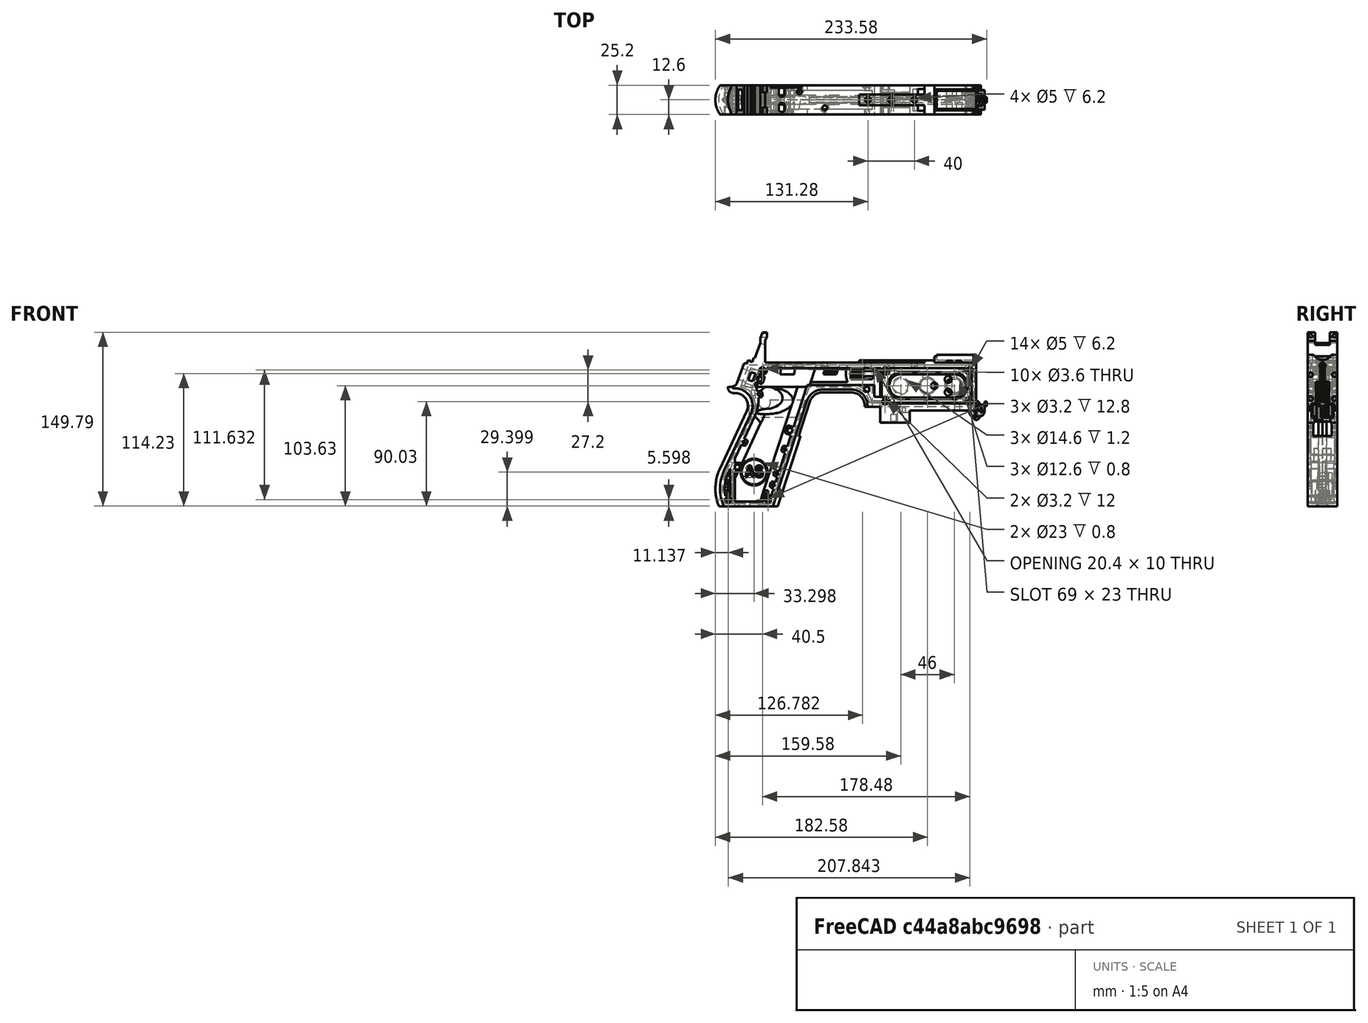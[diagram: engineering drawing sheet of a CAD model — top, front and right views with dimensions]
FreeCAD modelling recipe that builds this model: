
FCSTD DOCUMENT  (FreeCAD 1.0R39319 (Git))
Label: PICON-OF_ver_59
License: All rights reserved
LicenseURL: https://en.wikipedia.org/wiki/All_rights_reserved
objects: Sketcher::SketchObject×126, Part::Extrusion×65, Part::Cut×48, PartDesign::Pad×29, PartDesign::Pocket×21, PartDesign::Chamfer×15, PartDesign::Body×10, PartDesign::Fillet×6, Part::MultiFuse×5, Part::Part2DObjectPython×4, PartDesign::SubtractivePipe×4, PartDesign::SubtractiveLoft×4, PartDesign::Plane×3, PartDesign::SubShapeBinder×2, Part::Sweep×1, PartDesign::ShapeBinder×1, Mesh::Feature×1, PartDesign::Point×1, PartDesign::Groove×1
note: 632 computed .brp shape members not serialized (recipe doc carries the construction recipe); baked Part::Feature solids carry a one-line shape summary decoded from their .brp

FEATURE [Sketcher::SketchObject] Sketch  label="corpo principale"
  ArcFitTolerance = 1e-06
  AttacherType = Attacher::AttachEngine3D
  AttachmentSupport = -> [XZ_Plane]
  FullyConstrained = true
  MakeInternals = false
  MapMode = 5
  Placement = pos=(0,0,0) rot=(1,0,0;1.5708rad)
  sketch-geometry (65):
    g0: LineSegment StartX=0 StartY=0 StartZ=0 EndX=-57.2 EndY=0 EndZ=0
    g1: LineSegment StartX=-57.2 StartY=0 StartZ=0 EndX=-57.2 EndY=-10.4 EndZ=0
    g2: LineSegment StartX=-57.2 StartY=-10.4 StartZ=0 EndX=-82.8 EndY=-10.4 EndZ=0
    g3: LineSegment StartX=-82.8 StartY=-10.4 StartZ=0 EndX=-82.8 EndY=3.2 EndZ=0
    g4: LineSegment StartX=-82.8 StartY=3.2 StartZ=0 EndX=-93.6 EndY=3.2 EndZ=0
    g5: LineSegment StartX=-93.6 StartY=3.2 StartZ=0 EndX=-93.6 EndY=4 EndZ=0
    g6: LineSegment StartX=-107.6 StartY=18 StartZ=0 EndX=-132.428 EndY=18 EndZ=0
    g7: LineSegment StartX=-145.743 StartY=8.32624 StartZ=0 EndX=-175.232 EndY=-82.4316 EndZ=0
    g8: LineSegment StartX=-175.232 StartY=-82.4316 StartZ=0 EndX=-217.232 EndY=-82.4316 EndZ=0
    g9: LineSegment StartX=-217.232 StartY=-52.1862 StartZ=0 EndX=-193.988 EndY=-2.33927 EndZ=0
    g10: LineSegment StartX=-206.196 StartY=23.0857 StartZ=0 EndX=-199.861 EndY=40.4914 EndZ=0
    g11: LineSegment StartX=-199.861 StartY=40.4914 StartZ=0 EndX=-197.061 EndY=40.4914 EndZ=0
    g12: LineSegment StartX=-197.061 StartY=40.4914 StartZ=0 EndX=-197.061 EndY=42.8914 EndZ=0
    g13: LineSegment StartX=-197.061 StartY=42.8914 StartZ=0 EndX=-194.261 EndY=42.8914 EndZ=0
    g14: LineSegment StartX=-194.261 StartY=42.8914 StartZ=0 EndX=-194.535 EndY=42.1397 EndZ=0
    g15: LineSegment StartX=-194.535 StartY=42.1397 StartZ=0 EndX=-193.031 EndY=41.5924 EndZ=0
    g16: LineSegment StartX=-193.031 StartY=41.5924 StartZ=0 EndX=-191.663 EndY=45.3512 EndZ=0
    g17: LineSegment StartX=-191.663 StartY=45.3512 StartZ=0 EndX=-190.536 EndY=44.9408 EndZ=0
    g18: LineSegment StartX=-190.536 StartY=44.9408 StartZ=0 EndX=-185.747 EndY=58.0965 EndZ=0
    g19: LineSegment StartX=-185.747 StartY=58.0965 StartZ=0 EndX=-185.747 EndY=62.0965 EndZ=0
    g20: LineSegment StartX=-185.747 StartY=62.0965 StartZ=0 EndX=-183.832 EndY=67.3588 EndZ=0
    g21: LineSegment StartX=-183.832 StartY=67.3588 StartZ=0 EndX=-180.232 EndY=67.3588 EndZ=0
    g22: LineSegment StartX=-180.232 StartY=67.3588 StartZ=0 EndX=-180.232 EndY=63.7588 EndZ=0
    g23: LineSegment StartX=-180.232 StartY=63.7588 StartZ=0 EndX=-181.6 EndY=60 EndZ=0
    g24: LineSegment StartX=-181.6 StartY=60 StartZ=0 EndX=-181.6 EndY=41.2 EndZ=0
    g25: LineSegment StartX=-181.6 StartY=41.2 StartZ=0 EndX=-100.8 EndY=41.2 EndZ=0
    g26: LineSegment StartX=-36 StartY=43.2 StartZ=0 EndX=-36 EndY=41.2 EndZ=0
    g27: LineSegment StartX=0 StartY=48 StartZ=0 EndX=0 EndY=0 EndZ=0
    g28: LineSegment StartX=-209.901 StartY=19.85 StartZ=0 EndX=-209.901 EndY=20.1 EndZ=0
    g29: LineSegment StartX=-208.001 StartY=22 StartZ=0 EndX=-207.747 EndY=22 EndZ=0
    g30: LineSegment StartX=-207.583 StartY=19 StartZ=0 EndX=-209.051 EndY=19 EndZ=0
    g31: ArcOfCircle CenterX=-208.001 CenterY=20.1 CenterZ=0 NormalX=0 NormalY=0 NormalZ=1 AngleXU=0 Radius=1.9 StartAngle=1.5708 EndAngle=3.14159
    g32: GeomPoint [constr] X=-209.901 Y=22 Z=0
    g33: ArcOfCircle CenterX=-209.051 CenterY=19.85 CenterZ=0 NormalX=0 NormalY=0 NormalZ=1 AngleXU=0 Radius=0.85 StartAngle=3.14159 EndAngle=4.71239
    g34: GeomPoint [constr] X=-209.901 Y=19 Z=0
    g35: ArcOfCircle CenterX=-207.747 CenterY=23.65 CenterZ=0 NormalX=0 NormalY=0 NormalZ=1 AngleXU=0 Radius=1.65 StartAngle=4.71239 EndAngle=5.93412
    g36: GeomPoint [constr] X=-206.591 Y=22 Z=0
    g37: LineSegment StartX=-4 StartY=6 StartZ=0 EndX=-4 EndY=36.4 EndZ=0
    g38: LineSegment StartX=-4 StartY=36.4 StartZ=0 EndX=-185.2 EndY=36.4 EndZ=0
    g39: LineSegment StartX=-185.2 StartY=36.4 StartZ=0 EndX=-190.441 EndY=22 EndZ=0
    g40: LineSegment StartX=-214.575 StartY=-78.4316 StartZ=0 EndX=-178.142 EndY=-78.4316 EndZ=0
    g41: LineSegment StartX=-178.142 StartY=-78.4316 StartZ=0 EndX=-145.51 EndY=22 EndZ=0
    g42: LineSegment StartX=-145.51 StartY=22 StartZ=0 EndX=-87.91 EndY=22 EndZ=0
    g43: LineSegment StartX=-87.91 StartY=22 StartZ=0 EndX=-87.91 EndY=11.6 EndZ=0
    g44: LineSegment StartX=-87.91 StartY=11.6 StartZ=0 EndX=-80.11 EndY=11.6 EndZ=0
    g45: LineSegment StartX=-80.11 StartY=11.6 StartZ=0 EndX=-80.11 EndY=6 EndZ=0
    g46: LineSegment StartX=-80.11 StartY=6 StartZ=0 EndX=-4 EndY=6 EndZ=0
    g47: LineSegment StartX=-190.363 StartY=-4.02975 StartZ=0 EndX=-213.607 EndY=-53.8767 EndZ=0
    g48: ArcOfCircle CenterX=-132.428 CenterY=4 CenterZ=0 NormalX=0 NormalY=0 NormalZ=1 AngleXU=0 Radius=14 StartAngle=1.5708 EndAngle=2.82743
    g49: GeomPoint [constr] X=-142.6 Y=18 Z=0
    g50: ArcOfCircle CenterX=-107.6 CenterY=4 CenterZ=0 NormalX=0 NormalY=0 NormalZ=1 AngleXU=0 Radius=14 StartAngle=0 EndAngle=1.5708
    g51: GeomPoint [constr] X=-93.6 Y=18 Z=0
    g52: ArcOfCircle CenterX=-184.801 CenterY=-67.3089 CenterZ=0 NormalX=0 NormalY=0 NormalZ=1 AngleXU=0 Radius=35.7833 StartAngle=2.70526 EndAngle=3.57792
    g53: ArcOfCircle CenterX=-207.583 CenterY=4 CenterZ=0 NormalX=0 NormalY=0 NormalZ=1 AngleXU=0 Radius=15 StartAngle=5.84685 EndAngle=7.85398
    g54: LineSegment [constr] StartX=-213.607 StartY=-53.8767 StartZ=0 EndX=-217.232 EndY=-52.1862 EndZ=0
    g55: ArcOfCircle CenterX=-184.801 CenterY=-67.3089 CenterZ=0 NormalX=0 NormalY=0 NormalZ=1 AngleXU=0 Radius=31.7833 StartAngle=2.70526 EndAngle=3.49911
    g56: ArcOfCircle CenterX=-218.095 CenterY=8.90192 CenterZ=0 NormalX=0 NormalY=0 NormalZ=1 AngleXU=0 Radius=30.5989 StartAngle=5.84685 EndAngle=6.72553
    g57: LineSegment StartX=-44.6 StartY=43.2 StartZ=0 EndX=-36 EndY=43.2 EndZ=0
    g58: LineSegment StartX=-100.8 StartY=41.2 StartZ=0 EndX=-44.6 EndY=41.2 EndZ=0
    g59: LineSegment StartX=-44.6 StartY=41.2 StartZ=0 EndX=-44.6 EndY=43.2 EndZ=0
    g60: LineSegment StartX=-2.4 StartY=48 StartZ=0 EndX=0 EndY=48 EndZ=0
    g61: LineSegment StartX=-36 StartY=41.2 StartZ=0 EndX=-2.4 EndY=41.2 EndZ=0
    g62: LineSegment StartX=-2.4 StartY=41.2 StartZ=0 EndX=-2.4 EndY=48 EndZ=0
    g63: LineSegment [constr] StartX=-181.6 StartY=36.4 StartZ=0 EndX=-152.209 EndY=36.4 EndZ=0
    g64: LineSegment [constr] StartX=-181.6 StartY=36.4 StartZ=0 EndX=-130.41 EndY=36.4 EndZ=0
  constraints (183):
    c: Coincident(g-1,g0)
    c: PointOnObject(g0,g-1)
    c: Coincident(g0,g1)
    c: Vertical(g1)
    c: Coincident(g1,g2)
    c: Horizontal(g2)
    c: Coincident(g2,g3)
    c: Vertical(g3)
    c: Coincident(g3,g4)
    c: Coincident(g4,g5)
    c: Vertical(g5)
    c: Horizontal(g6)
    c: Coincident(g7,g8)
    c: Horizontal(g8)
    c: Coincident(g10,g11)
    c: Horizontal(g11)
    c: Coincident(g11,g12)
    c: Vertical(g12)
    c: Coincident(g12,g13)
    c: Horizontal(g13)
    c: Coincident(g13,g14)
    c: Coincident(g14,g15)
    c: Coincident(g15,g16)
    c: Coincident(g16,g17)
    c: Coincident(g17,g18)
    c: Coincident(g18,g19)
    c: Vertical(g19)
    c: Coincident(g19,g20)
    c: Coincident(g20,g21)
    c: Horizontal(g21)
    c: Coincident(g21,g22)
    c: Vertical(g22)
    c: Coincident(g22,g23)
    c: Coincident(g23,g24)
    c: Vertical(g24)
    c: Coincident(g24,g25)
    c: Horizontal(g25)
    c: Coincident(g57,g26)
    c: Vertical(g26)
    c: Coincident(g26,g61)
    c: PointOnObject(g60,g-2)
    c: Coincident(g60,g27)
    c: Coincident(g27,g0)
    c: DistanceY(g27,g27) = 48
    c: DistanceY(g1,g1) = 10.4
    c: DistanceX(g0,g0) = 57.2
    c: DistanceX(g2,g2) = 25.6
    c: Horizontal(g4)
    c: DistanceY(g3,g3) = 13.6
    c: DistanceX(g4,g4) = 10.8
    c: DistanceY(g5,g51) = 14.8
    c: DistanceX(g49,g51) = 49
    c: Distance(g7,g49) = 105.6
    c: DistanceX(g61,g60) = 36
    c: DistanceX(g25,g25) = 80.8
    c: DistanceY(g24,g24) = 18.8
    c: DistanceY(g22,g22) = 3.6
    c: Distance(g23) = 4
    c: Angle(g-1,g23) = 1.22173
    c: DistanceX(g21,g21) = 3.6
    c: Distance(g20) = 5.6
    c: Angle(g-1,g20) = 1.22173
    c: DistanceY(g19,g19) = 4
    c: Distance(g18) = 14
    c: Angle(g-1,g18) = 1.22173
    c: Distance(g17) = 1.2
    c: Distance(g16) = 4
    c: Angle(g16) = 1.22173
    c: Perpendicular(g18,g17)
    c: Distance(g15) = 1.6
    c: Perpendicular(g16,g15)
    c: Distance(g14) = 0.8
    c: DistanceX(g13,g13) = 2.8
    c: Perpendicular(g15,g14)
    c: DistanceY(g12,g12) = 2.4
    c: DistanceX(g11,g11) = 2.8
    c: Distance(g9) = 55
    c: Angle(g9,g-1) = 2.00713
    c: Horizontal(g29)
    c: Vertical(g28)
    c: Horizontal(g30)
    c: PointOnObject(g32,g29)
    c: PointOnObject(g32,g28)
    c: Tangent(g29,g31) = 1.5708
    c: Tangent(g28,g31) = 1.5708
    c: PointOnObject(g34,g28)
    c: PointOnObject(g34,g30)
    c: Tangent(g28,g33) = 1.5708
    c: Tangent(g30,g33) = 1.5708
    c: PointOnObject(g36,g29)
    c: PointOnObject(g36,g10)
    c: Tangent(g29,g35) = -1.5708
    c: Tangent(g10,g35) = -1.5708
    c: Angle(g-1,g10) = 1.22173
    c: Radius(g35) = 1.65
    c: Vertical(g37)
    c: Coincident(g37,g38)
    c: Horizontal(g38)
    c: Coincident(g38,g39)
    c: Horizontal(g40)
    c: Coincident(g40,g41)
    c: Coincident(g41,g42)
    c: Horizontal(g42)
    c: Coincident(g42,g43)
    c: Vertical(g43)
    c: Coincident(g43,g44)
    c: Horizontal(g44)
    c: Coincident(g44,g45)
    c: Vertical(g45)
    c: Coincident(g45,g46)
    c: Coincident(g46,g37)
    c: Horizontal(g46)
    c: DistanceY(g0,g37) = 6
    c: DistanceX(g37,g0) = 4
    c: DistanceY(g37,g25) = 4.8
    c: DistanceX(g38,g38) = 181.2
    c: DistanceX(g42,g42) = 57.6
    c: DistanceY(g49,g41) = 4
    c: DistanceX(g41,g49) = 2.91
    c: DistanceY(g43,g43) = 10.4
    c: DistanceX(g44,g44) = 7.8
    c: DistanceY(g7,g40) = 4
    c: Distance(g47) = 55
    c: Angle(g-1,g39) = 1.22173
    c: PointOnObject(g49,g7)
    c: PointOnObject(g49,g6)
    c: Tangent(g7,g48) = -1.5708
    c: Tangent(g6,g48) = -1.5708
    c: PointOnObject(g51,g5)
    c: PointOnObject(g51,g6)
    c: Tangent(g5,g50) = -1.5708
    c: Tangent(g6,g50) = -1.5708
    c: Radius(g50) = 14
    c: Radius(g48) = 14
    c: DistanceX(g8,g8) = 42
    c: Angle(g7,g-1) = 1.88496
    c: Parallel(g41,g7)
    c: Parallel(g47,g9)
    c: Coincident(g52,g8)
    c: Tangent(g52,g9) = 1.5708
    c: DistanceX(g9,g8) = 0
    c: Tangent(g53,g9) = -1.5708
    c: Tangent(g53,g30) = -1.5708
    c: Diameter(g53) = 30
    c: DistanceY(g53,g0) = -4
    c: Coincident(g54,g47)
    c: Distance(g54) = 4
    c: Coincident(g54,g9)
    c: Coincident(g55,g40)
    c: Tangent(g55,g47) = -1.5708
    c: Coincident(g52,g55)
    c: Coincident(g56,g39)
    c: Tangent(g56,g47) = 1.5708
    c: Horizontal(g57)
    c: DistanceX(g57,g57) = 8.6
    c: Coincident(g58,g25)
    c: Horizontal(g58)
    c: Coincident(g59,g58)
    c: Vertical(g59)
    c: DistanceY(g58,g57) = 2
    c: DistanceX(g58,g58) = 56.2
    c: Coincident(g59,g57)
    c: DistanceY(g41,g36) = 0
    c: DistanceY(g36,g39) = 0
    c: DistanceY(g28,g28) = 0.25
    c: DistanceX(g30,g36) = 2.46
    c: DistanceX(g28,g29) = 1.9
    c: Coincident(g62,g60)
    c: Horizontal(g60)
    c: DistanceX(g62,g27) = 2.4
    c: Coincident(g61,g62)
    c: DistanceY(g26,g26) = 2
    c: Vertical(g62)
    c: DistanceY(g61,g60) = 6.8
    c: Horizontal(g61)
    c: Distance(g63) = 29.391
    c: PointOnObject(g63,g38)
    c: PointOnObject(g63,g38)
    c: Distance(g64) = 51.19
    c: PointOnObject(g64,g38)
    c: PointOnObject(g64,g38)
    c: DistanceX(g24,g63) = 0
    c: DistanceX(g24,g64) = 0
FEATURE [Part::Extrusion] Extrude  label="Extrude corpo principale"
  Base = -> Sketch
  Dir = (0,-1,2e-16)
  DirMode = 2
  FaceMakerClass = Part::FaceMakerBullseye
  FaceMakerMode = 3
  LengthFwd = 25.2
  LengthRev = 12.6
  Solid = true
  Symmetric = true
FEATURE [Sketcher::SketchObject] Sketch002  label="scavo grilletto"
  ArcFitTolerance = 1e-06
  AttachmentSupport = -> [XZ_Plane]
  ExternalGeometry = -> [Sketch]
  FullyConstrained = true
  MakeInternals = false
  MapMode = 5
  Placement = pos=(0,0,0) rot=(1,0,0;1.5708rad)
  sketch-geometry (4):
    g0: LineSegment StartX=-89.51 StartY=22 StartZ=0 EndX=-152.71 EndY=22 EndZ=0
    g1: LineSegment StartX=-152.71 StartY=22 StartZ=0 EndX=-167.006 EndY=-22 EndZ=0
    g2: LineSegment StartX=-167.006 StartY=-22 StartZ=0 EndX=-89.51 EndY=-22 EndZ=0
    g3: LineSegment StartX=-89.51 StartY=-22 StartZ=0 EndX=-89.51 EndY=22 EndZ=0
  constraints (12):
    c: Horizontal(g0)
    c: Coincident(g0,g1)
    c: Coincident(g1,g2)
    c: Horizontal(g2)
    c: Coincident(g2,g3)
    c: Coincident(g3,g0)
    c: Vertical(g3)
    c: Angle(g1,g0) = 1.88496
    c: DistanceY(g3,g3) = 44
    c: DistanceX(g0,g0) = 63.2
    c: DistanceX(g0,g-3) = 1.6
    c: DistanceY(g-3,g0) = 0
FEATURE [Sketcher::SketchObject] Sketch004  label="traiettoria arrotondamento impugnatura anteriore"
  ArcFitTolerance = 1e-06
  AttachmentSupport = -> [XZ_Plane]
  ExternalGeometry = -> [Sketch]
  FullyConstrained = true
  MakeInternals = false
  MapMode = 5
  Placement = pos=(0,0,0) rot=(1,0,0;1.5708rad)
  sketch-geometry (13):
    g0: LineSegment StartX=-175.232 StartY=-82.4316 StartZ=0 EndX=-145.743 EndY=8.32624 EndZ=0
    g1: LineSegment StartX=-93.6 StartY=3.2 StartZ=0 EndX=-93.6 EndY=4 EndZ=0
    g2: LineSegment StartX=-132.428 StartY=18 StartZ=0 EndX=-107.6 EndY=18 EndZ=0
    g3: ArcOfCircle CenterX=-132.428 CenterY=4 CenterZ=0 NormalX=0 NormalY=0 NormalZ=1 AngleXU=0 Radius=14 StartAngle=1.5708 EndAngle=2.82743
    g4: ArcOfCircle CenterX=-107.6 CenterY=4 CenterZ=0 NormalX=0 NormalY=0 NormalZ=1 AngleXU=0 Radius=14 StartAngle=0 EndAngle=1.5708
    g5: LineSegment StartX=-175.232 StartY=-82.4316 StartZ=0 EndX=-217.232 EndY=-82.4316 EndZ=0
    g6: LineSegment StartX=-217.232 StartY=-52.1862 StartZ=0 EndX=-193.988 EndY=-2.33927 EndZ=0
    g7: LineSegment StartX=-209.051 StartY=19 StartZ=0 EndX=-207.583 EndY=19 EndZ=0
    g8: LineSegment StartX=-209.901 StartY=20.1 StartZ=0 EndX=-209.901 EndY=19.85 EndZ=0
    g9: ArcOfCircle CenterX=-184.801 CenterY=-67.3089 CenterZ=0 NormalX=0 NormalY=0 NormalZ=1 AngleXU=0 Radius=35.7833 StartAngle=2.70526 EndAngle=3.57792
    g10: ArcOfCircle CenterX=-207.583 CenterY=4 CenterZ=0 NormalX=0 NormalY=0 NormalZ=1 AngleXU=0 Radius=15 StartAngle=5.84685 EndAngle=7.85398
    g11: ArcOfCircle CenterX=-209.051 CenterY=19.85 CenterZ=0 NormalX=0 NormalY=0 NormalZ=1 AngleXU=0 Radius=0.85 StartAngle=3.14159 EndAngle=4.71239
    g12: ArcOfCircle CenterX=-208.001 CenterY=20.1 CenterZ=0 NormalX=0 NormalY=0 NormalZ=1 AngleXU=0 Radius=1.9 StartAngle=1.5708 EndAngle=3.14159
  constraints (26):
    c: Coincident(g0,g-3)
    c: Coincident(g0,g-6)
    c: Coincident(g1,g-8)
    c: Coincident(g1,g-7)
    c: Coincident(g2,g-5)
    c: Coincident(g2,g-4)
    c: Coincident(g3,g2)
    c: Tangent(g3,g0) = 1.5708
    c: Coincident(g4,g1)
    c: Tangent(g4,g2) = 1.5708
    c: Coincident(g5,g0)
    c: Coincident(g5,g-9)
    c: Coincident(g6,g-12)
    c: Coincident(g6,g-11)
    c: Coincident(g7,g-15)
    c: Coincident(g7,g-14)
    c: Coincident(g8,g-16)
    c: Coincident(g8,g-17)
    c: Tangent(g9,g6) = 1.5708
    c: Coincident(g9,g5)
    c: Coincident(g10,g7)
    c: Tangent(g10,g6) = -1.5708
    c: Tangent(g11,g7) = -1.5708
    c: Coincident(g11,g8)
    c: Tangent(g12,g8) = -1.5708
    c: Coincident(g12,g-17)
FEATURE [PartDesign::Plane] DatumPlane  label="Piano per disegno arrotondamento impugnatura"
  AttachmentSupport = -> [Sketch]
  Length = 73.6581
  MapMode = 7
  Placement = pos=(-145.743,1.8e-15,8.32624) rot=(0.154555,0.154555,0.97582;1.59527rad)
  ResizeMode = 0
  Width = 303.511
FEATURE [Sketcher::SketchObject] Sketch005  label="forma arrotondamento impugnatura anteriore"
  ArcFitTolerance = 1e-06
  AttachmentSupport = -> [DatumPlane]
  FullyConstrained = true
  MakeInternals = false
  MapMode = 5
  Placement = pos=(-145.743,1.8e-15,8.32624) rot=(0.154555,0.154555,0.97582;1.59527rad)
  sketch-geometry (5):
    g0: GeomPoint [constr] X=0 Y=-4 Z=0
    g1: GeomPoint [constr] X=-12.6 Y=7.1e-15 Z=0
    g2: GeomPoint [constr] X=12.6 Y=4.97e-14 Z=0
    g3: LineSegment StartX=-12.6 StartY=7.1e-15 StartZ=0 EndX=12.6 EndY=4.97e-14 EndZ=0
    g4: ArcOfCircle CenterX=-3.88e-14 CenterY=17.845 CenterZ=0 NormalX=0 NormalY=0 NormalZ=1 AngleXU=0 Radius=21.845 StartAngle=4.09759 EndAngle=5.32718
  constraints (11):
    c: DistanceY(g0,g-1) = 4
    c: DistanceX(g-1,g0) = 0
    c: DistanceX(g1,g-1) = 12.6
    c: DistanceX(g-1,g2) = 12.6
    c: DistanceY(g-1,g2) = 0
    c: DistanceY(g-1,g1) = 0
    c: Coincident(g3,g1)
    c: Coincident(g3,g2)
    c: Coincident(g4,g1)
    c: Coincident(g4,g2)
    c: PointOnObject(g0,g4)
FEATURE [Part::Sweep] Sweep  label="Sweep impugnatura"
  Frenet = true
  Sections = -> [Sketch005]
  Solid = true
  Spine = -> Sketch [Edge32,Edge33,Edge34,Edge35,Edge36,Edge37,Edge38,Edge39,Edge40,Edge41,Edge42,Edge43,Edge44]
  Transition = 1
FEATURE [Sketcher::SketchObject] Sketch008  label="buchi e pulizie varie"
  ArcFitTolerance = 1e-06
  AttachmentSupport = -> [XZ_Plane]
  ExternalGeometry = -> [Sketch]
  FullyConstrained = true
  MakeInternals = false
  MapMode = 5
  Placement = pos=(0,0,0) rot=(1,0,0;1.5708rad)
  sketch-geometry (26):
    g0: LineSegment StartX=-96.278 StartY=20.155 StartZ=0 EndX=-92.278 EndY=20.155 EndZ=0
    g1: LineSegment StartX=-92.278 StartY=20.155 StartZ=0 EndX=-92.278 EndY=16.155 EndZ=0
    g2: LineSegment StartX=-92.278 StartY=16.155 StartZ=0 EndX=-96.278 EndY=16.155 EndZ=0
    g3: LineSegment StartX=-96.278 StartY=16.155 StartZ=0 EndX=-96.278 EndY=20.155 EndZ=0
    g4: LineSegment StartX=-222.232 StartY=-82.4316 StartZ=0 EndX=-170.232 EndY=-82.4316 EndZ=0
    g5: LineSegment StartX=-170.232 StartY=-82.4316 StartZ=0 EndX=-170.232 EndY=-86.4316 EndZ=0
    g6: LineSegment StartX=-170.232 StartY=-86.4316 StartZ=0 EndX=-222.232 EndY=-86.4316 EndZ=0
    g7: LineSegment StartX=-222.232 StartY=-86.4316 StartZ=0 EndX=-222.232 EndY=-82.4316 EndZ=0
    g8: LineSegment StartX=-213.901 StartY=20.1 StartZ=0 EndX=-213.901 EndY=26 EndZ=0
    g9: LineSegment StartX=-213.901 StartY=26 StartZ=0 EndX=-206.196 EndY=26 EndZ=0
    g10: LineSegment StartX=-17.4 StartY=42.8 StartZ=0 EndX=-12.4 EndY=42.8 EndZ=0
    g11: LineSegment StartX=-12.4 StartY=42.8 StartZ=0 EndX=-12.4 EndY=41.2 EndZ=0
    g12: LineSegment StartX=-12.4 StartY=41.2 StartZ=0 EndX=-17.4 EndY=41.2 EndZ=0
    g13: LineSegment StartX=-17.4 StartY=41.2 StartZ=0 EndX=-17.4 EndY=42.8 EndZ=0
    g14: LineSegment StartX=-25.9 StartY=42.8 StartZ=0 EndX=-20.9 EndY=42.8 EndZ=0
    g15: LineSegment StartX=-20.9 StartY=42.8 StartZ=0 EndX=-20.9 EndY=41.2 EndZ=0
    g16: LineSegment StartX=-20.9 StartY=41.2 StartZ=0 EndX=-25.9 EndY=41.2 EndZ=0
    g17: LineSegment StartX=-25.9 StartY=41.2 StartZ=0 EndX=-25.9 EndY=42.8 EndZ=0
    g18: GeomPoint [constr] X=-206.196 Y=23.0857 Z=0
    g19: GeomPoint [constr] X=-213.901 Y=20.1 Z=0
    g20: BSplineCurve PolesCount=4 KnotsCount=2 Degree=3 IsPeriodic=0
    g21-g24: Circle [constr] x4 (B-spline internal-alignment scaffolding for g20; pole/knot coordinates omitted)
    g25: LineSegment StartX=-206.196 StartY=26 StartZ=0 EndX=-206.196 EndY=23.0857 EndZ=0
  constraints (73):
    c: Horizontal(g0)
    c: Coincident(g1,g0)
    c: Vertical(g1)
    c: Coincident(g2,g1)
    c: Horizontal(g2)
    c: Coincident(g3,g2)
    c: Coincident(g3,g0)
    c: Vertical(g3)
    c: DistanceX(g0,g-4) = 4.368
    c: DistanceY(g0,g-4) = 1.845
    c: DistanceY(g1,g1) = 4
    c: DistanceX(g2,g2) = 4
    c: Horizontal(g4)
    c: Coincident(g5,g4)
    c: Vertical(g5)
    c: Coincident(g6,g5)
    c: Horizontal(g6)
    c: Coincident(g7,g6)
    c: Coincident(g7,g4)
    c: Vertical(g7)
    c: DistanceY(g7,g7) = 4
    c: DistanceX(g4,g-5) = 5
    c: DistanceX(g-5,g4) = 5
    c: DistanceY(g4,g-5) = 0
    c: Coincident(g9,g8)
    c: Parallel(g9,g-6)
    c: DistanceX(g8,g-8) = 4
    c: Horizontal(g10)
    c: Coincident(g11,g10)
    c: Vertical(g11)
    c: Coincident(g12,g11)
    c: Horizontal(g12)
    c: Coincident(g13,g12)
    c: Coincident(g13,g10)
    c: Vertical(g13)
    c: Horizontal(g14)
    c: Coincident(g15,g14)
    c: Vertical(g15)
    c: Coincident(g16,g15)
    c: Horizontal(g16)
    c: Coincident(g17,g16)
    c: Coincident(g17,g14)
    c: Vertical(g17)
    c: DistanceY(g11,g10) = 1.6
    c: DistanceX(g10,g10) = 5
    c: DistanceY(g15,g14) = 1.6
    c: DistanceX(g14,g14) = 5
    c: DistanceX(g15,g12) = 3.5
    c: DistanceX(g11,g-9) = 10
    c: DistanceY(g-9,g11) = 0
    c: DistanceY(g-9,g15) = 0
    c: Perpendicular(g8,g9)
    c: DistanceY(g-7,g9) = 4
    c: DistanceY(g8,g-8) = 0
    c: InternalAlignment(g18,g20)
    c: InternalAlignment(g19,g20)
    c: InternalAlignment(g21,g20)
    c: Weight(g21) = 1
    c: InternalAlignment(g22,g20)
    c: Equal(g22,g21)
    c: InternalAlignment(g23,g20)
    c: Equal(g23,g21)
    c: InternalAlignment(g24,g20)
    c: Equal(g24,g21)
    c: Coincident(g18,g-12)
    c: Coincident(g19,g8)
    c: Coincident(g25,g9)
    c: Coincident(g25,g20)
    c: Vertical(g25)
    c: DistanceY(g20,g23) = 0
    c: DistanceY(g22,g18) = 2.26
    c: DistanceX(g22,g18) = 0.93
    c: DistanceX(g20,g23) = 2.9
FEATURE [Part::Extrusion] Extrude004  label="Extrude Buchi e pulizie varie"
  Base = -> Sketch008
  Dir = (0,-1,2e-16)
  DirMode = 2
  FaceMakerClass = Part::FaceMakerBullseye
  FaceMakerMode = 3
  LengthFwd = 25.2
  LengthRev = 0
  Solid = true
  Symmetric = true
FEATURE [Sketcher::SketchObject] Sketch009  label="rinforzi"
  ArcFitTolerance = 1e-06
  AttachmentSupport = -> [XZ_Plane]
  ExternalGeometry = -> [Sketch]
  FullyConstrained = true
  MakeInternals = false
  MapMode = 5
  Placement = pos=(0,0,0) rot=(1,0,0;1.5708rad)
  sketch-geometry (9):
    g0: LineSegment StartX=-87.91 StartY=22 StartZ=0 EndX=-87.91 EndY=36.4 EndZ=0
    g1: LineSegment StartX=-87.91 StartY=36.4 StartZ=0 EndX=-97.91 EndY=36.4 EndZ=0
    g2: LineSegment StartX=-97.91 StartY=36.4 StartZ=0 EndX=-97.91 EndY=22 EndZ=0
    g3: LineSegment StartX=-97.91 StartY=22 StartZ=0 EndX=-87.91 EndY=22 EndZ=0
    g4: LineSegment StartX=-149.713 StartY=9.06563 StartZ=0 EndX=-154.586 EndY=-5.93437 EndZ=0
    g5: LineSegment StartX=-154.586 StartY=-5.93437 StartZ=0 EndX=-191.863 EndY=-5.93437 EndZ=0
    g6: LineSegment StartX=-191.863 StartY=-5.93437 StartZ=0 EndX=-191.863 EndY=9.06563 EndZ=0
    g7: LineSegment StartX=-191.863 StartY=9.06563 StartZ=0 EndX=-149.713 EndY=9.06563 EndZ=0
    g8: LineSegment [constr] StartX=-145.51 StartY=22 StartZ=0 EndX=-149.713 EndY=9.06563 EndZ=0
  constraints (25):
    c: Vertical(g0)
    c: Coincident(g1,g0)
    c: Horizontal(g1)
    c: Coincident(g2,g1)
    c: Vertical(g2)
    c: Coincident(g3,g2)
    c: Coincident(g3,g0)
    c: Horizontal(g3)
    c: Coincident(g0,g-4)
    c: DistanceX(g3,g3) = 10
    c: DistanceY(g0,g-3) = 0
    c: Coincident(g5,g4)
    c: Horizontal(g5)
    c: Coincident(g6,g5)
    c: Vertical(g6)
    c: Coincident(g7,g6)
    c: Coincident(g7,g4)
    c: Horizontal(g7)
    c: Distance(g8) = 13.6
    c: Parallel(g-6,g8)
    c: Coincident(g-6,g8)
    c: Parallel(g4,g-6)
    c: DistanceY(g4,g4) = 15
    c: Coincident(g4,g8)
    c: DistanceX(g-5,g5) = -1.5
FEATURE [Part::Extrusion] Extrude001  label="Extrude scavo grilletto"
  Base = -> Sketch002
  Dir = (0,-1,2e-16)
  DirMode = 2
  FaceMakerClass = Part::FaceMakerBullseye
  FaceMakerMode = 3
  LengthFwd = 16
  LengthRev = 0
  Solid = true
  Symmetric = true
FEATURE [Part::Extrusion] Extrude005  label="Extrude Rinforzi"
  Base = -> Sketch009
  Dir = (0,-1,2e-16)
  DirMode = 2
  FaceMakerClass = Part::FaceMakerBullseye
  FaceMakerMode = 3
  LengthFwd = 2
  LengthRev = 0
  Placement = pos=(0,12.6,0) rot=(0,0,1;0rad)
  Solid = true
  Symmetric = false
FEATURE [PartDesign::ShapeBinder] CopyCut
  TraceSupport = false
FEATURE [PartDesign::Plane] DatumPlane001
  AttachmentSupport = -> [CopyCut]
  Length = 283.944
  MapMode = 5
  Placement = pos=(0,12.6,0) rot=(0,0.707107,0.707107;3.14159rad)
  ResizeMode = 0
  Width = 188.15
FEATURE [Sketcher::SketchObject] Sketch010  label="buco neopixel"
  ArcFitTolerance = 1e-06
  AttachmentSupport = -> [XZ_Plane]
  ExternalGeometry = -> [Sketch]
  FullyConstrained = true
  MakeInternals = false
  MapMode = 5
  Placement = pos=(0,0,0) rot=(1,0,0;1.5708rad)
  sketch-geometry (5):
    g0: LineSegment [constr] StartX=-199.861 StartY=40.4914 StartZ=0 EndX=-201.368 EndY=36.3521 EndZ=0
    g1: LineSegment StartX=-201.368 StartY=36.3521 StartZ=0 EndX=-204.932 EndY=26.5605 EndZ=0
    g2: LineSegment StartX=-201.368 StartY=36.3521 StartZ=0 EndX=-180.2 EndY=28.6477 EndZ=0
    g3: LineSegment StartX=-180.2 StartY=28.6477 StartZ=0 EndX=-183.764 EndY=18.8561 EndZ=0
    g4: LineSegment StartX=-183.764 StartY=18.8561 StartZ=0 EndX=-204.932 EndY=26.5605 EndZ=0
  constraints (14):
    c: Parallel(g0,g-3)
    c: Distance(g0) = 4.405
    c: Coincident(g0,g-3)
    c: Coincident(g2,g1)
    c: Coincident(g3,g2)
    c: Coincident(g4,g3)
    c: Coincident(g4,g1)
    c: Parallel(g1,g-3)
    c: Distance(g1) = 10.42
    c: Coincident(g1,g0)
    c: Parallel(g2,g4)
    c: Perpendicular(g1,g2)
    c: DistanceX(g-4,g2) = 5
    c: Parallel(g3,g1)
FEATURE [Part::Extrusion] Extrude006  label="Extrude buco neopixel"
  Base = -> Sketch010
  Dir = (0,-1,2e-16)
  DirMode = 2
  FaceMakerClass = Part::FaceMakerBullseye
  FaceMakerMode = 3
  LengthFwd = 17.2
  LengthRev = 0
  Solid = true
  Symmetric = true
FEATURE [Sketcher::SketchObject] Sketch011  label="fermo grilletto"
  ArcFitTolerance = 1e-06
  AttachmentSupport = -> [XZ_Plane]
  ExternalGeometry = -> [Sketch]
  FullyConstrained = true
  MakeInternals = false
  MapMode = 5
  Placement = pos=(0,0,0) rot=(1,0,0;1.5708rad)
  sketch-geometry (18):
    g0: LineSegment [constr] StartX=-145.51 StartY=22 StartZ=0 EndX=-157.347 EndY=-14.4293 EndZ=0
    g1: LineSegment [constr] StartX=-157.347 StartY=-14.4293 StartZ=0 EndX=-157.841 EndY=-15.951 EndZ=0
    g2: LineSegment StartX=-161.151 StartY=-13.1932 StartZ=0 EndX=-155.825 EndY=-14.9237 EndZ=0
    g3: LineSegment StartX=-163.167 StartY=-14.2205 StartZ=0 EndX=-164.403 EndY=-18.0247 EndZ=0
    g4: LineSegment StartX=-163.376 StartY=-20.0408 StartZ=0 EndX=-158.05 EndY=-21.7713 EndZ=0
    g5: LineSegment StartX=-158.05 StartY=-21.7713 StartZ=0 EndX=-155.825 EndY=-14.9237 EndZ=0
    g6: LineSegment StartX=-161.645 StartY=-14.7149 StartZ=0 EndX=-157.841 EndY=-15.951 EndZ=0
    g7: LineSegment StartX=-157.841 StartY=-15.951 StartZ=0 EndX=-159.077 EndY=-19.7552 EndZ=0
    g8: LineSegment StartX=-159.077 StartY=-19.7552 StartZ=0 EndX=-162.881 EndY=-18.5191 EndZ=0
    g9: LineSegment StartX=-162.881 StartY=-18.5191 StartZ=0 EndX=-161.645 EndY=-14.7149 EndZ=0
    g10: LineSegment [constr] StartX=-161.645 StartY=-14.7149 StartZ=0 EndX=-161.151 EndY=-13.1932 EndZ=0
    g11: LineSegment [constr] StartX=-159.077 StartY=-19.7552 StartZ=0 EndX=-157.555 EndY=-20.2496 EndZ=0
    g12: LineSegment [constr] StartX=-159.077 StartY=-19.7552 StartZ=0 EndX=-159.572 EndY=-21.2769 EndZ=0
    g13: LineSegment [constr] StartX=-161.645 StartY=-14.7149 StartZ=0 EndX=-163.167 EndY=-14.2205 EndZ=0
    g14: ArcOfCircle CenterX=-161.645 CenterY=-14.7149 CenterZ=0 NormalX=0 NormalY=0 NormalZ=1 AngleXU=0 Radius=1.6 StartAngle=1.25664 EndAngle=2.82743
    g15: GeomPoint [constr] X=-162.673 Y=-12.6988 Z=0
    g16: ArcOfCircle CenterX=-162.881 CenterY=-18.5191 CenterZ=0 NormalX=0 NormalY=0 NormalZ=1 AngleXU=0 Radius=1.6 StartAngle=2.82743 EndAngle=4.39823
    g17: GeomPoint [constr] X=-164.897 Y=-19.5464 Z=0
  constraints (48):
    c: Parallel(g0,g-3)
    c: Distance(g0) = 38.304
    c: Coincident(g0,g-3)
    c: Parallel(g1,g-3)
    c: Distance(g1) = 1.6
    c: Coincident(g1,g0)
    c: Coincident(g5,g4)
    c: Coincident(g5,g2)
    c: Coincident(g7,g6)
    c: Coincident(g8,g7)
    c: Coincident(g9,g8)
    c: Coincident(g9,g6)
    c: Parallel(g7,g-3)
    c: Parallel(g9,g7)
    c: Perpendicular(g6,g7)
    c: Parallel(g6,g8)
    c: Distance(g6) = 4
    c: Distance(g9) = 4
    c: Parallel(g5,g7)
    c: Parallel(g9,g3)
    c: Parallel(g2,g6)
    c: Parallel(g4,g8)
    c: Parallel(g13,g6)
    c: Parallel(g10,g9)
    c: Parallel(g11,g8)
    c: Parallel(g12,g7)
    c: Distance(g10) = 1.6
    c: Distance(g13) = 1.6
    c: Distance(g12) = 1.6
    c: Distance(g11) = 1.6
    c: Coincident(g10,g6)
    c: Coincident(g13,g6)
    c: Coincident(g12,g7)
    c: Coincident(g11,g7)
    c: Distance(g10,g15) = 1.6
    c: Distance(g15,g13) = 1.6
    c: Distance(g4,g12) = 1.6
    c: Distance(g4,g11) = 1.6
    c: PointOnObject(g15,g2)
    c: Tangent(g3,g14) = -1.5708
    c: Tangent(g2,g14) = 1.5708
    c: PointOnObject(g17,g4)
    c: PointOnObject(g17,g3)
    c: Tangent(g4,g16) = -1.5708
    c: Tangent(g3,g16) = -1.5708
    c: Equal(g16,g14)
    c: Coincident(g16,g8)
    c: Coincident(g6,g1)
FEATURE [Part::Extrusion] Extrude007  label="Extrude fermo grilletto"
  Base = -> Sketch011
  Dir = (0,-1,2e-16)
  DirMode = 2
  FaceMakerClass = Part::FaceMakerBullseye
  FaceMakerMode = 3
  LengthFwd = 25.2
  LengthRev = 0
  Solid = true
  Symmetric = true
FEATURE [Sketcher::SketchObject] Sketch012  label="buco oled"
  ArcFitTolerance = 1e-06
  AttachmentSupport = -> [XZ_Plane]
  ExternalGeometry = -> [Sketch]
  FullyConstrained = true
  MakeInternals = false
  MapMode = 5
  Placement = pos=(0,0,0) rot=(1,0,0;1.5708rad)
  sketch-geometry (4):
    g0: LineSegment StartX=-185.747 StartY=58.0965 StartZ=0 EndX=-180.232 EndY=56.0891 EndZ=0
    g1: LineSegment StartX=-185.747 StartY=58.0965 StartZ=0 EndX=-185.747 EndY=67.3588 EndZ=0
    g2: LineSegment StartX=-185.747 StartY=67.3588 StartZ=0 EndX=-180.232 EndY=67.3588 EndZ=0
    g3: LineSegment StartX=-180.232 StartY=67.3588 StartZ=0 EndX=-180.232 EndY=56.0891 EndZ=0
  constraints (10):
    c: Coincident(g1,g0)
    c: Coincident(g2,g1)
    c: Coincident(g3,g2)
    c: Coincident(g3,g0)
    c: Parallel(g1,g-5)
    c: Perpendicular(g-3,g0)
    c: Parallel(g2,g-6)
    c: Parallel(g3,g-4)
    c: Coincident(g0,g-5)
    c: Coincident(g2,g-6)
FEATURE [Part::Extrusion] Extrude008  label="Extrude buco oled"
  Base = -> Sketch012
  Dir = (0,-1,2e-16)
  DirMode = 2
  FaceMakerClass = Part::FaceMakerBullseye
  FaceMakerMode = 3
  LengthFwd = 12.8
  LengthRev = 0
  Solid = true
  Symmetric = true
FEATURE [Sketcher::SketchObject] Sketch013  label="buco pompa"
  ArcFitTolerance = 1e-06
  AttachmentSupport = -> [XZ_Plane]
  ExternalGeometry = -> [Sketch]
  FullyConstrained = true
  MakeInternals = false
  MapMode = 5
  Placement = pos=(0,0,0) rot=(1,0,0;1.5708rad)
  sketch-geometry (8):
    g0: LineSegment StartX=-82.8 StartY=-10.4 StartZ=0 EndX=-82.8 EndY=-9.6 EndZ=0
    g1: LineSegment StartX=-82.8 StartY=-9.6 StartZ=0 EndX=-67.9 EndY=-9.6 EndZ=0
    g2: LineSegment StartX=-67.9 StartY=-9.6 StartZ=0 EndX=-67.9 EndY=6 EndZ=0
    g3: LineSegment StartX=-67.9 StartY=6 StartZ=0 EndX=-65.9 EndY=6 EndZ=0
    g4: LineSegment StartX=-65.9 StartY=6 StartZ=0 EndX=-65.9 EndY=-1.7 EndZ=0
    g5: LineSegment StartX=-65.9 StartY=-1.7 StartZ=0 EndX=-57.2 EndY=-1.7 EndZ=0
    g6: LineSegment StartX=-57.2 StartY=-1.7 StartZ=0 EndX=-57.2 EndY=-10.4 EndZ=0
    g7: LineSegment StartX=-57.2 StartY=-10.4 StartZ=0 EndX=-82.8 EndY=-10.4 EndZ=0
  constraints (22):
    c: Vertical(g0)
    c: Coincident(g1,g0)
    c: Horizontal(g1)
    c: Coincident(g2,g1)
    c: Vertical(g2)
    c: Coincident(g3,g2)
    c: Horizontal(g3)
    c: Coincident(g4,g3)
    c: Vertical(g4)
    c: Coincident(g5,g4)
    c: Horizontal(g5)
    c: Coincident(g6,g5)
    c: Vertical(g6)
    c: Coincident(g7,g6)
    c: Coincident(g7,g0)
    c: DistanceY(g0,g0) = 0.8
    c: DistanceY(g6,g6) = 8.7
    c: DistanceX(g1,g1) = 14.9
    c: DistanceX(g3,g3) = 2
    c: Coincident(g0,g-4)
    c: DistanceY(g2,g-6) = 0
    c: Coincident(g6,g-5)
FEATURE [Part::Extrusion] Extrude009  label="Extrude buco pompa"
  Base = -> Sketch013
  Dir = (0,-1,2e-16)
  DirMode = 2
  FaceMakerClass = Part::FaceMakerBullseye
  FaceMakerMode = 3
  LengthFwd = 13.2
  LengthRev = 0
  Solid = true
  Symmetric = true
FEATURE [Sketcher::SketchObject] Sketch014  label="buco frontale"
  ArcFitTolerance = 1e-06
  AttachmentSupport = -> [XZ_Plane]
  ExternalGeometry = -> [Sketch]
  FullyConstrained = true
  MakeInternals = false
  MapMode = 5
  Placement = pos=(0,0,0) rot=(1,0,0;1.5708rad)
  sketch-geometry (10):
    g0: LineSegment StartX=0 StartY=0 StartZ=0 EndX=0 EndY=24.671 EndZ=0
    g1: LineSegment StartX=0 StartY=24.671 StartZ=0 EndX=-4 EndY=24.671 EndZ=0
    g2: LineSegment StartX=-4 StartY=24.671 StartZ=0 EndX=-4 EndY=16 EndZ=0
    g3: LineSegment StartX=-4 StartY=16 StartZ=0 EndX=-2.4 EndY=16 EndZ=0
    g4: LineSegment StartX=-2.4 StartY=16 StartZ=0 EndX=-2.4 EndY=10 EndZ=0
    g5: LineSegment StartX=-2.4 StartY=10 StartZ=0 EndX=-12 EndY=10 EndZ=0
    g6: LineSegment StartX=-12 StartY=10 StartZ=0 EndX=-12 EndY=6 EndZ=0
    g7: LineSegment StartX=-12 StartY=6 StartZ=0 EndX=-2.4 EndY=6 EndZ=0
    g8: LineSegment StartX=-2.4 StartY=6 StartZ=0 EndX=-2.4 EndY=0 EndZ=0
    g9: LineSegment StartX=-2.4 StartY=0 StartZ=0 EndX=0 EndY=0 EndZ=0
  constraints (29):
    c: Vertical(g0)
    c: Coincident(g1,g0)
    c: Horizontal(g1)
    c: Coincident(g2,g1)
    c: Vertical(g2)
    c: Coincident(g3,g2)
    c: Horizontal(g3)
    c: Coincident(g4,g3)
    c: Vertical(g4)
    c: Coincident(g5,g4)
    c: Horizontal(g5)
    c: Coincident(g6,g5)
    c: Vertical(g6)
    c: Coincident(g7,g6)
    c: Coincident(g8,g7)
    c: Vertical(g8)
    c: Coincident(g9,g8)
    c: Coincident(g9,g0)
    c: Horizontal(g9)
    c: DistanceY(g0,g0) = 24.671
    c: Horizontal(g7)
    c: DistanceY(g6,g6) = 4
    c: DistanceY(g4,g4) = 6
    c: DistanceX(g9,g9) = 2.4
    c: Coincident(g0,g-1)
    c: DistanceY(g-3,g7) = 0
    c: DistanceX(g8,g4) = 0
    c: DistanceX(g-3,g1) = 0
    c: DistanceX(g6,g-3) = 8
FEATURE [Part::Extrusion] Extrude010  label="Extrude buco frontale"
  Base = -> Sketch014
  Dir = (0,-1,2e-16)
  DirMode = 2
  FaceMakerClass = Part::FaceMakerBullseye
  FaceMakerMode = 3
  LengthFwd = 11.2
  LengthRev = 0
  Solid = true
  Symmetric = true
FEATURE [Sketcher::SketchObject] Sketch015  label="guida rail"
  ArcFitTolerance = 1e-06
  AttachmentSupport = -> [XZ_Plane]
  ExternalGeometry = -> [Sketch]
  FullyConstrained = true
  MakeInternals = false
  MapMode = 5
  Placement = pos=(0,0,0) rot=(1,0,0;1.5708rad)
  sketch-geometry (4):
    g0: LineSegment StartX=-100.8 StartY=43.2 StartZ=0 EndX=-44.6 EndY=43.2 EndZ=0
    g1: LineSegment StartX=-44.6 StartY=43.2 StartZ=0 EndX=-44.6 EndY=41.2 EndZ=0
    g2: LineSegment StartX=-44.6 StartY=41.2 StartZ=0 EndX=-100.8 EndY=41.2 EndZ=0
    g3: LineSegment StartX=-100.8 StartY=41.2 StartZ=0 EndX=-100.8 EndY=43.2 EndZ=0
  constraints (9):
    c: Horizontal(g0)
    c: Coincident(g1,g0)
    c: Coincident(g2,g1)
    c: Coincident(g3,g2)
    c: Coincident(g3,g0)
    c: Vertical(g3)
    c: Coincident(g2,g-3)
    c: Coincident(g1,g-3)
    c: Coincident(g0,g-4)
FEATURE [Part::Extrusion] Extrude011  label="Extrude guida rail"
  Base = -> Sketch015
  Dir = (0,-1,2e-16)
  DirMode = 2
  FaceMakerClass = Part::FaceMakerBullseye
  FaceMakerMode = 3
  LengthFwd = 9
  LengthRev = 0
  Solid = true
  Symmetric = true
FEATURE [Sketcher::SketchObject] Sketch016  label="guide per coperture laterali"
  ArcFitTolerance = 1e-06
  AttachmentSupport = -> [XZ_Plane]
  ExternalGeometry = -> [Sketch]
  FullyConstrained = true
  MakeInternals = false
  MapMode = 5
  Placement = pos=(0,0,0) rot=(1,0,0;1.5708rad)
  sketch-geometry (14):
    g0: Circle CenterX=-5.6 CenterY=7.6 CenterZ=0 NormalX=0 NormalY=0 NormalZ=1 AngleXU=0 Radius=1.6
    g1: Circle CenterX=-5.6 CenterY=7.6 CenterZ=0 NormalX=0 NormalY=0 NormalZ=1 AngleXU=0 Radius=4
    g2: Circle CenterX=-5.6 CenterY=34.8 CenterZ=0 NormalX=0 NormalY=0 NormalZ=1 AngleXU=0 Radius=1.6
    g3: Circle CenterX=-5.6 CenterY=34.8 CenterZ=0 NormalX=0 NormalY=0 NormalZ=1 AngleXU=0 Radius=4
    g4: Circle CenterX=-184.08 CenterY=34.8 CenterZ=0 NormalX=0 NormalY=0 NormalZ=1 AngleXU=0 Radius=1.6
    g5: Circle CenterX=-184.08 CenterY=34.8 CenterZ=0 NormalX=0 NormalY=0 NormalZ=1 AngleXU=0 Radius=4
    g6: Circle CenterX=-179.305 CenterY=-76.8316 CenterZ=0 NormalX=0 NormalY=0 NormalZ=1 AngleXU=0 Radius=1.6
    g7: Circle CenterX=-179.305 CenterY=-76.8316 CenterZ=0 NormalX=0 NormalY=0 NormalZ=1 AngleXU=0 Radius=4
    g8: Circle CenterX=-213.443 CenterY=-76.8316 CenterZ=0 NormalX=0 NormalY=0 NormalZ=1 AngleXU=0 Radius=1.6
    g9: Circle CenterX=-213.443 CenterY=-76.8316 CenterZ=0 NormalX=0 NormalY=0 NormalZ=1 AngleXU=0 Radius=4
    g10: Circle CenterX=-78.51 CenterY=7.6 CenterZ=0 NormalX=0 NormalY=0 NormalZ=1 AngleXU=0 Radius=1.6
    g11: Circle CenterX=-78.51 CenterY=7.6 CenterZ=0 NormalX=0 NormalY=0 NormalZ=1 AngleXU=0 Radius=4
    g12: Circle CenterX=-78.51 CenterY=34.8 CenterZ=0 NormalX=0 NormalY=0 NormalZ=1 AngleXU=0 Radius=1.6
    g13: Circle CenterX=-78.51 CenterY=34.8 CenterZ=0 NormalX=0 NormalY=0 NormalZ=1 AngleXU=0 Radius=4
  constraints (35):
    c: Diameter(g0) = 3.2
    c: Diameter(g1) = 8
    c: Coincident(g0,g1)
    c: Diameter(g2) = 3.2
    c: Diameter(g3) = 8
    c: Coincident(g3,g2)
    c: Tangent(g2,g-7)
    c: Diameter(g4) = 3.2
    c: Diameter(g5) = 8
    c: Coincident(g5,g4)
    c: Tangent(g4,g-7)
    c: Tangent(g4,g-8)
    c: Diameter(g6) = 3.2
    c: Diameter(g7) = 8
    c: Coincident(g7,g6)
    c: Tangent(g6,g-9)
    c: Tangent(g6,g-10)
    c: Diameter(g8) = 3.2
    c: Diameter(g9) = 8
    c: Coincident(g9,g8)
    c: Tangent(g8,g-10)
    c: Tangent(g8,g-11)
    c: Diameter(g10) = 3.2
    c: Diameter(g11) = 8
    c: Diameter(g12) = 3.2
    c: Diameter(g13) = 8
    c: Coincident(g12,g13)
    c: Coincident(g10,g11)
    c: Tangent(g12,g-7)
    c: DistanceX(g12,g10) = 0
    c: Tangent(g2,g-6)
    c: Tangent(g0,g-6)
    c: Tangent(g0,g-3)
    c: Tangent(g10,g-3)
    c: Tangent(g10,g-4)
FEATURE [Part::Extrusion] Extrude012  label="extrude guide per coperture laterali"
  Base = -> Sketch016
  Dir = (0,-1,2e-16)
  DirMode = 2
  FaceMakerClass = Part::FaceMakerBullseye
  FaceMakerMode = 3
  LengthFwd = 25.2
  LengthRev = 0
  Solid = true
  Symmetric = true
FEATURE [Sketcher::SketchObject] Sketch017  label="supporto CAM"
  ArcFitTolerance = 1e-06
  AttachmentSupport = -> [XZ_Plane]
  ExternalGeometry = -> [Sketch]
  FullyConstrained = true
  MakeInternals = false
  MapMode = 5
  Placement = pos=(0,0,0) rot=(1,0,0;1.5708rad)
  sketch-geometry (6):
    g0: LineSegment StartX=-2.4 StartY=48 StartZ=0 EndX=-2.4 EndY=41.2 EndZ=0
    g1: LineSegment StartX=-2.4 StartY=48 StartZ=0 EndX=-34 EndY=48 EndZ=0
    g2: LineSegment StartX=-34 StartY=48 StartZ=0 EndX=-34 EndY=46.72 EndZ=0
    g3: LineSegment StartX=-34 StartY=46.72 StartZ=0 EndX=-36 EndY=46.72 EndZ=0
    g4: LineSegment StartX=-36 StartY=46.72 StartZ=0 EndX=-36 EndY=41.2 EndZ=0
    g5: LineSegment StartX=-36 StartY=41.2 StartZ=0 EndX=-2.4 EndY=41.2 EndZ=0
  constraints (15):
    c: Coincident(g1,g0)
    c: Horizontal(g1)
    c: Coincident(g2,g1)
    c: Vertical(g2)
    c: Coincident(g3,g2)
    c: Horizontal(g3)
    c: Coincident(g4,g3)
    c: Coincident(g5,g4)
    c: DistanceX(g1,g0) = 31.6
    c: Coincident(g5,g0)
    c: Vertical(g4)
    c: DistanceY(g2,g1) = 1.28
    c: Coincident(g0,g-3)
    c: Coincident(g0,g-3)
    c: Coincident(g4,g-4)
FEATURE [Part::Extrusion] Extrude013  label="Extrude supporto CAM"
  Base = -> Sketch017
  Dir = (0,-1,2e-16)
  DirMode = 2
  FaceMakerClass = Part::FaceMakerBullseye
  FaceMakerMode = 3
  LengthFwd = 17.8
  LengthRev = 0
  Solid = true
  Symmetric = true
FEATURE [Sketcher::SketchObject] Sketch018  label="Scavo CAM"
  ArcFitTolerance = 1e-06
  AttachmentSupport = -> [YZ_Plane]
  ExternalGeometry = -> [Sketch]
  FullyConstrained = true
  MakeInternals = false
  MapMode = 5
  Placement = pos=(0,0,0) rot=(0.57735,0.57735,0.57735;2.0944rad)
  sketch-geometry (4):
    g0: LineSegment StartX=-7.73 StartY=48 StartZ=0 EndX=7.73 EndY=48 EndZ=0
    g1: LineSegment [constr] StartX=1.07e-14 StartY=48 StartZ=0 EndX=0 EndY=43.5155 EndZ=0
    g2: ArcOfCircle CenterX=9e-15 CenterY=52.42 CenterZ=0 NormalX=0 NormalY=0 NormalZ=1 AngleXU=0 Radius=8.90445 StartAngle=3.66102 EndAngle=5.76376
    g3: Circle [constr] CenterX=9e-15 CenterY=52.42 CenterZ=0 NormalX=0 NormalY=0 NormalZ=1 AngleXU=0 Radius=8.9
  constraints (13):
    c: Horizontal(g0)
    c: DistanceY(g-3,g0) = 0
    c: DistanceX(g0,g0) = 15.46
    c: DistanceX(g0,g-3) = 7.73
    c: DistanceX(g-3) = 0
    c: Coincident(g1,g-3)
    c: PointOnObject(g1,g-2)
    c: Coincident(g2,g0)
    c: Coincident(g2,g0)
    c: PointOnObject(g1,g2)
    c: Diameter(g3) = 17.8
    c: DistanceY(g1,g3) = 4.42
    c: Coincident(g2,g3)
FEATURE [Part::Extrusion] Extrude014  label="Extrude Scavo CAM"
  Base = -> Sketch018
  Dir = (1,0,0)
  DirMode = 2
  FaceMakerClass = Part::FaceMakerBullseye
  FaceMakerMode = 3
  LengthFwd = -34
  LengthRev = 0
  Solid = true
  Symmetric = false
FEATURE [Sketcher::SketchObject] Sketch019  label="scavo rumble"
  ArcFitTolerance = 1e-06
  AttachmentSupport = -> [XZ_Plane]
  ExternalGeometry = -> [Sketch]
  FullyConstrained = true
  MakeInternals = false
  MapMode = 5
  Placement = pos=(0,0,0) rot=(1,0,0;1.5708rad)
  sketch-geometry (6):
    g0: LineSegment StartX=-168.716 StartY=-37.1227 StartZ=0 EndX=-163.58 EndY=-38.7914 EndZ=0
    g1: LineSegment StartX=-163.58 StartY=-38.7914 StartZ=0 EndX=-170.687 EndY=-60.6657 EndZ=0
    g2: LineSegment StartX=-170.687 StartY=-60.6657 StartZ=0 EndX=-175.823 EndY=-58.997 EndZ=0
    g3: LineSegment StartX=-175.823 StartY=-58.997 StartZ=0 EndX=-168.716 EndY=-37.1227 EndZ=0
    g4: LineSegment [constr] StartX=-145.51 StartY=22 StartZ=0 EndX=-165.102 EndY=-38.297 EndZ=0
    g5: LineSegment [constr] StartX=-163.58 StartY=-38.7914 StartZ=0 EndX=-165.102 EndY=-38.297 EndZ=0
  constraints (17):
    c: Coincident(g1,g0)
    c: Coincident(g2,g1)
    c: Coincident(g3,g2)
    c: Coincident(g3,g0)
    c: Parallel(g3,g-3)
    c: Parallel(g3,g1)
    c: Perpendicular(g3,g0)
    c: Perpendicular(g2,g3)
    c: Distance(g2,g0) = 23
    c: Parallel(g4,g-3)
    c: Distance(g4) = 63.4
    c: Coincident(g4,g-3)
    c: Parallel(g5,g0)
    c: Coincident(g5,g0)
    c: Coincident(g5,g4)
    c: Distance(g4,g0) = 3.8
    c: Distance(g4,g0) = 1.6
FEATURE [Part::Extrusion] Extrude015  label="scavo rumble001"
  Base = -> Sketch019
  Dir = (0,-1,2e-16)
  DirMode = 2
  FaceMakerClass = Part::FaceMakerBullseye
  FaceMakerMode = 3
  LengthFwd = 21
  LengthRev = 0
  Solid = true
  Symmetric = true
FEATURE [Sketcher::SketchObject] Sketch020  label="fermo rumble"
  ArcFitTolerance = 1e-06
  AttachmentSupport = -> [XZ_Plane]
  ExternalGeometry = -> [Sketch019,Sketch]
  FullyConstrained = true
  MakeInternals = false
  MapMode = 5
  Placement = pos=(0,0,0) rot=(1,0,0;1.5708rad)
  sketch-geometry (16):
    g0: LineSegment [constr] StartX=-170.849 StartY=-55.9866 StartZ=0 EndX=-172.209 EndY=-60.1713 EndZ=0
    g1: LineSegment [constr] StartX=-172.209 StartY=-60.1713 StartZ=0 EndX=-170.687 EndY=-60.6657 EndZ=0
    g2: LineSegment StartX=-172.262 StartY=-53.2145 StartZ=0 EndX=-170.17 EndY=-53.8943 EndZ=0
    g3: LineSegment StartX=-170.17 StartY=-53.8943 StartZ=0 EndX=-170.849 EndY=-55.9866 EndZ=0
    g4: LineSegment StartX=-170.849 StartY=-55.9866 StartZ=0 EndX=-172.942 EndY=-55.3068 EndZ=0
    g5: LineSegment StartX=-172.942 StartY=-55.3068 StartZ=0 EndX=-172.262 EndY=-53.2145 EndZ=0
    g6: LineSegment StartX=-171.767 StartY=-51.6928 StartZ=0 EndX=-168.344 EndY=-52.8052 EndZ=0
    g7: LineSegment StartX=-168.344 StartY=-52.8052 StartZ=0 EndX=-169.951 EndY=-57.7507 EndZ=0
    g8: LineSegment StartX=-169.951 StartY=-57.7507 StartZ=0 EndX=-173.374 EndY=-56.6383 EndZ=0
    g9: LineSegment StartX=-174.402 StartY=-54.6222 StartZ=0 EndX=-173.784 EndY=-52.72 EndZ=0
    g10: LineSegment [constr] StartX=-173.784 StartY=-52.72 StartZ=0 EndX=-173.289 EndY=-51.1984 EndZ=0
    g11: LineSegment [constr] StartX=-173.289 StartY=-51.1984 StartZ=0 EndX=-171.767 EndY=-51.6928 EndZ=0
    g12: ArcOfCircle CenterX=-172.88 CenterY=-55.1166 CenterZ=0 NormalX=0 NormalY=0 NormalZ=1 AngleXU=0 Radius=1.6 StartAngle=2.82743 EndAngle=4.39823
    g13: GeomPoint [constr] X=-174.896 Y=-56.1438 Z=0
    g14: ArcOfCircle CenterX=-172.262 CenterY=-53.2145 CenterZ=0 NormalX=0 NormalY=0 NormalZ=1 AngleXU=0 Radius=1.6 StartAngle=1.25664 EndAngle=2.82743
    g15: GeomPoint [constr] X=-173.289 Y=-51.1984 Z=0
  constraints (42):
    c: Parallel(g0,g-4)
    c: Distance(g0) = 4.4
    c: Coincident(g1,g0)
    c: Perpendicular(g0,g1)
    c: Distance(g1) = 1.6
    c: Coincident(g1,g-5)
    c: Coincident(g3,g2)
    c: Coincident(g4,g3)
    c: Coincident(g5,g4)
    c: Coincident(g5,g2)
    c: Parallel(g3,g-4)
    c: Parallel(g3,g5)
    c: Perpendicular(g2,g3)
    c: Parallel(g4,g2)
    c: Distance(g2) = 2.2
    c: Distance(g3) = 2.2
    c: Coincident(g7,g6)
    c: Coincident(g8,g7)
    c: Parallel(g7,g-4)
    c: Parallel(g7,g9)
    c: Perpendicular(g6,g7)
    c: Parallel(g6,g8)
    c: Distance(g6,g15) = 5.2
    c: Distance(g7) = 5.2
    c: Coincident(g11,g10)
    c: Parallel(g10,g9)
    c: Parallel(g11,g6)
    c: Distance(g10) = 1.6
    c: Distance(g11) = 1.6
    c: Coincident(g10,g15)
    c: Distance(g11,g2) = 1.6
    c: Distance(g2,g10) = 1.6
    c: PointOnObject(g13,g8)
    c: PointOnObject(g13,g9)
    c: Tangent(g8,g12) = 1.5708
    c: Tangent(g9,g12) = 1.5708
    c: PointOnObject(g15,g9)
    c: Tangent(g6,g14) = 1.5708
    c: Tangent(g9,g14) = 1.5708
    c: Equal(g12,g14)
    c: Coincident(g6,g11)
    c: Coincident(g3,g0)
FEATURE [Part::Extrusion] Extrude016  label="Extrude fermo rumble"
  Base = -> Sketch020
  Dir = (0,-1,2e-16)
  DirMode = 2
  FaceMakerClass = Part::FaceMakerBullseye
  FaceMakerMode = 3
  LengthFwd = 25.2
  LengthRev = 0
  Solid = true
  Symmetric = true
FEATURE [Sketcher::SketchObject] Sketch021  label="perno fermo rumble001"
  ArcFitTolerance = 1e-06
  AttachmentSupport = -> [XZ_Plane001]
  FullyConstrained = true
  MakeInternals = false
  MapMode = 5
  Placement = pos=(0,0,0) rot=(1,0,0;1.5708rad)
  sketch-geometry (16):
    g0: LineSegment StartX=0 StartY=0.45 StartZ=0 EndX=0 EndY=1.55 EndZ=0
    g1: LineSegment StartX=0.45 StartY=2 StartZ=0 EndX=1.55 EndY=2 EndZ=0
    g2: LineSegment StartX=2 StartY=1.55 StartZ=0 EndX=2 EndY=0.45 EndZ=0
    g3: LineSegment StartX=1.55 StartY=0 StartZ=0 EndX=0.45 EndY=0 EndZ=0
    g4: ArcOfCircle [constr] CenterX=0.45 CenterY=1.55 CenterZ=0 NormalX=0 NormalY=0 NormalZ=1 AngleXU=0 Radius=0.45 StartAngle=1.5708 EndAngle=3.14159
    g5: GeomPoint [constr] X=0 Y=2 Z=0
    g6: LineSegment StartX=0.45 StartY=2 StartZ=0 EndX=0 EndY=1.55 EndZ=0
    g7: ArcOfCircle [constr] CenterX=1.55 CenterY=1.55 CenterZ=0 NormalX=0 NormalY=0 NormalZ=1 AngleXU=0 Radius=0.45 StartAngle=0 EndAngle=1.5708
    g8: GeomPoint [constr] X=2 Y=2 Z=0
    g9: LineSegment StartX=2 StartY=1.55 StartZ=0 EndX=1.55 EndY=2 EndZ=0
    g10: ArcOfCircle [constr] CenterX=1.55 CenterY=0.45 CenterZ=0 NormalX=0 NormalY=0 NormalZ=1 AngleXU=0 Radius=0.45 StartAngle=4.71239 EndAngle=6.28319
    g11: GeomPoint [constr] X=2 Y=0 Z=0
    g12: LineSegment StartX=1.55 StartY=0 StartZ=0 EndX=2 EndY=0.45 EndZ=0
    g13: ArcOfCircle [constr] CenterX=0.45 CenterY=0.45 CenterZ=0 NormalX=0 NormalY=0 NormalZ=1 AngleXU=0 Radius=0.45 StartAngle=3.14159 EndAngle=4.71239
    g14: GeomPoint [constr] X=0 Y=0 Z=0
    g15: LineSegment StartX=0 StartY=0.45 StartZ=0 EndX=0.45 EndY=0 EndZ=0
  constraints (35):
    c: Coincident(g14,g-1)
    c: PointOnObject(g5,g-2)
    c: Horizontal(g1)
    c: Vertical(g2)
    c: Horizontal(g3)
    c: DistanceX(g5,g8) = 2
    c: DistanceY(g11,g8) = 2
    c: PointOnObject(g5,g0)
    c: PointOnObject(g5,g1)
    c: Tangent(g0,g4) = 1.5708
    c: Tangent(g1,g4) = 1.5708
    c: Coincident(g6,g0)
    c: Coincident(g6,g1)
    c: PointOnObject(g8,g2)
    c: PointOnObject(g8,g1)
    c: Tangent(g2,g7) = 1.5708
    c: Tangent(g1,g7) = 1.5708
    c: Coincident(g9,g2)
    c: Coincident(g9,g1)
    c: PointOnObject(g11,g2)
    c: PointOnObject(g11,g3)
    c: Tangent(g2,g10) = 1.5708
    c: Tangent(g3,g10) = 1.5708
    c: Coincident(g12,g2)
    c: Coincident(g12,g3)
    c: PointOnObject(g14,g0)
    c: PointOnObject(g14,g3)
    c: Tangent(g0,g13) = 1.5708
    c: Tangent(g3,g13) = 1.5708
    c: Coincident(g15,g0)
    c: Coincident(g15,g3)
    c: Equal(g6,g9)
    c: Equal(g9,g12)
    c: Equal(g12,g15)
    c: DistanceX(g14,g3) = 0.45
FEATURE [Sketcher::SketchObject] Sketch022  label="fori per M3x5(OD)x6(L)"
  ArcFitTolerance = 1e-06
  AttachmentSupport = -> [XZ_Plane]
  ExternalGeometry = -> [Sketch016]
  FullyConstrained = true
  MakeInternals = false
  MapMode = 5
  Placement = pos=(0,0,0) rot=(1,0,0;1.5708rad)
  sketch-geometry (7):
    g0: Circle CenterX=-5.6 CenterY=34.8 CenterZ=0 NormalX=0 NormalY=0 NormalZ=1 AngleXU=0 Radius=2.5
    g1: Circle CenterX=-5.6 CenterY=7.6 CenterZ=0 NormalX=0 NormalY=0 NormalZ=1 AngleXU=0 Radius=2.5
    g2: Circle CenterX=-78.51 CenterY=34.8 CenterZ=0 NormalX=0 NormalY=0 NormalZ=1 AngleXU=0 Radius=2.5
    g3: Circle CenterX=-78.51 CenterY=7.6 CenterZ=0 NormalX=0 NormalY=0 NormalZ=1 AngleXU=0 Radius=2.5
    g4: Circle CenterX=-184.08 CenterY=34.8 CenterZ=0 NormalX=0 NormalY=0 NormalZ=1 AngleXU=0 Radius=2.5
    g5: Circle CenterX=-179.305 CenterY=-76.8316 CenterZ=0 NormalX=0 NormalY=0 NormalZ=1 AngleXU=0 Radius=2.5
    g6: Circle CenterX=-213.443 CenterY=-76.8316 CenterZ=0 NormalX=0 NormalY=0 NormalZ=1 AngleXU=0 Radius=2.5
  constraints (14):
    c: Diameter(g0) = 5
    c: Diameter(g1) = 5
    c: Diameter(g2) = 5
    c: Diameter(g3) = 5
    c: Diameter(g4) = 5
    c: Diameter(g5) = 5
    c: Diameter(g6) = 5
    c: Coincident(g0,g-8)
    c: Coincident(g1,g-9)
    c: Coincident(g2,g-6)
    c: Coincident(g3,g-7)
    c: Coincident(g4,g-5)
    c: Coincident(g5,g-4)
    c: Coincident(g6,g-3)
FEATURE [Part::Extrusion] Extrude018  label="Extrude fori M3x5x6 - dx"
  Base = -> Sketch022
  Dir = (0,-1,2e-16)
  DirMode = 2
  FaceMakerClass = Part::FaceMakerBullseye
  FaceMakerMode = 3
  LengthFwd = 6.2
  LengthRev = 0
  Placement = pos=(0,-9.5,0) rot=(0,0,1;0rad)
  Solid = true
  Symmetric = true
FEATURE [Part::Extrusion] Extrude019  label="Extrude fori M3x5x6 - sx"
  Base = -> Sketch022
  Dir = (0,-1,2e-16)
  DirMode = 2
  FaceMakerClass = Part::FaceMakerBullseye
  FaceMakerMode = 3
  LengthFwd = 6.2
  LengthRev = 0
  Placement = pos=(0,9.5,0) rot=(0,0,1;0rad)
  Solid = true
  Symmetric = true
FEATURE [Sketcher::SketchObject] Sketch023  label="foro anteriore M3x5x6"
  ArcFitTolerance = 1e-06
  AttachmentSupport = -> [YZ_Plane]
  FullyConstrained = true
  MakeInternals = false
  MapMode = 5
  Placement = pos=(0,0,0) rot=(0.57735,0.57735,0.57735;2.0944rad)
  sketch-geometry (2):
    g0: LineSegment [constr] StartX=0 StartY=0 StartZ=0 EndX=0 EndY=38.6 EndZ=0
    g1: Circle CenterX=0 CenterY=38.6 CenterZ=0 NormalX=0 NormalY=0 NormalZ=1 AngleXU=0 Radius=2.5
  constraints (5):
    c: Coincident(g0,g-1)
    c: PointOnObject(g0,g-2)
    c: DistanceY(g0,g0) = 38.6
    c: Diameter(g1) = 5
    c: Coincident(g1,g0)
FEATURE [Part::Extrusion] Extrude020  label="Extrude foro anteriore M3x5x6"
  Base = -> Sketch023
  Dir = (1,0,0)
  DirMode = 2
  FaceMakerClass = Part::FaceMakerBullseye
  FaceMakerMode = 3
  LengthFwd = -6.2
  LengthRev = 0
  Solid = true
  Symmetric = false
FEATURE [Sketcher::SketchObject] Sketch024  label="fori per viti frontale"
  ArcFitTolerance = 1e-06
  AttachmentSupport = -> [YZ_Plane]
  FullyConstrained = true
  MakeInternals = false
  MapMode = 5
  Placement = pos=(0,0,0) rot=(0.57735,0.57735,0.57735;2.0944rad)
  sketch-geometry (9):
    g0: LineSegment [constr] StartX=-10.3 StartY=30.721 StartZ=0 EndX=10.3 EndY=30.721 EndZ=0
    g1: LineSegment [constr] StartX=10.3 StartY=30.721 StartZ=0 EndX=10.3 EndY=10.121 EndZ=0
    g2: LineSegment [constr] StartX=10.3 StartY=10.121 StartZ=0 EndX=-10.3 EndY=10.121 EndZ=0
    g3: LineSegment [constr] StartX=-10.3 StartY=10.121 StartZ=0 EndX=-10.3 EndY=30.721 EndZ=0
    g4: LineSegment [constr] StartX=0 StartY=0 StartZ=0 EndX=0 EndY=10.121 EndZ=0
    g5: Circle CenterX=-10.3 CenterY=30.721 CenterZ=0 NormalX=0 NormalY=0 NormalZ=1 AngleXU=0 Radius=2
    g6: Circle CenterX=10.3 CenterY=30.721 CenterZ=0 NormalX=0 NormalY=0 NormalZ=1 AngleXU=0 Radius=2
    g7: Circle CenterX=-10.3 CenterY=10.121 CenterZ=0 NormalX=0 NormalY=0 NormalZ=1 AngleXU=0 Radius=2
    g8: Circle CenterX=10.3 CenterY=10.121 CenterZ=0 NormalX=0 NormalY=0 NormalZ=1 AngleXU=0 Radius=2
  constraints (22):
    c: Horizontal(g0)
    c: Coincident(g1,g0)
    c: Vertical(g1)
    c: Coincident(g2,g1)
    c: Horizontal(g2)
    c: Coincident(g3,g2)
    c: Coincident(g3,g0)
    c: Vertical(g3)
    c: DistanceX(g0,g0) = 20.6
    c: DistanceY(g3,g3) = 20.6
    c: Coincident(g4,g-1)
    c: PointOnObject(g4,g-2)
    c: DistanceY(g4,g4) = 10.121
    c: Symmetric(g2,g2,g4)
    c: Diameter(g5) = 4
    c: Diameter(g6) = 4
    c: Diameter(g7) = 4
    c: Diameter(g8) = 4
    c: Coincident(g5,g0)
    c: Coincident(g6,g0)
    c: Coincident(g7,g2)
    c: Coincident(g8,g1)
FEATURE [Part::Extrusion] Extrude021  label="Extrude fori per viti frontale"
  Base = -> Sketch024
  Dir = (1,0,0)
  DirMode = 2
  FaceMakerClass = Part::FaceMakerBullseye
  FaceMakerMode = 3
  LengthFwd = -2.4
  LengthRev = 0
  Solid = true
  Symmetric = false
FEATURE [Sketcher::SketchObject] Sketch025  label="foro per filo CAM"
  ArcFitTolerance = 1e-06
  AttachmentSupport = -> [XZ_Plane]
  ExternalGeometry = -> [Sketch]
  FullyConstrained = true
  MakeInternals = false
  MapMode = 5
  Placement = pos=(0,0,0) rot=(1,0,0;1.5708rad)
  sketch-geometry (4):
    g0: LineSegment StartX=-44.6 StartY=41.2 StartZ=0 EndX=-44.6 EndY=36.4 EndZ=0
    g1: LineSegment StartX=-44.6 StartY=36.4 StartZ=0 EndX=-54.6 EndY=36.4 EndZ=0
    g2: LineSegment StartX=-54.6 StartY=36.4 StartZ=0 EndX=-50.4 EndY=41.2 EndZ=0
    g3: LineSegment StartX=-50.4 StartY=41.2 StartZ=0 EndX=-44.6 EndY=41.2 EndZ=0
  constraints (11):
    c: Vertical(g0)
    c: Coincident(g1,g0)
    c: Horizontal(g1)
    c: Coincident(g2,g1)
    c: Coincident(g3,g2)
    c: Coincident(g3,g0)
    c: Horizontal(g3)
    c: Coincident(g0,g-3)
    c: DistanceY(g0,g-4) = 0
    c: DistanceX(g3,g3) = 5.8
    c: DistanceX(g1,g1) = 10
FEATURE [Part::Extrusion] Extrude022  label="Extrude foro per filo CAM dx"
  Base = -> Sketch025
  Dir = (0,-1,2e-16)
  DirMode = 2
  FaceMakerClass = Part::FaceMakerBullseye
  FaceMakerMode = 3
  LengthFwd = 4.9
  LengthRev = 0
  Placement = pos=(0,6.95,0) rot=(0,0,1;0rad)
  Solid = true
  Symmetric = true
FEATURE [Part::Extrusion] Extrude023  label="Extrude foro per filo CAM sx"
  Base = -> Sketch025
  Dir = (0,-1,2e-16)
  DirMode = 2
  FaceMakerClass = Part::FaceMakerBullseye
  FaceMakerMode = 3
  LengthFwd = 4.9
  LengthRev = 0
  Placement = pos=(0,-6.95,0) rot=(0,0,1;0rad)
  Solid = true
  Symmetric = true
FEATURE [Sketcher::SketchObject] Sketch026  label="foro sotto anteriore M3x5x6"
  ArcFitTolerance = 1e-06
  AttachmentSupport = -> [XY_Plane]
  FullyConstrained = true
  MakeInternals = false
  MapMode = 5
  sketch-geometry (2):
    g0: LineSegment [constr] StartX=0 StartY=0 StartZ=0 EndX=-16.5 EndY=0 EndZ=0
    g1: Circle CenterX=-16.5 CenterY=0 CenterZ=0 NormalX=0 NormalY=0 NormalZ=1 AngleXU=0 Radius=2.5
  constraints (5):
    c: Distance(g0) = 16.5
    c: Coincident(g0,g-1)
    c: PointOnObject(g0,g-1)
    c: Diameter(g1) = 5
    c: Coincident(g0,g1)
FEATURE [Sketcher::SketchObject] Sketch027  label="foro sotto posteriore M3x5x6"
  ArcFitTolerance = 1e-06
  AttachmentSupport = -> [XY_Plane]
  ExternalGeometry = -> [Sketch]
  FullyConstrained = true
  MakeInternals = false
  MapMode = 5
  sketch-geometry (2):
    g0: LineSegment [constr] StartX=-82.8 StartY=2e-16 StartZ=0 EndX=-71.3 EndY=2e-16 EndZ=0
    g1: Circle CenterX=-71.3 CenterY=2e-16 CenterZ=0 NormalX=0 NormalY=0 NormalZ=1 AngleXU=0 Radius=2.5
  constraints (5):
    c: Distance(g0) = 11.5
    c: Coincident(g0,g-3)
    c: PointOnObject(g0,g-3)
    c: Diameter(g1) = 5
    c: Coincident(g1,g0)
FEATURE [Sketcher::SketchObject] Sketch029  label="fori sotto impugnatura"
  ArcFitTolerance = 1e-06
  AttachmentSupport = -> [XY_Plane]
  ExternalGeometry = -> [Sketch]
  FullyConstrained = true
  MakeInternals = false
  MapMode = 5
  sketch-geometry (15):
    g0: LineSegment [constr] StartX=-175.232 StartY=-1.83e-14 StartZ=0 EndX=-191.232 EndY=0 EndZ=0
    g1: Circle CenterX=-191.232 CenterY=0 CenterZ=0 NormalX=0 NormalY=0 NormalZ=1 AngleXU=0 Radius=3.95
    g2: LineSegment [constr] StartX=-175.232 StartY=-1.83e-14 StartZ=0 EndX=-204.275 EndY=0 EndZ=0
    g3: LineSegment StartX=-204.275 StartY=3.525 StartZ=0 EndX=-204.275 EndY=-3.525 EndZ=0
    g4: LineSegment StartX=-205.4 StartY=-4.65 StartZ=0 EndX=-206.65 EndY=-4.65 EndZ=0
    g5: LineSegment StartX=-207.775 StartY=-3.525 StartZ=0 EndX=-207.775 EndY=3.525 EndZ=0
    g6: LineSegment StartX=-206.65 StartY=4.65 StartZ=0 EndX=-205.4 EndY=4.65 EndZ=0
    g7: ArcOfCircle CenterX=-206.65 CenterY=3.525 CenterZ=0 NormalX=0 NormalY=0 NormalZ=1 AngleXU=0 Radius=1.125 StartAngle=1.5708 EndAngle=3.14159
    g8: GeomPoint [constr] X=-207.775 Y=4.65 Z=0
    g9: ArcOfCircle CenterX=-205.4 CenterY=3.525 CenterZ=0 NormalX=0 NormalY=0 NormalZ=1 AngleXU=0 Radius=1.125 StartAngle=0 EndAngle=1.5708
    g10: GeomPoint [constr] X=-204.275 Y=4.65 Z=0
    g11: ArcOfCircle CenterX=-205.4 CenterY=-3.525 CenterZ=0 NormalX=0 NormalY=0 NormalZ=1 AngleXU=0 Radius=1.125 StartAngle=4.71239 EndAngle=6.28319
    g12: GeomPoint [constr] X=-204.275 Y=-4.65 Z=0
    g13: ArcOfCircle CenterX=-206.65 CenterY=-3.525 CenterZ=0 NormalX=0 NormalY=0 NormalZ=1 AngleXU=0 Radius=1.125 StartAngle=3.14159 EndAngle=4.71239
    g14: GeomPoint [constr] X=-207.775 Y=-4.65 Z=0
  constraints (35):
    c: Distance(g0) = 16
    c: Coincident(g0,g-3)
    c: PointOnObject(g0,g-1)
    c: Diameter(g1) = 7.9
    c: Coincident(g1,g0)
    c: Coincident(g2,g0)
    c: PointOnObject(g2,g-1)
    c: Vertical(g3)
    c: Horizontal(g4)
    c: Vertical(g5)
    c: Horizontal(g6)
    c: DistanceY(g12,g10) = 9.3
    c: DistanceX(g8,g10) = 3.5
    c: Symmetric(g10,g12,g2)
    c: PointOnObject(g8,g5)
    c: PointOnObject(g8,g6)
    c: Tangent(g5,g7) = 1.5708
    c: Tangent(g6,g7) = 1.5708
    c: PointOnObject(g10,g3)
    c: PointOnObject(g10,g6)
    c: Tangent(g3,g9) = 1.5708
    c: Tangent(g6,g9) = 1.5708
    c: PointOnObject(g12,g3)
    c: PointOnObject(g12,g4)
    c: Tangent(g3,g11) = 1.5708
    c: Tangent(g4,g11) = 1.5708
    c: PointOnObject(g14,g4)
    c: PointOnObject(g14,g5)
    c: Tangent(g4,g13) = 1.5708
    c: Tangent(g5,g13) = 1.5708
    c: Equal(g7,g9)
    c: Equal(g9,g11)
    c: Equal(g11,g13)
    c: DistanceX(g6,g6) = 1.25
    c: DistanceX(g-5,g5) = 6.8
FEATURE [Sketcher::SketchObject] Sketch030  label="fori superiori per solenoide e oled"
  ArcFitTolerance = 1e-06
  AttachmentSupport = -> [XY_Plane]
  ExternalGeometry = -> [Sketch]
  FullyConstrained = true
  MakeInternals = false
  MapMode = 5
  sketch-geometry (33):
    g0: LineSegment [constr] StartX=-181.6 StartY=1.12e-14 StartZ=0 EndX=-169.91 EndY=0 EndZ=0
    g1: LineSegment [constr] StartX=-169.91 StartY=0 StartZ=0 EndX=-169.91 EndY=-2.6 EndZ=0
    g2: LineSegment [constr] StartX=-169.91 StartY=0 StartZ=0 EndX=-169.91 EndY=2.6 EndZ=0
    g3: LineSegment StartX=-169.91 StartY=4.975 StartZ=0 EndX=-169.91 EndY=8.225 EndZ=0
    g4: LineSegment StartX=-167.535 StartY=10.6 StartZ=0 EndX=-167.285 EndY=10.6 EndZ=0
    g5: LineSegment StartX=-164.91 StartY=8.225 StartZ=0 EndX=-164.91 EndY=4.975 EndZ=0
    g6: LineSegment StartX=-167.285 StartY=2.6 StartZ=0 EndX=-167.535 EndY=2.6 EndZ=0
    g7: LineSegment StartX=-169.91 StartY=-4.975 StartZ=0 EndX=-169.91 EndY=-8.225 EndZ=0
    g8: LineSegment StartX=-167.535 StartY=-10.6 StartZ=0 EndX=-167.285 EndY=-10.6 EndZ=0
    g9: LineSegment StartX=-164.91 StartY=-8.225 StartZ=0 EndX=-164.91 EndY=-4.975 EndZ=0
    g10: LineSegment StartX=-167.285 StartY=-2.6 StartZ=0 EndX=-167.535 EndY=-2.6 EndZ=0
    g11: ArcOfCircle CenterX=-167.535 CenterY=8.225 CenterZ=0 NormalX=0 NormalY=0 NormalZ=1 AngleXU=0 Radius=2.375 StartAngle=1.5708 EndAngle=3.14159
    g12: GeomPoint [constr] X=-169.91 Y=10.6 Z=0
    g13: ArcOfCircle CenterX=-167.285 CenterY=8.225 CenterZ=0 NormalX=0 NormalY=0 NormalZ=1 AngleXU=0 Radius=2.375 StartAngle=0 EndAngle=1.5708
    g14: GeomPoint [constr] X=-164.91 Y=10.6 Z=0
    g15: ArcOfCircle CenterX=-167.285 CenterY=4.975 CenterZ=0 NormalX=0 NormalY=0 NormalZ=1 AngleXU=0 Radius=2.375 StartAngle=4.71239 EndAngle=6.28319
    g16: GeomPoint [constr] X=-164.91 Y=2.6 Z=0
    g17: ArcOfCircle CenterX=-167.535 CenterY=4.975 CenterZ=0 NormalX=0 NormalY=0 NormalZ=1 AngleXU=0 Radius=2.375 StartAngle=3.14159 EndAngle=4.71239
    g18: GeomPoint [constr] X=-169.91 Y=2.6 Z=0
    g19: ArcOfCircle CenterX=-167.535 CenterY=-4.975 CenterZ=0 NormalX=0 NormalY=0 NormalZ=1 AngleXU=0 Radius=2.375 StartAngle=1.5708 EndAngle=3.14159
    g20: GeomPoint [constr] X=-169.91 Y=-2.6 Z=0
    g21: ArcOfCircle CenterX=-167.285 CenterY=-4.975 CenterZ=0 NormalX=0 NormalY=0 NormalZ=1 AngleXU=0 Radius=2.375 StartAngle=0 EndAngle=1.5708
    g22: GeomPoint [constr] X=-164.91 Y=-2.6 Z=0
    g23: ArcOfCircle CenterX=-167.285 CenterY=-8.225 CenterZ=0 NormalX=0 NormalY=0 NormalZ=1 AngleXU=0 Radius=2.375 StartAngle=4.71239 EndAngle=6.28319
    g24: GeomPoint [constr] X=-164.91 Y=-10.6 Z=0
    g25: ArcOfCircle CenterX=-167.535 CenterY=-8.225 CenterZ=0 NormalX=0 NormalY=0 NormalZ=1 AngleXU=0 Radius=2.375 StartAngle=3.14159 EndAngle=4.71239
    g26: GeomPoint [constr] X=-169.91 Y=-10.6 Z=0
    g27: LineSegment [constr] StartX=-181.6 StartY=1.12e-14 StartZ=0 EndX=-152.209 EndY=0 EndZ=0
    g28: LineSegment [constr] StartX=-181.6 StartY=1.12e-14 StartZ=0 EndX=-130.41 EndY=0 EndZ=0
    g29: LineSegment [constr] StartX=-152.209 StartY=0 StartZ=0 EndX=-152.209 EndY=6.95 EndZ=0
    g30: LineSegment [constr] StartX=-130.41 StartY=0 StartZ=0 EndX=-130.41 EndY=-6.95 EndZ=0
    g31: Circle CenterX=-152.209 CenterY=6.95 CenterZ=0 NormalX=0 NormalY=0 NormalZ=1 AngleXU=0 Radius=2.1
    g32: Circle CenterX=-130.41 CenterY=-6.95 CenterZ=0 NormalX=0 NormalY=0 NormalZ=1 AngleXU=0 Radius=2.1
  constraints (79):
    c: Distance(g0) = 11.69
    c: PointOnObject(g0,g-1)
    c: Coincident(g-4,g0)
    c: Distance(g1) = 2.6
    c: Coincident(g1,g0)
    c: Vertical(g1)
    c: Distance(g2) = 2.6
    c: Coincident(g2,g0)
    c: Vertical(g2)
    c: Distance(g18,g12) = 8
    c: Coincident(g18,g2)
    c: Vertical(g3)
    c: Distance(g14,g12) = 5
    c: Horizontal(g4)
    c: Distance(g16,g14) = 8
    c: Vertical(g5)
    c: Distance(g26,g20) = 8
    c: Coincident(g20,g1)
    c: Vertical(g7)
    c: Distance(g26,g24) = 5
    c: Horizontal(g8)
    c: Distance(g24,g22) = 8
    c: Vertical(g9)
    c: PointOnObject(g12,g3)
    c: PointOnObject(g12,g4)
    c: Tangent(g3,g11) = 1.5708
    c: Tangent(g4,g11) = 1.5708
    c: PointOnObject(g14,g5)
    c: PointOnObject(g14,g4)
    c: Tangent(g5,g13) = 1.5708
    c: Tangent(g4,g13) = 1.5708
    c: PointOnObject(g16,g5)
    c: PointOnObject(g16,g6)
    c: Tangent(g5,g15) = 1.5708
    c: Tangent(g6,g15) = 1.5708
    c: PointOnObject(g18,g3)
    c: PointOnObject(g18,g6)
    c: Tangent(g3,g17) = 1.5708
    c: Tangent(g6,g17) = 1.5708
    c: Equal(g11,g13)
    c: Equal(g13,g15)
    c: Equal(g15,g17)
    c: DistanceX(g4,g4) = 0.25
    c: PointOnObject(g20,g7)
    c: PointOnObject(g20,g10)
    c: Tangent(g7,g19) = -1.5708
    c: Tangent(g10,g19) = -1.5708
    c: PointOnObject(g22,g9)
    c: PointOnObject(g22,g10)
    c: Tangent(g9,g21) = -1.5708
    c: Tangent(g10,g21) = -1.5708
    c: PointOnObject(g24,g9)
    c: PointOnObject(g24,g8)
    c: Tangent(g9,g23) = -1.5708
    c: Tangent(g8,g23) = -1.5708
    c: PointOnObject(g26,g8)
    c: PointOnObject(g26,g7)
    c: Tangent(g8,g25) = -1.5708
    c: Tangent(g7,g25) = -1.5708
    c: Equal(g19,g21)
    c: Equal(g21,g23)
    c: Equal(g23,g25)
    c: DistanceX(g10,g10) = 0.25
    c: Distance(g27) = 29.391
    c: Coincident(g27,g0)
    c: PointOnObject(g27,g-1)
    c: Distance(g28) = 51.19
    c: Coincident(g28,g0)
    c: PointOnObject(g28,g-1)
    c: Distance(g29) = 6.95
    c: Coincident(g29,g27)
    c: Vertical(g29)
    c: Distance(g30) = 6.95
    c: Coincident(g30,g28)
    c: Vertical(g30)
    c: Diameter(g31) = 4.2
    c: Diameter(g32) = 4.2
    c: Coincident(g32,g30)
    c: Coincident(g31,g29)
FEATURE [Sketcher::SketchObject] Sketch031  label="fori inferiori switch pompa"
  ArcFitTolerance = 1e-06
  AttachmentSupport = -> [XY_Plane]
  ExternalGeometry = -> [Sketch]
  FullyConstrained = true
  MakeInternals = false
  MapMode = 5
  sketch-geometry (4):
    g0: LineSegment [constr] StartX=-57.2 StartY=1.9e-15 StartZ=0 EndX=-62.45 EndY=1.9e-15 EndZ=0
    g1: LineSegment [constr] StartX=-62.45 StartY=3.25 StartZ=0 EndX=-62.45 EndY=-3.25 EndZ=0
    g2: Circle CenterX=-62.45 CenterY=3.25 CenterZ=0 NormalX=0 NormalY=0 NormalZ=1 AngleXU=0 Radius=1.6
    g3: Circle CenterX=-62.45 CenterY=-3.25 CenterZ=0 NormalX=0 NormalY=0 NormalZ=1 AngleXU=0 Radius=1.6
  constraints (10):
    c: Distance(g0) = 5.25
    c: Coincident(g0,g-3)
    c: PointOnObject(g0,g-3)
    c: Vertical(g1)
    c: DistanceY(g1,g1) = 6.5
    c: Symmetric(g1,g1,g0)
    c: Diameter(g2) = 3.2
    c: Diameter(g3) = 3.2
    c: Coincident(g2,g1)
    c: Coincident(g3,g1)
FEATURE [Sketcher::SketchObject] Sketch032  label="spazio per PILA 18650"
  ArcFitTolerance = 1e-06
  AttachmentSupport = -> [XY_Plane]
  ExternalGeometry = -> [Sketch]
  FullyConstrained = true
  MakeInternals = false
  MapMode = 5
  sketch-geometry (2):
    g0: LineSegment [constr] StartX=-178.142 StartY=-1.74e-14 StartZ=0 EndX=-191.142 EndY=-1.83e-14 EndZ=0
    g1: Circle CenterX=-191.142 CenterY=-1.83e-14 CenterZ=0 NormalX=0 NormalY=0 NormalZ=1 AngleXU=0 Radius=10.5
  constraints (5):
    c: Distance(g0) = 13
    c: Coincident(g0,g-3)
    c: PointOnObject(g0,g-4)
    c: Diameter(g1) = 21
    c: Coincident(g1,g0)
FEATURE [Part::Extrusion] Extrude030  label="Extrude spazio per PILA 18650"
  Base = -> Sketch032
  Dir = (0,0,1)
  DirLink = -> Sketch [Edge45]
  DirMode = 2
  FaceMakerClass = Part::FaceMakerBullseye
  FaceMakerMode = 3
  LengthFwd = 76
  LengthRev = 0
  Placement = pos=(6,0,-72) rot=(0,0,1;0rad)
  Solid = true
  Symmetric = false
FEATURE [Sketcher::SketchObject] Sketch033  label="fermo per scheda micro"
  ArcFitTolerance = 1e-06
  AttachmentSupport = -> [XZ_Plane]
  ExternalGeometry = -> [Sketch]
  FullyConstrained = true
  MakeInternals = false
  MapMode = 5
  Placement = pos=(0,0,0) rot=(1,0,0;1.5708rad)
  sketch-geometry (12):
    g0: LineSegment StartX=-11.6 StartY=6 StartZ=0 EndX=-4 EndY=6 EndZ=0
    g1: LineSegment StartX=-4 StartY=6 StartZ=0 EndX=-4 EndY=36.4 EndZ=0
    g2: LineSegment StartX=-4 StartY=36.4 StartZ=0 EndX=-11.6 EndY=36.4 EndZ=0
    g3: LineSegment StartX=-11.6 StartY=36.4 StartZ=0 EndX=-11.6 EndY=6 EndZ=0
    g4: LineSegment StartX=-80.11 StartY=11.6 StartZ=0 EndX=-70.51 EndY=11.6 EndZ=0
    g5: LineSegment StartX=-70.51 StartY=11.6 StartZ=0 EndX=-70.51 EndY=6 EndZ=0
    g6: LineSegment StartX=-70.51 StartY=6 StartZ=0 EndX=-80.11 EndY=6 EndZ=0
    g7: LineSegment StartX=-80.11 StartY=6 StartZ=0 EndX=-80.11 EndY=11.6 EndZ=0
    g8: LineSegment StartX=-78.51 StartY=36.4 StartZ=0 EndX=-70.51 EndY=36.4 EndZ=0
    g9: LineSegment StartX=-70.51 StartY=36.4 StartZ=0 EndX=-70.51 EndY=30.8 EndZ=0
    g10: LineSegment StartX=-70.51 StartY=30.8 StartZ=0 EndX=-78.51 EndY=30.8 EndZ=0
    g11: LineSegment StartX=-78.51 StartY=30.8 StartZ=0 EndX=-78.51 EndY=36.4 EndZ=0
  constraints (33):
    c: Horizontal(g0)
    c: Coincident(g1,g0)
    c: Coincident(g2,g1)
    c: Horizontal(g2)
    c: Coincident(g3,g2)
    c: Coincident(g3,g0)
    c: Vertical(g3)
    c: DistanceX(g2,g2) = 7.6
    c: Coincident(g1,g-3)
    c: Coincident(g0,g-3)
    c: Horizontal(g4)
    c: Coincident(g5,g4)
    c: Vertical(g5)
    c: Coincident(g6,g5)
    c: Horizontal(g6)
    c: Coincident(g7,g6)
    c: Coincident(g7,g4)
    c: Vertical(g7)
    c: DistanceY(g5,g5) = 5.6
    c: DistanceX(g4,g4) = 9.6
    c: Coincident(g9,g8)
    c: Vertical(g9)
    c: Coincident(g10,g9)
    c: Horizontal(g10)
    c: Coincident(g11,g10)
    c: Coincident(g11,g8)
    c: Vertical(g11)
    c: DistanceY(g9,g9) = 5.6
    c: DistanceX(g10,g10) = 8
    c: Coincident(g4,g-4)
    c: DistanceX(g4,g10) = 1.6
    c: Horizontal(g8)
    c: DistanceY(g8,g1) = 0
FEATURE [Sketcher::SketchObject] Sketch034  label="buchi guida rail"
  ArcFitTolerance = 1e-06
  AttachmentSupport = -> [XY_Plane]
  ExternalGeometry = -> [Sketch]
  FullyConstrained = true
  MakeInternals = false
  MapMode = 5
  sketch-geometry (6):
    g0: LineSegment [constr] StartX=-100.8 StartY=9.1e-15 StartZ=0 EndX=-93.3 EndY=0 EndZ=0
    g1: LineSegment [constr] StartX=-93.3 StartY=0 StartZ=0 EndX=-73.3 EndY=0 EndZ=0
    g2: LineSegment [constr] StartX=-73.3 StartY=0 StartZ=0 EndX=-53.3 EndY=0 EndZ=0
    g3: Circle CenterX=-93.3 CenterY=0 CenterZ=0 NormalX=0 NormalY=0 NormalZ=1 AngleXU=0 Radius=2.5
    g4: Circle CenterX=-73.3 CenterY=0 CenterZ=0 NormalX=0 NormalY=0 NormalZ=1 AngleXU=0 Radius=2.5
    g5: Circle CenterX=-53.3 CenterY=0 CenterZ=0 NormalX=0 NormalY=0 NormalZ=1 AngleXU=0 Radius=2.5
  constraints (15):
    c: Distance(g0) = 7.5
    c: Coincident(g0,g-3)
    c: PointOnObject(g0,g-1)
    c: Distance(g1) = 20
    c: Coincident(g1,g0)
    c: PointOnObject(g1,g-1)
    c: Distance(g2) = 20
    c: Coincident(g2,g1)
    c: PointOnObject(g2,g-1)
    c: Diameter(g3) = 5
    c: Diameter(g4) = 5
    c: Diameter(g5) = 5
    c: Coincident(g3,g0)
    c: Coincident(g4,g1)
    c: Coincident(g5,g2)
FEATURE [Part::Extrusion] Extrude032  label="Extrude buchi guida rail"
  Base = -> Sketch034
  Dir = (0,0,1)
  DirMode = 2
  FaceMakerClass = Part::FaceMakerBullseye
  FaceMakerMode = 3
  LengthFwd = -6.2
  LengthRev = 0
  Placement = pos=(0,0,43.2) rot=(0,0,1;0rad)
  Solid = true
  Symmetric = false
FEATURE [Part::Extrusion] Extrude033  label="Extrude fori superiori per solenoide e oled001"
  Base = -> Sketch030
  Dir = (0,0,1)
  DirMode = 2
  FaceMakerClass = Part::FaceMakerBullseye
  FaceMakerMode = 3
  LengthFwd = -4.8
  LengthRev = 0
  Placement = pos=(0,0,41.2) rot=(0,0,1;0rad)
  Solid = true
  Symmetric = false
FEATURE [Part::Extrusion] Extrude034  label="Extrude fori sotto impugnatura001"
  Base = -> Sketch029
  Dir = (0,0,1)
  DirMode = 2
  FaceMakerClass = Part::FaceMakerBullseye
  FaceMakerMode = 3
  LengthFwd = 5
  LengthRev = 0
  Placement = pos=(0,0,-83) rot=(0,0,1;0rad)
  Solid = true
  Symmetric = false
FEATURE [Part::Extrusion] Extrude035  label="Extrude fori inferiori switch pompa001"
  Base = -> Sketch031
  Dir = (0,0,1)
  DirMode = 2
  FaceMakerClass = Part::FaceMakerBullseye
  FaceMakerMode = 3
  LengthFwd = 4
  LengthRev = 0
  Placement = pos=(0,0,-1.7) rot=(0,0,1;0rad)
  Solid = true
  Symmetric = false
FEATURE [Part::Extrusion] Extrude036  label="Extrude foro sotto posteriore M3x5x007"
  Base = -> Sketch027
  Dir = (0,0,1)
  DirMode = 2
  FaceMakerClass = Part::FaceMakerBullseye
  FaceMakerMode = 3
  LengthFwd = 6.2
  LengthRev = 0
  Placement = pos=(0,0,-9.6) rot=(0,0,1;0rad)
  Solid = true
  Symmetric = false
FEATURE [Part::Extrusion] Extrude037  label="Extrude foro sotto anteriore M3x5x007"
  Base = -> Sketch026
  Dir = (0,0,1)
  DirMode = 2
  FaceMakerClass = Part::FaceMakerBullseye
  FaceMakerMode = 3
  LengthFwd = 6.2
  LengthRev = 0
  Solid = true
  Symmetric = false
FEATURE [Sketcher::SketchObject] Sketch035  label="foro per fissaggio micro"
  ArcFitTolerance = 1e-06
  AttachmentSupport = -> [XZ_Plane]
  ExternalGeometry = -> [Sketch,Sketch033]
  FullyConstrained = true
  MakeInternals = false
  MapMode = 5
  Placement = pos=(0,0,0) rot=(1,0,0;1.5708rad)
  sketch-geometry (3):
    g0: Circle CenterX=-7.8 CenterY=21.2 CenterZ=0 NormalX=0 NormalY=0 NormalZ=1 AngleXU=0 Radius=1.6
    g1: GeomPoint [constr] X=-4 Y=21.2 Z=0
    g2: LineSegment [constr] StartX=-4 StartY=21.2 StartZ=0 EndX=-11.6 EndY=21.2 EndZ=0
  constraints (6):
    c: Diameter(g0) = 3.2
    c: Symmetric(g-3,g-3,g1)
    c: Coincident(g2,g1)
    c: Horizontal(g2)
    c: DistanceX(g-4,g2) = 0
    c: Symmetric(g2,g1,g0)
FEATURE [Part::Extrusion] Extrude038  label="Extrude foro per fissaggio micro"
  Base = -> Sketch035
  Dir = (0,-1,2e-16)
  DirMode = 2
  FaceMakerClass = Part::FaceMakerBullseye
  FaceMakerMode = 3
  LengthFwd = 3
  LengthRev = 0
  Placement = pos=(0,8.6,0) rot=(0,0,1;0rad)
  Solid = true
  Symmetric = false
FEATURE [Sketcher::SketchObject] Sketch036  label="supporto per alimentatore"
  ArcFitTolerance = 1e-06
  AttachmentSupport = -> [XZ_Plane]
  ExternalGeometry = -> [Sketch,Sketch016,Sketch022]
  FullyConstrained = true
  MakeInternals = false
  MapMode = 5
  Placement = pos=(0,0,0) rot=(1,0,0;1.5708rad)
  sketch-geometry (5):
    g0: LineSegment StartX=-211.843 StartY=-50.0944 StartZ=0 EndX=-211.843 EndY=-80.4316 EndZ=0
    g1: LineSegment StartX=-211.843 StartY=-50.0944 StartZ=0 EndX=-207.775 EndY=-41.3701 EndZ=0
    g2: LineSegment [constr] StartX=-209.443 StartY=-50.0944 StartZ=0 EndX=-209.443 EndY=-80.4316 EndZ=0
    g3: LineSegment StartX=-207.775 StartY=-41.3701 StartZ=0 EndX=-207.775 EndY=-80.4316 EndZ=0
    g4: LineSegment StartX=-211.843 StartY=-80.4316 StartZ=0 EndX=-207.775 EndY=-80.4316 EndZ=0
  constraints (15):
    c: Vertical(g0)
    c: Coincident(g1,g0)
    c: Vertical(g2)
    c: Tangent(g2,g-5)
    c: Coincident(g3,g1)
    c: Vertical(g3)
    c: DistanceY(g-3,g3) = -2
    c: Tangent(g1,g-8)
    c: DistanceY(g-3,g0) = -2
    c: Coincident(g4,g0)
    c: Coincident(g4,g3)
    c: Tangent(g0,g-6)
    c: DistanceY(g-3,g2) = -2
    c: DistanceY(g2,g0) = 0
    c: DistanceX(g-3,g3) = 6.8
FEATURE [Part::Extrusion] Extrude039  label="Extrude039 supporto alimentatore"
  Base = -> Sketch036
  Dir = (0,-1,2e-16)
  DirMode = 2
  FaceMakerClass = Part::FaceMakerBullseye
  FaceMakerMode = 3
  LengthFwd = 25.2
  LengthRev = 0
  Solid = true
  Symmetric = true
FEATURE [Sketcher::SketchObject] Sketch037  label="scavo per alimentatore"
  ArcFitTolerance = 1e-06
  AttachmentSupport = -> [XZ_Plane]
  ExternalGeometry = -> [Sketch036]
  FullyConstrained = true
  MakeInternals = false
  MapMode = 5
  Placement = pos=(0,0,0) rot=(1,0,0;1.5708rad)
  sketch-geometry (4):
    g0: LineSegment StartX=-209.575 StartY=-50.4316 StartZ=0 EndX=-209.575 EndY=-80.4316 EndZ=0
    g1: LineSegment StartX=-209.575 StartY=-50.4316 StartZ=0 EndX=-207.775 EndY=-50.4316 EndZ=0
    g2: LineSegment StartX=-207.775 StartY=-50.4316 StartZ=0 EndX=-207.775 EndY=-80.4316 EndZ=0
    g3: LineSegment StartX=-207.775 StartY=-80.4316 StartZ=0 EndX=-209.575 EndY=-80.4316 EndZ=0
  constraints (11):
    c: Vertical(g0)
    c: Coincident(g1,g0)
    c: Horizontal(g1)
    c: Coincident(g2,g1)
    c: Vertical(g2)
    c: Coincident(g3,g2)
    c: Coincident(g3,g0)
    c: Horizontal(g3)
    c: DistanceX(g1,g1) = 1.8
    c: Coincident(g2,g-3)
    c: DistanceY(g2,g2) = 30
FEATURE [Part::Extrusion] Extrude040  label="Extrude040 scavo alimentatore"
  Base = -> Sketch037
  Dir = (0,-1,2e-16)
  DirMode = 2
  FaceMakerClass = Part::FaceMakerBullseye
  FaceMakerMode = 3
  LengthFwd = 19.5
  LengthRev = 0
  Solid = true
  Symmetric = true
FEATURE [Part::Extrusion] Extrude031  label="Extrude fermo per scheda micro"
  Base = -> Sketch033
  Dir = (0,-1,2e-16)
  DirMode = 2
  FaceMakerClass = Part::FaceMakerBullseye
  FaceMakerMode = 3
  LengthFwd = 3
  LengthRev = 0
  Placement = pos=(0,8.6,0) rot=(0,0,1;0rad)
  Solid = true
  Symmetric = false
FEATURE [Sketcher::SketchObject] Sketch038  label="scavo driver solenoide"
  ArcFitTolerance = 1e-06
  AttachmentSupport = -> [XZ_Plane]
  ExternalGeometry = -> [Sketch,Sketch036]
  FullyConstrained = true
  MakeInternals = false
  MapMode = 5
  Placement = pos=(0,0,0) rot=(1,0,0;1.5708rad)
  sketch-geometry (7):
    g0: LineSegment StartX=-192.222 StartY=-8.0175 StartZ=0 EndX=-194.941 EndY=-6.74965 EndZ=0
    g1: LineSegment StartX=-194.941 StartY=-6.74965 StartZ=0 EndX=-212.269 EndY=-43.9083 EndZ=0
    g2: LineSegment StartX=-192.222 StartY=-8.0175 StartZ=0 EndX=-188.779 EndY=-9.62345 EndZ=0
    g3: LineSegment StartX=-188.779 StartY=-9.62345 StartZ=0 EndX=-205.357 EndY=-45.1761 EndZ=0
    g4: LineSegment StartX=-205.357 StartY=-45.1761 StartZ=0 EndX=-209.55 EndY=-45.1761 EndZ=0
    g5: LineSegment [constr] StartX=-212.269 StartY=-43.9083 StartZ=0 EndX=-209.55 EndY=-45.1761 EndZ=0
    g6: LineSegment StartX=-212.269 StartY=-43.9083 StartZ=0 EndX=-209.55 EndY=-45.1761 EndZ=0
  constraints (20):
    c: Coincident(g1,g0)
    c: Coincident(g3,g2)
    c: Coincident(g4,g3)
    c: Distance(g2) = 3.8
    c: Distance(g1) = 41
    c: Coincident(g5,g1)
    c: Distance(g5) = 3
    c: Perpendicular(g5,g-3)
    c: Parallel(g1,g-3)
    c: Perpendicular(g1,g0)
    c: Distance(g0) = 3
    c: Coincident(g6,g1)
    c: Parallel(g3,g-3)
    c: Perpendicular(g2,g3)
    c: Coincident(g2,g0)
    c: Perpendicular(g-4,g4)
    c: PointOnObject(g5,g-3)
    c: Distance(g-3,g5) = 9.6
    c: Coincident(g4,g5)
    c: Coincident(g6,g4)
FEATURE [Part::Extrusion] Extrude041  label="Extrude scavo driver solenoide"
  Base = -> Sketch038
  Dir = (0,-1,2e-16)
  DirMode = 2
  FaceMakerClass = Part::FaceMakerBullseye
  FaceMakerMode = 3
  LengthFwd = 20.6
  LengthRev = 0
  Solid = true
  Symmetric = true
FEATURE [Sketcher::SketchObject] Sketch039  label="scavo per cavo usb per micro"
  ArcFitTolerance = 1e-06
  AttachmentSupport = -> [XZ_Plane]
  ExternalGeometry = -> [Sketch,Sketch016]
  FullyConstrained = true
  MakeInternals = false
  MapMode = 5
  Placement = pos=(0,0,0) rot=(1,0,0;1.5708rad)
  sketch-geometry (4):
    g0: LineSegment StartX=-82.51 StartY=36.4 StartZ=0 EndX=-74.51 EndY=36.4 EndZ=0
    g1: LineSegment StartX=-74.51 StartY=36.4 StartZ=0 EndX=-74.51 EndY=30.8 EndZ=0
    g2: LineSegment StartX=-74.51 StartY=30.8 StartZ=0 EndX=-82.51 EndY=30.8 EndZ=0
    g3: LineSegment StartX=-82.51 StartY=30.8 StartZ=0 EndX=-82.51 EndY=36.4 EndZ=0
  constraints (11):
    c: Coincident(g1,g0)
    c: Vertical(g1)
    c: Coincident(g2,g1)
    c: Horizontal(g2)
    c: Coincident(g3,g2)
    c: Coincident(g3,g0)
    c: Vertical(g3)
    c: Tangent(g0,g-3)
    c: Tangent(g2,g-4)
    c: Tangent(g3,g-4)
    c: Tangent(g1,g-4)
FEATURE [Part::Extrusion] Extrude042  label="Extrude scavo per cavo usb per micro"
  Base = -> Sketch039
  Dir = (0,-1,2e-16)
  DirMode = 2
  FaceMakerClass = Part::FaceMakerBullseye
  FaceMakerMode = 3
  LengthFwd = 11.2
  LengthRev = 0
  Solid = true
  Symmetric = true
FEATURE [Sketcher::SketchObject] Sketch040  label="scavo saldature alimentatore connettore 5v"
  ArcFitTolerance = 1e-06
  AttachmentSupport = -> [XZ_Plane]
  ExternalGeometry = -> [Sketch037]
  FullyConstrained = true
  MakeInternals = false
  MapMode = 5
  Placement = pos=(0,0,0) rot=(1,0,0;1.5708rad)
  sketch-geometry (4):
    g0: LineSegment StartX=-211.175 StartY=-52.4316 StartZ=0 EndX=-211.175 EndY=-56.4316 EndZ=0
    g1: LineSegment StartX=-211.175 StartY=-52.4316 StartZ=0 EndX=-209.575 EndY=-52.4316 EndZ=0
    g2: LineSegment StartX=-209.575 StartY=-52.4316 StartZ=0 EndX=-209.575 EndY=-56.4316 EndZ=0
    g3: LineSegment StartX=-209.575 StartY=-56.4316 StartZ=0 EndX=-211.175 EndY=-56.4316 EndZ=0
  constraints (11):
    c: Vertical(g0)
    c: Coincident(g1,g0)
    c: Horizontal(g1)
    c: Coincident(g2,g1)
    c: Coincident(g3,g2)
    c: Coincident(g3,g0)
    c: Horizontal(g3)
    c: DistanceX(g1,g1) = 1.6
    c: DistanceY(g2,g2) = 4
    c: Tangent(g2,g-3)
    c: DistanceY(g1,g-3) = 2
FEATURE [Part::Extrusion] Extrude043  label="Extrude scavo saldature alimentatore connettore 5v"
  Base = -> Sketch040
  Dir = (0,-1,2e-16)
  DirMode = 2
  FaceMakerClass = Part::FaceMakerBullseye
  FaceMakerMode = 3
  LengthFwd = 8
  LengthRev = 0
  Solid = true
  Symmetric = true
FEATURE [Sketcher::SketchObject] Sketch041  label="scavo saldature alimentatore connettore 5v verticali"
  ArcFitTolerance = 1e-06
  AttachmentSupport = -> [XZ_Plane]
  ExternalGeometry = -> [Sketch037]
  FullyConstrained = true
  MakeInternals = false
  MapMode = 5
  Placement = pos=(0,0,0) rot=(1,0,0;1.5708rad)
  sketch-geometry (4):
    g0: LineSegment StartX=-211.175 StartY=-53.6316 StartZ=0 EndX=-209.575 EndY=-53.6316 EndZ=0
    g1: LineSegment StartX=-209.575 StartY=-53.6316 StartZ=0 EndX=-209.575 EndY=-76.6316 EndZ=0
    g2: LineSegment StartX=-209.575 StartY=-76.6316 StartZ=0 EndX=-211.175 EndY=-76.6316 EndZ=0
    g3: LineSegment StartX=-211.175 StartY=-76.6316 StartZ=0 EndX=-211.175 EndY=-53.6316 EndZ=0
  constraints (11):
    c: Horizontal(g0)
    c: Coincident(g1,g0)
    c: Coincident(g2,g1)
    c: Horizontal(g2)
    c: Coincident(g3,g2)
    c: Coincident(g3,g0)
    c: Vertical(g3)
    c: DistanceY(g3,g3) = 23
    c: DistanceX(g0,g0) = 1.6
    c: Tangent(g1,g-3)
    c: DistanceY(g0,g-3) = 3.2
FEATURE [Part::Extrusion] Extrude044  label="Extrude scavo saldature alimentatore connettore 5v verticali"
  Base = -> Sketch041
  Dir = (0,-1,2e-16)
  DirMode = 2
  FaceMakerClass = Part::FaceMakerBullseye
  FaceMakerMode = 3
  LengthFwd = 3.2
  LengthRev = 0
  Placement = pos=(0,8.3,0) rot=(0,0,1;0rad)
  Solid = true
  Symmetric = false
FEATURE [Sketcher::SketchObject] Sketch042  label="fermi per driver solenoide e alimentatore"
  ArcFitTolerance = 1e-06
  AttachmentSupport = -> [XZ_Plane]
  ExternalGeometry = -> [Sketch036,Sketch037,Sketch,Sketch038]
  FullyConstrained = true
  MakeInternals = false
  MapMode = 5
  Placement = pos=(0,0,0) rot=(1,0,0;1.5708rad)
  sketch-geometry (27):
    g0: LineSegment StartX=-200.506 StartY=-25.7811 StartZ=0 EndX=-201.436 EndY=-27.775 EndZ=0
    g1: LineSegment StartX=-201.436 StartY=-27.775 StartZ=0 EndX=-199.442 EndY=-28.7048 EndZ=0
    g2: LineSegment StartX=-199.442 StartY=-28.7048 StartZ=0 EndX=-198.512 EndY=-26.7109 EndZ=0
    g3: LineSegment StartX=-198.512 StartY=-26.7109 StartZ=0 EndX=-200.506 EndY=-25.7811 EndZ=0
    g4: LineSegment StartX=-201.28 StartY=-23.6549 StartZ=0 EndX=-203.562 EndY=-28.5489 EndZ=0
    g5: LineSegment StartX=-203.562 StartY=-28.5489 StartZ=0 EndX=-200.118 EndY=-30.1549 EndZ=0
    g6: LineSegment StartX=-197.992 StartY=-29.381 StartZ=0 EndX=-197.062 EndY=-27.3871 EndZ=0
    g7: LineSegment StartX=-197.836 StartY=-25.2608 StartZ=0 EndX=-201.28 EndY=-23.6549 EndZ=0
    g8: LineSegment [constr] StartX=-198.668 StartY=-30.8311 StartZ=0 EndX=-197.992 EndY=-29.381 EndZ=0
    g9: LineSegment [constr] StartX=-198.668 StartY=-30.8311 StartZ=0 EndX=-200.118 EndY=-30.1549 EndZ=0
    g10: ArcOfCircle CenterX=-198.512 CenterY=-26.7109 CenterZ=0 NormalX=0 NormalY=0 NormalZ=1 AngleXU=0 Radius=1.6 StartAngle=5.84685 EndAngle=7.41765
    g11: GeomPoint [constr] X=-196.386 Y=-25.937 Z=0
    g12: ArcOfCircle CenterX=-199.442 CenterY=-28.7048 CenterZ=0 NormalX=0 NormalY=0 NormalZ=1 AngleXU=0 Radius=1.6 StartAngle=4.27606 EndAngle=5.84685
    g13: GeomPoint [constr] X=-198.668 Y=-30.8311 Z=0
    g14: LineSegment StartX=-207.775 StartY=-46.8316 StartZ=0 EndX=-207.775 EndY=-50.8316 EndZ=0
    g15: LineSegment StartX=-207.775 StartY=-46.8316 StartZ=0 EndX=-203.775 EndY=-46.8316 EndZ=0
    g16: LineSegment StartX=-203.775 StartY=-46.8316 StartZ=0 EndX=-203.775 EndY=-50.8316 EndZ=0
    g17: LineSegment StartX=-207.775 StartY=-50.8316 StartZ=0 EndX=-203.775 EndY=-50.8316 EndZ=0
    g18: LineSegment StartX=-209.375 StartY=-52.4316 StartZ=0 EndX=-203.775 EndY=-52.4316 EndZ=0
    g19: LineSegment StartX=-202.175 StartY=-50.8316 StartZ=0 EndX=-202.175 EndY=-46.8316 EndZ=0
    g20: LineSegment StartX=-203.775 StartY=-45.2316 StartZ=0 EndX=-209.375 EndY=-45.2316 EndZ=0
    g21: LineSegment StartX=-209.375 StartY=-45.2316 StartZ=0 EndX=-209.375 EndY=-52.4316 EndZ=0
    g22: ArcOfCircle CenterX=-203.775 CenterY=-46.8316 CenterZ=0 NormalX=0 NormalY=0 NormalZ=1 AngleXU=0 Radius=1.6 StartAngle=1.8e-15 EndAngle=1.5708
    g23: GeomPoint [constr] X=-202.175 Y=-45.2316 Z=0
    g24: ArcOfCircle CenterX=-203.775 CenterY=-50.8316 CenterZ=0 NormalX=0 NormalY=0 NormalZ=1 AngleXU=0 Radius=1.6 StartAngle=4.71239 EndAngle=6.28319
    g25: GeomPoint [constr] X=-202.175 Y=-52.4316 Z=0
    g26: LineSegment [constr] StartX=-207.775 StartY=-50.4316 StartZ=0 EndX=-207.775 EndY=-50.8316 EndZ=0
  constraints (69):
    c: Coincident(g1,g0)
    c: Coincident(g2,g1)
    c: Coincident(g3,g2)
    c: Coincident(g3,g0)
    c: Parallel(g0,g2)
    c: Perpendicular(g3,g0)
    c: Perpendicular(g1,g0)
    c: Coincident(g5,g4)
    c: Coincident(g7,g4)
    c: Distance(g3) = 2.2
    c: Distance(g2) = 2.2
    c: Parallel(g6,g2)
    c: Parallel(g6,g4)
    c: Perpendicular(g5,g6)
    c: Perpendicular(g7,g6)
    c: Distance(g13,g11) = 5.4
    c: Distance(g5,g13) = 5.4
    c: Coincident(g9,g8)
    c: Distance(g8) = 1.6
    c: Distance(g9) = 1.6
    c: Perpendicular(g9,g8)
    c: Parallel(g8,g6)
    c: Coincident(g8,g13)
    c: Distance(g8,g1) = 1.6
    c: Distance(g9,g1) = 1.6
    c: Tangent(g0,g-5)
    c: Distance(g0,g-6) = 19.2
    c: PointOnObject(g11,g7)
    c: PointOnObject(g11,g6)
    c: Tangent(g7,g10) = -1.5708
    c: Tangent(g6,g10) = -1.5708
    c: PointOnObject(g13,g5)
    c: Tangent(g5,g12) = -1.5708
    c: Tangent(g6,g12) = -1.5708
    c: Equal(g10,g12)
    c: Coincident(g10,g2)
    c: Vertical(g14)
    c: Coincident(g15,g14)
    c: Horizontal(g15)
    c: Coincident(g16,g15)
    c: Vertical(g16)
    c: Coincident(g17,g14)
    c: Coincident(g17,g16)
    c: Horizontal(g17)
    c: Distance(g16) = 4
    c: Distance(g15) = 4
    c: Horizontal(g18)
    c: Vertical(g19)
    c: Horizontal(g20)
    c: Coincident(g21,g20)
    c: Coincident(g21,g18)
    c: Vertical(g21)
    c: Distance(g20,g23) = 7.2
    c: Distance(g25,g23) = 7.2
    c: DistanceY(g18,g14) = 1.6
    c: DistanceX(g18,g14) = 1.6
    c: PointOnObject(g23,g20)
    c: PointOnObject(g23,g19)
    c: Tangent(g20,g22) = -1.5708
    c: Tangent(g19,g22) = -1.5708
    c: PointOnObject(g25,g19)
    c: Tangent(g18,g24) = -1.5708
    c: Tangent(g19,g24) = -1.5708
    c: Equal(g22,g24)
    c: Coincident(g22,g15)
    c: Vertical(g26)
    c: Distance(g26) = 0.4
    c: Coincident(g26,g-4)
    c: Coincident(g14,g26)
FEATURE [Part::Extrusion] Extrude045  label="Extrude fermi per driver solenoide e alimentatore"
  Base = -> Sketch042
  Dir = (0,-1,2e-16)
  DirMode = 2
  FaceMakerClass = Part::FaceMakerBullseye
  FaceMakerMode = 3
  LengthFwd = 25.2
  LengthRev = 0
  Solid = true
  Symmetric = true
FEATURE [Sketcher::SketchObject] Sketch043  label="scavo pulizia fermo alimentatore"
  ArcFitTolerance = 1e-06
  AttachmentSupport = -> [XZ_Plane]
  ExternalGeometry = -> [Sketch042,Sketch036,Sketch037]
  FullyConstrained = true
  MakeInternals = false
  MapMode = 5
  Placement = pos=(0,0,0) rot=(1,0,0;1.5708rad)
  sketch-geometry (6):
    g0: LineSegment StartX=-209.375 StartY=-52.4316 StartZ=0 EndX=-209.375 EndY=-50.4316 EndZ=0
    g1: LineSegment StartX=-209.375 StartY=-50.4316 StartZ=0 EndX=-207.775 EndY=-50.4316 EndZ=0
    g2: LineSegment StartX=-207.775 StartY=-50.4316 StartZ=0 EndX=-207.775 EndY=-45.2316 EndZ=0
    g3: LineSegment StartX=-207.775 StartY=-45.2316 StartZ=0 EndX=-202.175 EndY=-45.2316 EndZ=0
    g4: LineSegment StartX=-202.175 StartY=-45.2316 StartZ=0 EndX=-202.175 EndY=-52.4316 EndZ=0
    g5: LineSegment StartX=-202.175 StartY=-52.4316 StartZ=0 EndX=-209.375 EndY=-52.4316 EndZ=0
  constraints (13):
    c: Vertical(g0)
    c: Coincident(g1,g0)
    c: Coincident(g2,g1)
    c: Coincident(g3,g2)
    c: Coincident(g4,g3)
    c: Coincident(g5,g4)
    c: Coincident(g5,g0)
    c: Horizontal(g5)
    c: Coincident(g0,g-6)
    c: Tangent(g1,g-8)
    c: Tangent(g2,g-4)
    c: Tangent(g3,g-7)
    c: Tangent(g4,g-3)
FEATURE [Part::Extrusion] Extrude046  label="Extrude scavo pulizia fermo alimentatore"
  Base = -> Sketch043
  Dir = (0,-1,2e-16)
  DirMode = 2
  FaceMakerClass = Part::FaceMakerBullseye
  FaceMakerMode = 3
  LengthFwd = 19.5
  LengthRev = 0
  Solid = true
  Symmetric = true
FEATURE [Sketcher::SketchObject] Sketch044  label="buchini per fissaggio oled"
  ArcFitTolerance = 1e-06
  AttachmentSupport = -> [YZ_Plane]
  ExternalGeometry = -> [Sketch]
  FullyConstrained = true
  MakeInternals = false
  MapMode = 5
  Placement = pos=(0,0,0) rot=(0.57735,0.57735,0.57735;2.0944rad)
  sketch-geometry (5):
    g0: LineSegment [constr] StartX=1.5e-14 StartY=67.3588 StartZ=0 EndX=0 EndY=64.3588 EndZ=0
    g1: LineSegment [constr] StartX=0 StartY=64.3588 StartZ=0 EndX=10.4 EndY=64.3588 EndZ=0
    g2: LineSegment [constr] StartX=0 StartY=64.3588 StartZ=0 EndX=-10.4 EndY=64.3588 EndZ=0
    g3: Circle CenterX=10.4 CenterY=64.3588 CenterZ=0 NormalX=0 NormalY=0 NormalZ=1 AngleXU=0 Radius=1.5
    g4: Circle CenterX=-10.4 CenterY=64.3588 CenterZ=0 NormalX=0 NormalY=0 NormalZ=1 AngleXU=0 Radius=1.5
  constraints (13):
    c: Distance(g0) = 3
    c: PointOnObject(g0,g-2)
    c: Coincident(g1,g0)
    c: Horizontal(g1)
    c: Coincident(g2,g0)
    c: Horizontal(g2)
    c: DistanceX(g1,g1) = 10.4
    c: Coincident(g3,g1)
    c: Diameter(g4) = 3
    c: Coincident(g4,g2)
    c: Coincident(g0,g-7)
    c: Equal(g1,g2)
    c: Equal(g4,g3)
FEATURE [Part::Extrusion] Extrude047  label="Extrude buchini per fissaggio oled"
  Base = -> Sketch044
  Dir = (1,0,0)
  DirMode = 2
  FaceMakerClass = Part::FaceMakerBullseye
  FaceMakerMode = 3
  LengthFwd = 10
  LengthRev = 0
  Placement = pos=(-186,0,0) rot=(0,0,1;0rad)
  Solid = true
  Symmetric = false
FEATURE [Sketcher::SketchObject] Sketch046  label="scavo 5x5 neopixel"
  ArcFitTolerance = 1e-06
  AttachmentSupport = -> [YZ_Plane002]
  FullyConstrained = true
  MakeInternals = false
  MapMode = 5
  Placement = pos=(0,0,0) rot=(0.57735,0.57735,0.57735;2.0944rad)
  sketch-geometry (4):
    g0: LineSegment StartX=-2.7 StartY=2.7 StartZ=0 EndX=2.7 EndY=2.7 EndZ=0
    g1: LineSegment StartX=2.7 StartY=2.7 StartZ=0 EndX=2.7 EndY=-2.7 EndZ=0
    g2: LineSegment StartX=2.7 StartY=-2.7 StartZ=0 EndX=-2.7 EndY=-2.7 EndZ=0
    g3: LineSegment StartX=-2.7 StartY=-2.7 StartZ=0 EndX=-2.7 EndY=2.7 EndZ=0
  constraints (11):
    c: Horizontal(g0)
    c: Coincident(g1,g0)
    c: Vertical(g1)
    c: Coincident(g2,g1)
    c: Horizontal(g2)
    c: Coincident(g3,g2)
    c: Coincident(g3,g0)
    c: Vertical(g3)
    c: DistanceX(g0,g0) = 5.4
    c: DistanceY(g1,g1) = 5.4
    c: Symmetric(g0,g1,g-1)
FEATURE [Sketcher::SketchObject] Sketch047  label="scavo 10x10 neopixel corpo"
  ArcFitTolerance = 1e-06
  AttachmentOffset = pos=(0,0,1) rot=(0,0,1;0rad)
  AttachmentSupport = -> [YZ_Plane002]
  FullyConstrained = true
  MakeInternals = false
  MapMode = 5
  Placement = pos=(1,0,0) rot=(0.57735,0.57735,0.57735;2.0944rad)
  sketch-geometry (4):
    g0: LineSegment StartX=-5 StartY=5.1 StartZ=0 EndX=5 EndY=5.1 EndZ=0
    g1: LineSegment StartX=5 StartY=5.1 StartZ=0 EndX=5 EndY=-5.1 EndZ=0
    g2: LineSegment StartX=5 StartY=-5.1 StartZ=0 EndX=-5 EndY=-5.1 EndZ=0
    g3: LineSegment StartX=-5 StartY=-5.1 StartZ=0 EndX=-5 EndY=5.1 EndZ=0
  constraints (11):
    c: Horizontal(g0)
    c: Coincident(g1,g0)
    c: Vertical(g1)
    c: Coincident(g2,g1)
    c: Horizontal(g2)
    c: Coincident(g3,g2)
    c: Coincident(g3,g0)
    c: Vertical(g3)
    c: DistanceX(g0,g0) = 10
    c: DistanceY(g1,g1) = 10.2
    c: Symmetric(g0,g2,g-1)
FEATURE [Sketcher::SketchObject] Sketch048  label="buco per perno blocco neopixel"
  ArcFitTolerance = 1e-06
  AttachmentSupport = -> [XZ_Plane002]
  FullyConstrained = true
  MakeInternals = false
  MapMode = 5
  Placement = pos=(0,0,0) rot=(1,0,0;1.5708rad)
  sketch-geometry (4):
    g0: LineSegment StartX=3 StartY=1.2 StartZ=0 EndX=3 EndY=-1.2 EndZ=0
    g1: LineSegment StartX=3 StartY=-1.2 StartZ=0 EndX=5.4 EndY=-1.2 EndZ=0
    g2: LineSegment StartX=5.4 StartY=-1.2 StartZ=0 EndX=5.4 EndY=1.2 EndZ=0
    g3: LineSegment StartX=5.4 StartY=1.2 StartZ=0 EndX=3 EndY=1.2 EndZ=0
  constraints (11):
    c: Coincident(g1,g0)
    c: Horizontal(g1)
    c: Coincident(g2,g1)
    c: Vertical(g2)
    c: Coincident(g3,g2)
    c: Coincident(g3,g0)
    c: Horizontal(g3)
    c: DistanceX(g1,g1) = 2.4
    c: DistanceY(g2,g2) = 2.4
    c: Symmetric(g0,g0,g-1)
    c: DistanceX(g-1,g0) = 3
FEATURE [Sketcher::SketchObject] Sketch045  label="blocco principale per neopixel"
  ArcFitTolerance = 1e-06
  AttachmentSupport = -> [XZ_Plane002]
  ExternalGeometry = -> [Sketch048]
  FullyConstrained = true
  MakeInternals = false
  MapMode = 5
  Placement = pos=(0,0,0) rot=(1,0,0;1.5708rad)
  sketch-geometry (6):
    g0: LineSegment StartX=0 StartY=5.1 StartZ=0 EndX=0 EndY=-5.1 EndZ=0
    g1: LineSegment StartX=0 StartY=-5.1 StartZ=0 EndX=3 EndY=-5.1 EndZ=0
    g2: LineSegment StartX=7 StartY=-1.1 StartZ=0 EndX=7 EndY=5.1 EndZ=0
    g3: LineSegment StartX=7 StartY=5.1 StartZ=0 EndX=0 EndY=5.1 EndZ=0
    g4: ArcOfCircle CenterX=3 CenterY=-1.1 CenterZ=0 NormalX=0 NormalY=0 NormalZ=1 AngleXU=0 Radius=4 StartAngle=4.71239 EndAngle=6.28319
    g5: GeomPoint [constr] X=7 Y=-5.1 Z=0
  constraints (15):
    c: Vertical(g0)
    c: Coincident(g1,g0)
    c: Horizontal(g1)
    c: Vertical(g2)
    c: Coincident(g3,g2)
    c: Coincident(g3,g0)
    c: Horizontal(g3)
    c: DistanceY(g0,g0) = 10.2
    c: Symmetric(g0,g0,g-1)
    c: DistanceX(g3,g3) = 7
    c: PointOnObject(g5,g2)
    c: PointOnObject(g5,g1)
    c: Tangent(g2,g4) = -1.5708
    c: Tangent(g1,g4) = -1.5708
    c: DistanceX(g-3,g1) = 0
FEATURE [Sketcher::SketchObject] Sketch049  label="rinforzi esterni per corpo neopoixel"
  ArcFitTolerance = 1e-06
  AttachmentSupport = -> [XZ_Plane002]
  ExternalGeometry = -> [Sketch045]
  FullyConstrained = true
  MakeInternals = false
  MapMode = 5
  Placement = pos=(0,0,0) rot=(1,0,0;1.5708rad)
  sketch-geometry (8):
    g0: LineSegment StartX=1 StartY=-4.1 StartZ=0 EndX=2 EndY=-4.1 EndZ=0
    g1: LineSegment StartX=2 StartY=-4.1 StartZ=0 EndX=2 EndY=-5.1 EndZ=0
    g2: LineSegment StartX=2 StartY=-5.1 StartZ=0 EndX=1 EndY=-5.1 EndZ=0
    g3: LineSegment StartX=1 StartY=-5.1 StartZ=0 EndX=1 EndY=-4.1 EndZ=0
    g4: LineSegment StartX=1 StartY=5.1 StartZ=0 EndX=2 EndY=5.1 EndZ=0
    g5: LineSegment StartX=2 StartY=5.1 StartZ=0 EndX=2 EndY=4.1 EndZ=0
    g6: LineSegment StartX=2 StartY=4.1 StartZ=0 EndX=1 EndY=4.1 EndZ=0
    g7: LineSegment StartX=1 StartY=4.1 StartZ=0 EndX=1 EndY=5.1 EndZ=0
  constraints (24):
    c: Horizontal(g0)
    c: Coincident(g1,g0)
    c: Vertical(g1)
    c: Coincident(g2,g1)
    c: Horizontal(g2)
    c: Coincident(g3,g2)
    c: Coincident(g3,g0)
    c: Vertical(g3)
    c: Horizontal(g4)
    c: Coincident(g5,g4)
    c: Vertical(g5)
    c: Coincident(g6,g5)
    c: Horizontal(g6)
    c: Coincident(g7,g6)
    c: Coincident(g7,g4)
    c: Vertical(g7)
    c: DistanceX(g4,g4) = 1
    c: DistanceY(g5,g5) = 1
    c: DistanceX(g0,g0) = 1
    c: DistanceY(g1,g1) = 1
    c: DistanceX(g-3,g4) = 1
    c: DistanceY(g-3,g4) = 0
    c: DistanceX(g-4,g2) = 1
    c: DistanceY(g2,g-4) = 0
FEATURE [Sketcher::SketchObject] Sketch052  label="scavo saldature driver solenoide"
  ArcFitTolerance = 1e-06
  AttachmentSupport = -> [XZ_Plane]
  ExternalGeometry = -> [Sketch038]
  FullyConstrained = true
  MakeInternals = false
  MapMode = 5
  Placement = pos=(0,0,0) rot=(1,0,0;1.5708rad)
  sketch-geometry (4):
    g0: LineSegment StartX=-195.304 StartY=-6.5806 StartZ=0 EndX=-196.994 EndY=-10.2058 EndZ=0
    g1: LineSegment StartX=-196.994 StartY=-10.2058 StartZ=0 EndX=-196.632 EndY=-10.3749 EndZ=0
    g2: LineSegment StartX=-196.632 StartY=-10.3749 StartZ=0 EndX=-194.941 EndY=-6.74965 EndZ=0
    g3: LineSegment StartX=-194.941 StartY=-6.74965 StartZ=0 EndX=-195.304 EndY=-6.5806 EndZ=0
  constraints (11):
    c: Coincident(g1,g0)
    c: Coincident(g2,g1)
    c: Coincident(g3,g2)
    c: Coincident(g3,g0)
    c: Parallel(g2,g0)
    c: Perpendicular(g2,g3)
    c: Perpendicular(g1,g2,g1) = 1.5708
    c: Parallel(g2,g-3)
    c: Distance(g2) = 4
    c: Distance(g3) = 0.4
    c: Coincident(g2,g-3)
FEATURE [Part::Extrusion] Extrude055  label="Extrude scavo saldature driver solenoide"
  Base = -> Sketch052
  Dir = (0,-1,2e-16)
  DirMode = 2
  FaceMakerClass = Part::FaceMakerBullseye
  FaceMakerMode = 3
  LengthFwd = 6
  LengthRev = 0
  Solid = true
  Symmetric = true
FEATURE [Sketcher::SketchObject] Sketch053  label="scavo saldature rumble"
  ArcFitTolerance = 1e-06
  AttachmentSupport = -> [XZ_Plane]
  ExternalGeometry = -> [Sketch019]
  FullyConstrained = true
  MakeInternals = false
  MapMode = 5
  Placement = pos=(0,0,0) rot=(1,0,0;1.5708rad)
  sketch-geometry (4):
    g0: LineSegment StartX=-169.451 StartY=-56.8615 StartZ=0 EndX=-170.687 EndY=-60.6657 EndZ=0
    g1: LineSegment StartX=-170.687 StartY=-60.6657 StartZ=0 EndX=-169.546 EndY=-61.0365 EndZ=0
    g2: LineSegment StartX=-169.546 StartY=-61.0365 StartZ=0 EndX=-168.31 EndY=-57.2323 EndZ=0
    g3: LineSegment StartX=-168.31 StartY=-57.2323 StartZ=0 EndX=-169.451 EndY=-56.8615 EndZ=0
  constraints (11):
    c: Coincident(g1,g0)
    c: Coincident(g2,g1)
    c: Coincident(g3,g2)
    c: Coincident(g3,g0)
    c: Parallel(g0,g2)
    c: Perpendicular(g3,g0)
    c: Perpendicular(g1,g0)
    c: Parallel(g0,g-3)
    c: Distance(g0) = 4
    c: Coincident(g0,g-3)
    c: Distance(g1) = 1.2
FEATURE [Part::Extrusion] Extrude056  label="Extrude scavo saldature rumble"
  Base = -> Sketch053
  Dir = (0,-1,2e-16)
  DirMode = 2
  FaceMakerClass = Part::FaceMakerBullseye
  FaceMakerMode = 3
  LengthFwd = 8.4
  LengthRev = 0
  Solid = true
  Symmetric = true
FEATURE [Sketcher::SketchObject] Sketch054  label="scavo saldature alimentatore connettore USB"
  ArcFitTolerance = 1e-06
  AttachmentSupport = -> [XZ_Plane]
  ExternalGeometry = -> [Sketch037]
  FullyConstrained = true
  MakeInternals = false
  MapMode = 5
  Placement = pos=(0,0,0) rot=(1,0,0;1.5708rad)
  sketch-geometry (4):
    g0: LineSegment StartX=-209.575 StartY=-80.4316 StartZ=0 EndX=-210.375 EndY=-80.4316 EndZ=0
    g1: LineSegment StartX=-210.375 StartY=-80.4316 StartZ=0 EndX=-210.375 EndY=-72.4316 EndZ=0
    g2: LineSegment StartX=-210.375 StartY=-72.4316 StartZ=0 EndX=-209.575 EndY=-72.4316 EndZ=0
    g3: LineSegment StartX=-209.575 StartY=-72.4316 StartZ=0 EndX=-209.575 EndY=-80.4316 EndZ=0
  constraints (11):
    c: Horizontal(g0)
    c: Coincident(g1,g0)
    c: Vertical(g1)
    c: Coincident(g2,g1)
    c: Horizontal(g2)
    c: Coincident(g3,g2)
    c: Coincident(g3,g0)
    c: Vertical(g3)
    c: DistanceX(g0,g0) = 0.8
    c: DistanceY(g3,g3) = 8
    c: Coincident(g0,g-4)
FEATURE [Part::Extrusion] Extrude057  label="Extrude scavo saldature alimentatore connettore USB"
  Base = -> Sketch054
  Dir = (0,-1,2e-16)
  DirMode = 2
  FaceMakerClass = Part::FaceMakerBullseye
  FaceMakerMode = 3
  LengthFwd = 11
  LengthRev = 0
  Solid = true
  Symmetric = true
FEATURE [Sketcher::SketchObject] Sketch055  label="buco interno per micro switch"
  ArcFitTolerance = 1e-06
  AttachmentSupport = -> [XZ_Plane]
  ExternalGeometry = -> [Sketch]
  FullyConstrained = true
  MakeInternals = false
  MapMode = 5
  Placement = pos=(0,0,0) rot=(1,0,0;1.5708rad)
  sketch-geometry (11):
    g0: LineSegment [constr] StartX=-194.483 StartY=34.2854 StartZ=0 EndX=-196.022 EndY=30.0568 EndZ=0
    g1: LineSegment [constr] StartX=-196.022 StartY=30.0568 StartZ=0 EndX=-197.561 EndY=25.8282 EndZ=0
    g2: LineSegment [constr] StartX=-196.022 StartY=30.0568 StartZ=0 EndX=-194.143 EndY=29.3727 EndZ=0
    g3: LineSegment [constr] StartX=-196.022 StartY=30.0568 StartZ=0 EndX=-197.902 EndY=30.7408 EndZ=0
    g4: LineSegment StartX=-196.362 StartY=34.9694 StartZ=0 EndX=-192.604 EndY=33.6014 EndZ=0
    g5: LineSegment StartX=-199.441 StartY=26.5122 StartZ=0 EndX=-195.682 EndY=25.1441 EndZ=0
    g6: LineSegment StartX=-192.604 StartY=33.6014 StartZ=0 EndX=-195.682 EndY=25.1441 EndZ=0
    g7: LineSegment StartX=-196.362 StartY=34.9694 StartZ=0 EndX=-199.441 EndY=26.5122 EndZ=0
    g8: GeomPoint [constr] X=-187.821 Y=29.2 Z=0
    g9: LineSegment [constr] StartX=-188.505 StartY=27.3206 StartZ=0 EndX=-196.022 EndY=30.0568 EndZ=0
    g10: LineSegment [constr] StartX=-187.821 StartY=29.2 StartZ=0 EndX=-188.505 EndY=27.3206 EndZ=0
  constraints (27):
    c: Coincident(g2,g0)
    c: Parallel(g0,g-3)
    c: Tangent(g1,g0) = -1.5708
    c: Perpendicular(g0,g2)
    c: Tangent(g2,g3)
    c: Distance(g0,g1) = 9
    c: Equal(g0,g1)
    c: Distance(g3,g2) = 4
    c: Equal(g2,g3)
    c: Parallel(g3,g4)
    c: Symmetric(g4,g4,g0)
    c: Parallel(g6,g1)
    c: Parallel(g7,g1)
    c: Symmetric(g6,g6,g2)
    c: Symmetric(g5,g5,g1)
    c: Symmetric(g7,g7,g3)
    c: Coincident(g7,g4)
    c: Coincident(g6,g4)
    c: Coincident(g5,g6)
    c: Symmetric(g-3,g-3,g8)
    c: Perpendicular(g-3,g9)
    c: Distance(g9) = 8
    c: Coincident(g3,g9)
    c: Coincident(g10,g8)
    c: Parallel(g10,g-3)
    c: Distance(g10) = 2
    c: Coincident(g10,g9)
FEATURE [Sketcher::SketchObject] Sketch056  label="buco esterno per micro switch"
  ArcFitTolerance = 1e-06
  AttachmentSupport = -> [XZ_Plane]
  ExternalGeometry = -> [Sketch055]
  FullyConstrained = true
  MakeInternals = false
  MapMode = 5
  Placement = pos=(0,0,0) rot=(1,0,0;1.5708rad)
  sketch-geometry (17):
    g0: GeomPoint [constr] X=-194.143 Y=29.3727 Z=0
    g1: GeomPoint [constr] X=-194.483 Y=34.2854 Z=0
    g2: GeomPoint [constr] X=-197.902 Y=30.7408 Z=0
    g3: GeomPoint [constr] X=-197.561 Y=25.8282 Z=0
    g4: GeomPoint [constr] X=-196.022 Y=30.0568 Z=0
    g5: LineSegment [constr] StartX=-194.483 StartY=34.2854 StartZ=0 EndX=-196.022 EndY=30.0568 EndZ=0
    g6: LineSegment [constr] StartX=-196.022 StartY=30.0568 StartZ=0 EndX=-197.561 EndY=25.8282 EndZ=0
    g7: LineSegment [constr] StartX=-197.902 StartY=30.7408 StartZ=0 EndX=-196.022 EndY=30.0568 EndZ=0
    g8: LineSegment [constr] StartX=-196.022 StartY=30.0568 StartZ=0 EndX=-194.143 EndY=29.3727 EndZ=0
    g9: LineSegment [constr] StartX=-195.338 StartY=31.9362 StartZ=0 EndX=-196.022 EndY=30.0568 EndZ=0
    g10: LineSegment [constr] StartX=-196.022 StartY=30.0568 StartZ=0 EndX=-196.706 EndY=28.1774 EndZ=0
    g11: LineSegment [constr] StartX=-196.022 StartY=30.0568 StartZ=0 EndX=-196.821 EndY=30.3475 EndZ=0
    g12: LineSegment [constr] StartX=-196.022 StartY=30.0568 StartZ=0 EndX=-195.223 EndY=29.7661 EndZ=0
    g13: LineSegment StartX=-194.539 StartY=31.6454 StartZ=0 EndX=-195.907 EndY=27.8867 EndZ=0
    g14: LineSegment StartX=-196.137 StartY=32.2269 StartZ=0 EndX=-197.505 EndY=28.4681 EndZ=0
    g15: LineSegment StartX=-196.137 StartY=32.2269 StartZ=0 EndX=-194.539 EndY=31.6454 EndZ=0
    g16: LineSegment StartX=-197.505 StartY=28.4681 StartZ=0 EndX=-195.907 EndY=27.8867 EndZ=0
  constraints (34):
    c: Symmetric(g-5,g-5,g1)
    c: Symmetric(g-5,g-6,g0)
    c: Symmetric(g-6,g-6,g3)
    c: Symmetric(g-5,g-6,g2)
    c: Coincident(g5,g1)
    c: Coincident(g5,g4)
    c: Coincident(g6,g4)
    c: Coincident(g6,g3)
    c: Equal(g5,g6)
    c: Coincident(g7,g2)
    c: Coincident(g7,g4)
    c: Coincident(g8,g4)
    c: Coincident(g8,g0)
    c: Equal(g7,g8)
    c: Coincident(g11,g9)
    c: Coincident(g12,g9)
    c: Tangent(g10,g9) = -1.5708
    c: Perpendicular(g11,g9)
    c: Parallel(g9,g-4)
    c: Equal(g9,g10)
    c: Parallel(g12,g11)
    c: Equal(g11,g12)
    c: Distance(g11,g12) = 1.7
    c: Distance(g9,g10) = 4
    c: Symmetric(g13,g13,g12)
    c: Parallel(g13,g9)
    c: Symmetric(g14,g14,g11)
    c: Symmetric(g15,g15,g9)
    c: Parallel(g15,g11)
    c: Symmetric(g16,g16,g10)
    c: Coincident(g16,g14)
    c: Coincident(g15,g14)
    c: Coincident(g13,g15)
    c: Coincident(g9,g4)
FEATURE [Sketcher::SketchObject] Sketch057  label="buco interno per SWITCH"
  ArcFitTolerance = 1e-06
  AttachmentSupport = -> [XZ_Plane]
  ExternalGeometry = -> [Sketch]
  FullyConstrained = true
  MakeInternals = false
  MapMode = 5
  Placement = pos=(0,0,0) rot=(1,0,0;1.5708rad)
  sketch-geometry (10):
    g0: GeomPoint [constr] X=-187.821 Y=29.2 Z=0
    g1: LineSegment [constr] StartX=-188.505 StartY=27.3206 StartZ=0 EndX=-193.203 EndY=29.0307 EndZ=0
    g2: LineSegment [constr] StartX=-190.809 StartY=35.6086 StartZ=0 EndX=-195.597 EndY=22.4529 EndZ=0
    g3: GeomPoint [constr] X=-193.203 Y=29.0307 Z=0
    g4: LineSegment [constr] StartX=-196.492 StartY=30.2278 StartZ=0 EndX=-189.914 EndY=27.8336 EndZ=0
    g5: LineSegment StartX=-194.098 StartY=36.8056 StartZ=0 EndX=-187.52 EndY=34.4115 EndZ=0
    g6: LineSegment StartX=-194.098 StartY=36.8056 StartZ=0 EndX=-198.886 EndY=23.6499 EndZ=0
    g7: LineSegment StartX=-187.52 StartY=34.4115 StartZ=0 EndX=-192.308 EndY=21.2558 EndZ=0
    g8: LineSegment StartX=-198.886 StartY=23.6499 StartZ=0 EndX=-192.308 EndY=21.2558 EndZ=0
    g9: LineSegment [constr] StartX=-187.821 StartY=29.2 StartZ=0 EndX=-188.505 EndY=27.3206 EndZ=0
  constraints (23):
    c: Symmetric(g-3,g-3,g0)
    c: Perpendicular(g1,g-3)
    c: Parallel(g2,g-3)
    c: Symmetric(g2,g2,g3)
    c: Perpendicular(g2,g4)
    c: Symmetric(g4,g4,g3)
    c: Distance(g2) = 14
    c: Distance(g4) = 7
    c: Distance(g1) = 5
    c: Parallel(g5,g4)
    c: Parallel(g7,g2)
    c: Symmetric(g5,g5,g2)
    c: Symmetric(g6,g6,g4)
    c: Symmetric(g7,g7,g4)
    c: Symmetric(g8,g8,g2)
    c: Coincident(g6,g5)
    c: Coincident(g7,g5)
    c: Coincident(g8,g7)
    c: Coincident(g3,g1)
    c: Coincident(g9,g0)
    c: Parallel(g9,g-3)
    c: Distance(g9) = 2
    c: Coincident(g1,g9)
FEATURE [Sketcher::SketchObject] Sketch058  label="buco esterno per SWITCH"
  ArcFitTolerance = 1e-06
  AttachmentSupport = -> [XZ_Plane]
  ExternalGeometry = -> [Sketch057]
  FullyConstrained = true
  MakeInternals = false
  MapMode = 5
  Placement = pos=(0,0,0) rot=(1,0,0;1.5708rad)
  sketch-geometry (12):
    g0: GeomPoint [constr] X=-190.809 Y=35.6086 Z=0
    g1: GeomPoint [constr] X=-196.492 Y=30.2278 Z=0
    g2: GeomPoint [constr] X=-189.914 Y=27.8336 Z=0
    g3: GeomPoint [constr] X=-195.597 Y=22.4529 Z=0
    g4: GeomPoint [constr] X=-193.203 Y=29.0307 Z=0
    g5: LineSegment [constr] StartX=-192.006 StartY=32.3196 StartZ=0 EndX=-194.4 EndY=25.7418 EndZ=0
    g6: GeomPoint [constr] X=-193.203 Y=29.0307 Z=0
    g7: LineSegment [constr] StartX=-195.082 StartY=29.7148 StartZ=0 EndX=-191.324 EndY=28.3467 EndZ=0
    g8: LineSegment StartX=-193.885 StartY=33.0037 StartZ=0 EndX=-190.127 EndY=31.6356 EndZ=0
    g9: LineSegment StartX=-190.127 StartY=31.6356 StartZ=0 EndX=-192.521 EndY=25.0578 EndZ=0
    g10: LineSegment StartX=-196.28 StartY=26.4258 StartZ=0 EndX=-192.521 EndY=25.0578 EndZ=0
    g11: LineSegment StartX=-193.885 StartY=33.0037 StartZ=0 EndX=-196.28 EndY=26.4258 EndZ=0
  constraints (21):
    c: Symmetric(g-6,g-6,g3)
    c: Symmetric(g-4,g-6,g2)
    c: Symmetric(g-5,g-4,g0)
    c: Symmetric(g-5,g-6,g1)
    c: Symmetric(g1,g2,g4)
    c: Parallel(g5,g-4)
    c: Symmetric(g5,g5,g6)
    c: Perpendicular(g7,g5)
    c: Symmetric(g7,g7,g6)
    c: Distance(g5) = 7
    c: Distance(g7) = 4
    c: Parallel(g8,g7)
    c: Parallel(g11,g5)
    c: Symmetric(g8,g8,g5)
    c: Symmetric(g9,g9,g7)
    c: Symmetric(g10,g10,g5)
    c: Symmetric(g11,g11,g7)
    c: Coincident(g11,g8)
    c: Coincident(g9,g8)
    c: Coincident(g9,g10)
    c: Coincident(g6,g4)
FEATURE [Part::Extrusion] Extrude060  label="Extrude buco interno per SWITCH destro"
  Base = -> Sketch057
  Dir = (0,-1,2e-16)
  DirMode = 2
  FaceMakerClass = Part::FaceMakerBullseye
  FaceMakerMode = 3
  LengthFwd = 13.2
  LengthRev = 0
  Placement = pos=(0,2.6,0) rot=(0,0,1;0rad)
  Solid = true
  Symmetric = false
FEATURE [Part::Extrusion] Extrude061  label="Extrude buco esterno per SWITCH destro"
  Base = -> Sketch058
  Dir = (0,-1,2e-16)
  DirMode = 2
  FaceMakerClass = Part::FaceMakerBullseye
  FaceMakerMode = 3
  LengthFwd = 2
  LengthRev = 0
  Placement = pos=(0,-10.6,0) rot=(0,0,1;0rad)
  Solid = true
  Symmetric = false
FEATURE [Sketcher::SketchObject] Sketch059  label="buco per spazio introduzione SWITCH"
  ArcFitTolerance = 1e-06
  AttachmentSupport = -> [XZ_Plane]
  ExternalGeometry = -> [Sketch057,Sketch010]
  FullyConstrained = true
  MakeInternals = false
  MapMode = 5
  Placement = pos=(0,0,0) rot=(1,0,0;1.5708rad)
  sketch-geometry (8):
    g0: LineSegment [constr] StartX=-201.368 StartY=36.3521 StartZ=0 EndX=-195.094 EndY=34.0687 EndZ=0
    g1: LineSegment [constr] StartX=-194.098 StartY=36.8056 StartZ=0 EndX=-195.094 EndY=34.0687 EndZ=0
    g2: LineSegment StartX=-198.658 StartY=24.2771 StartZ=0 EndX=-199.654 EndY=21.5401 EndZ=0
    g3: LineSegment StartX=-199.654 StartY=21.5401 StartZ=0 EndX=-181.196 EndY=14.822 EndZ=0
    g4: LineSegment StartX=-181.196 StartY=14.822 StartZ=0 EndX=-180.2 EndY=17.559 EndZ=0
    g5: LineSegment StartX=-180.2 StartY=17.559 StartZ=0 EndX=-198.658 EndY=24.2771 EndZ=0
    g6: LineSegment [constr] StartX=-204.932 StartY=26.5605 StartZ=0 EndX=-198.658 EndY=24.2771 EndZ=0
    g7: LineSegment [constr] StartX=-198.658 StartY=24.2771 StartZ=0 EndX=-199.654 EndY=21.5401 EndZ=0
  constraints (20):
    c: Parallel(g1,g-3)
    c: Parallel(g0,g-4)
    c: Coincident(g0,g-4)
    c: Coincident(g1,g-3)
    c: Coincident(g0,g1)
    c: Coincident(g3,g2)
    c: Coincident(g4,g3)
    c: Coincident(g5,g4)
    c: Coincident(g5,g2)
    c: Parallel(g5,g-5)
    c: Parallel(g3,g-5)
    c: Parallel(g4,g-6)
    c: DistanceX(g-6,g4) = 0
    c: Coincident(g6,g-5)
    c: Equal(g6,g0)
    c: Coincident(g7,g6)
    c: Equal(g7,g1)
    c: Tangent(g7,g-3)
    c: Coincident(g2,g6)
    c: Coincident(g2,g7)
FEATURE [Part::Extrusion] Extrude062  label="Extrude buco per spazio introduzione SWITCH"
  Base = -> Sketch059
  Dir = (0,-1,2e-16)
  DirMode = 2
  FaceMakerClass = Part::FaceMakerBullseye
  FaceMakerMode = 3
  LengthFwd = 13.2
  LengthRev = 0
  Solid = true
  Symmetric = true
FEATURE [Part::Extrusion] Extrude063  label="Extrude buco interno per SWITCH sinistro"
  Base = -> Sketch057
  Dir = (0,-1,2e-16)
  DirMode = 2
  FaceMakerClass = Part::FaceMakerBullseye
  FaceMakerMode = 3
  LengthFwd = 13.2
  LengthRev = 0
  Placement = pos=(0,10.6,0) rot=(0,0,1;0rad)
  Solid = true
  Symmetric = false
FEATURE [Part::Extrusion] Extrude064  label="Extrude buco esterno per SWITCH sinistro"
  Base = -> Sketch058
  Dir = (0,-1,2e-16)
  DirMode = 2
  FaceMakerClass = Part::FaceMakerBullseye
  FaceMakerMode = 3
  LengthFwd = 2
  LengthRev = 0
  Placement = pos=(0,12.6,0) rot=(0,0,1;0rad)
  Solid = true
  Symmetric = false
FEATURE [Sketcher::SketchObject] Sketch061  label="struttura esterna blocco switch"
  ArcFitTolerance = 1e-06
  AttachmentSupport = -> [XZ_Plane003]
  FullyConstrained = true
  MakeInternals = false
  MapMode = 5
  Placement = pos=(0,0,0) rot=(1,0,0;1.5708rad)
  sketch-geometry (5):
    g0: LineSegment StartX=-1 StartY=-5.1 StartZ=0 EndX=1 EndY=-5.1 EndZ=0
    g1: LineSegment StartX=1 StartY=-5.1 StartZ=0 EndX=1 EndY=5.1 EndZ=0
    g2: LineSegment StartX=1 StartY=5.1 StartZ=0 EndX=-1 EndY=5.1 EndZ=0
    g3: LineSegment StartX=-1 StartY=5.1 StartZ=0 EndX=-1 EndY=-5.1 EndZ=0
    g4: GeomPoint [constr] X=0 Y=0 Z=0
  constraints (12):
    c: Coincident(g0,g1)
    c: Coincident(g1,g2)
    c: Coincident(g2,g3)
    c: Coincident(g3,g0)
    c: Horizontal(g0)
    c: Horizontal(g2)
    c: Vertical(g1)
    c: Vertical(g3)
    c: Symmetric(g2,g0,g4)
    c: Distance(g1,g3) = 2
    c: Distance(g0,g2) = 10.2
    c: Coincident(g4,g-1)
FEATURE [Sketcher::SketchObject] Sketch062  label="struttura interna blocco switch"
  ArcFitTolerance = 1e-06
  AttachmentSupport = -> [XZ_Plane003]
  ExternalGeometry = -> [Sketch061]
  FullyConstrained = true
  MakeInternals = false
  MapMode = 5
  Placement = pos=(0,0,0) rot=(1,0,0;1.5708rad)
  sketch-geometry (5):
    g0: LineSegment StartX=-1 StartY=3.1 StartZ=0 EndX=-1 EndY=-3.1 EndZ=0
    g1: LineSegment StartX=-1 StartY=-3.1 StartZ=0 EndX=1 EndY=-3.1 EndZ=0
    g2: LineSegment StartX=1 StartY=-3.1 StartZ=0 EndX=1 EndY=3.1 EndZ=0
    g3: LineSegment StartX=1 StartY=3.1 StartZ=0 EndX=-1 EndY=3.1 EndZ=0
    g4: GeomPoint [constr] X=0 Y=0 Z=0
  constraints (12):
    c: Coincident(g0,g1)
    c: Coincident(g1,g2)
    c: Coincident(g2,g3)
    c: Coincident(g3,g0)
    c: Vertical(g0)
    c: Vertical(g2)
    c: Horizontal(g1)
    c: Horizontal(g3)
    c: Symmetric(g2,g0,g4)
    c: Coincident(g4,g-1)
    c: Distance(g0) = 6.2
    c: Equal(g3,g-3)
FEATURE [Sketcher::SketchObject] Sketch063  label="blocchi tra switch"
  ArcFitTolerance = 1e-06
  AttachmentSupport = -> [XZ_Plane003]
  ExternalGeometry = -> [Sketch061,Sketch062]
  FullyConstrained = true
  MakeInternals = false
  MapMode = 5
  Placement = pos=(0,0,0) rot=(1,0,0;1.5708rad)
  sketch-geometry (8):
    g0: LineSegment StartX=-3 StartY=5.1 StartZ=0 EndX=-1 EndY=5.1 EndZ=0
    g1: LineSegment StartX=-1 StartY=5.1 StartZ=0 EndX=-1 EndY=3.1 EndZ=0
    g2: LineSegment StartX=-1 StartY=3.1 StartZ=0 EndX=-3 EndY=3.1 EndZ=0
    g3: LineSegment StartX=-3 StartY=3.1 StartZ=0 EndX=-3 EndY=5.1 EndZ=0
    g4: LineSegment StartX=-3 StartY=-3.1 StartZ=0 EndX=-1 EndY=-3.1 EndZ=0
    g5: LineSegment StartX=-1 StartY=-3.1 StartZ=0 EndX=-1 EndY=-5.1 EndZ=0
    g6: LineSegment StartX=-1 StartY=-5.1 StartZ=0 EndX=-3 EndY=-5.1 EndZ=0
    g7: LineSegment StartX=-3 StartY=-5.1 StartZ=0 EndX=-3 EndY=-3.1 EndZ=0
  constraints (20):
    c: Horizontal(g0)
    c: Coincident(g1,g0)
    c: Coincident(g2,g1)
    c: Horizontal(g2)
    c: Coincident(g3,g2)
    c: Coincident(g3,g0)
    c: Vertical(g3)
    c: Horizontal(g4)
    c: Coincident(g5,g4)
    c: Coincident(g6,g5)
    c: Horizontal(g6)
    c: Coincident(g7,g6)
    c: Coincident(g7,g4)
    c: Vertical(g7)
    c: Coincident(g0,g-4)
    c: Coincident(g1,g-5)
    c: Coincident(g4,g-6)
    c: Coincident(g5,g-7)
    c: Distance(g0) = 2
    c: Distance(g4) = 2
FEATURE [Sketcher::SketchObject] Sketch066  label="piano per rampino"
  ArcFitTolerance = 1e-06
  AttachmentSupport = -> [XZ_Plane002]
  ExternalGeometry = -> [Sketch045]
  FullyConstrained = true
  MakeInternals = false
  MapMode = 5
  Placement = pos=(0,0,0) rot=(1,0,0;1.5708rad)
  sketch-geometry (4):
    g0: LineSegment StartX=5.4 StartY=5.1 StartZ=0 EndX=5.4 EndY=3.9 EndZ=0
    g1: LineSegment StartX=5.4 StartY=3.9 StartZ=0 EndX=7 EndY=3.9 EndZ=0
    g2: LineSegment StartX=7 StartY=3.9 StartZ=0 EndX=7 EndY=5.1 EndZ=0
    g3: LineSegment StartX=7 StartY=5.1 StartZ=0 EndX=5.4 EndY=5.1 EndZ=0
  constraints (11):
    c: Coincident(g0,g1)
    c: Coincident(g1,g2)
    c: Coincident(g2,g3)
    c: Coincident(g3,g0)
    c: Vertical(g0)
    c: Vertical(g2)
    c: Horizontal(g1)
    c: Horizontal(g3)
    c: Distance(g0,g2) = 1.6
    c: Distance(g1,g3) = 1.2
    c: Coincident(g2,g-3)
FEATURE [Sketcher::SketchObject] Sketch064  label="rampini_per_serraggio_struttura"
  ArcFitTolerance = 1e-06
  AttachmentSupport = -> [XZ_Plane002]
  ExternalGeometry = -> [Sketch066,Sketch045]
  FullyConstrained = true
  MakeInternals = false
  MapMode = 5
  Placement = pos=(0,0,0) rot=(1,0,0;1.5708rad)
  sketch-geometry (7):
    g0: LineSegment StartX=7 StartY=5.1 StartZ=0 EndX=7 EndY=3.9 EndZ=0
    g1: LineSegment StartX=7 StartY=3.9 StartZ=0 EndX=9 EndY=3.9 EndZ=0
    g2: LineSegment StartX=7 StartY=5.1 StartZ=0 EndX=7 EndY=5.1 EndZ=0
    g3: LineSegment StartX=7 StartY=5.1 StartZ=0 EndX=7 EndY=7.5 EndZ=0
    g4: LineSegment StartX=9 StartY=5.1 StartZ=0 EndX=9 EndY=3.9 EndZ=0
    g5: LineSegment StartX=7 StartY=7.5 StartZ=0 EndX=9 EndY=7.5 EndZ=0
    g6: LineSegment StartX=9 StartY=7.5 StartZ=0 EndX=9 EndY=5.1 EndZ=0
  constraints (20):
    c: Vertical(g0)
    c: Coincident(g1,g0)
    c: Horizontal(g1)
    c: Coincident(g2,g0)
    c: Horizontal(g2)
    c: Coincident(g3,g2)
    c: Vertical(g3)
    c: Coincident(g5,g3)
    c: Coincident(g4,g6)
    c: Coincident(g4,g1)
    c: Vertical(g4)
    c: Coincident(g0,g-3)
    c: DistanceY(g-4,g3) = 2.4
    c: DistanceX(g1,g1) = 2
    c: DistanceY(g2,g6) = 0
    c: DistanceX(g2,g2) = 0
    c: DistanceY(g0,g0) = 1.2
    c: Coincident(g5,g6)
    c: Horizontal(g5)
    c: Vertical(g6)
FEATURE [Sketcher::SketchObject] Sketch067  label="perno per blocco switch"
  ArcFitTolerance = 1e-06
  AttachmentSupport = -> [XZ_Plane]
  ExternalGeometry = -> [Sketch,Sketch010]
  FullyConstrained = true
  MakeInternals = false
  MapMode = 5
  Placement = pos=(0,0,0) rot=(1,0,0;1.5708rad)
  sketch-geometry (14):
    g0: LineSegment StartX=-191.073 StartY=24.9429 StartZ=0 EndX=-185.81 EndY=23.0276 EndZ=0
    g1: LineSegment StartX=-183.76 StartY=23.9839 StartZ=0 EndX=-182.392 EndY=27.7427 EndZ=0
    g2: LineSegment StartX=-183.348 StartY=29.7934 StartZ=0 EndX=-188.61 EndY=31.7087 EndZ=0
    g3: LineSegment StartX=-188.61 StartY=31.7087 StartZ=0 EndX=-191.073 EndY=24.9429 EndZ=0
    g4: GeomPoint [constr] X=-186.459 Y=27.0946 Z=0
    g5: LineSegment StartX=-189.022 StartY=25.8992 StartZ=0 EndX=-185.263 EndY=24.5311 EndZ=0
    g6: LineSegment StartX=-185.263 StartY=24.5311 StartZ=0 EndX=-183.895 EndY=28.2899 EndZ=0
    g7: LineSegment StartX=-183.895 StartY=28.2899 StartZ=0 EndX=-187.654 EndY=29.658 EndZ=0
    g8: LineSegment StartX=-187.654 StartY=29.658 StartZ=0 EndX=-189.022 EndY=25.8992 EndZ=0
    g9: GeomPoint [constr] X=-186.459 Y=27.0946 Z=0
    g10: ArcOfCircle CenterX=-185.263 CenterY=24.5311 CenterZ=0 NormalX=0 NormalY=0 NormalZ=1 AngleXU=0 Radius=1.6 StartAngle=4.36332 EndAngle=5.93412
    g11: GeomPoint [constr] X=-184.307 Y=22.4804 Z=0
    g12: ArcOfCircle CenterX=-183.895 CenterY=28.2899 CenterZ=0 NormalX=0 NormalY=0 NormalZ=1 AngleXU=0 Radius=1.6 StartAngle=5.93412 EndAngle=7.50492
    g13: GeomPoint [constr] X=-181.844 Y=29.2462 Z=0
  constraints (30):
    c: Coincident(g2,g3)
    c: Coincident(g3,g0)
    c: Symmetric(g13,g0,g4)
    c: Distance(g11,g3) = 7.2
    c: Distance(g0,g2) = 7.2
    c: Parallel(g3,g1)
    c: Parallel(g2,g0)
    c: Perpendicular(g2,g3)
    c: Coincident(g5,g6)
    c: Coincident(g6,g7)
    c: Coincident(g7,g8)
    c: Coincident(g8,g5)
    c: Symmetric(g7,g5,g9)
    c: Distance(g6,g8) = 4
    c: Distance(g5,g7) = 4
    c: Coincident(g9,g4)
    c: Parallel(g8,g6)
    c: Parallel(g7,g5)
    c: Perpendicular(g7,g8)
    c: Tangent(g8,g-3)
    c: Tangent(g2,g-4)
    c: PointOnObject(g11,g1)
    c: PointOnObject(g11,g0)
    c: Tangent(g1,g10) = -1.5708
    c: Tangent(g0,g10) = -1.5708
    c: PointOnObject(g13,g1)
    c: Tangent(g1,g12) = -1.5708
    c: Tangent(g2,g12) = -1.5708
    c: Equal(g10,g12)
    c: Coincident(g10,g5)
FEATURE [Part::Extrusion] Extrude072  label="Extrude perno per blocco switch"
  Base = -> Sketch067
  Dir = (0,-1,2e-16)
  DirMode = 2
  FaceMakerClass = Part::FaceMakerBullseye
  FaceMakerMode = 3
  LengthFwd = 25.2
  LengthRev = 0
  Solid = true
  Symmetric = true
FEATURE [Part::MultiFuse] Fusion
  Refine = true
  Shapes = -> [Extrude,Sweep,Extrude007,Extrude011,Extrude005,Extrude012,Extrude013,Extrude016,Extrude031,Extrude039,Extrude045,Extrude072]
FEATURE [Part::Cut] Cut
  Base = -> Fusion
  Refine = true
  Tool = -> Extrude001
FEATURE [Part::Cut] Cut001
  Base = -> Cut
  Refine = true
  Tool = -> Extrude004
FEATURE [Part::Cut] Cut002
  Base = -> Cut001
  Refine = true
  Tool = -> Extrude006
FEATURE [Part::Cut] Cut003
  Base = -> Cut002
  Refine = true
  Tool = -> Extrude008
FEATURE [Part::Cut] Cut004
  Base = -> Cut003
  Refine = true
  Tool = -> Extrude009
FEATURE [Part::Cut] Cut005
  Base = -> Cut004
  Refine = true
  Tool = -> Extrude010
FEATURE [Part::Cut] Cut006
  Base = -> Cut005
  Refine = true
  Tool = -> Extrude014
FEATURE [Part::Cut] Cut007
  Base = -> Cut006
  Refine = true
  Tool = -> Extrude015
FEATURE [Part::Cut] Cut008
  Base = -> Cut007
  Refine = true
  Tool = -> Extrude018
FEATURE [Part::Cut] Cut009
  Base = -> Cut008
  Refine = true
  Tool = -> Extrude019
FEATURE [Part::Cut] Cut010
  Base = -> Cut009
  Refine = true
  Tool = -> Extrude020
FEATURE [Part::Cut] Cut011
  Base = -> Cut010
  Refine = true
  Tool = -> Extrude021
FEATURE [Part::Cut] Cut012
  Base = -> Cut011
  Refine = true
  Tool = -> Extrude022
FEATURE [Part::Cut] Cut013
  Base = -> Cut012
  Refine = true
  Tool = -> Extrude023
FEATURE [Part::Cut] Cut014
  Base = -> Cut013
  Refine = true
  Tool = -> Extrude032
FEATURE [Part::Cut] Cut015
  Base = -> Cut014
  Refine = true
  Tool = -> Extrude033
FEATURE [Part::Cut] Cut016
  Base = -> Cut015
  Refine = true
  Tool = -> Extrude034
FEATURE [Part::Cut] Cut017
  Base = -> Cut016
  Refine = true
  Tool = -> Extrude035
FEATURE [Part::Cut] Cut018
  Base = -> Cut017
  Refine = true
  Tool = -> Extrude036
FEATURE [Part::Cut] Cut019
  Base = -> Cut018
  Refine = true
  Tool = -> Extrude037
FEATURE [Part::Cut] Cut020
  Base = -> Cut019
  Refine = true
  Tool = -> Extrude030
FEATURE [Part::Cut] Cut022
  Base = -> Cut020
  Refine = true
  Tool = -> Extrude038
FEATURE [Part::Cut] Cut023
  Base = -> Cut022
  Refine = true
  Tool = -> Extrude041
FEATURE [Part::Cut] Cut024
  Base = -> Cut023
  Refine = true
  Tool = -> Extrude040
FEATURE [Part::Cut] Cut025
  Base = -> Cut024
  Refine = true
  Tool = -> Extrude042
FEATURE [Part::Cut] Cut026
  Base = -> Cut025
  Refine = true
  Tool = -> Extrude043
FEATURE [Part::Cut] Cut027
  Base = -> Cut026
  Refine = true
  Tool = -> Extrude044
FEATURE [Part::Cut] Cut028
  Base = -> Cut027
  Refine = true
  Tool = -> Extrude046
FEATURE [Part::Cut] Cut029
  Base = -> Cut028
  Refine = true
  Tool = -> Extrude047
FEATURE [Part::Cut] Cut033
  Base = -> Cut029
  Refine = true
  Tool = -> Extrude055
FEATURE [Part::Cut] Cut034
  Base = -> Cut033
  Refine = true
  Tool = -> Extrude056
FEATURE [Part::Cut] Cut035
  Base = -> Cut034
  Refine = true
  Tool = -> Extrude057
FEATURE [Part::Cut] Cut037
  Base = -> Cut035
  Refine = true
  Tool = -> Extrude060
FEATURE [Part::Cut] Cut038
  Base = -> Cut037
  Refine = true
  Tool = -> Extrude061
FEATURE [Part::Cut] Cut039
  Base = -> Cut038
  Refine = true
  Tool = -> Extrude063
FEATURE [Part::Cut] Cut040
  Base = -> Cut039
  Refine = true
  Tool = -> Extrude064
FEATURE [Part::Cut] Cut041
  Base = -> Cut040
  Refine = true
  Tool = -> Extrude062
FEATURE [Sketcher::SketchObject] Sketch068  label="base con smusso sopra neopixel"
  ArcFitTolerance = 1e-06
  AttachmentSupport = -> [YZ_Plane002]
  FullyConstrained = true
  MakeInternals = false
  MapMode = 5
  Placement = pos=(0,0,0) rot=(0.57735,0.57735,0.57735;2.0944rad)
  sketch-geometry (5):
    g0: LineSegment StartX=-9.5 StartY=-6.1 StartZ=0 EndX=9.5 EndY=-6.1 EndZ=0
    g1: LineSegment StartX=9.5 StartY=-6.1 StartZ=0 EndX=9.5 EndY=6.1 EndZ=0
    g2: LineSegment StartX=9.5 StartY=6.1 StartZ=0 EndX=-9.5 EndY=6.1 EndZ=0
    g3: LineSegment StartX=-9.5 StartY=6.1 StartZ=0 EndX=-9.5 EndY=-6.1 EndZ=0
    g4: GeomPoint [constr] X=0 Y=0 Z=0
  constraints (12):
    c: Coincident(g0,g1)
    c: Coincident(g1,g2)
    c: Coincident(g2,g3)
    c: Coincident(g3,g0)
    c: Horizontal(g0)
    c: Horizontal(g2)
    c: Vertical(g1)
    c: Vertical(g3)
    c: Symmetric(g2,g0,g4)
    c: Distance(g1,g3) = 19
    c: Distance(g0,g2) = 12.2
    c: Coincident(g4,g-1)
FEATURE [Sketcher::SketchObject] Sketch069  label="cilindro minore"
  ArcFitTolerance = 1e-06
  AttachmentSupport = -> [XZ_Plane004]
  FullyConstrained = true
  MakeInternals = false
  MapMode = 5
  Placement = pos=(0,0,0) rot=(1,0,0;1.5708rad)
  sketch-geometry (1):
    g0: Circle CenterX=0 CenterY=0 CenterZ=0 NormalX=0 NormalY=0 NormalZ=1 AngleXU=0 Radius=5.8
  constraints (2):
    c: Diameter(g0) = 11.6
    c: Coincident(g0,g-1)
FEATURE [Sketcher::SketchObject] Sketch070  label="cilindro maggiore"
  ArcFitTolerance = 1e-06
  AttachmentSupport = -> [XZ_Plane004]
  ExternalGeometry = -> [Sketch069]
  FullyConstrained = true
  MakeInternals = false
  MapMode = 5
  Placement = pos=(0,0,0) rot=(1,0,0;1.5708rad)
  sketch-geometry (1):
    g0: Circle CenterX=0 CenterY=0 CenterZ=0 NormalX=0 NormalY=0 NormalZ=1 AngleXU=0 Radius=6.5
  constraints (2):
    c: Coincident(g0,g-1)
    c: Diameter(g0) = 13
FEATURE [Sketcher::SketchObject] Sketch071  label="buco interno"
  ArcFitTolerance = 1e-06
  AttachmentSupport = -> [XZ_Plane004]
  ExternalGeometry = -> [Sketch069]
  FullyConstrained = true
  MakeInternals = false
  MapMode = 5
  Placement = pos=(0,0,0) rot=(1,0,0;1.5708rad)
  sketch-geometry (1):
    g0: Circle CenterX=0 CenterY=0 CenterZ=0 NormalX=0 NormalY=0 NormalZ=1 AngleXU=0 Radius=5
  constraints (2):
    c: Coincident(g0,g-1)
    c: Diameter(g0) = 10
FEATURE [PartDesign::Pad] Pad
  Direction = (0,-1,2e-16)
  Length = 1.2
  Length2 = 10
  Placement = pos=(0,0,0) rot=(1,0,0;1.5708rad)
  Profile = -> Sketch070
  ReferenceAxis = -> Sketch070 [N_Axis]
  Refine = true
  Suppressed = false
  Type = 0
FEATURE [PartDesign::Pad] Pad001
  BaseFeature = -> Pad
  Direction = (0,-1,2e-16)
  Length = 5.6
  Length2 = 10
  Placement = pos=(0,0,0) rot=(1,0,0;1.5708rad)
  Profile = -> Sketch069
  ReferenceAxis = -> Sketch069 [N_Axis]
  Refine = true
  Suppressed = false
  Type = 0
FEATURE [PartDesign::Pocket] Pocket
  BaseFeature = -> Pad001
  Direction = (0,1,-2e-16)
  Length = 7
  Length2 = 5
  Midplane = true
  Placement = pos=(0,0,0) rot=(1,0,0;1.5708rad)
  Profile = -> Sketch071
  ReferenceAxis = -> Sketch071 [N_Axis]
  Refine = true
  Suppressed = false
  Type = 0
FEATURE [PartDesign::Fillet] Fillet
  Base = -> Pocket [Face7]
  BaseFeature = -> Pocket
  Placement = pos=(0,0,0) rot=(1,0,0;1.5708rad)
  Radius = 1
  Refine = true
  SupportTransform = false
  Suppressed = false
  UseAllEdges = false
FEATURE [PartDesign::Body] Body004  label="pulsanti lato sinistro"
  AllowCompound = false
  Group = -> [Sketch069,Sketch070,Sketch071,Pad,Pad001,Pocket,Fillet]
  Origin = -> Origin004
  Tip = -> Fillet
FEATURE [Sketcher::SketchObject] Sketch072  label="buco per saldature e diodo driver solenoide"
  ArcFitTolerance = 1e-06
  AttachmentSupport = -> [XZ_Plane]
  ExternalGeometry = -> [Sketch038]
  FullyConstrained = true
  MakeInternals = false
  MapMode = 5
  Placement = pos=(0,0,0) rot=(1,0,0;1.5708rad)
  sketch-geometry (4):
    g0: LineSegment StartX=-212.269 StartY=-43.9083 StartZ=0 EndX=-207.197 EndY=-33.0326 EndZ=0
    g1: LineSegment StartX=-207.197 StartY=-33.0326 StartZ=0 EndX=-207.56 EndY=-32.8635 EndZ=0
    g2: LineSegment StartX=-207.56 StartY=-32.8635 StartZ=0 EndX=-212.631 EndY=-43.7392 EndZ=0
    g3: LineSegment StartX=-212.631 StartY=-43.7392 StartZ=0 EndX=-212.269 EndY=-43.9083 EndZ=0
  constraints (11):
    c: Coincident(g1,g0)
    c: Coincident(g2,g1)
    c: Coincident(g3,g2)
    c: Coincident(g3,g0)
    c: Parallel(g-3,g0)
    c: Parallel(g0,g2)
    c: Perpendicular(g0,g3)
    c: Perpendicular(g1,g0)
    c: Distance(g3) = 0.4
    c: Distance(g2) = 12
    c: Coincident(g0,g-3)
FEATURE [Part::Extrusion] Extrude074  label="Extrude buco per saldature e diodo driver solenoide"
  Base = -> Sketch072
  Dir = (0,-1,2e-16)
  DirMode = 2
  FaceMakerClass = Part::FaceMakerBullseye
  FaceMakerMode = 3
  LengthFwd = 14.6
  LengthRev = 0
  Solid = true
  Symmetric = true
FEATURE [Part::Cut] Cut042
  Base = -> Cut041
  Refine = true
  Tool = -> Extrude074
FEATURE [Sketcher::SketchObject] Sketch073  label="fori slargati blocco solenoide"
  ArcFitTolerance = 1e-06
  AttachmentSupport = -> [XY_Plane]
  ExternalGeometry = -> [Sketch030]
  FullyConstrained = true
  MakeInternals = false
  MapMode = 5
  sketch-geometry (2):
    g0: Circle CenterX=-152.209 CenterY=6.95 CenterZ=0 NormalX=0 NormalY=0 NormalZ=1 AngleXU=0 Radius=3.7
    g1: Circle CenterX=-130.41 CenterY=-6.95 CenterZ=0 NormalX=0 NormalY=0 NormalZ=1 AngleXU=0 Radius=3.7
  constraints (4):
    c: Diameter(g0) = 7.4
    c: Coincident(g0,g-3)
    c: Diameter(g1) = 7.4
    c: Coincident(g1,g-4)
FEATURE [Part::Extrusion] Extrude075  label="Extrude fori slargati blocco solenoide"
  Base = -> Sketch073
  Dir = (0,0,1)
  DirMode = 2
  FaceMakerClass = Part::FaceMakerBullseye
  FaceMakerMode = 3
  LengthFwd = 1.5
  LengthRev = 0
  Placement = pos=(0,0,36.4) rot=(0,0,1;0rad)
  Solid = true
  Symmetric = false
FEATURE [Part::Cut] Cut043
  Base = -> Cut042
  Refine = true
  Tool = -> Extrude075
FEATURE [Sketcher::SketchObject] Sketch074  label="lato sx pistola"
  ArcFitTolerance = 1e-06
  AttachmentSupport = -> [XZ_Plane]
  ExternalGeometry = -> [Sketch016,Sketch,Sketch058]
  FullyConstrained = true
  MakeInternals = false
  MapMode = 5
  Placement = pos=(0,0,0) rot=(1,0,0;1.5708rad)
  sketch-geometry (37):
    g0: LineSegment StartX=-82.8 StartY=3.2 StartZ=0 EndX=0 EndY=3.2 EndZ=0
    g1: LineSegment StartX=-82.8 StartY=3.2 StartZ=0 EndX=-82.8 EndY=6.2 EndZ=0
    g2: LineSegment [constr] StartX=-107.6 StartY=18 StartZ=0 EndX=-107.6 EndY=20 EndZ=0
    g3: LineSegment [constr] StartX=-132.428 StartY=18 StartZ=0 EndX=-132.428 EndY=20 EndZ=0
    g4: LineSegment StartX=-132.428 StartY=20 StartZ=0 EndX=-107.6 EndY=20 EndZ=0
    g5: ArcOfCircle CenterX=-107.6 CenterY=4 CenterZ=0 NormalX=0 NormalY=0 NormalZ=1 AngleXU=0 Radius=16 StartAngle=0.137937 EndAngle=1.5708
    g6: LineSegment StartX=-82.8 StartY=6.2 StartZ=0 EndX=-91.752 EndY=6.2 EndZ=0
    g7: LineSegment [constr] StartX=-145.743 StartY=8.32624 StartZ=0 EndX=-147.645 EndY=8.94427 EndZ=0
    g8: ArcOfCircle CenterX=-132.428 CenterY=4 CenterZ=0 NormalX=0 NormalY=0 NormalZ=1 AngleXU=0 Radius=16 StartAngle=1.5708 EndAngle=2.82743
    g9: LineSegment StartX=-215.932 StartY=-80.4316 StartZ=0 EndX=-176.685 EndY=-80.4316 EndZ=0
    g10: LineSegment StartX=-147.645 StartY=8.94427 StartZ=0 EndX=-176.685 EndY=-80.4316 EndZ=0
    g11: LineSegment [constr] StartX=-193.988 StartY=-2.33927 StartZ=0 EndX=-192.176 EndY=-3.18451 EndZ=0
    g12: LineSegment [constr] StartX=-217.232 StartY=-52.1862 StartZ=0 EndX=-215.42 EndY=-53.0314 EndZ=0
    g13: LineSegment StartX=-192.176 StartY=-3.18451 StartZ=0 EndX=-215.42 EndY=-53.0314 EndZ=0
    g14: ArcOfCircle CenterX=-184.801 CenterY=-67.3089 CenterZ=0 NormalX=0 NormalY=0 NormalZ=1 AngleXU=0 Radius=33.7833 StartAngle=2.70526 EndAngle=3.54053
    g15: ArcOfCircle CenterX=-207.583 CenterY=4 CenterZ=0 NormalX=0 NormalY=0 NormalZ=1 AngleXU=0 Radius=17 StartAngle=5.84685 EndAngle=7.56663
    g16: LineSegment StartX=-202.765 StartY=20.303 StartZ=0 EndX=-195.887 EndY=39.2 EndZ=0
    g17: LineSegment [constr] StartX=-193.885 StartY=33.0037 StartZ=0 EndX=-197.644 EndY=34.3718 EndZ=0
    g18: LineSegment StartX=-195.887 StartY=39.2 StartZ=0 EndX=0 EndY=39.2 EndZ=0
    g19: LineSegment StartX=0 StartY=3.2 StartZ=0 EndX=0 EndY=39.2 EndZ=0
    g20: LineSegment StartX=-189.939 StartY=31.5672 StartZ=0 EndX=-192.333 EndY=24.9893 EndZ=0
    g21: LineSegment StartX=-196.467 StartY=26.4942 StartZ=0 EndX=-194.073 EndY=33.0721 EndZ=0
    g22: Circle CenterX=-213.443 CenterY=-76.8316 CenterZ=0 NormalX=0 NormalY=0 NormalZ=1 AngleXU=0 Radius=1.8
    g23: Circle CenterX=-179.305 CenterY=-76.8316 CenterZ=0 NormalX=0 NormalY=0 NormalZ=1 AngleXU=0 Radius=1.8
    g24: Circle CenterX=-184.08 CenterY=34.8 CenterZ=0 NormalX=0 NormalY=0 NormalZ=1 AngleXU=0 Radius=1.8
    g25: Circle CenterX=-78.51 CenterY=34.8 CenterZ=0 NormalX=0 NormalY=0 NormalZ=1 AngleXU=0 Radius=1.8
    g26: Circle CenterX=-78.51 CenterY=7.6 CenterZ=0 NormalX=0 NormalY=0 NormalZ=1 AngleXU=0 Radius=1.8
    g27: Circle CenterX=-5.6 CenterY=34.8 CenterZ=0 NormalX=0 NormalY=0 NormalZ=1 AngleXU=0 Radius=1.8
    g28: Circle CenterX=-5.6 CenterY=7.6 CenterZ=0 NormalX=0 NormalY=0 NormalZ=1 AngleXU=0 Radius=1.8
    g29: LineSegment StartX=-190.127 StartY=31.6356 StartZ=0 EndX=-189.939 EndY=31.5672 EndZ=0
    g30: LineSegment StartX=-194.073 StartY=33.0721 StartZ=0 EndX=-193.885 EndY=33.0037 EndZ=0
    g31: LineSegment StartX=-193.885 StartY=33.0037 StartZ=0 EndX=-190.127 EndY=31.6356 EndZ=0
    g32: LineSegment StartX=-196.467 StartY=26.4942 StartZ=0 EndX=-192.333 EndY=24.9893 EndZ=0
    g33: Circle CenterX=-19 CenterY=21.2 CenterZ=0 NormalX=0 NormalY=0 NormalZ=1 AngleXU=0 Radius=6.3
    g34: Circle CenterX=-42 CenterY=21.2 CenterZ=0 NormalX=0 NormalY=0 NormalZ=1 AngleXU=0 Radius=6.3
    g35: Circle CenterX=-65 CenterY=21.2 CenterZ=0 NormalX=0 NormalY=0 NormalZ=1 AngleXU=0 Radius=6.3
    g36: LineSegment [constr] StartX=-4 StartY=21.2 StartZ=0 EndX=-65 EndY=21.2 EndZ=0
  constraints (96):
    c: Coincident(g0,g-41)
    c: Horizontal(g0)
    c: PointOnObject(g0,g-39)
    c: Coincident(g1,g0)
    c: Vertical(g1)
    c: DistanceY(g1,g1) = 3
    c: Coincident(g2,g-17)
    c: Vertical(g2)
    c: Coincident(g3,g-16)
    c: Vertical(g3)
    c: DistanceY(g2,g2) = 2
    c: DistanceY(g3,g3) = 2
    c: Coincident(g4,g3)
    c: Coincident(g4,g2)
    c: Coincident(g5,g-17)
    c: Coincident(g5,g2)
    c: Coincident(g6,g1)
    c: Horizontal(g6)
    c: Coincident(g6,g5)
    c: Coincident(g7,g-15)
    c: Coincident(g8,g7)
    c: Coincident(g8,g3)
    c: Coincident(g8,g-15)
    c: Horizontal(g9)
    c: DistanceY(g-13,g9) = 2
    c: Coincident(g10,g7)
    c: Parallel(g10,g-14)
    c: Coincident(g9,g10)
    c: Distance(g11) = 2
    c: Coincident(g11,g-11)
    c: Perpendicular(g-11,g11)
    c: Distance(g12) = 2
    c: Coincident(g12,g-12)
    c: Perpendicular(g-11,g12)
    c: Coincident(g13,g11)
    c: Coincident(g13,g12)
    c: Coincident(g14,g-32)
    c: Coincident(g14,g12)
    c: Coincident(g14,g9)
    c: Coincident(g15,g-10)
    c: Coincident(g15,g11)
    c: Parallel(g16,g-22)
    c: Distance(g17) = 4
    c: PointOnObject(g17,g16)
    c: Coincident(g15,g16)
    c: Horizontal(g18)
    c: Coincident(g18,g16)
    c: Coincident(g19,g0)
    c: PointOnObject(g19,g-39)
    c: DistanceY(g19,g-36) = 2
    c: Coincident(g18,g19)
    c: Diameter(g22) = 3.6
    c: Coincident(g22,g-9)
    c: Diameter(g23) = 3.6
    c: Coincident(g23,g-8)
    c: Diameter(g24) = 3.6
    c: Diameter(g25) = 3.6
    c: Diameter(g26) = 3.6
    c: Diameter(g27) = 3.6
    c: Diameter(g28) = 3.6
    c: Coincident(g27,g-4)
    c: Coincident(g28,g-3)
    c: Coincident(g25,g-6)
    c: Coincident(g26,g-5)
    c: Coincident(g24,g-7)
    c: Parallel(g20,g-21)
    c: Equal(g20,g-21)
    c: Parallel(g21,g-19)
    c: Equal(g21,g-19)
    c: Distance(g29) = 0.2
    c: Distance(g30) = 0.2
    c: Parallel(g29,g-20)
    c: Parallel(g31,g-20)
    c: Equal(g31,g-20)
    c: Coincident(g30,g31)
    c: Coincident(g31,g29)
    c: Coincident(g29,g-21)
    c: Parallel(g30,g31)
    c: Coincident(g17,g30)
    c: Coincident(g20,g29)
    c: Coincident(g21,g30)
    c: Perpendicular(g16,g17)
    c: Coincident(g32,g21)
    c: Coincident(g32,g20)
    c: Perpendicular(g10,g7)
    c: Diameter(g33) = 12.6
    c: Diameter(g34) = 12.6
    c: Diameter(g35) = 12.6
    c: Horizontal(g36)
    c: PointOnObject(g33,g36)
    c: PointOnObject(g34,g36)
    c: DistanceX(g34,g33) = 23
    c: DistanceX(g35,g34) = 23
    c: DistanceX(g33,g36) = 15
    c: Symmetric(g-24,g-24,g36)
    c: Coincident(g36,g35)
FEATURE [Sketcher::SketchObject] Sketch075  label="lato dx pistola"
  ArcFitTolerance = 1e-06
  AttachmentSupport = -> [XZ_Plane]
  ExternalGeometry = -> [Sketch016,Sketch,Sketch058,Sketch074]
  FullyConstrained = true
  MakeInternals = false
  MapMode = 5
  Placement = pos=(0,0,0) rot=(1,0,0;1.5708rad)
  sketch-geometry (61):
    g0: LineSegment StartX=-82.8 StartY=3.2 StartZ=0 EndX=0 EndY=3.2 EndZ=0
    g1: LineSegment StartX=-82.8 StartY=3.2 StartZ=0 EndX=-82.8 EndY=6.2 EndZ=0
    g2: LineSegment [constr] StartX=-107.6 StartY=18 StartZ=0 EndX=-107.6 EndY=20 EndZ=0
    g3: LineSegment [constr] StartX=-132.428 StartY=18 StartZ=0 EndX=-132.428 EndY=20 EndZ=0
    g4: LineSegment StartX=-132.428 StartY=20 StartZ=0 EndX=-107.6 EndY=20 EndZ=0
    g5: ArcOfCircle CenterX=-107.6 CenterY=4 CenterZ=0 NormalX=0 NormalY=0 NormalZ=1 AngleXU=0 Radius=16 StartAngle=0.137937 EndAngle=1.5708
    g6: LineSegment StartX=-82.8 StartY=6.2 StartZ=0 EndX=-91.752 EndY=6.2 EndZ=0
    g7: LineSegment [constr] StartX=-145.743 StartY=8.32624 StartZ=0 EndX=-147.645 EndY=8.94427 EndZ=0
    g8: ArcOfCircle CenterX=-132.428 CenterY=4 CenterZ=0 NormalX=0 NormalY=0 NormalZ=1 AngleXU=0 Radius=16 StartAngle=1.5708 EndAngle=2.82743
    g9: LineSegment StartX=-215.932 StartY=-80.4316 StartZ=0 EndX=-176.685 EndY=-80.4316 EndZ=0
    g10: LineSegment StartX=-147.645 StartY=8.94427 StartZ=0 EndX=-176.685 EndY=-80.4316 EndZ=0
    g11: LineSegment [constr] StartX=-193.988 StartY=-2.33927 StartZ=0 EndX=-192.176 EndY=-3.18451 EndZ=0
    g12: LineSegment [constr] StartX=-217.232 StartY=-52.1862 StartZ=0 EndX=-215.42 EndY=-53.0314 EndZ=0
    g13: LineSegment StartX=-192.176 StartY=-3.18451 StartZ=0 EndX=-215.42 EndY=-53.0314 EndZ=0
    g14: ArcOfCircle CenterX=-184.801 CenterY=-67.3089 CenterZ=0 NormalX=0 NormalY=0 NormalZ=1 AngleXU=0 Radius=33.7833 StartAngle=2.70526 EndAngle=3.54053
    g15: ArcOfCircle CenterX=-207.583 CenterY=4 CenterZ=0 NormalX=0 NormalY=0 NormalZ=1 AngleXU=0 Radius=17 StartAngle=5.84685 EndAngle=7.56663
    g16: LineSegment StartX=-202.765 StartY=20.303 StartZ=0 EndX=-195.887 EndY=39.2 EndZ=0
    g17: LineSegment [constr] StartX=-193.885 StartY=33.0037 StartZ=0 EndX=-197.644 EndY=34.3718 EndZ=0
    g18: LineSegment StartX=-195.887 StartY=39.2 StartZ=0 EndX=0 EndY=39.2 EndZ=0
    g19: LineSegment StartX=0 StartY=3.2 StartZ=0 EndX=0 EndY=39.2 EndZ=0
    g20: LineSegment StartX=-189.939 StartY=31.5672 StartZ=0 EndX=-192.333 EndY=24.9893 EndZ=0
    g21: LineSegment StartX=-196.467 StartY=26.4942 StartZ=0 EndX=-194.073 EndY=33.0721 EndZ=0
    g22: Circle CenterX=-213.443 CenterY=-76.8316 CenterZ=0 NormalX=0 NormalY=0 NormalZ=1 AngleXU=0 Radius=1.8
    g23: Circle CenterX=-179.305 CenterY=-76.8316 CenterZ=0 NormalX=0 NormalY=0 NormalZ=1 AngleXU=0 Radius=1.8
    g24: Circle CenterX=-184.08 CenterY=34.8 CenterZ=0 NormalX=0 NormalY=0 NormalZ=1 AngleXU=0 Radius=1.8
    g25: Circle CenterX=-78.51 CenterY=34.8 CenterZ=0 NormalX=0 NormalY=0 NormalZ=1 AngleXU=0 Radius=1.8
    g26: Circle CenterX=-78.51 CenterY=7.6 CenterZ=0 NormalX=0 NormalY=0 NormalZ=1 AngleXU=0 Radius=1.8
    g27: Circle CenterX=-5.6 CenterY=34.8 CenterZ=0 NormalX=0 NormalY=0 NormalZ=1 AngleXU=0 Radius=1.8
    g28: Circle CenterX=-5.6 CenterY=7.6 CenterZ=0 NormalX=0 NormalY=0 NormalZ=1 AngleXU=0 Radius=1.8
    g29: LineSegment StartX=-190.127 StartY=31.6356 StartZ=0 EndX=-189.939 EndY=31.5672 EndZ=0
    g30: LineSegment StartX=-194.073 StartY=33.0721 StartZ=0 EndX=-193.885 EndY=33.0037 EndZ=0
    g31: LineSegment StartX=-193.885 StartY=33.0037 StartZ=0 EndX=-190.127 EndY=31.6356 EndZ=0
    g32: LineSegment StartX=-196.467 StartY=26.4942 StartZ=0 EndX=-192.333 EndY=24.9893 EndZ=0
    g33: LineSegment [constr] StartX=-4 StartY=21.2 StartZ=0 EndX=-87.91 EndY=21.2 EndZ=0
    g34: GeomPoint [constr] X=-4 Y=21.2 Z=0
    g35: LineSegment [constr] StartX=-15.2 StartY=33.7 StartZ=0 EndX=-15.2 EndY=8.7 EndZ=0
    g36: LineSegment [constr] StartX=-15.2 StartY=33.7 StartZ=0 EndX=-56.2 EndY=33.7 EndZ=0
    g37: LineSegment [constr] StartX=-15.2 StartY=8.7 StartZ=0 EndX=-56.2 EndY=8.7 EndZ=0
    g38: LineSegment [constr] StartX=-56.2 StartY=33.7 StartZ=0 EndX=-56.2 EndY=8.7 EndZ=0
    g39: Circle CenterX=-18.6 CenterY=30.3 CenterZ=0 NormalX=0 NormalY=0 NormalZ=1 AngleXU=0 Radius=3.4
    g40: Circle CenterX=-18.6 CenterY=12.1 CenterZ=0 NormalX=0 NormalY=0 NormalZ=1 AngleXU=0 Radius=3.4
    g41: Circle CenterX=-43.2 CenterY=30.3 CenterZ=0 NormalX=0 NormalY=0 NormalZ=1 AngleXU=0 Radius=3.4
    g42: Circle CenterX=-43.2 CenterY=12.1 CenterZ=0 NormalX=0 NormalY=0 NormalZ=1 AngleXU=0 Radius=3.4
    g43: LineSegment [constr] StartX=-4 StartY=21.2 StartZ=0 EndX=-15.2 EndY=21.2 EndZ=0
    g44: LineSegment [constr] StartX=-15.2 StartY=21.2 StartZ=0 EndX=-36.2 EndY=21.2 EndZ=0
    g45: LineSegment [constr] StartX=-41.5 StartY=16.2 StartZ=0 EndX=-30.9 EndY=16.2 EndZ=0
    g46: LineSegment [constr] StartX=-30.9 StartY=16.2 StartZ=0 EndX=-30.9 EndY=26.2 EndZ=0
    g47: LineSegment [constr] StartX=-30.9 StartY=26.2 StartZ=0 EndX=-41.5 EndY=26.2 EndZ=0
    g48: LineSegment [constr] StartX=-41.5 StartY=26.2 StartZ=0 EndX=-41.5 EndY=16.2 EndZ=0
    g49: GeomPoint [constr] X=-36.2 Y=21.2 Z=0
    g50: Circle CenterX=-36.2 CenterY=21.2 CenterZ=0 NormalX=0 NormalY=0 NormalZ=1 AngleXU=0 Radius=2.8
    g51: LineSegment [constr] StartX=-24.2 StartY=26.7 StartZ=0 EndX=-24.2 EndY=15.7 EndZ=0
    g52: Circle CenterX=-24.2 CenterY=26.7 CenterZ=0 NormalX=0 NormalY=0 NormalZ=1 AngleXU=0 Radius=3
    g53: Circle CenterX=-24.2 CenterY=15.7 CenterZ=0 NormalX=0 NormalY=0 NormalZ=1 AngleXU=0 Radius=3
    g54: GeomPoint X=-18.6 Y=30.3 Z=0
    g55: GeomPoint X=-18.6 Y=12.1 Z=0
    g56: GeomPoint X=-43.2 Y=12.1 Z=0
    g57: GeomPoint X=-43.2 Y=30.3 Z=0
    g58: Circle CenterX=-65 CenterY=21.2 CenterZ=0 NormalX=0 NormalY=0 NormalZ=1 AngleXU=0 Radius=1.5
    g59: Circle CenterX=-42 CenterY=21.2 CenterZ=0 NormalX=0 NormalY=0 NormalZ=1 AngleXU=0 Radius=1.5
    g60: Circle CenterX=-19 CenterY=21.2 CenterZ=0 NormalX=0 NormalY=0 NormalZ=1 AngleXU=0 Radius=1.5
  constraints (149):
    c: Coincident(g0,g-41)
    c: Horizontal(g0)
    c: PointOnObject(g0,g-39)
    c: Coincident(g1,g0)
    c: Vertical(g1)
    c: DistanceY(g1,g1) = 3
    c: Coincident(g2,g-17)
    c: Vertical(g2)
    c: Coincident(g3,g-16)
    c: Vertical(g3)
    c: DistanceY(g2,g2) = 2
    c: DistanceY(g3,g3) = 2
    c: Coincident(g4,g3)
    c: Coincident(g4,g2)
    c: Coincident(g5,g-17)
    c: Coincident(g5,g2)
    c: Coincident(g6,g1)
    c: Horizontal(g6)
    c: Coincident(g6,g5)
    c: Coincident(g7,g-15)
    c: Coincident(g8,g7)
    c: Coincident(g8,g3)
    c: Coincident(g8,g-15)
    c: Horizontal(g9)
    c: DistanceY(g-13,g9) = 2
    c: Coincident(g10,g7)
    c: Parallel(g10,g-14)
    c: Coincident(g9,g10)
    c: Distance(g11) = 2
    c: Coincident(g11,g-11)
    c: Perpendicular(g-11,g11)
    c: Distance(g12) = 2
    c: Coincident(g12,g-12)
    c: Perpendicular(g-11,g12)
    c: Coincident(g13,g11)
    c: Coincident(g13,g12)
    c: Coincident(g14,g-32)
    c: Coincident(g14,g12)
    c: Coincident(g14,g9)
    c: Coincident(g15,g-10)
    c: Coincident(g15,g11)
    c: Parallel(g16,g-22)
    c: Distance(g17) = 4
    c: PointOnObject(g17,g16)
    c: Coincident(g15,g16)
    c: Horizontal(g18)
    c: Coincident(g18,g16)
    c: Coincident(g19,g0)
    c: PointOnObject(g19,g-39)
    c: DistanceY(g19,g-36) = 2
    c: Coincident(g18,g19)
    c: Diameter(g22) = 3.6
    c: Coincident(g22,g-9)
    c: Diameter(g23) = 3.6
    c: Coincident(g23,g-8)
    c: Diameter(g24) = 3.6
    c: Diameter(g25) = 3.6
    c: Diameter(g26) = 3.6
    c: Diameter(g27) = 3.6
    c: Diameter(g28) = 3.6
    c: Coincident(g27,g-4)
    c: Coincident(g28,g-3)
    c: Coincident(g25,g-6)
    c: Coincident(g26,g-5)
    c: Coincident(g24,g-7)
    c: Parallel(g20,g-21)
    c: Equal(g20,g-21)
    c: Parallel(g21,g-19)
    c: Equal(g21,g-19)
    c: Distance(g29) = 0.2
    c: Distance(g30) = 0.2
    c: Parallel(g29,g-20)
    c: Parallel(g31,g-20)
    c: Equal(g31,g-20)
    c: Coincident(g30,g31)
    c: Coincident(g31,g29)
    c: Coincident(g29,g-21)
    c: Parallel(g30,g31)
    c: Coincident(g17,g30)
    c: Coincident(g20,g29)
    c: Coincident(g21,g30)
    c: Perpendicular(g16,g17)
    c: Coincident(g32,g21)
    c: Coincident(g32,g20)
    c: Perpendicular(g10,g7)
    c: Horizontal(g33)
    c: Symmetric(g-24,g-24,g33)
    c: PointOnObject(g33,g-28)
    c: Symmetric(g-24,g-24,g34)
    c: DistanceY(g35,g35) = 25
    c: Symmetric(g35,g35,g33)
    c: Distance(g36) = 41
    c: Coincident(g36,g35)
    c: Horizontal(g36)
    c: Coincident(g37,g35)
    c: Horizontal(g37)
    c: Coincident(g38,g36)
    c: Vertical(g38)
    c: Coincident(g37,g38)
    c: Diameter(g39) = 6.8
    c: Diameter(g40) = 6.8
    c: Tangent(g39,g36)
    c: Tangent(g40,g37)
    c: Tangent(g39,g35)
    c: Tangent(g40,g35)
    c: Diameter(g41) = 6.8
    c: Diameter(g42) = 6.8
    c: Tangent(g41,g36)
    c: Tangent(g42,g37)
    c: DistanceX(g41,g39) = 24.6
    c: DistanceX(g42,g40) = 24.6
    c: Distance(g43) = 11.2
    c: Coincident(g43,g33)
    c: PointOnObject(g43,g33)
    c: PointOnObject(g43,g35)
    c: Distance(g44) = 21
    c: Coincident(g44,g43)
    c: PointOnObject(g44,g33)
    c: Coincident(g45,g46)
    c: Coincident(g46,g47)
    c: Coincident(g47,g48)
    c: Coincident(g48,g45)
    c: Horizontal(g45)
    c: Horizontal(g47)
    c: Vertical(g46)
    c: Vertical(g48)
    c: Symmetric(g47,g45,g49)
    c: Distance(g46,g48) = 10.6
    c: Distance(g45,g47) = 10
    c: Coincident(g49,g44)
    c: Diameter(g50) = 5.6
    c: Coincident(g50,g44)
    c: Distance(g51) = 11
    c: Symmetric(g51,g51,g33)
    c: DistanceX(g51,g43) = 9
    c: Diameter(g52) = 6
    c: Coincident(g52,g51)
    c: Diameter(g53) = 6
    c: Coincident(g53,g51)
    c: Coincident(g40,g55)
    c: Coincident(g39,g54)
    c: Coincident(g41,g57)
    c: Coincident(g42,g56)
    c: Diameter(g58) = 3
    c: Diameter(g59) = 3
    c: Diameter(g60) = 3
    c: Coincident(g58,g-44)
    c: Coincident(g59,g-46)
    c: Coincident(g60,g-45)
FEATURE [Sketcher::SketchObject] Sketch078
  ArcFitTolerance = 1e-06
  AttachmentSupport = -> [XZ_Plane005]
  FullyConstrained = true
  MakeInternals = false
  MapMode = 5
  Placement = pos=(0,0,0) rot=(1,0,0;1.5708rad)
  sketch-geometry (5):
    g0: LineSegment [constr] StartX=0 StartY=5.5 StartZ=0 EndX=0 EndY=-5.5 EndZ=0
    g1: ArcOfCircle CenterX=0 CenterY=5.5 CenterZ=0 NormalX=0 NormalY=0 NormalZ=1 AngleXU=0 Radius=2.7 StartAngle=0 EndAngle=3.14159
    g2: ArcOfCircle CenterX=0 CenterY=-5.5 CenterZ=0 NormalX=0 NormalY=0 NormalZ=1 AngleXU=0 Radius=2.7 StartAngle=3.1416 EndAngle=6.28318
    g3: LineSegment StartX=-2.7 StartY=5.5 StartZ=0 EndX=-2.7 EndY=-5.50001 EndZ=0
    g4: LineSegment StartX=2.7 StartY=5.5 StartZ=0 EndX=2.7 EndY=-5.50001 EndZ=0
  constraints (13):
    c: Distance(g0) = 11
    c: Vertical(g0)
    c: Symmetric(g0,g0,g-1)
    c: Radius(g1) = 2.7
    c: Coincident(g1,g0)
    c: Radius(g2) = 2.7
    c: Coincident(g2,g0)
    c: Vertical(g3)
    c: Vertical(g4)
    c: Coincident(g2,g4)
    c: Coincident(g2,g3)
    c: Tangent(g3,g1) = -1.5708
    c: Tangent(g4,g1) = 1.5708
FEATURE [PartDesign::Pad] Pad002
  Direction = (0,-1,2e-16)
  Length = 0.8
  Length2 = 10
  Placement = pos=(0,0,0) rot=(1,0,0;1.5708rad)
  Profile = -> Sketch078
  ReferenceAxis = -> Sketch078 [N_Axis]
  Refine = true
  Suppressed = false
  Type = 0
FEATURE [Sketcher::SketchObject] Sketch079
  ArcFitTolerance = 1e-06
  AttachmentSupport = -> [XZ_Plane005]
  ExternalGeometry = -> [Sketch078]
  FullyConstrained = true
  MakeInternals = false
  MapMode = 5
  Placement = pos=(0,0,0) rot=(1,0,0;1.5708rad)
  sketch-geometry (2):
    g0: Circle CenterX=-1e-16 CenterY=5.5 CenterZ=0 NormalX=0 NormalY=0 NormalZ=1 AngleXU=0 Radius=2.7
    g1: Circle CenterX=0 CenterY=-5.5 CenterZ=0 NormalX=0 NormalY=0 NormalZ=1 AngleXU=0 Radius=2.7
  constraints (4):
    c: Coincident(g0,g-3)
    c: PointOnObject(g-3,g0)
    c: Coincident(g1,g-4)
    c: Equal(g1,g-4)
FEATURE [PartDesign::Pad] Pad003
  BaseFeature = -> Pad002
  Direction = (0,-1,2e-16)
  Length = 5
  Length2 = 10
  Placement = pos=(0,0,0) rot=(1,0,0;1.5708rad)
  Profile = -> Sketch079
  ReferenceAxis = -> Sketch079 [N_Axis]
  Refine = true
  Suppressed = false
  Type = 0
FEATURE [PartDesign::Fillet] Fillet001
  Base = -> Pad003 [Edge16,Edge14]
  BaseFeature = -> Pad003
  Placement = pos=(0,0,0) rot=(1,0,0;1.5708rad)
  Radius = 0.4
  Refine = true
  SupportTransform = false
  Suppressed = false
  UseAllEdges = false
FEATURE [PartDesign::Body] Body005  label="pulsanti lato destro"
  AllowCompound = false
  Group = -> [Sketch078,Pad002,Sketch079,Pad003,Fillet001]
  Origin = -> Origin005
  Tip = -> Fillet001
FEATURE [PartDesign::SubShapeBinder] Binder
  BindCopyOnChange = 0
  BindMode = 0
  ClaimChildren = false
  Context = -> Body006 [Binder.]
  Fuse = false
  MakeFace = true
  OffsetFill = false
  OffsetIntersection = false
  OffsetJoinType = 0
  OffsetOpenResult = false
  PartialLoad = false
  Refine = true
  Relative = true
  Support = -> [Body[Sketch074.]]
  _Version = 2
FEATURE [PartDesign::SubShapeBinder] Binder001
  BindCopyOnChange = 0
  BindMode = 0
  ClaimChildren = false
  Context = -> Body007 [Binder001.]
  Fuse = false
  MakeFace = true
  OffsetFill = false
  OffsetIntersection = false
  OffsetJoinType = 0
  OffsetOpenResult = false
  PartialLoad = false
  Refine = true
  Relative = true
  Support = -> [Body[Sketch075.]]
  _Version = 2
FEATURE [Mesh::Feature] logo_per_PCB_definitivo_positivo
  Placement = pos=(-191,17,-66) rot=(0,1,1;0rad)
FEATURE [Sketcher::SketchObject] Sketch114  label="Sketch114 - base lato DX"
  ArcFitTolerance = 1e-06
  AttachmentSupport = -> [Binder001]
  ExternalGeometry = -> [Binder001]
  FullyConstrained = true
  MakeInternals = false
  MapMode = 5
  Placement = pos=(0,1e-15,0) rot=(0,0.707107,0.707107;3.14159rad)
  sketch-geometry (30):
    g0: Circle CenterX=5.6 CenterY=34.8 CenterZ=0 NormalX=0 NormalY=0 NormalZ=1 AngleXU=0 Radius=1.8
    g1: Circle CenterX=5.6 CenterY=7.6 CenterZ=0 NormalX=0 NormalY=0 NormalZ=1 AngleXU=0 Radius=1.8
    g2: Circle CenterX=24.2 CenterY=26.7 CenterZ=0 NormalX=0 NormalY=0 NormalZ=1 AngleXU=0 Radius=3
    g3: Circle CenterX=24.2 CenterY=15.7 CenterZ=0 NormalX=0 NormalY=0 NormalZ=1 AngleXU=0 Radius=3
    g4: Circle CenterX=36.2 CenterY=21.2 CenterZ=0 NormalX=0 NormalY=0 NormalZ=1 AngleXU=0 Radius=2.8
    g5: Circle CenterX=78.51 CenterY=34.8 CenterZ=0 NormalX=0 NormalY=0 NormalZ=1 AngleXU=0 Radius=1.8
    g6: Circle CenterX=78.51 CenterY=7.6 CenterZ=0 NormalX=0 NormalY=0 NormalZ=1 AngleXU=0 Radius=1.8
    g7: Circle CenterX=184.08 CenterY=34.8 CenterZ=0 NormalX=0 NormalY=0 NormalZ=1 AngleXU=0 Radius=1.8
    g8: Circle CenterX=213.443 CenterY=-76.8316 CenterZ=0 NormalX=0 NormalY=0 NormalZ=1 AngleXU=0 Radius=1.8
    g9: Circle CenterX=179.305 CenterY=-76.8316 CenterZ=0 NormalX=0 NormalY=0 NormalZ=1 AngleXU=0 Radius=1.8
    g10: ArcOfCircle [constr] CenterX=132.428 CenterY=4 CenterZ=0 NormalX=0 NormalY=0 NormalZ=1 AngleXU=0 Radius=16 StartAngle=0.314159 EndAngle=1.5708
    g11: ArcOfCircle CenterX=107.6 CenterY=4 CenterZ=0 NormalX=0 NormalY=0 NormalZ=1 AngleXU=0 Radius=16 StartAngle=1.5708 EndAngle=3.00366
    g12: ArcOfCircle CenterX=207.583 CenterY=4 CenterZ=0 NormalX=0 NormalY=0 NormalZ=1 AngleXU=0 Radius=17 StartAngle=1.85815 EndAngle=3.57792
    g13: ArcOfCircle CenterX=184.801 CenterY=-67.3089 CenterZ=0 NormalX=0 NormalY=0 NormalZ=1 AngleXU=0 Radius=33.7833 StartAngle=5.88425 EndAngle=6.71952
    g14: LineSegment StartX=0 StartY=39.2 StartZ=0 EndX=0 EndY=3.2 EndZ=0
    g15: LineSegment StartX=0 StartY=3.2 StartZ=0 EndX=82.8 EndY=3.2 EndZ=0
    g16: LineSegment StartX=82.8 StartY=3.2 StartZ=0 EndX=82.8 EndY=6.2 EndZ=0
    g17: LineSegment StartX=82.8 StartY=6.2 StartZ=0 EndX=91.752 EndY=6.2 EndZ=0
    g18: LineSegment StartX=107.6 StartY=20 StartZ=0 EndX=132.428 EndY=20 EndZ=0
    g19: LineSegment StartX=147.645 StartY=8.94427 StartZ=0 EndX=176.685 EndY=-80.4316 EndZ=0
    g20: LineSegment StartX=176.685 StartY=-80.4316 StartZ=0 EndX=215.932 EndY=-80.4316 EndZ=0
    g21: LineSegment StartX=215.42 StartY=-53.0314 StartZ=0 EndX=192.176 EndY=-3.18451 EndZ=0
    g22: LineSegment StartX=202.765 StartY=20.303 StartZ=0 EndX=195.887 EndY=39.2 EndZ=0
    g23: LineSegment StartX=195.887 StartY=39.2 StartZ=0 EndX=0 EndY=39.2 EndZ=0
    g24: LineSegment StartX=196.467 StartY=26.4942 StartZ=0 EndX=194.073 EndY=33.0721 EndZ=0
    g25: LineSegment StartX=194.073 StartY=33.0721 StartZ=0 EndX=189.939 EndY=31.5672 EndZ=0
    g26: LineSegment StartX=189.939 StartY=31.5672 StartZ=0 EndX=192.333 EndY=24.9893 EndZ=0
    g27: LineSegment StartX=192.333 StartY=24.9893 StartZ=0 EndX=196.467 EndY=26.4942 EndZ=0
    g28: LineSegment StartX=132.428 StartY=20 StartZ=0 EndX=144.053 EndY=20 EndZ=0
    g29: LineSegment StartX=144.053 StartY=20 StartZ=0 EndX=147.645 EndY=8.94427 EndZ=0
  constraints (65):
    c: Equal(g0,g-25)
    c: Equal(g2,g-29)
    c: Equal(g3,g-30)
    c: Equal(g4,g-28)
    c: Equal(g1,g-26)
    c: Coincident(g0,g-25)
    c: Coincident(g1,g-26)
    c: Coincident(g2,g-29)
    c: Coincident(g3,g-30)
    c: Coincident(g4,g-28)
    c: Equal(g5,g-23)
    c: Equal(g6,g-24)
    c: Coincident(g5,g-23)
    c: Coincident(g6,g-24)
    c: Equal(g7,g-20)
    c: Coincident(g7,g-20)
    c: Equal(g9,g-22)
    c: Coincident(g9,g-22)
    c: Equal(g8,g-21)
    c: Coincident(g8,g-21)
    c: Equal(g13,g-12)
    c: Equal(g12,g-14)
    c: Equal(g10,g-9)
    c: Equal(g11,g-7)
    c: Coincident(g14,g-27)
    c: Coincident(g14,g-27)
    c: Coincident(g15,g14)
    c: Coincident(g15,g-5)
    c: Coincident(g16,g15)
    c: Coincident(g16,g-6)
    c: Coincident(g17,g16)
    c: Coincident(g17,g-7)
    c: Coincident(g11,g17)
    c: Coincident(g11,g-8)
    c: Coincident(g18,g11)
    c: Coincident(g18,g-9)
    c: Coincident(g10,g18)
    c: Coincident(g10,g-10)
    c: Coincident(g19,g10)
    c: Coincident(g19,g-11)
    c: Coincident(g20,g19)
    c: Coincident(g20,g-12)
    c: Coincident(g13,g20)
    c: Coincident(g13,g-13)
    c: Coincident(g21,g13)
    c: Coincident(g21,g-14)
    c: Coincident(g12,g21)
    c: Coincident(g12,g-15)
    c: Coincident(g22,g12)
    c: Coincident(g22,g-15)
    c: Coincident(g23,g22)
    c: Coincident(g23,g14)
    c: Coincident(g24,g-18)
    c: Coincident(g24,g-16)
    c: Coincident(g25,g24)
    c: Coincident(g25,g-19)
    c: Coincident(g26,g25)
    c: Coincident(g26,g-19)
    c: Coincident(g27,g26)
    c: Coincident(g27,g24)
    c: Coincident(g29,g10)
    c: Coincident(g28,g10)
    c: Coincident(g29,g28)
    c: Parallel(g28,g18)
    c: Parallel(g29,g19)
FEATURE [PartDesign::Pad] Pad011
  Direction = (0,1,-2e-16)
  Length = 2
  Length2 = 10
  Profile = -> Sketch114
  ReferenceAxis = -> Sketch114 [N_Axis]
  Refine = true
  Reversed = true
  Suppressed = false
  Type = 0
FEATURE [Sketcher::SketchObject] Sketch115
  ArcFitTolerance = 1e-06
  AttachmentSupport = -> [Pad011]
  ExternalGeometry = -> [Binder001]
  FullyConstrained = true
  MakeInternals = false
  MapMode = 5
  Placement = pos=(0,1.7e-15,0) rot=(0,0.707107,0.707107;3.14159rad)
  sketch-geometry (4):
    g0: ArcOfCircle CenterX=24.2 CenterY=26.7 CenterZ=0 NormalX=0 NormalY=0 NormalZ=1 AngleXU=0 Radius=3 StartAngle=4.48384e-08 EndAngle=3.14159
    g1: ArcOfCircle CenterX=24.2 CenterY=15.7 CenterZ=0 NormalX=0 NormalY=0 NormalZ=1 AngleXU=0 Radius=3 StartAngle=3.14159 EndAngle=6.28318
    g2: LineSegment StartX=21.2 StartY=26.7 StartZ=0 EndX=21.2 EndY=15.7 EndZ=0
    g3: LineSegment StartX=27.2 StartY=26.7 StartZ=0 EndX=27.2 EndY=15.7 EndZ=0
  constraints (12):
    c: Equal(g1,g-4)
    c: Equal(g0,g-3)
    c: Coincident(g0,g-3)
    c: Coincident(g1,g-4)
    c: Vertical(g2)
    c: Vertical(g3)
    c: Tangent(g3,g-3)
    c: Tangent(g2,g-3)
    c: Coincident(g0,g2)
    c: Coincident(g0,g3)
    c: Coincident(g1,g2)
    c: Coincident(g3,g1)
FEATURE [Sketcher::SketchObject] Sketch117  label="Sketch117 - fori per inserto M3 x 3 x 4.5"
  ArcFitTolerance = 1e-06
  AttachmentSupport = -> [Pad011]
  ExternalGeometry = -> [Binder001]
  FullyConstrained = true
  MakeInternals = false
  MapMode = 5
  Placement = pos=(0,1.7e-15,0) rot=(0,0.707107,0.707107;3.14159rad)
  sketch-geometry (4):
    g0: Circle CenterX=43.2 CenterY=30.3 CenterZ=0 NormalX=0 NormalY=0 NormalZ=1 AngleXU=0 Radius=2.25
    g1: Circle CenterX=43.2 CenterY=12.1 CenterZ=0 NormalX=0 NormalY=0 NormalZ=1 AngleXU=0 Radius=2.25
    g2: Circle CenterX=18.6 CenterY=30.3 CenterZ=0 NormalX=0 NormalY=0 NormalZ=1 AngleXU=0 Radius=2.25
    g3: Circle CenterX=18.6 CenterY=12.1 CenterZ=0 NormalX=0 NormalY=0 NormalZ=1 AngleXU=0 Radius=2.25
  constraints (8):
    c: Diameter(g0) = 4.5
    c: Diameter(g1) = 4.5
    c: Diameter(g2) = 4.5
    c: Diameter(g3) = 4.5
    c: Coincident(g2,g-3)
    c: Coincident(g3,g-6)
    c: Coincident(g0,g-4)
    c: Coincident(g1,g-5)
FEATURE [Sketcher::SketchObject] Sketch118
  ArcFitTolerance = 1e-06
  AttachmentSupport = -> [Pad011]
  ExternalGeometry = -> [Binder001]
  FullyConstrained = true
  MakeInternals = false
  MapMode = 5
  Placement = pos=(0,-2,0) rot=(1,0,0;1.5708rad)
  sketch-geometry (12):
    g0: Circle CenterX=-78.51 CenterY=34.8 CenterZ=0 NormalX=0 NormalY=0 NormalZ=1 AngleXU=0 Radius=1.8
    g1: Circle CenterX=-78.51 CenterY=7.6 CenterZ=0 NormalX=0 NormalY=0 NormalZ=1 AngleXU=0 Radius=1.8
    g2: Circle CenterX=-5.6 CenterY=34.8 CenterZ=0 NormalX=0 NormalY=0 NormalZ=1 AngleXU=0 Radius=1.8
    g3: Circle CenterX=-5.6 CenterY=7.6 CenterZ=0 NormalX=0 NormalY=0 NormalZ=1 AngleXU=0 Radius=1.8
    g4: LineSegment StartX=0 StartY=39.2 StartZ=0 EndX=0 EndY=3.2 EndZ=0
    g5: LineSegment StartX=0 StartY=3.2 StartZ=0 EndX=-82.8 EndY=3.2 EndZ=0
    g6: LineSegment StartX=-82.8 StartY=3.2 StartZ=0 EndX=-82.8 EndY=39.2 EndZ=0
    g7: LineSegment StartX=-82.8 StartY=39.2 StartZ=0 EndX=0 EndY=39.2 EndZ=0
    g8: ArcOfCircle CenterX=-65 CenterY=21.2 CenterZ=0 NormalX=0 NormalY=0 NormalZ=1 AngleXU=0 Radius=10 StartAngle=1.5708 EndAngle=4.71239
    g9: ArcOfCircle CenterX=-19 CenterY=21.2 CenterZ=0 NormalX=0 NormalY=0 NormalZ=1 AngleXU=0 Radius=10 StartAngle=4.71239 EndAngle=7.85398
    g10: LineSegment StartX=-65 StartY=31.2 StartZ=0 EndX=-19 EndY=31.2 EndZ=0
    g11: LineSegment StartX=-65 StartY=11.2 StartZ=0 EndX=-19 EndY=11.2 EndZ=0
  constraints (25):
    c: Equal(g2,g-5)
    c: Equal(g3,g-7)
    c: Equal(g1,g-6)
    c: Equal(g0,g-4)
    c: Coincident(g0,g-4)
    c: Coincident(g1,g-6)
    c: Coincident(g3,g-7)
    c: Coincident(g2,g-5)
    c: Coincident(g4,g-8)
    c: Coincident(g4,g-9)
    c: Coincident(g5,g4)
    c: Coincident(g5,g-10)
    c: Coincident(g6,g5)
    c: PointOnObject(g6,g-3)
    c: Vertical(g6)
    c: Coincident(g7,g6)
    c: Coincident(g7,g4)
    c: Tangent(g8,g10) = 1.5708
    c: Tangent(g8,g11) = -1.5708
    c: Tangent(g9,g10) = 1.5708
    c: Tangent(g9,g11) = -1.5708
    c: Equal(g8,g9)
    c: Radius(g8) = 10
    c: Coincident(g8,g-11)
    c: Coincident(g9,g-12)
FEATURE [Sketcher::SketchObject] Sketch120
  ArcFitTolerance = 1e-06
  AttachmentSupport = -> [Pad011]
  ExternalGeometry = -> [Binder001]
  FullyConstrained = true
  MakeInternals = false
  MapMode = 5
  Placement = pos=(0,-2,0) rot=(1,0,0;1.5708rad)
  sketch-geometry (4):
    g0: LineSegment StartX=-137.815 StartY=39.2 StartZ=0 EndX=-142.655 EndY=24.303 EndZ=0
    g1: LineSegment StartX=-137.815 StartY=39.2 StartZ=0 EndX=-110.815 EndY=39.2 EndZ=0
    g2: LineSegment StartX=-142.655 StartY=24.303 StartZ=0 EndX=-110.815 EndY=24.303 EndZ=0
    g3: ArcOfCircle CenterX=-92.2534 CenterY=31.7515 CenterZ=0 NormalX=0 NormalY=0 NormalZ=1 AngleXU=0 Radius=20 StartAngle=2.75997 EndAngle=3.52321
  constraints (12):
    c: PointOnObject(g0,g-3)
    c: Coincident(g1,g0)
    c: PointOnObject(g1,g-3)
    c: Coincident(g2,g0)
    c: Horizontal(g2)
    c: Tangent(g0,g-4)
    c: Vertical(g2,g1)
    c: DistanceX(g1,g1) = 27
    c: DistanceY(g-6,g0) = 4
    c: Radius(g3) = 20
    c: Coincident(g3,g1)
    c: Coincident(g3,g2)
FEATURE [Sketcher::SketchObject] Sketch121
  ArcFitTolerance = 1e-06
  AttachmentSupport = -> [Pad011]
  ExternalGeometry = -> [Binder001]
  FullyConstrained = true
  MakeInternals = false
  MapMode = 5
  Placement = pos=(0,-2,0) rot=(1,0,0;1.5708rad)
  sketch-geometry (15):
    g0: LineSegment StartX=-137.815 StartY=39.2 StartZ=0 EndX=-143.955 EndY=20.303 EndZ=0
    g1: LineSegment StartX=-143.955 StartY=20.303 StartZ=0 EndX=-190.141 EndY=20.303 EndZ=0
    g2: LineSegment StartX=-190.141 StartY=20.303 StartZ=0 EndX=-186.139 EndY=31.3 EndZ=0
    g3: LineSegment StartX=-178.754 StartY=39.2 StartZ=0 EndX=-180.791 EndY=33.6029 EndZ=0
    g4: ArcOfCircle CenterX=-184.08 CenterY=34.8 CenterZ=0 NormalX=0 NormalY=0 NormalZ=1 AngleXU=0 Radius=3.5 StartAngle=4.71239 EndAngle=5.93412
    g5: LineSegment StartX=-184.08 StartY=31.3 StartZ=0 EndX=-186.139 EndY=31.3 EndZ=0
    g6: LineSegment StartX=-137.815 StartY=39.2 StartZ=0 EndX=-156.815 EndY=39.2 EndZ=0
    g7: LineSegment StartX=-168.815 StartY=39.2 StartZ=0 EndX=-178.754 EndY=39.2 EndZ=0
    g8: LineSegment StartX=-157.815 StartY=39.2 StartZ=0 EndX=-167.815 EndY=39.2 EndZ=0
    g9: LineSegment StartX=-168.815 StartY=31.2 StartZ=0 EndX=-156.815 EndY=31.2 EndZ=0
    g10: LineSegment StartX=-167.436 StartY=36.2 StartZ=0 EndX=-157.436 EndY=36.2 EndZ=0
    g11: ArcOfCircle CenterX=-176.411 CenterY=35.2 CenterZ=0 NormalX=0 NormalY=0 NormalZ=1 AngleXU=0 Radius=20 StartAngle=6.08183 EndAngle=6.48454
    g12: ArcOfCircle CenterX=-188.411 CenterY=35.2 CenterZ=0 NormalX=0 NormalY=0 NormalZ=1 AngleXU=0 Radius=20 StartAngle=6.08183 EndAngle=6.48454
    g13: ArcOfCircle CenterX=-177.411 CenterY=35.2 CenterZ=0 NormalX=0 NormalY=0 NormalZ=1 AngleXU=0 Radius=20 StartAngle=0.0500209 EndAngle=0.201358
    g14: ArcOfCircle CenterX=-187.411 CenterY=35.2 CenterZ=0 NormalX=0 NormalY=0 NormalZ=1 AngleXU=0 Radius=20 StartAngle=0.0500209 EndAngle=0.201358
  constraints (46):
    c: PointOnObject(g0,g-3)
    c: Tangent(g0,g-5)
    c: Coincident(g1,g0)
    c: Horizontal(g1)
    c: Coincident(g2,g1)
    c: PointOnObject(g3,g-3)
    c: Parallel(g3,g-6)
    c: Parallel(g2,g-6)
    c: Radius(g4) = 3.5
    c: Coincident(g4,g-7)
    c: Tangent(g3,g4) = 1.5708
    c: Horizontal(g5)
    c: Tangent(g5,g4) = 1.5708
    c: DistanceX(g-8,g5) = 3.8
    c: Coincident(g2,g5)
    c: Coincident(g6,g0)
    c: PointOnObject(g6,g-3)
    c: DistanceX(g6,g6) = 19
    c: PointOnObject(g7,g-3)
    c: DistanceX(g7,g6) = 12
    c: Coincident(g7,g3)
    c: PointOnObject(g8,g-3)
    c: PointOnObject(g8,g-3)
    c: DistanceX(g8,g8) = 10
    c: DistanceX(g8,g6) = 1
    c: Horizontal(g9)
    c: Vertical(g7,g9)
    c: Vertical(g6,g9)
    c: DistanceY(g9,g7) = 8
    c: Horizontal(g10)
    c: Equal(g8,g10)
    c: DistanceY(g10,g8) = 3
    c: Radius(g11) = 20
    c: Coincident(g11,g6)
    c: Coincident(g11,g9)
    c: Radius(g12) = 20
    c: Coincident(g12,g7)
    c: Coincident(g12,g9)
    c: Equal(g13,g11)
    c: Coincident(g13,g8)
    c: Coincident(g13,g10)
    c: Horizontal(g13,g11)
    c: Equal(g14,g12)
    c: Coincident(g14,g8)
    c: Coincident(g14,g10)
    c: Horizontal(g1,g-6)
FEATURE [Sketcher::SketchObject] Sketch122
  ArcFitTolerance = 1e-06
  AttachmentSupport = -> [Pad011]
  ExternalGeometry = -> [Binder001]
  FullyConstrained = true
  MakeInternals = false
  MapMode = 5
  Placement = pos=(0,-2,0) rot=(1,0,0;1.5708rad)
  sketch-geometry (8):
    g0: ArcOfCircle CenterX=-184.801 CenterY=-67.3089 CenterZ=0 NormalX=0 NormalY=0 NormalZ=1 AngleXU=0 Radius=33.7833 StartAngle=2.70526 EndAngle=3.54053
    g1: LineSegment StartX=-176.685 StartY=-80.4316 StartZ=0 EndX=-215.932 EndY=-80.4316 EndZ=0
    g2: LineSegment StartX=-215.42 StartY=-53.0314 StartZ=0 EndX=-192.176 EndY=-3.18454 EndZ=0
    g3: ArcOfCircle CenterX=-207.583 CenterY=4 CenterZ=0 NormalX=0 NormalY=0 NormalZ=1 AngleXU=0 Radius=17 StartAngle=5.84685 EndAngle=7.56663
    g4: Circle CenterX=-213.443 CenterY=-76.8316 CenterZ=0 NormalX=0 NormalY=0 NormalZ=1 AngleXU=0 Radius=3
    g5: Circle CenterX=-179.305 CenterY=-76.8316 CenterZ=0 NormalX=0 NormalY=0 NormalZ=1 AngleXU=0 Radius=3
    g6: LineSegment StartX=-143.955 StartY=20.303 StartZ=0 EndX=-176.685 EndY=-80.4316 EndZ=0
    g7: LineSegment StartX=-202.765 StartY=20.303 StartZ=0 EndX=-143.955 EndY=20.303 EndZ=0
  constraints (18):
    c: Coincident(g0,g-7)
    c: Coincident(g0,g-8)
    c: Coincident(g1,g0)
    c: Tangent(g2,g-5)
    c: Coincident(g3,g-6)
    c: Coincident(g2,g3)
    c: Coincident(g0,g2)
    c: Diameter(g4) = 6
    c: Diameter(g5) = 6
    c: Coincident(g4,g-9)
    c: Coincident(g5,g-10)
    c: Horizontal(g1)
    c: Coincident(g6,g1)
    c: Tangent(g6,g-4)
    c: Coincident(g3,g-6)
    c: Coincident(g7,g3)
    c: Horizontal(g7)
    c: Coincident(g7,g6)
FEATURE [Sketcher::SketchObject] Sketch123
  ArcFitTolerance = 1e-06
  AttachmentSupport = -> [Pad011]
  ExternalGeometry = -> [Binder001]
  FullyConstrained = true
  MakeInternals = false
  MapMode = 5
  Placement = pos=(0,-2,0) rot=(1,0,0;1.5708rad)
  sketch-geometry (4):
    g0: LineSegment StartX=-108 StartY=36.8 StartZ=0 EndX=-90 EndY=36.8 EndZ=0
    g1: LineSegment StartX=-108 StartY=36.8 StartZ=0 EndX=-108 EndY=26.8 EndZ=0
    g2: LineSegment StartX=-108 StartY=26.8 StartZ=0 EndX=-90 EndY=26.8 EndZ=0
    g3: ArcOfCircle CenterX=-94 CenterY=31.8 CenterZ=0 NormalX=0 NormalY=0 NormalZ=1 AngleXU=0 Radius=6.40312 StartAngle=5.38713 EndAngle=7.17924
  constraints (13):
    c: Horizontal(g0)
    c: Coincident(g1,g0)
    c: Vertical(g1)
    c: Coincident(g2,g1)
    c: Horizontal(g2)
    c: DistanceX(g0,g0) = 18
    c: DistanceY(g1,g1) = 10
    c: Equal(g0,g2)
    c: DistanceX(g0,g-3) = 90
    c: DistanceY(g0,g-3) = 2.4
    c: Coincident(g3,g0)
    c: Coincident(g3,g2)
    c: DistanceX(g3,g0) = 4
FEATURE [PartDesign::Chamfer] Chamfer014
  Angle = 45
  Base = -> Pad011 [Edge80,Edge4,Edge7]
  BaseFeature = -> Pad011
  ChamferType = 0
  FlipDirection = false
  Refine = true
  Size = 1.9
  Size2 = 1
  SupportTransform = false
  Suppressed = false
  UseAllEdges = false
FEATURE [PartDesign::Pocket] Pocket006
  BaseFeature = -> Chamfer014
  Direction = (0,-1,2e-16)
  Length = 1.2
  Length2 = 5
  Profile = -> Sketch115
  ReferenceAxis = -> Sketch115 [N_Axis]
  Refine = true
  Suppressed = false
  Type = 0
FEATURE [Sketcher::SketchObject] Sketch116  label="Sketch116 - pieno per inserto M3 x 3 x 4,5"
  ArcFitTolerance = 1e-06
  AttachmentSupport = -> [Pocket006]
  ExternalGeometry = -> [Binder001]
  FullyConstrained = true
  MakeInternals = false
  MapMode = 5
  Placement = pos=(0,1.7e-15,0) rot=(0,0.707107,0.707107;3.14159rad)
  sketch-geometry (4):
    g0: Circle CenterX=43.2 CenterY=30.3 CenterZ=0 NormalX=0 NormalY=0 NormalZ=1 AngleXU=0 Radius=3.4
    g1: Circle CenterX=43.2 CenterY=12.1 CenterZ=0 NormalX=0 NormalY=0 NormalZ=1 AngleXU=0 Radius=3.4
    g2: Circle CenterX=18.6 CenterY=30.3 CenterZ=0 NormalX=0 NormalY=0 NormalZ=1 AngleXU=0 Radius=3.4
    g3: Circle CenterX=18.6 CenterY=12.1 CenterZ=0 NormalX=0 NormalY=0 NormalZ=1 AngleXU=0 Radius=3.4
  constraints (8):
    c: Diameter(g0) = 6.8
    c: Diameter(g1) = 6.8
    c: Diameter(g2) = 6.8
    c: Diameter(g3) = 6.8
    c: Coincident(g2,g-3)
    c: Coincident(g0,g-4)
    c: Coincident(g3,g-6)
    c: Coincident(g1,g-5)
FEATURE [PartDesign::Pad] Pad012
  BaseFeature = -> Pocket006
  Direction = (0,1,-2e-16)
  Length = 2.4
  Length2 = 10
  Profile = -> Sketch116
  ReferenceAxis = -> Sketch116 [N_Axis]
  Refine = true
  Suppressed = false
  Type = 0
FEATURE [PartDesign::Pocket] Pocket007
  BaseFeature = -> Pad012
  Direction = (0,-1,2e-16)
  Length = 0.6
  Length2 = 2.4
  Profile = -> Sketch117
  ReferenceAxis = -> Sketch117 [N_Axis]
  Refine = true
  Suppressed = false
  Type = 4
FEATURE [PartDesign::Pad] Pad013
  BaseFeature = -> Pocket007
  Direction = (0,-1,2e-16)
  Length = 1.6
  Length2 = 10
  Profile = -> Sketch118
  ReferenceAxis = -> Sketch118 [N_Axis]
  Refine = true
  Suppressed = false
  Type = 0
FEATURE [Sketcher::SketchObject] Sketch119
  ArcFitTolerance = 1e-06
  AttachmentSupport = -> [Pad013]
  ExternalGeometry = -> [Binder001]
  FullyConstrained = true
  MakeInternals = false
  MapMode = 5
  Placement = pos=(0,-3.6,0) rot=(1,0,0;1.5708rad)
  sketch-geometry (21):
    g0: LineSegment [constr] StartX=-82.8 StartY=3.2 StartZ=0 EndX=-82.8 EndY=39.2 EndZ=0
    g1: ArcOfCircle CenterX=-78.51 CenterY=34.8 CenterZ=0 NormalX=0 NormalY=0 NormalZ=1 AngleXU=0 Radius=3.5 StartAngle=4.71239 EndAngle=6.28319
    g2: ArcOfCircle CenterX=-78.51 CenterY=7.6 CenterZ=0 NormalX=0 NormalY=0 NormalZ=1 AngleXU=0 Radius=3.5 StartAngle=0 EndAngle=1.5708
    g3: ArcOfCircle CenterX=-5.6 CenterY=34.8 CenterZ=0 NormalX=0 NormalY=0 NormalZ=1 AngleXU=0 Radius=3.5 StartAngle=3.14159 EndAngle=4.71239
    g4: ArcOfCircle CenterX=-5.6 CenterY=7.6 CenterZ=0 NormalX=0 NormalY=0 NormalZ=1 AngleXU=0 Radius=3.5 StartAngle=1.5708 EndAngle=3.14159
    g5: LineSegment StartX=0 StartY=39.2 StartZ=0 EndX=0 EndY=31.3 EndZ=0
    g6: LineSegment StartX=0 StartY=39.2 StartZ=0 EndX=-9.1 EndY=39.2 EndZ=0
    g7: LineSegment StartX=0 StartY=3.2 StartZ=0 EndX=0 EndY=11.1 EndZ=0
    g8: LineSegment StartX=0 StartY=3.2 StartZ=0 EndX=-9.1 EndY=3.2 EndZ=0
    g9: LineSegment StartX=-82.8 StartY=3.2 StartZ=0 EndX=-75.01 EndY=3.2 EndZ=0
    g10: LineSegment StartX=-82.8 StartY=3.2 StartZ=0 EndX=-82.8 EndY=11.1 EndZ=0
    g11: LineSegment StartX=-82.8 StartY=39.2 StartZ=0 EndX=-82.8 EndY=31.3 EndZ=0
    g12: LineSegment StartX=-82.8 StartY=39.2 StartZ=0 EndX=-75.01 EndY=39.2 EndZ=0
    g13: LineSegment StartX=-82.8 StartY=31.3 StartZ=0 EndX=-78.51 EndY=31.3 EndZ=0
    g14: LineSegment StartX=-75.01 StartY=39.2 StartZ=0 EndX=-75.01 EndY=34.8 EndZ=0
    g15: LineSegment StartX=-82.8 StartY=11.1 StartZ=0 EndX=-78.51 EndY=11.1 EndZ=0
    g16: LineSegment StartX=-75.01 StartY=3.2 StartZ=0 EndX=-75.01 EndY=7.6 EndZ=0
    g17: LineSegment StartX=-9.1 StartY=39.2 StartZ=0 EndX=-9.1 EndY=34.8 EndZ=0
    g18: LineSegment StartX=0 StartY=31.3 StartZ=0 EndX=-5.6 EndY=31.3 EndZ=0
    g19: LineSegment StartX=0 StartY=11.1 StartZ=0 EndX=-5.6 EndY=11.1 EndZ=0
    g20: LineSegment StartX=-9.1 StartY=3.2 StartZ=0 EndX=-9.1 EndY=7.6 EndZ=0
  constraints (51):
    c: Coincident(g0,g-10)
    c: PointOnObject(g0,g-8)
    c: Vertical(g0)
    c: Coincident(g1,g-3)
    c: Coincident(g2,g-4)
    c: Coincident(g3,g-5)
    c: Coincident(g4,g-6)
    c: Radius(g4) = 3.5
    c: Radius(g3) = 3.5
    c: Radius(g1) = 3.5
    c: Radius(g2) = 3.5
    c: Coincident(g5,g-9)
    c: PointOnObject(g5,g-9)
    c: Coincident(g6,g5)
    c: PointOnObject(g6,g-8)
    c: Coincident(g7,g-9)
    c: PointOnObject(g7,g-9)
    c: Coincident(g8,g7)
    c: PointOnObject(g8,g-7)
    c: Coincident(g9,g0)
    c: PointOnObject(g9,g-7)
    c: Coincident(g10,g0)
    c: PointOnObject(g10,g0)
    c: Coincident(g11,g0)
    c: PointOnObject(g11,g0)
    c: Coincident(g12,g0)
    c: PointOnObject(g12,g-8)
    c: Coincident(g13,g11)
    c: Horizontal(g13)
    c: Coincident(g14,g12)
    c: Vertical(g14)
    c: Coincident(g15,g10)
    c: Horizontal(g15)
    c: Coincident(g16,g9)
    c: Vertical(g16)
    c: Coincident(g17,g6)
    c: Vertical(g17)
    c: Coincident(g18,g5)
    c: Horizontal(g18)
    c: Coincident(g19,g7)
    c: Horizontal(g19)
    c: Coincident(g20,g8)
    c: Vertical(g20)
    c: Tangent(g20,g4) = 1.5708
    c: Tangent(g4,g19) = -1.5708
    c: Tangent(g18,g3) = 1.5708
    c: Tangent(g3,g17) = -1.5708
    c: Tangent(g13,g1) = -1.5708
    c: Tangent(g1,g14) = 1.5708
    c: Tangent(g16,g2) = -1.5708
    c: Tangent(g2,g15) = 1.5708
FEATURE [PartDesign::Pocket] Pocket008
  BaseFeature = -> Pad013
  Direction = (0,1,-2e-16)
  Length = 1.6
  Length2 = 5
  Profile = -> Sketch119
  ReferenceAxis = -> Sketch119 [N_Axis]
  Refine = true
  Suppressed = false
  Type = 0
FEATURE [PartDesign::Pad] Pad017
  BaseFeature = -> Pocket008
  Direction = (0,-1,2e-16)
  Length = 1.6
  Length2 = 10
  Profile = -> Sketch123
  ReferenceAxis = -> Sketch123 [N_Axis]
  Refine = true
  Suppressed = false
  Type = 0
FEATURE [Sketcher::SketchObject] Sketch125
  ArcFitTolerance = 1e-06
  AttachmentSupport = -> [Pad017]
  ExternalGeometry = -> [Pad017]
  FullyConstrained = true
  MakeInternals = false
  MapMode = 5
  Placement = pos=(0,-3.6,8e-16) rot=(1,0,0;1.5708rad)
  sketch-geometry (20):
    g0: LineSegment StartX=-108 StartY=35.8 StartZ=0 EndX=-108 EndY=35 EndZ=0
    g1: LineSegment StartX=-108 StartY=35 StartZ=0 EndX=-97 EndY=35 EndZ=0
    g2: LineSegment StartX=-97 StartY=35 StartZ=0 EndX=-97 EndY=35.8 EndZ=0
    g3: LineSegment StartX=-97 StartY=35.8 StartZ=0 EndX=-108 EndY=35.8 EndZ=0
    g4: LineSegment StartX=-108 StartY=28.6 StartZ=0 EndX=-108 EndY=27.8 EndZ=0
    g5: LineSegment StartX=-108 StartY=27.8 StartZ=0 EndX=-97 EndY=27.8 EndZ=0
    g6: LineSegment StartX=-97 StartY=27.8 StartZ=0 EndX=-97 EndY=28.6 EndZ=0
    g7: LineSegment StartX=-97 StartY=28.6 StartZ=0 EndX=-108 EndY=28.6 EndZ=0
    g8: LineSegment StartX=-108 StartY=30.4 StartZ=0 EndX=-108 EndY=29.6 EndZ=0
    g9: LineSegment StartX=-108 StartY=29.6 StartZ=0 EndX=-97 EndY=29.6 EndZ=0
    g10: LineSegment StartX=-97 StartY=29.6 StartZ=0 EndX=-97 EndY=30.4 EndZ=0
    g11: LineSegment StartX=-97 StartY=30.4 StartZ=0 EndX=-108 EndY=30.4 EndZ=0
    g12: LineSegment StartX=-108 StartY=32.2 StartZ=0 EndX=-108 EndY=31.4 EndZ=0
    g13: LineSegment StartX=-108 StartY=31.4 StartZ=0 EndX=-97 EndY=31.4 EndZ=0
    g14: LineSegment StartX=-97 StartY=31.4 StartZ=0 EndX=-97 EndY=32.2 EndZ=0
    g15: LineSegment StartX=-97 StartY=32.2 StartZ=0 EndX=-108 EndY=32.2 EndZ=0
    g16: LineSegment StartX=-108 StartY=34 StartZ=0 EndX=-108 EndY=33.2 EndZ=0
    g17: LineSegment StartX=-108 StartY=33.2 StartZ=0 EndX=-97 EndY=33.2 EndZ=0
    g18: LineSegment StartX=-97 StartY=33.2 StartZ=0 EndX=-97 EndY=34 EndZ=0
    g19: LineSegment StartX=-97 StartY=34 StartZ=0 EndX=-108 EndY=34 EndZ=0
  constraints (55):
    c: Coincident(g1,g0)
    c: Horizontal(g1)
    c: Coincident(g2,g1)
    c: Vertical(g2)
    c: Coincident(g3,g2)
    c: Horizontal(g3)
    c: Coincident(g3,g0)
    c: DistanceX(g1,g1) = 11
    c: DistanceY(g2,g2) = 0.8
    c: Coincident(g5,g4)
    c: Horizontal(g5)
    c: Coincident(g6,g5)
    c: Vertical(g6)
    c: Coincident(g7,g6)
    c: Horizontal(g7)
    c: Coincident(g7,g4)
    c: Coincident(g9,g8)
    c: Horizontal(g9)
    c: Coincident(g10,g9)
    c: Vertical(g10)
    c: Coincident(g11,g10)
    c: Horizontal(g11)
    c: Coincident(g11,g8)
    c: Coincident(g13,g12)
    c: Horizontal(g13)
    c: Coincident(g14,g13)
    c: Vertical(g14)
    c: Coincident(g15,g14)
    c: Horizontal(g15)
    c: Coincident(g15,g12)
    c: Coincident(g17,g16)
    c: Horizontal(g17)
    c: Coincident(g18,g17)
    c: Vertical(g18)
    c: Coincident(g19,g18)
    c: Horizontal(g19)
    c: Coincident(g19,g16)
    c: Equal(g3,g19)
    c: Equal(g3,g15)
    c: Equal(g3,g11)
    c: Equal(g3,g7)
    c: Equal(g2,g18)
    c: Equal(g2,g14)
    c: Equal(g2,g10)
    c: Equal(g2,g6)
    c: DistanceY(g-4,g4) = 1
    c: DistanceY(g4,g8) = 1
    c: DistanceY(g8,g12) = 1
    c: DistanceY(g12,g16) = 1
    c: DistanceY(g16,g0) = 1
    c: Tangent(g0,g-5)
    c: Tangent(g16,g-5)
    c: Tangent(g12,g-5)
    c: Tangent(g8,g-5)
    c: Tangent(g4,g-5)
FEATURE [PartDesign::Chamfer] Chamfer009
  Angle = 45
  Base = -> Pad017 [Edge151,Edge154]
  BaseFeature = -> Pad017
  ChamferType = 1
  FlipDirection = false
  Refine = true
  Size = 1.5
  Size2 = 2.8
  SupportTransform = false
  Suppressed = false
  UseAllEdges = false
FEATURE [PartDesign::Pocket] Pocket009
  BaseFeature = -> Chamfer009
  Direction = (0,1,-2e-16)
  Length = 1
  Length2 = 5
  Profile = -> Sketch125
  ReferenceAxis = -> Sketch125 [N_Axis]
  Refine = true
  Suppressed = false
  Type = 0
FEATURE [PartDesign::Pad] Pad014
  BaseFeature = -> Pocket009
  Direction = (0,-1,2e-16)
  Length = 0.8
  Length2 = 10
  Profile = -> Sketch120
  ReferenceAxis = -> Sketch120 [N_Axis]
  Refine = true
  Suppressed = false
  Type = 0
FEATURE [Sketcher::SketchObject] Sketch124
  ArcFitTolerance = 1e-06
  AttachmentSupport = -> [Pad014]
  ExternalGeometry = -> [Binder001]
  FullyConstrained = true
  MakeInternals = false
  MapMode = 5
  Placement = pos=(0,-2.8,6e-16) rot=(1,0,0;1.5708rad)
  sketch-geometry (4):
    g0: LineSegment StartX=-129 StartY=39.2 StartZ=0 EndX=-131.599 EndY=31.2 EndZ=0
    g1: LineSegment StartX=-118 StartY=39.2 StartZ=0 EndX=-120.599 EndY=31.2 EndZ=0
    g2: LineSegment StartX=-129 StartY=39.2 StartZ=0 EndX=-118 EndY=39.2 EndZ=0
    g3: LineSegment StartX=-120.599 StartY=31.2 StartZ=0 EndX=-131.599 EndY=31.2 EndZ=0
  constraints (12):
    c: PointOnObject(g0,g-3)
    c: PointOnObject(g1,g-3)
    c: Parallel(g-4,g0)
    c: Parallel(g-4,g1)
    c: Coincident(g2,g0)
    c: Coincident(g2,g1)
    c: DistanceX(g2,g2) = 11
    c: DistanceY(g1,g1) = 8
    c: Coincident(g3,g1)
    c: Horizontal(g3)
    c: Coincident(g3,g0)
    c: DistanceX(g1,g-3) = 118
FEATURE [PartDesign::Pad] Pad018
  BaseFeature = -> Pad014
  Direction = (0,-1,2e-16)
  Length = 1.2
  Length2 = 10
  Profile = -> Sketch124
  ReferenceAxis = -> Sketch124 [N_Axis]
  Refine = true
  Suppressed = false
  Type = 0
FEATURE [Sketcher::SketchObject] Sketch126
  ArcFitTolerance = 1e-06
  AttachmentSupport = -> [Pad018]
  ExternalGeometry = -> [Pad018]
  FullyConstrained = true
  MakeInternals = false
  MapMode = 5
  Placement = pos=(0,-4,0) rot=(1,0,0;1.5708rad)
  sketch-geometry (8):
    g0: LineSegment StartX=-129.877 StartY=36.5 StartZ=0 EndX=-130.137 EndY=35.7 EndZ=0
    g1: LineSegment StartX=-130.69 StartY=34 StartZ=0 EndX=-130.95 EndY=33.2 EndZ=0
    g2: LineSegment StartX=-129.877 StartY=36.5 StartZ=0 EndX=-118.877 EndY=36.5 EndZ=0
    g3: LineSegment StartX=-130.137 StartY=35.7 StartZ=0 EndX=-119.137 EndY=35.7 EndZ=0
    g4: LineSegment StartX=-130.69 StartY=34 StartZ=0 EndX=-119.69 EndY=34 EndZ=0
    g5: LineSegment StartX=-130.95 StartY=33.2 StartZ=0 EndX=-119.95 EndY=33.2 EndZ=0
    g6: LineSegment StartX=-118.877 StartY=36.5 StartZ=0 EndX=-119.137 EndY=35.7 EndZ=0
    g7: LineSegment StartX=-119.69 StartY=34 StartZ=0 EndX=-119.95 EndY=33.2 EndZ=0
  constraints (20):
    c: Coincident(g2,g0)
    c: Horizontal(g2)
    c: Coincident(g3,g0)
    c: Horizontal(g3)
    c: Coincident(g4,g1)
    c: Horizontal(g4)
    c: Coincident(g5,g1)
    c: Horizontal(g5)
    c: Coincident(g6,g2)
    c: Coincident(g6,g3)
    c: Coincident(g7,g4)
    c: Coincident(g7,g5)
    c: Tangent(g0,g-4)
    c: Tangent(g6,g-5)
    c: Tangent(g1,g-4)
    c: Tangent(g7,g-5)
    c: DistanceY(g3,g2) = 0.8
    c: DistanceY(g5,g4) = 0.8
    c: DistanceY(g-6,g1) = 2
    c: DistanceY(g-6,g0) = 4.5
FEATURE [PartDesign::Chamfer] Chamfer008
  Angle = 45
  Base = -> Pad018 [Edge257]
  BaseFeature = -> Pad018
  ChamferType = 1
  FlipDirection = false
  Refine = true
  Size = 1
  Size2 = 6
  SupportTransform = false
  Suppressed = false
  UseAllEdges = false
FEATURE [PartDesign::Pocket] Pocket010
  BaseFeature = -> Chamfer008
  Direction = (0,1,-2e-16)
  Length = 1
  Length2 = 5
  Profile = -> Sketch126
  ReferenceAxis = -> Sketch126 [N_Axis]
  Refine = true
  Suppressed = false
  Type = 0
FEATURE [PartDesign::Pad] Pad015
  BaseFeature = -> Pocket010
  Direction = (0,-1,2e-16)
  Length = 2
  Length2 = 10
  Profile = -> Sketch121
  ReferenceAxis = -> Sketch121 [N_Axis]
  Refine = true
  Suppressed = false
  Type = 0
FEATURE [PartDesign::Pad] Pad016
  BaseFeature = -> Pad015
  Direction = (0,-1,2e-16)
  Length = 1.6
  Length2 = 10
  Profile = -> Sketch122
  ReferenceAxis = -> Sketch122 [N_Axis]
  Refine = true
  Suppressed = false
  Type = 0
FEATURE [Sketcher::SketchObject] Sketch129
  ArcFitTolerance = 1e-06
  AttachmentSupport = -> [Pad016]
  ExternalGeometry = -> [Binder001]
  FullyConstrained = true
  MakeInternals = false
  MapMode = 5
  Placement = pos=(0,-3.6,0) rot=(1,0,0;1.5708rad)
  sketch-geometry (12):
    g0: LineSegment [constr] StartX=-192.176 StartY=-3.18451 StartZ=0 EndX=-181.223 EndY=20.303 EndZ=0
    g1: LineSegment [constr] StartX=-202.765 StartY=20.303 StartZ=0 EndX=-181.223 EndY=20.303 EndZ=0
    g2: LineSegment StartX=-202.765 StartY=20.303 StartZ=0 EndX=-181.223 EndY=20.303 EndZ=0
    g3: LineSegment StartX=-192.176 StartY=-3.18451 StartZ=0 EndX=-196.804 EndY=-13.1107 EndZ=0
    g4: ArcOfCircle CenterX=-207.583 CenterY=4 CenterZ=0 NormalX=0 NormalY=0 NormalZ=1 AngleXU=0 Radius=17 StartAngle=5.84685 EndAngle=7.56663
    g5: ArcOfEllipse CenterX=-181.223 CenterY=8.55923 CenterZ=0 NormalX=0 NormalY=0 NormalZ=1 MajorRadius=23.4779 MinorRadius=11.7437 AngleXU=2e-16 StartAngle=4.71239 EndAngle=7.85398
    g6: LineSegment [constr] StartX=-157.745 StartY=8.55923 StartZ=0 EndX=-204.701 EndY=8.55923 EndZ=0
    g7: LineSegment [constr] StartX=-181.223 StartY=20.303 StartZ=0 EndX=-181.223 EndY=-3.18451 EndZ=0
    g8: GeomPoint [constr] X=-160.894 Y=8.55923 Z=0
    g9: GeomPoint [constr] X=-201.553 Y=8.55923 Z=0
    g10: ArcOfCircle CenterX=-181.223 CenterY=-20.3763 CenterZ=0 NormalX=0 NormalY=0 NormalZ=1 AngleXU=0 Radius=17.1918 StartAngle=1.57079 EndAngle=2.70526
    g11: GeomPoint [constr] X=-181.223 Y=-3.18451 Z=0
  constraints (23):
    c: Coincident(g0,g-5)
    c: Coincident(g1,g-6)
    c: Horizontal(g1)
    c: Coincident(g1,g0)
    c: Parallel(g0,g-4)
    c: Coincident(g2,g1)
    c: Coincident(g2,g0)
    c: Coincident(g3,g0)
    c: Equal(g4,g-5)
    c: Coincident(g4,g1)
    c: Coincident(g4,g0)
    c: InternalAlignment(g6-g9 -> g5) x4
    c: Vertical(g5,g0)
    c: Horizontal(g6)
    c: Coincident(g5,g0)
    c: DistanceX(g6,g-3) = 10.1
    c: Tangent(g10,g3) = -1.5708
    c: PointOnObject(g11,g10)
    c: Tangent(g5,g10,g11) = 1.5708
    c: Coincident(g10,g5)
    c: Coincident(g11,g7)
    c: Parallel(g3,g-4)
    c: Horizontal(g5,g0)
FEATURE [Sketcher::SketchObject] Sketch130
  ArcFitTolerance = 1e-06
  AttachmentOffset = pos=(0,0,-1.6) rot=(0,0,1;0rad)
  AttachmentSupport = -> [Pad016]
  ExternalGeometry = -> [Binder001]
  FullyConstrained = true
  MakeInternals = false
  MapMode = 5
  Placement = pos=(0,-2,-4e-16) rot=(1,0,0;1.5708rad)
  sketch-geometry (12):
    g0: LineSegment [constr] StartX=-192.176 StartY=-3.18451 StartZ=0 EndX=-181.223 EndY=20.303 EndZ=0
    g1: LineSegment [constr] StartX=-202.765 StartY=20.303 StartZ=0 EndX=-181.223 EndY=20.303 EndZ=0
    g2: LineSegment StartX=-202.765 StartY=20.303 StartZ=0 EndX=-181.223 EndY=20.303 EndZ=0
    g3: LineSegment StartX=-192.176 StartY=-3.18451 StartZ=0 EndX=-193.827 EndY=-6.72678 EndZ=0
    g4: ArcOfCircle CenterX=-207.583 CenterY=4 CenterZ=0 NormalX=0 NormalY=0 NormalZ=1 AngleXU=0 Radius=17 StartAngle=5.84685 EndAngle=7.56663
    g5: ArcOfEllipse CenterX=-181.223 CenterY=10.803 CenterZ=0 NormalX=0 NormalY=0 NormalZ=1 MajorRadius=14.4779 MinorRadius=9.5 AngleXU=0 StartAngle=4.71239 EndAngle=7.85398
    g6: LineSegment [constr] StartX=-166.745 StartY=10.803 StartZ=0 EndX=-195.701 EndY=10.803 EndZ=0
    g7: LineSegment [constr] StartX=-181.223 StartY=20.303 StartZ=0 EndX=-181.223 EndY=1.30297 EndZ=0
    g8: GeomPoint [constr] X=-170.298 Y=10.803 Z=0
    g9: GeomPoint [constr] X=-192.148 Y=10.803 Z=0
    g10: ArcOfCircle CenterX=-181.223 CenterY=-12.6042 CenterZ=0 NormalX=0 NormalY=0 NormalZ=1 AngleXU=0 Radius=13.9072 StartAngle=1.5708 EndAngle=2.70526
    g11: GeomPoint [constr] X=-181.223 Y=1.30297 Z=0
  constraints (23):
    c: Coincident(g0,g-5)
    c: Coincident(g1,g-6)
    c: Horizontal(g1)
    c: Coincident(g1,g0)
    c: Parallel(g0,g-4)
    c: Coincident(g2,g1)
    c: Coincident(g2,g0)
    c: Coincident(g3,g0)
    c: Equal(g4,g-5)
    c: Coincident(g4,g1)
    c: Coincident(g4,g0)
    c: InternalAlignment(g6-g9 -> g5) x4
    c: Vertical(g5,g0)
    c: Horizontal(g6)
    c: Coincident(g5,g0)
    c: DistanceX(g6,g-3) = 19.1
    c: Tangent(g10,g3) = -1.5708
    c: PointOnObject(g11,g10)
    c: Tangent(g5,g10,g11) = 1.5708
    c: Coincident(g10,g5)
    c: Coincident(g11,g7)
    c: Parallel(g3,g-4)
    c: DistanceY(g5,g0) = 19
FEATURE [Part::Part2DObjectPython] Clone2D001  label="Sketch130 (2D)"  # Draft 2D object (typed FeaturePython)
  Fuse = false
  Objects = -> [Sketch130]
  Placement = pos=(0,-2,-4e-16) rot=(1,0,0;1.5708rad)
  Scale = (1,1,1)
FEATURE [Sketcher::SketchObject] Sketch131
  ArcFitTolerance = 1e-06
  AttachmentOffset = pos=(0,0,-3.5) rot=(0,0,1;0rad)
  AttachmentSupport = -> [Pad016]
  ExternalGeometry = -> [Binder001]
  FullyConstrained = true
  MakeInternals = false
  MapMode = 5
  Placement = pos=(0,-0.1,-8e-16) rot=(1,0,0;1.5708rad)
  sketch-geometry (1):
    g0: GeomPoint X=-197.47 Y=8.55923 Z=0
  constraints (1):
    c: Symmetric(g-6,g-4,g0)
FEATURE [Sketcher::SketchObject] Sketch132
  ArcFitTolerance = 1e-06
  AttachmentSupport = -> [Pad016]
  ExternalGeometry = -> [Binder001]
  FullyConstrained = true
  MakeInternals = false
  MapMode = 5
  Placement = pos=(0,-3.6,0) rot=(1,0,0;1.5708rad)
  sketch-geometry (3):
    g0: LineSegment [constr] StartX=-215.42 StartY=-53.0314 StartZ=0 EndX=-167.782 EndY=-53.0314 EndZ=0
    g1: Circle CenterX=-191.282 CenterY=-53.0314 CenterZ=0 NormalX=0 NormalY=0 NormalZ=1 AngleXU=0 Radius=11.5
    g2: Circle CenterX=-191.282 CenterY=-53.0314 CenterZ=0 NormalX=0 NormalY=0 NormalZ=1 AngleXU=0 Radius=10.7
  constraints (8):
    c: Coincident(g0,g-3)
    c: PointOnObject(g0,g-4)
    c: Horizontal(g0)
    c: Diameter(g1) = 23
    c: PointOnObject(g1,g0)
    c: DistanceX(g1,g0) = 23.5
    c: Diameter(g2) = 21.4
    c: Coincident(g2,g1)
FEATURE [Part::Part2DObjectPython] ShapeString  # Draft 2D object (typed FeaturePython)
  FontFile = <path>
  Fuse = false
  Justification = 6
  JustificationReference = 0
  KeepLeftMargin = false
  MakeFace = true
  ObliqueAngle = 0
  Placement = pos=(-199,-3.6,-57.5) rot=(1,0,0;1.5708rad)
  ScaleToSize = true
  Size = 10
  String = AS
  Tracking = 0
FEATURE [Sketcher::SketchObject] Sketch133
  ArcFitTolerance = 1e-06
  AttachmentSupport = -> [Binder]
  ExternalGeometry = -> [Binder]
  FullyConstrained = true
  MakeInternals = false
  MapMode = 5
  Placement = pos=(0,9e-16,0) rot=(0,0.707107,0.707107;3.14159rad)
  sketch-geometry (30):
    g0: LineSegment StartX=0 StartY=39.2 StartZ=0 EndX=0 EndY=3.2 EndZ=0
    g1: LineSegment StartX=0 StartY=3.2 StartZ=0 EndX=82.8 EndY=3.2 EndZ=0
    g2: LineSegment StartX=82.8 StartY=3.2 StartZ=0 EndX=82.8 EndY=6.2 EndZ=0
    g3: LineSegment StartX=82.8 StartY=6.2 StartZ=0 EndX=91.752 EndY=6.2 EndZ=0
    g4: LineSegment StartX=0 StartY=39.2 StartZ=0 EndX=195.887 EndY=39.2 EndZ=0
    g5: LineSegment StartX=195.887 StartY=39.2 StartZ=0 EndX=202.765 EndY=20.303 EndZ=0
    g6: LineSegment StartX=192.333 StartY=24.9893 StartZ=0 EndX=196.467 EndY=26.4942 EndZ=0
    g7: LineSegment StartX=196.467 StartY=26.4942 StartZ=0 EndX=194.073 EndY=33.0721 EndZ=0
    g8: LineSegment StartX=194.073 StartY=33.0721 StartZ=0 EndX=189.939 EndY=31.5672 EndZ=0
    g9: LineSegment StartX=189.939 StartY=31.5672 StartZ=0 EndX=192.333 EndY=24.9893 EndZ=0
    g10: ArcOfCircle CenterX=107.6 CenterY=4 CenterZ=0 NormalX=0 NormalY=0 NormalZ=1 AngleXU=0 Radius=16 StartAngle=1.5708 EndAngle=3.00366
    g11: LineSegment StartX=107.6 StartY=20 StartZ=0 EndX=132.428 EndY=20 EndZ=0
    g12: ArcOfCircle [constr] CenterX=132.428 CenterY=4 CenterZ=0 NormalX=0 NormalY=0 NormalZ=1 AngleXU=0 Radius=16 StartAngle=0.314159 EndAngle=1.5708
    g13: LineSegment StartX=147.645 StartY=8.94427 StartZ=0 EndX=176.685 EndY=-80.4316 EndZ=0
    g14: LineSegment StartX=176.685 StartY=-80.4316 StartZ=0 EndX=215.932 EndY=-80.4316 EndZ=0
    g15: ArcOfCircle CenterX=207.583 CenterY=4 CenterZ=0 NormalX=0 NormalY=0 NormalZ=1 AngleXU=0 Radius=17 StartAngle=1.85815 EndAngle=3.57792
    g16: ArcOfCircle CenterX=184.801 CenterY=-67.3089 CenterZ=0 NormalX=0 NormalY=0 NormalZ=1 AngleXU=0 Radius=33.7833 StartAngle=5.88425 EndAngle=6.71952
    g17: LineSegment StartX=192.176 StartY=-3.18451 StartZ=0 EndX=215.42 EndY=-53.0314 EndZ=0
    g18: Circle CenterX=5.6 CenterY=34.8 CenterZ=0 NormalX=0 NormalY=0 NormalZ=1 AngleXU=0 Radius=1.8
    g19: Circle CenterX=5.6 CenterY=7.6 CenterZ=0 NormalX=0 NormalY=0 NormalZ=1 AngleXU=0 Radius=1.8
    g20: Circle CenterX=78.51 CenterY=34.8 CenterZ=0 NormalX=0 NormalY=0 NormalZ=1 AngleXU=0 Radius=1.8
    g21: Circle CenterX=78.51 CenterY=7.6 CenterZ=0 NormalX=0 NormalY=0 NormalZ=1 AngleXU=0 Radius=1.8
    g22: Circle CenterX=184.08 CenterY=34.8 CenterZ=0 NormalX=0 NormalY=0 NormalZ=1 AngleXU=0 Radius=1.8
    g23: Circle CenterX=179.305 CenterY=-76.8316 CenterZ=0 NormalX=0 NormalY=0 NormalZ=1 AngleXU=0 Radius=1.8
    g24: Circle CenterX=213.443 CenterY=-76.8316 CenterZ=0 NormalX=0 NormalY=0 NormalZ=1 AngleXU=0 Radius=1.8
    g25: Circle CenterX=19 CenterY=21.2 CenterZ=0 NormalX=0 NormalY=0 NormalZ=1 AngleXU=0 Radius=6.3
    g26: Circle CenterX=42 CenterY=21.2 CenterZ=0 NormalX=0 NormalY=0 NormalZ=1 AngleXU=0 Radius=6.3
    g27: Circle CenterX=65 CenterY=21.2 CenterZ=0 NormalX=0 NormalY=0 NormalZ=1 AngleXU=0 Radius=6.3
    g28: LineSegment StartX=132.428 StartY=20 StartZ=0 EndX=144.053 EndY=20 EndZ=0
    g29: LineSegment StartX=147.645 StartY=8.94427 StartZ=0 EndX=144.053 EndY=20 EndZ=0
  constraints (65):
    c: Coincident(g0,g-4)
    c: Coincident(g0,g-5)
    c: Coincident(g1,g0)
    c: Coincident(g1,g-6)
    c: Coincident(g2,g1)
    c: Coincident(g2,g-7)
    c: Coincident(g3,g2)
    c: Coincident(g3,g-8)
    c: Coincident(g4,g0)
    c: Coincident(g4,g-16)
    c: Coincident(g5,g4)
    c: Coincident(g5,g-16)
    c: Coincident(g6,g-20)
    c: Coincident(g6,g-21)
    c: Coincident(g7,g6)
    c: Coincident(g7,g-23)
    c: Coincident(g8,g7)
    c: Coincident(g8,g-22)
    c: Coincident(g9,g8)
    c: Coincident(g9,g6)
    c: Equal(g10,g-8)
    c: Coincident(g10,g3)
    c: Coincident(g10,g-9)
    c: Coincident(g11,g10)
    c: Coincident(g11,g-10)
    c: Equal(g12,g-10)
    c: Coincident(g12,g11)
    c: Coincident(g12,g-11)
    c: Coincident(g13,g12)
    c: Coincident(g13,g-12)
    c: Coincident(g14,g13)
    c: Coincident(g14,g-13)
    c: Equal(g15,g-15)
    c: Coincident(g15,g5)
    c: Coincident(g15,g-15)
    c: Equal(g16,g-13)
    c: Coincident(g16,g14)
    c: Coincident(g16,g-14)
    c: Coincident(g17,g15)
    c: Coincident(g17,g16)
    c: Equal(g18,g-28)
    c: Equal(g19,g-29)
    c: Equal(g20,g-26)
    c: Equal(g21,g-27)
    c: Equal(g22,g-17)
    c: Equal(g24,g-25)
    c: Equal(g23,g-24)
    c: Coincident(g23,g-24)
    c: Coincident(g24,g-25)
    c: Coincident(g22,g-17)
    c: Coincident(g20,g-26)
    c: Coincident(g21,g-27)
    c: Coincident(g18,g-28)
    c: Coincident(g19,g-29)
    c: Equal(g25,g-30)
    c: Equal(g26,g-31)
    c: Equal(g27,g-32)
    c: Coincident(g25,g-30)
    c: Coincident(g26,g-31)
    c: Coincident(g27,g-32)
    c: Parallel(g28,g11)
    c: Parallel(g29,g13)
    c: Coincident(g28,g11)
    c: Coincident(g29,g12)
    c: Coincident(g29,g28)
FEATURE [PartDesign::Pad] Pad019
  Direction = (0,1,-2e-16)
  Length = 2
  Length2 = 10
  Profile = -> Sketch133
  ReferenceAxis = -> Sketch133 [N_Axis]
  Refine = true
  Suppressed = false
  Type = 0
FEATURE [Sketcher::SketchObject] Sketch091  label="Sketch091 - forma anteriore"
  ArcFitTolerance = 1e-06
  AttachmentSupport = -> [Pad019]
  ExternalGeometry = -> [Binder]
  FullyConstrained = true
  MakeInternals = false
  MapMode = 5
  Placement = pos=(0,2,0) rot=(0,0.707107,0.707107;3.14159rad)
  sketch-geometry (12):
    g0: Circle CenterX=5.6 CenterY=34.8 CenterZ=0 NormalX=0 NormalY=0 NormalZ=1 AngleXU=0 Radius=1.8
    g1: Circle CenterX=5.6 CenterY=7.6 CenterZ=0 NormalX=0 NormalY=0 NormalZ=1 AngleXU=0 Radius=1.8
    g2: Circle CenterX=78.51 CenterY=34.8 CenterZ=0 NormalX=0 NormalY=0 NormalZ=1 AngleXU=0 Radius=1.8
    g3: Circle CenterX=78.51 CenterY=7.6 CenterZ=0 NormalX=0 NormalY=0 NormalZ=1 AngleXU=0 Radius=1.8
    g4: LineSegment StartX=0 StartY=39.2 StartZ=0 EndX=0 EndY=3.2 EndZ=0
    g5: LineSegment StartX=0 StartY=3.2 StartZ=0 EndX=82.8 EndY=3.2 EndZ=0
    g6: LineSegment StartX=82.8 StartY=3.2 StartZ=0 EndX=82.8 EndY=39.2 EndZ=0
    g7: LineSegment StartX=82.8 StartY=39.2 StartZ=0 EndX=0 EndY=39.2 EndZ=0
    g8: ArcOfCircle CenterX=19 CenterY=21.2 CenterZ=0 NormalX=0 NormalY=0 NormalZ=1 AngleXU=0 Radius=10 StartAngle=1.5708 EndAngle=4.71239
    g9: ArcOfCircle CenterX=65 CenterY=21.2 CenterZ=0 NormalX=0 NormalY=0 NormalZ=1 AngleXU=0 Radius=10 StartAngle=4.71239 EndAngle=7.85398
    g10: LineSegment StartX=19 StartY=31.2 StartZ=0 EndX=65 EndY=31.2 EndZ=0
    g11: LineSegment StartX=19 StartY=11.2 StartZ=0 EndX=65 EndY=11.2 EndZ=0
  constraints (25):
    c: Equal(g2,g-7)
    c: Equal(g3,g-8)
    c: Equal(g1,g-13)
    c: Equal(g0,g-12)
    c: Coincident(g0,g-12)
    c: Coincident(g1,g-13)
    c: Coincident(g3,g-8)
    c: Coincident(g2,g-7)
    c: Coincident(g4,g-4)
    c: Coincident(g4,g-5)
    c: Coincident(g5,g4)
    c: Coincident(g5,g-6)
    c: Coincident(g6,g5)
    c: PointOnObject(g6,g-3)
    c: Vertical(g6)
    c: Coincident(g7,g6)
    c: Coincident(g7,g4)
    c: Tangent(g8,g10) = 1.5708
    c: Tangent(g8,g11) = -1.5708
    c: Tangent(g9,g10) = 1.5708
    c: Tangent(g9,g11) = -1.5708
    c: Equal(g8,g9)
    c: Radius(g8) = 10
    c: Coincident(g8,g-11)
    c: Coincident(g9,g-9)
FEATURE [Sketcher::SketchObject] Sketch093  label="Sketch093 - scavi interni pulsanti"
  ArcFitTolerance = 1e-06
  AttachmentSupport = -> [Pad019]
  ExternalGeometry = -> [Binder]
  FullyConstrained = true
  MakeInternals = false
  MapMode = 5
  Placement = pos=(0,1.8e-15,0) rot=(1,0,0;1.5708rad)
  sketch-geometry (3):
    g0: Circle CenterX=-65 CenterY=21.2 CenterZ=0 NormalX=0 NormalY=0 NormalZ=1 AngleXU=0 Radius=7.3
    g1: Circle CenterX=-42 CenterY=21.2 CenterZ=0 NormalX=0 NormalY=0 NormalZ=1 AngleXU=0 Radius=7.3
    g2: Circle CenterX=-19 CenterY=21.2 CenterZ=0 NormalX=0 NormalY=0 NormalZ=1 AngleXU=0 Radius=7.3
  constraints (6):
    c: Coincident(g0,g-3)
    c: Coincident(g1,g-4)
    c: Coincident(g2,g-5)
    c: Diameter(g0) = 14.6
    c: Diameter(g1) = 14.6
    c: Diameter(g2) = 14.6
FEATURE [Sketcher::SketchObject] Sketch094  label="Sketch094 - forma centrale"
  ArcFitTolerance = 1e-06
  AttachmentSupport = -> [Pad019]
  ExternalGeometry = -> [Binder]
  FullyConstrained = true
  MakeInternals = false
  MapMode = 5
  Placement = pos=(0,2,0) rot=(0,0.707107,0.707107;3.14159rad)
  sketch-geometry (4):
    g0: LineSegment StartX=137.815 StartY=39.2 StartZ=0 EndX=142.655 EndY=24.303 EndZ=0
    g1: LineSegment StartX=110.815 StartY=24.303 StartZ=0 EndX=142.655 EndY=24.303 EndZ=0
    g2: LineSegment StartX=137.815 StartY=39.2 StartZ=0 EndX=110.815 EndY=39.2 EndZ=0
    g3: ArcOfCircle CenterX=92.2534 CenterY=31.7515 CenterZ=0 NormalX=0 NormalY=0 NormalZ=1 AngleXU=0 Radius=20 StartAngle=5.90156 EndAngle=6.66481
  constraints (12):
    c: PointOnObject(g0,g-3)
    c: Tangent(g0,g-5)
    c: Horizontal(g1)
    c: Coincident(g1,g0)
    c: Coincident(g2,g0)
    c: PointOnObject(g2,g-3)
    c: DistanceX(g2,g2) = 27
    c: Vertical(g1,g2)
    c: Coincident(g3,g2)
    c: Radius(g3) = 20
    c: Coincident(g3,g1)
    c: DistanceY(g-6,g0) = 4
FEATURE [Sketcher::SketchObject] Sketch095  label="Sketch095 - forma posteriore"
  ArcFitTolerance = 1e-06
  AttachmentSupport = -> [Pad019]
  ExternalGeometry = -> [Binder]
  FullyConstrained = true
  MakeInternals = false
  MapMode = 5
  Placement = pos=(0,2,0) rot=(0,0.707107,0.707107;3.14159rad)
  sketch-geometry (15):
    g0: LineSegment StartX=137.815 StartY=39.2 StartZ=0 EndX=143.955 EndY=20.303 EndZ=0
    g1: LineSegment StartX=143.955 StartY=20.303 StartZ=0 EndX=190.141 EndY=20.303 EndZ=0
    g2: ArcOfCircle CenterX=184.08 CenterY=34.8 CenterZ=0 NormalX=0 NormalY=0 NormalZ=1 AngleXU=0 Radius=3.5 StartAngle=3.49066 EndAngle=4.71239
    g3: LineSegment StartX=180.791 StartY=33.6029 StartZ=0 EndX=178.754 EndY=39.2 EndZ=0
    g4: LineSegment StartX=184.08 StartY=31.3 StartZ=0 EndX=186.139 EndY=31.3 EndZ=0
    g5: LineSegment StartX=190.141 StartY=20.303 StartZ=0 EndX=186.139 EndY=31.3 EndZ=0
    g6: LineSegment StartX=137.815 StartY=39.2 StartZ=0 EndX=156.815 EndY=39.2 EndZ=0
    g7: LineSegment StartX=178.754 StartY=39.2 StartZ=0 EndX=168.815 EndY=39.2 EndZ=0
    g8: LineSegment StartX=156.815 StartY=31.2 StartZ=0 EndX=168.815 EndY=31.2 EndZ=0
    g9: ArcOfCircle CenterX=176.411 CenterY=35.2 CenterZ=0 NormalX=0 NormalY=0 NormalZ=1 AngleXU=0 Radius=20 StartAngle=2.94023 EndAngle=3.34295
    g10: ArcOfCircle CenterX=188.411 CenterY=35.2 CenterZ=0 NormalX=0 NormalY=0 NormalZ=1 AngleXU=0 Radius=20 StartAngle=2.94023 EndAngle=3.34295
    g11: LineSegment StartX=157.815 StartY=39.2 StartZ=0 EndX=167.815 EndY=39.2 EndZ=0
    g12: LineSegment StartX=157.436 StartY=36.2 StartZ=0 EndX=167.436 EndY=36.2 EndZ=0
    g13: ArcOfCircle CenterX=177.411 CenterY=35.2 CenterZ=0 NormalX=0 NormalY=0 NormalZ=1 AngleXU=0 Radius=20 StartAngle=2.94023 EndAngle=3.09157
    g14: ArcOfCircle CenterX=187.411 CenterY=35.2 CenterZ=0 NormalX=0 NormalY=0 NormalZ=1 AngleXU=0 Radius=20 StartAngle=2.94023 EndAngle=3.09157
  constraints (46):
    c: PointOnObject(g0,g-3)
    c: Tangent(g0,g-6)
    c: Coincident(g1,g0)
    c: Horizontal(g1)
    c: Radius(g2) = 3.5
    c: Coincident(g2,g-5)
    c: PointOnObject(g3,g-3)
    c: Parallel(g3,g-4)
    c: Tangent(g3,g2) = 1.5708
    c: Horizontal(g4)
    c: Tangent(g4,g2) = -1.5708
    c: Coincident(g5,g1)
    c: Parallel(g5,g-4)
    c: Coincident(g5,g4)
    c: DistanceX(g4,g-8) = 3.8
    c: Coincident(g6,g0)
    c: PointOnObject(g6,g-3)
    c: Coincident(g7,g3)
    c: PointOnObject(g7,g-3)
    c: Horizontal(g8)
    c: DistanceX(g6,g7) = 12
    c: Vertical(g8,g6)
    c: Vertical(g7,g8)
    c: DistanceY(g8,g6) = 8
    c: Coincident(g9,g8)
    c: Coincident(g9,g6)
    c: Coincident(g10,g7)
    c: Coincident(g10,g8)
    c: Radius(g9) = 20
    c: Radius(g10) = 20
    c: PointOnObject(g11,g-3)
    c: PointOnObject(g11,g-3)
    c: DistanceX(g11,g11) = 10
    c: DistanceX(g6,g11) = 1
    c: Horizontal(g12)
    c: Equal(g12,g11)
    c: DistanceY(g12,g11) = 3
    c: Coincident(g13,g11)
    c: Coincident(g13,g12)
    c: Radius(g13) = 20
    c: Coincident(g14,g11)
    c: Coincident(g14,g12)
    c: Radius(g14) = 20
    c: DistanceX(g0,g6) = 19
    c: Horizontal(g9,g13)
    c: Horizontal(g0,g-4)
FEATURE [Sketcher::SketchObject] Sketch096  label="Sketch096 - forma impugnatura"
  ArcFitTolerance = 1e-06
  AttachmentSupport = -> [Pad019]
  ExternalGeometry = -> [Binder]
  FullyConstrained = true
  MakeInternals = false
  MapMode = 5
  Placement = pos=(0,2,0) rot=(0,0.707107,0.707107;3.14159rad)
  sketch-geometry (8):
    g0: LineSegment StartX=176.685 StartY=-80.4316 StartZ=0 EndX=143.955 EndY=20.303 EndZ=0
    g1: LineSegment StartX=176.685 StartY=-80.4316 StartZ=0 EndX=215.932 EndY=-80.4316 EndZ=0
    g2: Circle CenterX=179.305 CenterY=-76.8316 CenterZ=0 NormalX=0 NormalY=0 NormalZ=1 AngleXU=0 Radius=3
    g3: Circle CenterX=213.443 CenterY=-76.8316 CenterZ=0 NormalX=0 NormalY=0 NormalZ=1 AngleXU=0 Radius=3
    g4: LineSegment StartX=143.955 StartY=20.303 StartZ=0 EndX=202.765 EndY=20.303 EndZ=0
    g5: LineSegment StartX=215.42 StartY=-53.0314 StartZ=0 EndX=192.176 EndY=-3.18451 EndZ=0
    g6: ArcOfCircle CenterX=184.801 CenterY=-67.3089 CenterZ=0 NormalX=0 NormalY=0 NormalZ=1 AngleXU=0 Radius=33.7833 StartAngle=5.88425 EndAngle=6.71952
    g7: ArcOfCircle CenterX=207.583 CenterY=4 CenterZ=0 NormalX=0 NormalY=0 NormalZ=1 AngleXU=0 Radius=17 StartAngle=1.85815 EndAngle=3.57792
  constraints (19):
    c: Coincident(g0,g-4)
    c: PointOnObject(g0,g-3)
    c: Horizontal(g0,g-7)
    c: Coincident(g1,g0)
    c: Coincident(g1,g-5)
    c: Diameter(g2) = 6
    c: Diameter(g3) = 6
    c: Coincident(g2,g-9)
    c: Coincident(g3,g-10)
    c: Coincident(g4,g0)
    c: Coincident(g5,g-6)
    c: Coincident(g6,g1)
    c: Coincident(g6,g5)
    c: Equal(g-5,g6)
    c: Coincident(g5,g-7)
    c: Coincident(g4,g-7)
    c: Tangent(g7,g-7)
    c: Coincident(g7,g4)
    c: Coincident(g7,g5)
FEATURE [Sketcher::SketchObject] Sketch097
  ArcFitTolerance = 1e-06
  AttachmentSupport = -> [Pad019]
  ExternalGeometry = -> [Binder]
  FullyConstrained = true
  MakeInternals = false
  MapMode = 5
  Placement = pos=(0,2,0) rot=(0,0.707107,0.707107;3.14159rad)
  sketch-geometry (4):
    g0: LineSegment StartX=90 StartY=36.8 StartZ=0 EndX=108 EndY=36.8 EndZ=0
    g1: LineSegment StartX=108 StartY=36.8 StartZ=0 EndX=108 EndY=26.8 EndZ=0
    g2: LineSegment StartX=108 StartY=26.8 StartZ=0 EndX=90 EndY=26.8 EndZ=0
    g3: ArcOfCircle CenterX=94 CenterY=31.8 CenterZ=0 NormalX=0 NormalY=0 NormalZ=1 AngleXU=0 Radius=6.40312 StartAngle=2.24554 EndAngle=4.03765
  constraints (13):
    c: Horizontal(g0)
    c: Coincident(g1,g0)
    c: Vertical(g1)
    c: DistanceX(g0,g0) = 18
    c: DistanceY(g1,g1) = 10
    c: Coincident(g2,g1)
    c: Horizontal(g2)
    c: Equal(g2,g0)
    c: DistanceY(g0,g-3) = 2.4
    c: Coincident(g3,g0)
    c: Coincident(g3,g2)
    c: DistanceX(g2,g3) = 4
    c: DistanceX(g-3,g0) = 90
FEATURE [PartDesign::Chamfer] Chamfer015
  Angle = 45
  Base = -> Pad019 [Edge19,Edge22,Edge79]
  BaseFeature = -> Pad019
  ChamferType = 0
  FlipDirection = false
  Refine = true
  Size = 1.9
  Size2 = 1
  SupportTransform = false
  Suppressed = false
  UseAllEdges = false
FEATURE [PartDesign::Pocket] Pocket002
  BaseFeature = -> Chamfer015
  Direction = (0,1,-2e-16)
  Length = 1.2
  Length2 = 5
  Profile = -> Sketch093
  ReferenceAxis = -> Sketch093 [N_Axis]
  Refine = true
  Suppressed = false
  Type = 0
FEATURE [PartDesign::Pad] Pad005
  BaseFeature = -> Pocket002
  Direction = (0,1,-2e-16)
  Length = 1.6
  Length2 = 10
  Profile = -> Sketch091
  ReferenceAxis = -> Sketch091 [N_Axis]
  Refine = true
  Suppressed = false
  Type = 0
FEATURE [Sketcher::SketchObject] Sketch092  label="Sketch092 - scavi per viti anteriori"
  ArcFitTolerance = 1e-06
  AttachmentSupport = -> [Pad005]
  ExternalGeometry = -> [Binder]
  FullyConstrained = true
  MakeInternals = false
  MapMode = 5
  Placement = pos=(0,3.6,0) rot=(0,0.707107,0.707107;3.14159rad)
  sketch-geometry (20):
    g0: ArcOfCircle CenterX=5.6 CenterY=7.6 CenterZ=0 NormalX=0 NormalY=0 NormalZ=1 AngleXU=0 Radius=3.5 StartAngle=0 EndAngle=1.5708
    g1: ArcOfCircle CenterX=5.6 CenterY=34.8 CenterZ=0 NormalX=0 NormalY=0 NormalZ=1 AngleXU=0 Radius=3.5 StartAngle=4.71239 EndAngle=6.28319
    g2: ArcOfCircle CenterX=78.51 CenterY=34.8 CenterZ=0 NormalX=0 NormalY=0 NormalZ=1 AngleXU=0 Radius=3.5 StartAngle=3.14159 EndAngle=4.71239
    g3: ArcOfCircle CenterX=78.51 CenterY=7.6 CenterZ=0 NormalX=0 NormalY=0 NormalZ=1 AngleXU=0 Radius=3.5 StartAngle=1.5708 EndAngle=3.14159
    g4: LineSegment StartX=0 StartY=3.2 StartZ=0 EndX=0 EndY=11.1 EndZ=0
    g5: LineSegment StartX=0 StartY=11.1 StartZ=0 EndX=5.6 EndY=11.1 EndZ=0
    g6: LineSegment StartX=0 StartY=3.2 StartZ=0 EndX=9.1 EndY=3.2 EndZ=0
    g7: LineSegment StartX=9.1 StartY=3.2 StartZ=0 EndX=9.1 EndY=7.6 EndZ=0
    g8: LineSegment StartX=0 StartY=39.2 StartZ=0 EndX=0 EndY=31.3 EndZ=0
    g9: LineSegment StartX=0 StartY=31.3 StartZ=0 EndX=5.6 EndY=31.3 EndZ=0
    g10: LineSegment StartX=0 StartY=39.2 StartZ=0 EndX=9.1 EndY=39.2 EndZ=0
    g11: LineSegment StartX=9.1 StartY=39.2 StartZ=0 EndX=9.1 EndY=34.8 EndZ=0
    g12: LineSegment StartX=82.8 StartY=39.2 StartZ=0 EndX=75.01 EndY=39.2 EndZ=0
    g13: LineSegment StartX=82.8 StartY=39.2 StartZ=0 EndX=82.8 EndY=31.3 EndZ=0
    g14: LineSegment StartX=82.8 StartY=31.3 StartZ=0 EndX=78.51 EndY=31.3 EndZ=0
    g15: LineSegment StartX=82.8 StartY=3.2 StartZ=0 EndX=75.01 EndY=3.2 EndZ=0
    g16: LineSegment StartX=75.01 StartY=3.2 StartZ=0 EndX=75.01 EndY=7.6 EndZ=0
    g17: LineSegment StartX=82.8 StartY=3.2 StartZ=0 EndX=82.8 EndY=11.1 EndZ=0
    g18: LineSegment StartX=82.8 StartY=11.1 StartZ=0 EndX=78.51 EndY=11.1 EndZ=0
    g19: LineSegment StartX=75.01 StartY=39.2 StartZ=0 EndX=75.01 EndY=34.8 EndZ=0
  constraints (48):
    c: Radius(g0) = 3.5
    c: Coincident(g0,g-10)
    c: Radius(g1) = 3.5
    c: Coincident(g1,g-9)
    c: Radius(g2) = 3.5
    c: Coincident(g2,g-8)
    c: Radius(g3) = 3.5
    c: Coincident(g3,g-7)
    c: Coincident(g4,g-5)
    c: PointOnObject(g4,g-4)
    c: Coincident(g5,g4)
    c: Horizontal(g5)
    c: Coincident(g6,g4)
    c: PointOnObject(g6,g-5)
    c: Coincident(g7,g6)
    c: Vertical(g7)
    c: Coincident(g8,g-4)
    c: PointOnObject(g8,g-4)
    c: Coincident(g9,g8)
    c: Horizontal(g9)
    c: Coincident(g10,g8)
    c: PointOnObject(g10,g-3)
    c: Coincident(g11,g10)
    c: Vertical(g11)
    c: PointOnObject(g12,g-3)
    c: PointOnObject(g12,g-3)
    c: Coincident(g13,g12)
    c: Vertical(g13)
    c: Coincident(g14,g13)
    c: Horizontal(g14)
    c: Coincident(g15,g-6)
    c: PointOnObject(g15,g-5)
    c: Coincident(g16,g15)
    c: Vertical(g16)
    c: Coincident(g17,g15)
    c: Coincident(g18,g17)
    c: Horizontal(g18)
    c: Tangent(g3,g18) = -1.5708
    c: Tangent(g16,g3) = 1.5708
    c: Coincident(g19,g12)
    c: Vertical(g19)
    c: Tangent(g2,g19) = -1.5708
    c: Tangent(g2,g14) = 1.5708
    c: Tangent(g0,g7) = -1.5708
    c: Tangent(g0,g5) = 1.5708
    c: Tangent(g9,g1) = -1.5708
    c: Tangent(g1,g11) = 1.5708
    c: Tangent(g17,g13)
FEATURE [PartDesign::Pocket] Pocket001
  BaseFeature = -> Pad005
  Direction = (0,-1,2e-16)
  Length = 1.6
  Length2 = 5
  Profile = -> Sketch092
  ReferenceAxis = -> Sketch092 [N_Axis]
  Refine = true
  Suppressed = false
  Type = 0
FEATURE [PartDesign::Pad] Pad006
  BaseFeature = -> Pocket001
  Direction = (0,1,-2e-16)
  Length = 0.8
  Length2 = 10
  Profile = -> Sketch094
  ReferenceAxis = -> Sketch094 [N_Axis]
  Refine = true
  Suppressed = false
  Type = 0
FEATURE [PartDesign::Pad] Pad007
  BaseFeature = -> Pad006
  Direction = (0,1,-2e-16)
  Length = 2
  Length2 = 10
  Profile = -> Sketch095
  ReferenceAxis = -> Sketch095 [N_Axis]
  Refine = true
  Suppressed = false
  Type = 0
FEATURE [PartDesign::Pad] Pad008  label="Pad008 - forma impugnatura"
  BaseFeature = -> Pad007
  Direction = (0,1,-2e-16)
  Length = 1.6
  Length2 = 10
  Profile = -> Sketch096
  ReferenceAxis = -> Sketch096 [N_Axis]
  Refine = true
  Suppressed = false
  Type = 0
FEATURE [PartDesign::Pad] Pad009
  BaseFeature = -> Pad008
  Direction = (0,1,-2e-16)
  Length = 1.6
  Length2 = 10
  Profile = -> Sketch097
  ReferenceAxis = -> Sketch097 [N_Axis]
  Refine = true
  Suppressed = false
  Type = 0
FEATURE [Sketcher::SketchObject] Sketch098
  ArcFitTolerance = 1e-06
  AttachmentSupport = -> [Pad006]
  ExternalGeometry = -> [Binder]
  FullyConstrained = true
  MakeInternals = false
  MapMode = 5
  Placement = pos=(0,2.8,-7e-16) rot=(0,0.707107,0.707107;3.14159rad)
  sketch-geometry (4):
    g0: LineSegment StartX=118 StartY=39.2 StartZ=0 EndX=129 EndY=39.2 EndZ=0
    g1: LineSegment StartX=120.599 StartY=31.2 StartZ=0 EndX=131.599 EndY=31.2 EndZ=0
    g2: LineSegment StartX=129 StartY=39.2 StartZ=0 EndX=131.599 EndY=31.2 EndZ=0
    g3: LineSegment StartX=118 StartY=39.2 StartZ=0 EndX=120.599 EndY=31.2 EndZ=0
  constraints (12):
    c: PointOnObject(g0,g-3)
    c: PointOnObject(g0,g-3)
    c: DistanceX(g0,g0) = 11
    c: Horizontal(g1)
    c: Equal(g1,g0)
    c: Coincident(g2,g0)
    c: Coincident(g3,g0)
    c: Parallel(g-4,g2)
    c: Coincident(g1,g2)
    c: Coincident(g1,g3)
    c: DistanceY(g1,g0) = 8
    c: DistanceX(g-3,g0) = 118
FEATURE [Sketcher::SketchObject] Sketch099
  ArcFitTolerance = 1e-06
  AttachmentSupport = -> [Pad008]
  ExternalGeometry = -> [Binder]
  FullyConstrained = true
  MakeInternals = false
  MapMode = 5
  Placement = pos=(0,3.6,0) rot=(0,0.707107,0.707107;3.14159rad)
  sketch-geometry (13):
    g0: LineSegment StartX=192.176 StartY=-3.18451 StartZ=0 EndX=196.804 EndY=-13.1108 EndZ=0
    g1: LineSegment [constr] StartX=202.765 StartY=20.303 StartZ=0 EndX=181.223 EndY=20.303 EndZ=0
    g2: LineSegment [constr] StartX=181.223 StartY=20.303 StartZ=0 EndX=181.223 EndY=-3.18451 EndZ=0
    g3: ArcOfCircle CenterX=181.223 CenterY=-20.3764 CenterZ=0 NormalX=0 NormalY=0 NormalZ=1 AngleXU=0 Radius=17.1918 StartAngle=0.436332 EndAngle=1.57079
    g4: ArcOfEllipse CenterX=181.223 CenterY=8.55923 CenterZ=0 NormalX=0 NormalY=0 NormalZ=1 MajorRadius=23.4779 MinorRadius=11.7437 AngleXU=0 StartAngle=1.5708 EndAngle=4.71239
    g5: LineSegment [constr] StartX=204.701 StartY=8.55923 StartZ=0 EndX=157.745 EndY=8.55923 EndZ=0
    g6: LineSegment [constr] StartX=181.223 StartY=20.303 StartZ=0 EndX=181.223 EndY=-3.18451 EndZ=0
    g7: GeomPoint [constr] X=201.553 Y=8.55923 Z=0
    g8: GeomPoint [constr] X=160.894 Y=8.55923 Z=0
    g9: GeomPoint [constr] X=181.223 Y=-3.18451 Z=0
    g10: LineSegment StartX=181.223 StartY=20.303 StartZ=0 EndX=202.765 EndY=20.303 EndZ=0
    g11: ArcOfCircle CenterX=207.583 CenterY=4 CenterZ=0 NormalX=0 NormalY=0 NormalZ=1 AngleXU=0 Radius=17 StartAngle=1.85815 EndAngle=3.57792
    g12: LineSegment [constr] StartX=172.411 StartY=39.2 StartZ=0 EndX=192.176 EndY=-3.18451 EndZ=0
  constraints (27):
    c: Coincident(g1,g-7)
    c: Horizontal(g1)
    c: Coincident(g2,g1)
    c: Vertical(g2)
    c: Horizontal(g2,g0)
    c: Coincident(g3,g0)
    c: Coincident(g3,g2)
    c: InternalAlignment(g5-g8 -> g4) x4
    c: Horizontal(g5)
    c: PointOnObject(g4,g2)
    c: Coincident(g4,g1)
    c: DistanceX(g-3,g5) = 10.1
    c: Coincident(g4,g2)
    c: Tangent(g3,g-5)
    c: PointOnObject(g9,g4)
    c: PointOnObject(g9,g3)
    c: Tangent(g4,g3,g9) = 1.5708
    c: Coincident(g10,g1)
    c: Coincident(g10,g1)
    c: Equal(g11,g-4)
    c: Coincident(g11,g1)
    c: Coincident(g11,g0)
    c: PointOnObject(g12,g-6)
    c: PointOnObject(g1,g12)
    c: Tangent(g12,g-5) = -1.5708
    c: Tangent(g0,g-5) = -1.5708
    c: Horizontal(g9,g12)
FEATURE [Sketcher::SketchObject] Sketch106  label="Sketch106 - smusso impuniatura interno"
  ArcFitTolerance = 1e-06
  AttachmentSupport = -> [Pad008]
  ExternalGeometry = -> [Pad008]
  FullyConstrained = true
  MakeInternals = false
  MapMode = 5
  Placement = pos=(0,-1.586e-13,-80.4316) rot=(1,0,0;3.14159rad)
  sketch-geometry (9):
    g0: LineSegment StartX=-176.685 StartY=-3.6 StartZ=0 EndX=-176.685 EndY=4.7291e-12 EndZ=0
    g1: LineSegment [constr] StartX=-176.685 StartY=-1.416e-13 StartZ=0 EndX=-176.685 EndY=4.7292e-12 EndZ=0
    g2: LineSegment [constr] StartX=-186.685 StartY=-3.6 StartZ=0 EndX=-186.685 EndY=4.7291e-12 EndZ=0
    g3: ArcOfEllipse CenterX=-186.685 CenterY=4.7292e-12 CenterZ=0 NormalX=0 NormalY=0 NormalZ=1 MajorRadius=10 MinorRadius=3.6 AngleXU=-3.14159 StartAngle=1.5708 EndAngle=3.14159
    g4: LineSegment [constr] StartX=-196.685 StartY=-1.416e-13 StartZ=0 EndX=-176.685 EndY=-1.416e-13 EndZ=0
    g5: LineSegment [constr] StartX=-186.685 StartY=-3.6 StartZ=0 EndX=-186.685 EndY=3.6 EndZ=0
    g6: GeomPoint [constr] X=-196.015 Y=-1.45e-13 Z=0
    g7: GeomPoint [constr] X=-177.356 Y=-1.415e-13 Z=0
    g8: LineSegment StartX=-176.685 StartY=-3.6 StartZ=0 EndX=-186.685 EndY=-3.6 EndZ=0
  constraints (15):
    c: PointOnObject(g2,g-3)
    c: Coincident(g1,g-5)
    c: DistanceY(g1,g1) = 0
    c: Coincident(g0,g1)
    c: DistanceX(g2,g-5) = 10
    c: Vertical(g2)
    c: Horizontal(g2,g0)
    c: InternalAlignment(g4-g7 -> g3) x4
    c: Coincident(g3,g2)
    c: Horizontal(g4)
    c: Coincident(g3,g0)
    c: Tangent(g0,g-5) = 1.5708
    c: Coincident(g3,g2)
    c: Coincident(g8,g0)
    c: Coincident(g8,g2)
FEATURE [Sketcher::SketchObject] Sketch107  label="Sketch107 - smusso impugnatura esterno"
  ArcFitTolerance = 1e-06
  AttachmentSupport = -> [Pad008]
  ExternalGeometry = -> [Pad008]
  FullyConstrained = true
  MakeInternals = false
  MapMode = 5
  Placement = pos=(0,-1.586e-13,-80.4316) rot=(1,0,0;3.14159rad)
  sketch-geometry (9):
    g0: LineSegment [constr] StartX=-215.932 StartY=-1.416e-13 StartZ=0 EndX=-215.932 EndY=-5.3e-14 EndZ=0
    g1: LineSegment StartX=-215.932 StartY=-3.6 StartZ=0 EndX=-215.932 EndY=-5.28e-14 EndZ=0
    g2: LineSegment StartX=-215.932 StartY=-3.6 StartZ=0 EndX=-205.932 EndY=-3.6 EndZ=0
    g3: LineSegment [constr] StartX=-205.932 StartY=-3.6 StartZ=0 EndX=-205.932 EndY=-5.28e-14 EndZ=0
    g4: ArcOfEllipse CenterX=-205.932 CenterY=-5.3e-14 CenterZ=0 NormalX=0 NormalY=0 NormalZ=1 MajorRadius=10 MinorRadius=3.6 AngleXU=-3.14159 StartAngle=-2.66e-14 EndAngle=1.5708
    g5: LineSegment [constr] StartX=-215.932 StartY=-1.416e-13 StartZ=0 EndX=-195.932 EndY=-1.416e-13 EndZ=0
    g6: LineSegment [constr] StartX=-205.932 StartY=-3.6 StartZ=0 EndX=-205.932 EndY=3.6 EndZ=0
    g7: GeomPoint [constr] X=-215.262 Y=-1.425e-13 Z=0
    g8: GeomPoint [constr] X=-196.602 Y=-1.551e-13 Z=0
  constraints (16):
    c: Coincident(g0,g-6)
    c: PointOnObject(g0,g-6)
    c: DistanceY(g0,g0) = 0
    c: Coincident(g1,g-6)
    c: Coincident(g1,g0)
    c: Tangent(g2,g-3)
    c: DistanceX(g2,g2) = 10
    c: Coincident(g3,g2)
    c: Vertical(g3)
    c: Horizontal(g3,g0)
    c: InternalAlignment(g5-g8 -> g4) x4
    c: Coincident(g4,g3)
    c: Horizontal(g5)
    c: Coincident(g4,g0)
    c: Coincident(g4,g2)
    c: PointOnObject(g2,g1)
FEATURE [Sketcher::SketchObject] Sketch108
  ArcFitTolerance = 1e-06
  AttachmentOffset = pos=(0,0,-1.6) rot=(0,0,1;0rad)
  AttachmentSupport = -> [Pad008]
  ExternalGeometry = -> [Binder]
  FullyConstrained = true
  MakeInternals = false
  MapMode = 5
  Placement = pos=(0,2,4e-16) rot=(0,0.707107,0.707107;3.14159rad)
  sketch-geometry (14):
    g0: LineSegment StartX=192.176 StartY=-3.18451 StartZ=0 EndX=193.827 EndY=-6.72678 EndZ=0
    g1: LineSegment [constr] StartX=202.765 StartY=20.303 StartZ=0 EndX=181.223 EndY=20.303 EndZ=0
    g2: LineSegment [constr] StartX=181.223 StartY=20.303 StartZ=0 EndX=181.223 EndY=1.30297 EndZ=0
    g3: ArcOfCircle CenterX=181.223 CenterY=-12.6042 CenterZ=0 NormalX=0 NormalY=0 NormalZ=1 AngleXU=0 Radius=13.9072 StartAngle=0.436332 EndAngle=1.5708
    g4: ArcOfEllipse CenterX=181.223 CenterY=10.803 CenterZ=0 NormalX=0 NormalY=0 NormalZ=1 MajorRadius=14.4779 MinorRadius=9.5 AngleXU=0 StartAngle=1.5708 EndAngle=4.71239
    g5: LineSegment [constr] StartX=195.701 StartY=10.803 StartZ=0 EndX=166.745 EndY=10.803 EndZ=0
    g6: LineSegment [constr] StartX=181.223 StartY=20.303 StartZ=0 EndX=181.223 EndY=1.30297 EndZ=0
    g7: GeomPoint [constr] X=192.148 Y=10.803 Z=0
    g8: GeomPoint [constr] X=170.298 Y=10.803 Z=0
    g9: LineSegment StartX=181.223 StartY=20.303 StartZ=0 EndX=202.765 EndY=20.303 EndZ=0
    g10: ArcOfCircle CenterX=207.583 CenterY=4 CenterZ=0 NormalX=0 NormalY=0 NormalZ=1 AngleXU=0 Radius=17 StartAngle=1.85815 EndAngle=3.57792
    g11: LineSegment [constr] StartX=172.411 StartY=39.2 StartZ=0 EndX=192.176 EndY=-3.18451 EndZ=0
    g12: GeomPoint [constr] X=181.223 Y=1.30297 Z=0
    g13: GeomPoint [constr] X=181.223 Y=1.30297 Z=0
  constraints (28):
    c: Coincident(g1,g-7)
    c: Horizontal(g1)
    c: Coincident(g2,g1)
    c: Vertical(g2)
    c: Coincident(g3,g2)
    c: InternalAlignment(g5-g8 -> g4) x4
    c: Horizontal(g5)
    c: PointOnObject(g4,g2)
    c: Coincident(g4,g1)
    c: DistanceX(g-3,g5) = 19.1
    c: Coincident(g4,g2)
    c: Coincident(g9,g1)
    c: Coincident(g9,g1)
    c: Coincident(g10,g1)
    c: Coincident(g10,g0)
    c: PointOnObject(g11,g-6)
    c: PointOnObject(g1,g11)
    c: DistanceY(g2,g1) = 19
    c: Coincident(g10,g-4)
    c: PointOnObject(g12,g4)
    c: PointOnObject(g12,g3)
    c: Tangent(g11,g-5) = -1.5708
    c: Tangent(g0,g-5) = -1.5708
    c: Tangent(g3,g0) = 1.5708
    c: PointOnObject(g13,g4)
    c: PointOnObject(g13,g3)
    c: Tangent(g4,g3,g13) = 1.5708
    c: Horizontal(g11,g0)
FEATURE [Part::Part2DObjectPython] Clone2D  label="Sketch108 (2D)"  # Draft 2D object (typed FeaturePython)
  Fuse = false
  Objects = -> [Sketch108]
  Placement = pos=(0,2,4e-16) rot=(0,0.707107,0.707107;3.14159rad)
  Scale = (1,1,1)
FEATURE [Sketcher::SketchObject] Sketch109
  ArcFitTolerance = 1e-06
  AttachmentOffset = pos=(0,0,-3.5) rot=(0,0,1;0rad)
  AttachmentSupport = -> [Pad008]
  ExternalGeometry = -> [Binder]
  FullyConstrained = true
  MakeInternals = false
  MapMode = 5
  Placement = pos=(0,0.1,8e-16) rot=(0,0.707107,0.707107;3.14159rad)
  sketch-geometry (1):
    g0: GeomPoint X=197.47 Y=8.55923 Z=0
  constraints (1):
    c: Symmetric(g-7,g-5,g0)
FEATURE [PartDesign::Chamfer] Chamfer005
  Angle = 45
  Base = -> Pad009 [Edge215,Edge212]
  BaseFeature = -> Pad009
  ChamferType = 1
  FlipDirection = false
  Refine = true
  Size = 1.5
  Size2 = 2.8
  SupportTransform = false
  Suppressed = false
  UseAllEdges = false
FEATURE [Sketcher::SketchObject] Sketch111
  ArcFitTolerance = 1e-06
  AttachmentSupport = -> [Pad009]
  ExternalGeometry = -> [Pad009]
  FullyConstrained = true
  MakeInternals = false
  MapMode = 5
  Placement = pos=(0,3.6,-8e-16) rot=(0,0.707107,0.707107;3.14159rad)
  sketch-geometry (21):
    g0: LineSegment [constr] StartX=97 StartY=36.8 StartZ=0 EndX=97 EndY=26.8 EndZ=0
    g1: LineSegment StartX=97 StartY=28.6 StartZ=0 EndX=97 EndY=27.8 EndZ=0
    g2: LineSegment StartX=97 StartY=27.8 StartZ=0 EndX=108 EndY=27.8 EndZ=0
    g3: LineSegment StartX=108 StartY=27.8 StartZ=0 EndX=108 EndY=28.6 EndZ=0
    g4: LineSegment StartX=108 StartY=28.6 StartZ=0 EndX=97 EndY=28.6 EndZ=0
    g5: LineSegment StartX=97 StartY=35.8 StartZ=0 EndX=97 EndY=35 EndZ=0
    g6: LineSegment StartX=97 StartY=35 StartZ=0 EndX=108 EndY=35 EndZ=0
    g7: LineSegment StartX=108 StartY=35 StartZ=0 EndX=108 EndY=35.8 EndZ=0
    g8: LineSegment StartX=108 StartY=35.8 StartZ=0 EndX=97 EndY=35.8 EndZ=0
    g9: LineSegment StartX=97 StartY=30.4 StartZ=0 EndX=97 EndY=29.6 EndZ=0
    g10: LineSegment StartX=97 StartY=29.6 StartZ=0 EndX=108 EndY=29.6 EndZ=0
    g11: LineSegment StartX=108 StartY=29.6 StartZ=0 EndX=108 EndY=30.4 EndZ=0
    g12: LineSegment StartX=108 StartY=30.4 StartZ=0 EndX=97 EndY=30.4 EndZ=0
    g13: LineSegment StartX=97 StartY=34 StartZ=0 EndX=97 EndY=33.2 EndZ=0
    g14: LineSegment StartX=97 StartY=33.2 StartZ=0 EndX=108 EndY=33.2 EndZ=0
    g15: LineSegment StartX=108 StartY=33.2 StartZ=0 EndX=108 EndY=34 EndZ=0
    g16: LineSegment StartX=108 StartY=34 StartZ=0 EndX=97 EndY=34 EndZ=0
    g17: LineSegment StartX=97 StartY=32.2 StartZ=0 EndX=97 EndY=31.4 EndZ=0
    g18: LineSegment StartX=97 StartY=31.4 StartZ=0 EndX=108 EndY=31.4 EndZ=0
    g19: LineSegment StartX=108 StartY=31.4 StartZ=0 EndX=108 EndY=32.2 EndZ=0
    g20: LineSegment StartX=108 StartY=32.2 StartZ=0 EndX=97 EndY=32.2 EndZ=0
  constraints (54):
    c: Vertical(g0)
    c: PointOnObject(g0,g-3)
    c: PointOnObject(g0,g-4)
    c: DistanceX(g0,g-5) = 11
    c: Coincident(g1,g2)
    c: Coincident(g2,g3)
    c: Coincident(g3,g4)
    c: Coincident(g4,g1)
    c: Horizontal(g2)
    c: Horizontal(g4)
    c: Tangent(g1,g0)
    c: Tangent(g3,g-5)
    c: DistanceY(g2,g3) = 0.8
    c: Coincident(g5,g6)
    c: Coincident(g6,g7)
    c: Coincident(g7,g8)
    c: Coincident(g8,g5)
    c: Horizontal(g6)
    c: Horizontal(g8)
    c: DistanceY(g6,g7) = 0.8
    c: Coincident(g9,g10)
    c: Coincident(g10,g11)
    c: Coincident(g11,g12)
    c: Coincident(g12,g9)
    c: Horizontal(g10)
    c: Horizontal(g12)
    c: DistanceY(g10,g11) = 0.8
    c: Tangent(g5,g0)
    c: Tangent(g7,g-5)
    c: Tangent(g9,g0)
    c: Tangent(g11,g-5)
    c: Coincident(g13,g14)
    c: Coincident(g14,g15)
    c: Coincident(g15,g16)
    c: Coincident(g16,g13)
    c: Horizontal(g14)
    c: Horizontal(g16)
    c: DistanceY(g14,g15) = 0.8
    c: Tangent(g13,g0)
    c: Tangent(g15,g-5)
    c: Coincident(g17,g18)
    c: Coincident(g18,g19)
    c: Coincident(g19,g20)
    c: Coincident(g20,g17)
    c: Horizontal(g18)
    c: Horizontal(g20)
    c: DistanceY(g18,g19) = 0.8
    c: Tangent(g17,g0)
    c: Tangent(g19,g-5)
    c: DistanceY(g1,g9) = 1
    c: DistanceY(g9,g17) = 1
    c: DistanceY(g17,g13) = 1
    c: DistanceY(g13,g5) = 1
    c: DistanceY(g0,g1) = 1
FEATURE [PartDesign::Pocket] Pocket004
  BaseFeature = -> Chamfer005
  Direction = (0,-1,2e-16)
  Length = 1
  Length2 = 5
  Profile = -> Sketch111
  ReferenceAxis = -> Sketch111 [N_Axis]
  Refine = true
  Suppressed = false
  Type = 0
FEATURE [PartDesign::Pad] Pad010
  BaseFeature = -> Pocket004
  Direction = (0,1,-2e-16)
  Length = 1.2
  Length2 = 10
  Profile = -> Sketch098
  ReferenceAxis = -> Sketch098 [N_Axis]
  Refine = true
  Suppressed = false
  Type = 0
FEATURE [PartDesign::Chamfer] Chamfer006
  Angle = 45
  Base = -> Pad010 [Edge291]
  BaseFeature = -> Pad010
  ChamferType = 1
  FlipDirection = false
  Refine = true
  Size = 1
  Size2 = 6
  SupportTransform = false
  Suppressed = false
  UseAllEdges = false
FEATURE [Sketcher::SketchObject] Sketch110
  ArcFitTolerance = 1e-06
  AttachmentSupport = -> [Pad010]
  ExternalGeometry = -> [Sketch098]
  FullyConstrained = true
  MakeInternals = false
  MapMode = 5
  Placement = pos=(0,4,-9e-16) rot=(0,0.707107,0.707107;3.14159rad)
  sketch-geometry (8):
    g0: LineSegment StartX=119.69 StartY=34 StartZ=0 EndX=130.69 EndY=34 EndZ=0
    g1: LineSegment StartX=119.95 StartY=33.2 StartZ=0 EndX=130.95 EndY=33.2 EndZ=0
    g2: LineSegment StartX=119.137 StartY=35.7 StartZ=0 EndX=130.137 EndY=35.7 EndZ=0
    g3: LineSegment StartX=118.877 StartY=36.5 StartZ=0 EndX=129.877 EndY=36.5 EndZ=0
    g4: LineSegment StartX=118.877 StartY=36.5 StartZ=0 EndX=119.137 EndY=35.7 EndZ=0
    g5: LineSegment StartX=129.877 StartY=36.5 StartZ=0 EndX=130.137 EndY=35.7 EndZ=0
    g6: LineSegment StartX=119.69 StartY=34 StartZ=0 EndX=119.95 EndY=33.2 EndZ=0
    g7: LineSegment StartX=130.69 StartY=34 StartZ=0 EndX=130.95 EndY=33.2 EndZ=0
  constraints (24):
    c: Horizontal(g0)
    c: Horizontal(g1)
    c: Horizontal(g2)
    c: Horizontal(g3)
    c: Equal(g1,g-5)
    c: Equal(g0,g-5)
    c: Equal(g2,g-5)
    c: Equal(g3,g-5)
    c: PointOnObject(g0,g-3)
    c: PointOnObject(g1,g-3)
    c: PointOnObject(g2,g-3)
    c: PointOnObject(g3,g-3)
    c: Coincident(g4,g3)
    c: Coincident(g4,g2)
    c: Coincident(g5,g3)
    c: Coincident(g5,g2)
    c: Coincident(g6,g0)
    c: Coincident(g6,g1)
    c: Coincident(g7,g0)
    c: Coincident(g7,g1)
    c: DistanceY(g1,g0) = 0.8
    c: DistanceY(g2,g3) = 0.8
    c: DistanceY(g-5,g1) = 2
    c: DistanceY(g-5,g2) = 4.5
FEATURE [PartDesign::Pocket] Pocket003
  BaseFeature = -> Chamfer006
  Direction = (0,-1,2e-16)
  Length = 1
  Length2 = 5
  Profile = -> Sketch110
  ReferenceAxis = -> Sketch110 [N_Axis]
  Refine = true
  Suppressed = false
  Type = 0
FEATURE [PartDesign::SubtractivePipe] SubtractivePipe
  AuxilleryCurvelinear = true
  AuxillerySpineTangent = false
  BaseFeature = -> Pocket003
  Binormal = (0,0,0)
  Mode = 0
  Profile = -> Sketch106
  Refine = true
  Spine = -> Pad008 [Edge215]
  SpineTangent = false
  Suppressed = false
  Transformation = 0
  Transition = 0
FEATURE [PartDesign::SubtractivePipe] SubtractivePipe001
  AuxilleryCurvelinear = true
  AuxillerySpineTangent = false
  BaseFeature = -> SubtractivePipe
  Binormal = (0,0,0)
  Mode = 0
  Profile = -> Sketch107
  Refine = true
  Spine = -> Pad008 [Edge213,Edge216,Edge210]
  SpineTangent = false
  Suppressed = false
  Transformation = 0
  Transition = 0
FEATURE [PartDesign::SubtractiveLoft] SubtractiveLoft
  BaseFeature = -> SubtractivePipe001
  Closed = false
  Profile = -> Sketch099
  Refine = true
  Ruled = false
  Sections = -> [Sketch108]
  Suppressed = false
FEATURE [PartDesign::SubtractiveLoft] SubtractiveLoft001
  BaseFeature = -> SubtractiveLoft
  Closed = false
  Profile = -> Clone2D
  Refine = true
  Ruled = false
  Sections = -> [Sketch109]
  Suppressed = false
FEATURE [Sketcher::SketchObject] Sketch112
  ArcFitTolerance = 1e-06
  AttachmentSupport = -> [Pad008]
  ExternalGeometry = -> [Binder]
  FullyConstrained = true
  MakeInternals = false
  MapMode = 5
  Placement = pos=(0,3.6,0) rot=(0,0.707107,0.707107;3.14159rad)
  sketch-geometry (4):
    g0: LineSegment [constr] StartX=167.782 StartY=-53.0314 StartZ=0 EndX=215.42 EndY=-53.0314 EndZ=0
    g1: GeomPoint [constr] X=191.282 Y=-53.0314 Z=0
    g2: Circle CenterX=191.282 CenterY=-53.0314 CenterZ=0 NormalX=0 NormalY=0 NormalZ=1 AngleXU=0 Radius=11.5
    g3: Circle CenterX=191.282 CenterY=-53.0314 CenterZ=0 NormalX=0 NormalY=0 NormalZ=1 AngleXU=0 Radius=10.7
  constraints (9):
    c: Horizontal(g0)
    c: PointOnObject(g0,g-3)
    c: Diameter(g2) = 23
    c: Coincident(g2,g1)
    c: Diameter(g3) = 21.4
    c: Coincident(g3,g1)
    c: DistanceX(g0,g1) = 23.5
    c: PointOnObject(g1,g0)
    c: Coincident(g0,g-4)
FEATURE [PartDesign::Chamfer] Chamfer016
  Angle = 45
  Base = -> SubtractiveLoft001 [Edge118,Edge117,Edge119,Edge120,Edge109]
  BaseFeature = -> SubtractiveLoft001
  ChamferType = 0
  FlipDirection = false
  Refine = true
  Size = 1.5
  Size2 = 1
  SupportTransform = false
  Suppressed = false
  UseAllEdges = false
FEATURE [PartDesign::Chamfer] Chamfer017
  Angle = 45
  Base = -> Chamfer016 [Edge15]
  BaseFeature = -> Chamfer016
  ChamferType = 0
  FlipDirection = false
  Refine = true
  Size = 1.6
  Size2 = 1
  SupportTransform = false
  Suppressed = false
  UseAllEdges = false
FEATURE [PartDesign::Chamfer] Chamfer018
  Angle = 45
  Base = -> Chamfer017 [Edge10]
  BaseFeature = -> Chamfer017
  ChamferType = 0
  FlipDirection = false
  Refine = true
  Size = 3.5
  Size2 = 1
  SupportTransform = false
  Suppressed = false
  UseAllEdges = false
FEATURE [PartDesign::Chamfer] Chamfer019
  Angle = 45
  Base = -> Chamfer018 [Edge94]
  BaseFeature = -> Chamfer018
  ChamferType = 0
  FlipDirection = false
  Refine = true
  Size = 1.9
  Size2 = 1
  SupportTransform = false
  Suppressed = false
  UseAllEdges = false
FEATURE [PartDesign::Fillet] Fillet009
  Base = -> Chamfer019 [Edge83]
  BaseFeature = -> Chamfer019
  Radius = 1.1
  Refine = true
  SupportTransform = false
  Suppressed = false
  UseAllEdges = false
FEATURE [PartDesign::Fillet] Fillet010
  Base = -> Fillet009 [Edge77]
  BaseFeature = -> Fillet009
  Radius = 1.9
  Refine = true
  SupportTransform = false
  Suppressed = false
  UseAllEdges = false
FEATURE [PartDesign::Pocket] Pocket005
  BaseFeature = -> Fillet010
  Direction = (0,-1,2e-16)
  Length = 0.8
  Length2 = 5
  Profile = -> Sketch112
  ReferenceAxis = -> Sketch112 [N_Axis]
  Refine = true
  Suppressed = false
  Type = 0
FEATURE [Part::Part2DObjectPython] ShapeString001  # Draft 2D object (typed FeaturePython)
  FontFile = <path>
  Fuse = false
  Justification = 6
  JustificationReference = 0
  KeepLeftMargin = false
  MakeFace = true
  ObliqueAngle = 0
  Placement = pos=(-183.5,3.6,-57.5) rot=(0,0.707107,0.707107;3.14159rad)
  ScaleToSize = true
  Size = 10
  String = AS
  Tracking = 0
FEATURE [PartDesign::Pocket] Pocket013
  BaseFeature = -> Pocket005
  Direction = (-1e-16,-1,2e-16)
  Length = 1
  Length2 = 5
  Profile = -> ShapeString001
  ReferenceAxis = -> ShapeString001 [N_Axis]
  Refine = true
  Suppressed = false
  Type = 0
FEATURE [PartDesign::Pad] Pad020
  Direction = (0,-1,2e-16)
  Length = 25.2
  Length2 = 10
  Midplane = true
  Placement = pos=(0,0,0) rot=(1,0,0;1.5708rad)
  Profile = -> Sketch021
  ReferenceAxis = -> Sketch021 [N_Axis]
  Refine = true
  Suppressed = false
  Type = 0
FEATURE [PartDesign::Body] Body001  label="perno fermo rumble e driver solenoide"
  AllowCompound = false
  Group = -> [Sketch021,Pad020]
  Origin = -> Origin001
  Tip = -> Pad020
FEATURE [PartDesign::Pad] Pad021
  Direction = (0,-1,2e-16)
  Length = 16.8
  Length2 = 10
  Midplane = true
  Placement = pos=(0,0,0) rot=(1,0,0;1.5708rad)
  Profile = -> Sketch061
  ReferenceAxis = -> Sketch061 [N_Axis]
  Refine = true
  Suppressed = false
  Type = 0
FEATURE [PartDesign::Pocket] Pocket014
  BaseFeature = -> Pad021
  Direction = (0,1,-2e-16)
  Length = 12.8
  Length2 = 5
  Midplane = true
  Placement = pos=(0,0,0) rot=(1,0,0;1.5708rad)
  Profile = -> Sketch062
  ReferenceAxis = -> Sketch062 [N_Axis]
  Refine = true
  Suppressed = false
  Type = 0
FEATURE [PartDesign::Pad] Pad022
  BaseFeature = -> Pocket014
  Direction = (0,-1,2e-16)
  Length = 7.6
  Length2 = 10
  Midplane = true
  Placement = pos=(0,0,0) rot=(1,0,0;1.5708rad)
  Profile = -> Sketch063
  ReferenceAxis = -> Sketch063 [N_Axis]
  Refine = true
  Suppressed = false
  Type = 0
FEATURE [PartDesign::Body] Body003  label="blocco switch"
  AllowCompound = false
  Group = -> [Sketch061,Sketch062,Sketch063,Pad021,Pocket014,Pad022]
  Origin = -> Origin003
  Tip = -> Pad022
FEATURE [PartDesign::Pad] Pad024
  Direction = (0,-1,2e-16)
  Length = 17
  Length2 = 10
  Midplane = true
  Placement = pos=(0,0,0) rot=(1,0,0;1.5708rad)
  Profile = -> Sketch045
  ReferenceAxis = -> Sketch045 [N_Axis]
  Refine = true
  Suppressed = false
  Type = 0
FEATURE [PartDesign::Pocket] Pocket015
  BaseFeature = -> Pad024
  Direction = (-1,0,0)
  Length = 8
  Length2 = 5
  Placement = pos=(0,0,0) rot=(1,0,0;1.5708rad)
  Profile = -> Sketch047
  ReferenceAxis = -> Sketch047 [N_Axis]
  Refine = true
  Reversed = true
  Suppressed = false
  Type = 0
FEATURE [PartDesign::Pocket] Pocket016
  BaseFeature = -> Pocket015
  Direction = (-1,0,0)
  Length = 1
  Length2 = 5
  Placement = pos=(0,0,0) rot=(1,0,0;1.5708rad)
  Profile = -> Sketch046
  ReferenceAxis = -> Sketch046 [N_Axis]
  Refine = true
  Reversed = true
  Suppressed = false
  Type = 0
FEATURE [PartDesign::Pocket] Pocket017
  BaseFeature = -> Pocket016
  Direction = (0,1,-2e-16)
  Length = 17
  Length2 = 5
  Midplane = true
  Placement = pos=(0,0,0) rot=(1,0,0;1.5708rad)
  Profile = -> Sketch048
  ReferenceAxis = -> Sketch048 [N_Axis]
  Refine = true
  Suppressed = false
  Type = 0
FEATURE [PartDesign::Pad] Pad025
  BaseFeature = -> Pocket017
  Direction = (0,-1,2e-16)
  Length = 17
  Length2 = 10
  Midplane = true
  Placement = pos=(0,0,0) rot=(1,0,0;1.5708rad)
  Profile = -> Sketch049
  ReferenceAxis = -> Sketch049 [N_Axis]
  Refine = true
  Suppressed = false
  Type = 0
FEATURE [PartDesign::Pad] Pad026
  BaseFeature = -> Pad025
  Direction = (0,-1,2e-16)
  Length = 17
  Length2 = 10
  Midplane = true
  Placement = pos=(0,0,0) rot=(1,0,0;1.5708rad)
  Profile = -> Sketch066
  ReferenceAxis = -> Sketch066 [N_Axis]
  Refine = true
  Suppressed = false
  Type = 0
FEATURE [PartDesign::Pad] Pad027
  BaseFeature = -> Pad026
  Direction = (0,-1,2e-16)
  Length = 5
  Length2 = 10
  Midplane = true
  Placement = pos=(0,0,0) rot=(1,0,0;1.5708rad)
  Profile = -> Sketch064
  ReferenceAxis = -> Sketch064 [N_Axis]
  Refine = true
  Suppressed = false
  Type = 0
FEATURE [PartDesign::Pad] Pad028
  BaseFeature = -> Pad027
  Direction = (1,0,0)
  Length = 1
  Length2 = 10
  Placement = pos=(0,0,0) rot=(1,0,0;1.5708rad)
  Profile = -> Sketch068
  ReferenceAxis = -> Sketch068 [N_Axis]
  Refine = true
  Reversed = true
  Suppressed = false
  Type = 0
FEATURE [PartDesign::Chamfer] Chamfer020
  Angle = 45
  Base = -> Pad028 [Edge73,Edge75,Edge78,Edge77]
  BaseFeature = -> Pad028
  ChamferType = 0
  FlipDirection = false
  Placement = pos=(0,0,0) rot=(1,0,0;1.5708rad)
  Refine = true
  Size = 0.5
  Size2 = 1
  SupportTransform = false
  Suppressed = false
  UseAllEdges = false
FEATURE [PartDesign::Body] Body002  label="supporto per neopixel"
  AllowCompound = false
  Group = -> [Sketch045,Sketch047,Sketch046,Sketch048,Sketch049,Sketch066,Sketch064,Sketch068,Pad024,Pocket015,Pocket016,Pocket017,Pad025,Pad026,Pad027,Pad028,Chamfer020]
  Origin = -> Origin002
  Tip = -> Chamfer020
FEATURE [Sketcher::SketchObject] Sketch134  label="perno fermo rumble002"
  ArcFitTolerance = 1e-06
  AttachmentSupport = -> [XZ_Plane008]
  FullyConstrained = true
  MakeInternals = false
  MapMode = 5
  Placement = pos=(0,0,0) rot=(1,0,0;1.5708rad)
  sketch-geometry (16):
    g0: LineSegment StartX=0 StartY=0.45 StartZ=0 EndX=0 EndY=1.55 EndZ=0
    g1: LineSegment StartX=0.45 StartY=2 StartZ=0 EndX=1.55 EndY=2 EndZ=0
    g2: LineSegment StartX=2 StartY=1.55 StartZ=0 EndX=2 EndY=0.45 EndZ=0
    g3: LineSegment StartX=1.55 StartY=0 StartZ=0 EndX=0.45 EndY=0 EndZ=0
    g4: ArcOfCircle [constr] CenterX=0.45 CenterY=1.55 CenterZ=0 NormalX=0 NormalY=0 NormalZ=1 AngleXU=0 Radius=0.45 StartAngle=1.5708 EndAngle=3.14159
    g5: GeomPoint [constr] X=0 Y=2 Z=0
    g6: LineSegment StartX=0.45 StartY=2 StartZ=0 EndX=0 EndY=1.55 EndZ=0
    g7: ArcOfCircle [constr] CenterX=1.55 CenterY=1.55 CenterZ=0 NormalX=0 NormalY=0 NormalZ=1 AngleXU=0 Radius=0.45 StartAngle=0 EndAngle=1.5708
    g8: GeomPoint [constr] X=2 Y=2 Z=0
    g9: LineSegment StartX=2 StartY=1.55 StartZ=0 EndX=1.55 EndY=2 EndZ=0
    g10: ArcOfCircle [constr] CenterX=1.55 CenterY=0.45 CenterZ=0 NormalX=0 NormalY=0 NormalZ=1 AngleXU=0 Radius=0.45 StartAngle=4.71239 EndAngle=6.28319
    g11: GeomPoint [constr] X=2 Y=0 Z=0
    g12: LineSegment StartX=1.55 StartY=0 StartZ=0 EndX=2 EndY=0.45 EndZ=0
    g13: ArcOfCircle [constr] CenterX=0.45 CenterY=0.45 CenterZ=0 NormalX=0 NormalY=0 NormalZ=1 AngleXU=0 Radius=0.45 StartAngle=3.14159 EndAngle=4.71239
    g14: GeomPoint [constr] X=0 Y=0 Z=0
    g15: LineSegment StartX=0 StartY=0.45 StartZ=0 EndX=0.45 EndY=0 EndZ=0
  constraints (35):
    c: Coincident(g14,g-1)
    c: PointOnObject(g5,g-2)
    c: Horizontal(g1)
    c: Vertical(g2)
    c: Horizontal(g3)
    c: DistanceX(g5,g8) = 2
    c: DistanceY(g11,g8) = 2
    c: PointOnObject(g5,g0)
    c: PointOnObject(g5,g1)
    c: Tangent(g0,g4) = 1.5708
    c: Tangent(g1,g4) = 1.5708
    c: Coincident(g6,g0)
    c: Coincident(g6,g1)
    c: PointOnObject(g8,g2)
    c: PointOnObject(g8,g1)
    c: Tangent(g2,g7) = 1.5708
    c: Tangent(g1,g7) = 1.5708
    c: Coincident(g9,g2)
    c: Coincident(g9,g1)
    c: PointOnObject(g11,g2)
    c: PointOnObject(g11,g3)
    c: Tangent(g2,g10) = 1.5708
    c: Tangent(g3,g10) = 1.5708
    c: Coincident(g12,g2)
    c: Coincident(g12,g3)
    c: PointOnObject(g14,g0)
    c: PointOnObject(g14,g3)
    c: Tangent(g0,g13) = 1.5708
    c: Tangent(g3,g13) = 1.5708
    c: Coincident(g15,g0)
    c: Coincident(g15,g3)
    c: Equal(g6,g9)
    c: Equal(g9,g12)
    c: Equal(g12,g15)
    c: DistanceX(g14,g3) = 0.45
FEATURE [PartDesign::Pad] Pad029
  Direction = (0,-1,2e-16)
  Length = 17
  Length2 = 10
  Midplane = true
  Placement = pos=(0,0,0) rot=(1,0,0;1.5708rad)
  Profile = -> Sketch134
  ReferenceAxis = -> Sketch134 [N_Axis]
  Refine = true
  Suppressed = false
  Type = 0
FEATURE [PartDesign::Body] Body008  label="perno fermo neopixel"
  AllowCompound = false
  Group = -> [Sketch134,Pad029]
  Origin = -> Origin008
  Tip = -> Pad029
FEATURE [Sketcher::SketchObject] Sketch135  label="perno fermo rumble003"
  ArcFitTolerance = 1e-06
  AttachmentSupport = -> [XZ_Plane009]
  FullyConstrained = true
  MakeInternals = false
  MapMode = 5
  Placement = pos=(0,0,0) rot=(1,0,0;1.5708rad)
  sketch-geometry (16):
    g0: LineSegment StartX=4.69e-14 StartY=0.8 StartZ=0 EndX=-3.04e-14 EndY=3.1 EndZ=0
    g1: LineSegment StartX=0.8 StartY=3.9 StartZ=0 EndX=3.1 EndY=3.9 EndZ=0
    g2: LineSegment StartX=3.9 StartY=3.1 StartZ=0 EndX=3.9 EndY=0.8 EndZ=0
    g3: LineSegment StartX=3.1 StartY=0 StartZ=0 EndX=0.8 EndY=0 EndZ=0
    g4: ArcOfCircle [constr] CenterX=0.8 CenterY=3.1 CenterZ=0 NormalX=0 NormalY=0 NormalZ=1 AngleXU=0 Radius=0.8 StartAngle=1.5708 EndAngle=3.14159
    g5: GeomPoint [constr] X=0 Y=3.9 Z=0
    g6: LineSegment StartX=0.8 StartY=3.9 StartZ=0 EndX=-3.04e-14 EndY=3.1 EndZ=0
    g7: ArcOfCircle [constr] CenterX=3.1 CenterY=3.1 CenterZ=0 NormalX=0 NormalY=0 NormalZ=1 AngleXU=0 Radius=0.8 StartAngle=-2.4e-14 EndAngle=1.5708
    g8: GeomPoint [constr] X=3.9 Y=3.9 Z=0
    g9: LineSegment StartX=3.9 StartY=3.1 StartZ=0 EndX=3.1 EndY=3.9 EndZ=0
    g10: ArcOfCircle [constr] CenterX=3.1 CenterY=0.8 CenterZ=0 NormalX=0 NormalY=0 NormalZ=1 AngleXU=0 Radius=0.8 StartAngle=4.71239 EndAngle=6.28319
    g11: GeomPoint [constr] X=3.9 Y=0 Z=0
    g12: LineSegment StartX=3.1 StartY=0 StartZ=0 EndX=3.9 EndY=0.8 EndZ=0
    g13: ArcOfCircle [constr] CenterX=0.8 CenterY=0.8 CenterZ=0 NormalX=0 NormalY=0 NormalZ=1 AngleXU=0 Radius=0.8 StartAngle=3.14159 EndAngle=4.71239
    g14: GeomPoint [constr] X=0 Y=0 Z=0
    g15: LineSegment StartX=4.69e-14 StartY=0.8 StartZ=0 EndX=0.8 EndY=0 EndZ=0
  constraints (35):
    c: Coincident(g14,g-1)
    c: PointOnObject(g5,g-2)
    c: Horizontal(g1)
    c: Vertical(g2)
    c: Horizontal(g3)
    c: DistanceX(g5,g8) = 3.9
    c: DistanceY(g11,g8) = 3.9
    c: PointOnObject(g5,g0)
    c: PointOnObject(g5,g1)
    c: Tangent(g0,g4) = 1.5708
    c: Tangent(g1,g4) = 1.5708
    c: Coincident(g6,g0)
    c: Coincident(g6,g1)
    c: PointOnObject(g8,g2)
    c: PointOnObject(g8,g1)
    c: Tangent(g2,g7) = 1.5708
    c: Tangent(g1,g7) = 1.5708
    c: Coincident(g9,g2)
    c: Coincident(g9,g1)
    c: PointOnObject(g11,g2)
    c: PointOnObject(g11,g3)
    c: Tangent(g2,g10) = 1.5708
    c: Tangent(g3,g10) = 1.5708
    c: Coincident(g12,g2)
    c: Coincident(g12,g3)
    c: PointOnObject(g14,g0)
    c: PointOnObject(g14,g3)
    c: Tangent(g0,g13) = 1.5708
    c: Tangent(g3,g13) = 1.5708
    c: Coincident(g15,g0)
    c: Coincident(g15,g3)
    c: Equal(g6,g9)
    c: Equal(g9,g12)
    c: Equal(g12,g15)
    c: DistanceX(g14,g3) = 0.8
FEATURE [PartDesign::Pad] Pad030
  Direction = (0,-1,2e-16)
  Length = 25.2
  Length2 = 10
  Midplane = true
  Placement = pos=(0,0,0) rot=(1,0,0;1.5708rad)
  Profile = -> Sketch135
  ReferenceAxis = -> Sketch135 [N_Axis]
  Refine = true
  Suppressed = false
  Type = 0
FEATURE [PartDesign::Body] Body009  label="perno fermo switch - caricabatterie - grilletto"
  AllowCompound = false
  Group = -> [Sketch135,Pad030]
  Origin = -> Origin009
  Tip = -> Pad030
FEATURE [Sketcher::SketchObject] Sketch136  label="scavo_rele"
  ArcFitTolerance = 1e-06
  AttachmentSupport = -> [XZ_Plane]
  ExternalGeometry = -> [Sketch]
  FullyConstrained = true
  MakeInternals = false
  MapMode = 5
  Placement = pos=(0,0,0) rot=(1,0,0;1.5708rad)
  sketch-geometry (7):
    g0: LineSegment [constr] StartX=-172.456 StartY=-60.9321 StartZ=0 EndX=-176.597 EndY=-73.6763 EndZ=0
    g1: LineSegment [constr] StartX=-172.456 StartY=-60.9321 StartZ=0 EndX=-170.364 EndY=-61.612 EndZ=0
    g2: LineSegment [constr] StartX=-172.456 StartY=-60.9321 StartZ=0 EndX=-176.07 EndY=-59.7579 EndZ=0
    g3: LineSegment StartX=-176.07 StartY=-59.7579 StartZ=0 EndX=-170.364 EndY=-61.612 EndZ=0
    g4: LineSegment StartX=-176.07 StartY=-59.7579 StartZ=0 EndX=-180.211 EndY=-72.502 EndZ=0
    g5: LineSegment StartX=-170.364 StartY=-61.612 StartZ=0 EndX=-174.505 EndY=-74.3561 EndZ=0
    g6: LineSegment StartX=-180.211 StartY=-72.502 StartZ=0 EndX=-174.505 EndY=-74.3561 EndZ=0
  constraints (19):
    c: Tangent(g0,g-3)
    c: Distance(g0,g-3) = 87.2
    c: Distance(g0,g0) = 13.4
    c: Coincident(g1,g0)
    c: Coincident(g2,g0)
    c: Distance(g2) = 3.8
    c: Distance(g1) = 2.2
    c: Perpendicular(g0,g1)
    c: Perpendicular(g0,g2)
    c: Coincident(g3,g2)
    c: Coincident(g3,g1)
    c: Equal(g4,g0)
    c: Equal(g5,g0)
    c: Parallel(g4,g0)
    c: Parallel(g5,g0)
    c: Coincident(g4,g2)
    c: Coincident(g5,g1)
    c: Coincident(g6,g4)
    c: Coincident(g6,g5)
FEATURE [Part::Extrusion] Extrude076  label="Extrude076 - scavo_rele"
  Base = -> Sketch136
  Dir = (0,-1,2e-16)
  DirMode = 2
  FaceMakerClass = Part::FaceMakerBullseye
  FaceMakerMode = 3
  LengthFwd = 18.2
  LengthRev = 0
  Solid = true
  Symmetric = true
FEATURE [Sketcher::SketchObject] Sketch137  label="scavo_nuovo_driver"
  ArcFitTolerance = 1e-06
  AttachmentSupport = -> [XZ_Plane]
  ExternalGeometry = -> [Sketch]
  FullyConstrained = true
  MakeInternals = false
  MapMode = 5
  Placement = pos=(0,0,0) rot=(1,0,0;1.5708rad)
  sketch-geometry (7):
    g0: LineSegment [constr] StartX=-160.034 StartY=-22.6997 StartZ=0 EndX=-164.854 EndY=-37.5361 EndZ=0
    g1: LineSegment [constr] StartX=-160.034 StartY=-22.6997 StartZ=0 EndX=-156.99 EndY=-23.6885 EndZ=0
    g2: LineSegment [constr] StartX=-160.034 StartY=-22.6997 StartZ=0 EndX=-163.648 EndY=-21.5254 EndZ=0
    g3: LineSegment StartX=-163.648 StartY=-21.5254 StartZ=0 EndX=-156.99 EndY=-23.6885 EndZ=0
    g4: LineSegment StartX=-163.648 StartY=-21.5254 StartZ=0 EndX=-168.468 EndY=-36.3619 EndZ=0
    g5: LineSegment StartX=-156.99 StartY=-23.6885 StartZ=0 EndX=-161.811 EndY=-38.525 EndZ=0
    g6: LineSegment StartX=-168.468 StartY=-36.3619 StartZ=0 EndX=-161.811 EndY=-38.525 EndZ=0
  constraints (19):
    c: Distance(g0,g-3) = 47
    c: Distance(g0) = 15.6
    c: Tangent(g0,g-3)
    c: Coincident(g1,g0)
    c: Coincident(g2,g0)
    c: Distance(g1) = 3.2
    c: Distance(g2) = 3.8
    c: Perpendicular(g0,g1)
    c: Perpendicular(g0,g2)
    c: Coincident(g3,g2)
    c: Coincident(g3,g1)
    c: Equal(g4,g0)
    c: Equal(g5,g0)
    c: Parallel(g4,g0)
    c: Parallel(g5,g0)
    c: Coincident(g4,g2)
    c: Coincident(g5,g1)
    c: Coincident(g6,g4)
    c: Coincident(g6,g5)
FEATURE [Part::Extrusion] Extrude077  label="Extrude077 - scavo_nuovo_driver"
  Base = -> Sketch137
  Dir = (0,-1,2e-16)
  DirMode = 2
  FaceMakerClass = Part::FaceMakerBullseye
  FaceMakerMode = 3
  LengthFwd = 20.8
  LengthRev = 0
  Solid = true
  Symmetric = true
FEATURE [Sketcher::SketchObject] Sketch138  label="scavo_nuovo_driver_alto"
  ArcFitTolerance = 1e-06
  AttachmentSupport = -> [XZ_Plane]
  ExternalGeometry = -> [Sketch]
  FullyConstrained = true
  MakeInternals = false
  MapMode = 5
  Placement = pos=(0,0,0) rot=(1,0,0;1.5708rad)
  sketch-geometry (7):
    g0: LineSegment [constr] StartX=-188.796 StartY=17.7274 StartZ=0 EndX=-187.75 EndY=4.97025 EndZ=0
    g1: LineSegment StartX=-187.75 StartY=4.97025 StartZ=0 EndX=-189.743 EndY=4.8067 EndZ=0
    g2: LineSegment StartX=-187.75 StartY=4.97025 StartZ=0 EndX=-182.766 EndY=5.37913 EndZ=0
    g3: LineSegment StartX=-190.79 StartY=17.5638 StartZ=0 EndX=-189.743 EndY=4.8067 EndZ=0
    g4: LineSegment StartX=-183.813 StartY=18.1363 StartZ=0 EndX=-182.766 EndY=5.37913 EndZ=0
    g5: LineSegment StartX=-190.79 StartY=17.5638 StartZ=0 EndX=-188.796 EndY=17.7274 EndZ=0
    g6: LineSegment StartX=-188.796 StartY=17.7274 StartZ=0 EndX=-183.813 EndY=18.1363 EndZ=0
  constraints (20):
    c: Distance(g0) = 12.8
    c: DistanceY(g-3,g0) = 9
    c: PointOnObject(g0,g-4)
    c: PointOnObject(g0,g-4)
    c: Coincident(g1,g0)
    c: Coincident(g2,g0)
    c: Distance(g1) = 2
    c: Distance(g2) = 5
    c: Perpendicular(g0,g1)
    c: Perpendicular(g0,g2)
    c: Equal(g3,g0)
    c: Parallel(g3,g0)
    c: Coincident(g3,g1)
    c: Equal(g4,g0)
    c: Parallel(g4,g0)
    c: Coincident(g4,g2)
    c: Coincident(g5,g3)
    c: Coincident(g5,g0)
    c: Coincident(g6,g0)
    c: Coincident(g6,g4)
FEATURE [Part::Extrusion] Extrude078  label="Extrude078 - scavo_nuovo_driver_alto"
  Base = -> Sketch138
  Dir = (0,-1,2e-16)
  DirMode = 2
  FaceMakerClass = Part::FaceMakerBullseye
  FaceMakerMode = 3
  LengthFwd = 16.6
  LengthRev = 0
  Solid = true
  Symmetric = true
FEATURE [Sketcher::SketchObject] Sketch139  label="fermi_nuovo_driver_alto"
  ArcFitTolerance = 1e-06
  AttachmentSupport = -> [XZ_Plane]
  ExternalGeometry = -> [Sketch138,Sketch]
  FullyConstrained = true
  MakeInternals = false
  MapMode = 5
  Placement = pos=(0,0,0) rot=(1,0,0;1.5708rad)
  sketch-geometry (17):
    g0: LineSegment [constr] StartX=-188.314 StartY=16.4295 StartZ=0 EndX=-187.885 EndY=13.7638 EndZ=0
    g1: LineSegment [constr] StartX=-187.885 StartY=13.7638 StartZ=0 EndX=-187.456 EndY=11.0981 EndZ=0
    g2: LineSegment StartX=-187.885 StartY=13.7638 StartZ=0 EndX=-187.71 EndY=12.6778 EndZ=0
    g3: LineSegment StartX=-187.885 StartY=13.7638 StartZ=0 EndX=-188.06 EndY=14.8499 EndZ=0
    g4: LineSegment StartX=-187.71 StartY=12.6778 StartZ=0 EndX=-185.538 EndY=13.0274 EndZ=0
    g5: LineSegment StartX=-188.06 StartY=14.8499 StartZ=0 EndX=-185.888 EndY=15.1994 EndZ=0
    g6: LineSegment StartX=-185.888 StartY=15.1994 StartZ=0 EndX=-185.538 EndY=13.0274 EndZ=0
    g7: LineSegment StartX=-187.456 StartY=11.0981 StartZ=0 EndX=-189.035 EndY=10.8439 EndZ=0
    g8: LineSegment StartX=-188.314 StartY=16.4295 StartZ=0 EndX=-189.893 EndY=16.1753 EndZ=0
    g9: LineSegment StartX=-189.893 StartY=16.1753 StartZ=0 EndX=-189.035 EndY=10.8439 EndZ=0
    g10: LineSegment StartX=-187.456 StartY=11.0981 StartZ=0 EndX=-185.284 EndY=11.4477 EndZ=0
    g11: LineSegment StartX=-188.314 StartY=16.4295 StartZ=0 EndX=-186.142 EndY=16.7791 EndZ=0
    g12: LineSegment StartX=-184.308 StartY=15.4537 StartZ=0 EndX=-183.958 EndY=13.2816 EndZ=0
    g13: ArcOfCircle CenterX=-185.888 CenterY=15.1994 CenterZ=0 NormalX=0 NormalY=0 NormalZ=1 AngleXU=0 Radius=1.6 StartAngle=0.15957 EndAngle=1.73037
    g14: GeomPoint [constr] X=-184.562 Y=17.0333 Z=0
    g15: ArcOfCircle CenterX=-185.538 CenterY=13.0274 CenterZ=0 NormalX=0 NormalY=0 NormalZ=1 AngleXU=0 Radius=1.6 StartAngle=4.87196 EndAngle=6.44276
    g16: GeomPoint [constr] X=-183.704 Y=11.7019 Z=0
  constraints (43):
    c: Tangent(g1,g0) = -1.5708
    c: Distance(g0) = 2.7
    c: Equal(g1,g0)
    c: Tangent(g1,g-5)
    c: Coincident(g2,g0)
    c: Coincident(g3,g0)
    c: Distance(g2) = 1.1
    c: Equal(g3,g2)
    c: PointOnObject(g3,g2)
    c: Coincident(g4,g2)
    c: Coincident(g5,g3)
    c: Distance(g4) = 2.2
    c: Equal(g4,g5)
    c: Perpendicular(g1,g4)
    c: Perpendicular(g0,g5)
    c: Coincident(g6,g5)
    c: Coincident(g6,g4)
    c: Coincident(g7,g1)
    c: Coincident(g8,g0)
    c: Distance(g7) = 1.6
    c: Equal(g7,g8)
    c: Perpendicular(g1,g7)
    c: Perpendicular(g8,g0)
    c: Coincident(g9,g8)
    c: Coincident(g9,g7)
    c: Coincident(g10,g1)
    c: Coincident(g11,g0)
    c: Distance(g10,g16) = 3.8
    c: Perpendicular(g1,g10)
    c: Perpendicular(g1,g11)
    c: DistanceY(g0,g-4) = 3.8
    c: PointOnObject(g14,g12)
    c: PointOnObject(g14,g11)
    c: Tangent(g12,g13) = 1.5708
    c: Tangent(g11,g13) = 1.5708
    c: PointOnObject(g16,g12)
    c: PointOnObject(g16,g10)
    c: Tangent(g12,g15) = 1.5708
    c: Tangent(g10,g15) = -1.5708
    c: Equal(g13,g15)
    c: Coincident(g13,g5)
    c: Parallel(g2,g0)
    c: PointOnObject(g0,g-5)
FEATURE [Part::Extrusion] Extrude079  label="Extrude079 - fermi_nuovo_driver_alto"
  Base = -> Sketch139
  Dir = (0,-1,2e-16)
  DirMode = 2
  FaceMakerClass = Part::FaceMakerBullseye
  FaceMakerMode = 3
  LengthFwd = 25.2
  LengthRev = 0
  Solid = true
  Symmetric = true
FEATURE [Sketcher::SketchObject] Sketch140  label="scavo_diodo_nuovo_driver_alto"
  ArcFitTolerance = 1e-06
  AttachmentSupport = -> [XZ_Plane]
  ExternalGeometry = -> [Sketch138]
  FullyConstrained = true
  MakeInternals = false
  MapMode = 5
  Placement = pos=(0,0,0) rot=(1,0,0;1.5708rad)
  sketch-geometry (4):
    g0: LineSegment StartX=-190.79 StartY=17.5638 StartZ=0 EndX=-189.743 EndY=4.8067 EndZ=0
    g1: LineSegment StartX=-193.78 StartY=17.3185 StartZ=0 EndX=-192.733 EndY=4.56137 EndZ=0
    g2: LineSegment StartX=-190.79 StartY=17.5638 StartZ=0 EndX=-193.78 EndY=17.3185 EndZ=0
    g3: LineSegment StartX=-192.733 StartY=4.56137 StartZ=0 EndX=-189.743 EndY=4.8067 EndZ=0
  constraints (11):
    c: Equal(g0,g-3)
    c: Parallel(g0,g-3)
    c: Equal(g1,g-3)
    c: Parallel(g1,g-3)
    c: Coincident(g2,g0)
    c: Distance(g2) = 3
    c: Perpendicular(g0,g2)
    c: Coincident(g1,g2)
    c: Coincident(g3,g1)
    c: Coincident(g3,g0)
    c: Coincident(g0,g-3)
FEATURE [Part::Extrusion] Extrude080  label="Extrude080 - scavo_diodo_nuovo_driver_alto"
  Base = -> Sketch140
  Dir = (0,-1,2e-16)
  DirMode = 2
  FaceMakerClass = Part::FaceMakerBullseye
  FaceMakerMode = 3
  LengthFwd = 4
  LengthRev = 0
  Placement = pos=(0,7.8,0) rot=(0,0,1;0rad)
  Solid = true
  Symmetric = false
FEATURE [Part::MultiFuse] Fusion001
  Refine = true
  Shapes = -> [Cut043,Extrude079]
FEATURE [Part::Cut] Cut044
  Base = -> Fusion001
  Refine = true
  Tool = -> Extrude078
FEATURE [Part::Cut] Cut045
  Base = -> Cut044
  Refine = true
  Tool = -> Extrude080
FEATURE [Sketcher::SketchObject] Sketch141  label="fermi_nuovo_driver"
  ArcFitTolerance = 1e-06
  AttachmentSupport = -> [XZ_Plane]
  ExternalGeometry = -> [Sketch,Sketch137]
  FullyConstrained = true
  MakeInternals = false
  MapMode = 5
  Placement = pos=(0,0,0) rot=(1,0,0;1.5708rad)
  sketch-geometry (17):
    g0: LineSegment [constr] StartX=-156.99 StartY=-23.6885 StartZ=0 EndX=-160.034 EndY=-22.6997 EndZ=0
    g1: LineSegment [constr] StartX=-160.034 StartY=-22.6997 StartZ=0 EndX=-162.815 EndY=-31.2592 EndZ=0
    g2: LineSegment [constr] StartX=-162.815 StartY=-31.2592 StartZ=0 EndX=-164.484 EndY=-36.3949 EndZ=0
    g3: LineSegment StartX=-164.484 StartY=-36.3949 StartZ=0 EndX=-166.576 EndY=-35.715 EndZ=0
    g4: LineSegment StartX=-167.603 StartY=-33.6989 StartZ=0 EndX=-166.923 EndY=-31.6066 EndZ=0
    g5: LineSegment StartX=-164.907 StartY=-30.5793 StartZ=0 EndX=-161.293 EndY=-31.7536 EndZ=0
    g6: LineSegment StartX=-161.293 StartY=-31.7536 StartZ=0 EndX=-162.962 EndY=-36.8893 EndZ=0
    g7: LineSegment StartX=-164.484 StartY=-36.3949 StartZ=0 EndX=-162.962 EndY=-36.8893 EndZ=0
    g8: LineSegment StartX=-165.402 StartY=-32.101 StartZ=0 EndX=-166.082 EndY=-34.1933 EndZ=0
    g9: LineSegment StartX=-166.082 StartY=-34.1933 StartZ=0 EndX=-163.989 EndY=-34.8732 EndZ=0
    g10: LineSegment StartX=-163.989 StartY=-34.8732 StartZ=0 EndX=-163.309 EndY=-32.7809 EndZ=0
    g11: LineSegment StartX=-163.309 StartY=-32.7809 StartZ=0 EndX=-165.402 EndY=-32.101 EndZ=0
    g12: ArcOfCircle CenterX=-165.402 CenterY=-32.101 CenterZ=0 NormalX=0 NormalY=0 NormalZ=1 AngleXU=0 Radius=1.6 StartAngle=1.25664 EndAngle=2.82743
    g13: GeomPoint [constr] X=-166.429 Y=-30.0849 Z=0
    g14: ArcOfCircle CenterX=-166.082 CenterY=-34.1933 CenterZ=0 NormalX=0 NormalY=0 NormalZ=1 AngleXU=0 Radius=1.6 StartAngle=2.82743 EndAngle=4.39823
    g15: GeomPoint [constr] X=-168.098 Y=-35.2206 Z=0
    g16: LineSegment [constr] StartX=-160.034 StartY=-22.6997 StartZ=0 EndX=-164.854 EndY=-37.5361 EndZ=0
  constraints (44):
    c: Coincident(g0,g-4)
    c: PointOnObject(g0,g-3)
    c: Parallel(g0,g-4)
    c: Coincident(g1,g0)
    c: Parallel(g1,g-3)
    c: Coincident(g2,g1)
    c: Distance(g2) = 5.4
    c: Coincident(g3,g2)
    c: Parallel(g2,g-3)
    c: Distance(g15,g13) = 5.4
    c: Perpendicular(g3,g2)
    c: Parallel(g4,g2)
    c: Distance(g5,g13) = 5.4
    c: Distance(g3,g15) = 3.8
    c: Perpendicular(g4,g5)
    c: Coincident(g6,g5)
    c: Distance(g6) = 5.4
    c: Parallel(g6,g4)
    c: Coincident(g7,g2)
    c: Coincident(g7,g6)
    c: Coincident(g8,g9)
    c: Coincident(g9,g10)
    c: Coincident(g10,g11)
    c: Coincident(g11,g8)
    c: Distance(g8,g10) = 2.2
    c: Distance(g9,g11) = 2.2
    c: Perpendicular(g11,g8)
    c: Equal(g8,g10)
    c: Equal(g11,g9)
    c: Tangent(g10,g2)
    c: Distance(g10,g1) = 1.6
    c: PointOnObject(g13,g4)
    c: PointOnObject(g13,g5)
    c: Tangent(g4,g12) = 1.5708
    c: Tangent(g5,g12) = 1.5708
    c: PointOnObject(g15,g4)
    c: Tangent(g4,g14) = 1.5708
    c: Tangent(g3,g14) = 1.5708
    c: Equal(g14,g12)
    c: Coincident(g12,g8)
    c: Coincident(g16,g0)
    c: PointOnObject(g16,g-5)
    c: Parallel(g16,g-3)
    c: Distance(g16,g2) = 1.2
FEATURE [Part::Extrusion] Extrude081  label="Extrude081 - fermi_nuovo_driver"
  Base = -> Sketch141
  Dir = (0,-1,2e-16)
  DirMode = 2
  FaceMakerClass = Part::FaceMakerBullseye
  FaceMakerMode = 3
  LengthFwd = 25.2
  LengthRev = 0
  Solid = true
  Symmetric = true
FEATURE [Part::MultiFuse] Fusion002
  Refine = true
  Shapes = -> [Cut045,Extrude081]
FEATURE [Part::Cut] Cut046
  Base = -> Fusion002
  Refine = true
  Tool = -> Extrude077
FEATURE [Sketcher::SketchObject] Sketch142  label="fermi_rele"
  ArcFitTolerance = 1e-06
  AttachmentSupport = -> [XZ_Plane]
  ExternalGeometry = -> [Sketch,Sketch136]
  FullyConstrained = true
  MakeInternals = false
  MapMode = 5
  Placement = pos=(0,0,0) rot=(1,0,0;1.5708rad)
  sketch-geometry (15):
    g0: LineSegment StartX=-176.936 StartY=-62.4208 StartZ=0 EndX=-177.615 EndY=-64.5131 EndZ=0
    g1: LineSegment StartX=-174.919 StartY=-61.3936 StartZ=0 EndX=-171.305 EndY=-62.5678 EndZ=0
    g2: LineSegment StartX=-171.305 StartY=-62.5678 StartZ=0 EndX=-172.974 EndY=-67.7035 EndZ=0
    g3: LineSegment StartX=-176.588 StartY=-66.5293 StartZ=0 EndX=-172.974 EndY=-67.7035 EndZ=0
    g4: LineSegment StartX=-175.414 StartY=-62.9152 StartZ=0 EndX=-173.322 EndY=-63.5951 EndZ=0
    g5: LineSegment StartX=-175.414 StartY=-62.9152 StartZ=0 EndX=-176.094 EndY=-65.0076 EndZ=0
    g6: LineSegment StartX=-173.322 StartY=-63.5951 StartZ=0 EndX=-174.001 EndY=-65.6874 EndZ=0
    g7: LineSegment StartX=-176.094 StartY=-65.0076 StartZ=0 EndX=-174.001 EndY=-65.6874 EndZ=0
    g8: LineSegment [constr] StartX=-173.322 StartY=-63.5951 StartZ=0 EndX=-172.827 EndY=-62.0734 EndZ=0
    g9: LineSegment [constr] StartX=-173.322 StartY=-63.5951 StartZ=0 EndX=-171.8 EndY=-64.0895 EndZ=0
    g10: LineSegment [constr] StartX=-170.364 StartY=-61.612 StartZ=0 EndX=-172.456 EndY=-60.9321 EndZ=0
    g11: ArcOfCircle CenterX=-175.414 CenterY=-62.9152 CenterZ=0 NormalX=0 NormalY=0 NormalZ=1 AngleXU=0 Radius=1.6 StartAngle=1.25664 EndAngle=2.82743
    g12: GeomPoint [constr] X=-176.441 Y=-60.8991 Z=0
    g13: ArcOfCircle CenterX=-176.094 CenterY=-65.0076 CenterZ=0 NormalX=0 NormalY=0 NormalZ=1 AngleXU=0 Radius=1.6 StartAngle=2.82743 EndAngle=4.39823
    g14: GeomPoint [constr] X=-178.11 Y=-66.0348 Z=0
  constraints (39):
    c: Distance(g14,g12) = 5.4
    c: Distance(g1,g12) = 5.4
    c: Perpendicular(g1,g0)
    c: Coincident(g2,g1)
    c: Parallel(g2,g0)
    c: Coincident(g3,g2)
    c: Parallel(g2,g-3)
    c: Coincident(g5,g4)
    c: Distance(g5) = 2.2
    c: Distance(g4) = 2.2
    c: Perpendicular(g4,g5)
    c: Coincident(g6,g4)
    c: Equal(g6,g5)
    c: Parallel(g6,g5)
    c: Coincident(g7,g5)
    c: Coincident(g7,g6)
    c: Coincident(g8,g4)
    c: Coincident(g9,g4)
    c: Distance(g8) = 1.6
    c: Distance(g9) = 1.6
    c: Parallel(g8,g6)
    c: Parallel(g9,g4)
    c: PointOnObject(g8,g1)
    c: PointOnObject(g9,g2)
    c: Coincident(g10,g-4)
    c: Parallel(g10,g-4)
    c: PointOnObject(g10,g-3)
    c: Tangent(g6,g-3) = 1.5708
    c: Distance(g4,g10) = 2.8
    c: PointOnObject(g12,g1)
    c: Tangent(g1,g11) = 1.5708
    c: Tangent(g0,g11) = -1.5708
    c: PointOnObject(g14,g3)
    c: PointOnObject(g14,g0)
    c: Tangent(g3,g13) = -1.5708
    c: Tangent(g0,g13) = -1.5708
    c: Equal(g11,g13)
    c: Coincident(g11,g4)
    c: Parallel(g3,g1)
FEATURE [Part::Extrusion] Extrude082  label="Extrude082 - fermi_rele"
  Base = -> Sketch142
  Dir = (0,-1,2e-16)
  DirMode = 2
  FaceMakerClass = Part::FaceMakerBullseye
  FaceMakerMode = 3
  LengthFwd = 25.2
  LengthRev = 0
  Solid = true
  Symmetric = true
FEATURE [Part::MultiFuse] Fusion003
  Refine = true
  Shapes = -> [Cut046,Extrude082]
FEATURE [Part::Cut] Cut047
  Base = -> Fusion003
  Refine = true
  Tool = -> Extrude076
FEATURE [Sketcher::SketchObject] Sketch143  label="foro_passaggio_cavi_led_batteria"
  ArcFitTolerance = 1e-06
  AttachmentSupport = -> [XZ_Plane]
  ExternalGeometry = -> [Sketch,Sketch042,Sketch036]
  FullyConstrained = true
  MakeInternals = false
  MapMode = 5
  Placement = pos=(0,0,0) rot=(1,0,0;1.5708rad)
  sketch-geometry (4):
    g0: LineSegment StartX=-207.775 StartY=-41.3701 StartZ=0 EndX=-213.607 EndY=-53.8767 EndZ=0
    g1: LineSegment StartX=-213.607 StartY=-53.8767 StartZ=0 EndX=-211.843 EndY=-59.5559 EndZ=0
    g2: LineSegment StartX=-207.775 StartY=-41.3701 StartZ=0 EndX=-207.775 EndY=-50.8316 EndZ=0
    g3: LineSegment StartX=-207.775 StartY=-50.8316 StartZ=0 EndX=-211.843 EndY=-59.5559 EndZ=0
  constraints (9):
    c: Coincident(g0,g-3)
    c: PointOnObject(g1,g-6)
    c: Coincident(g1,g0)
    c: Coincident(g2,g0)
    c: Coincident(g2,g-7)
    c: Coincident(g3,g2)
    c: Parallel(g3,g0)
    c: Coincident(g3,g1)
    c: Coincident(g0,g-5)
FEATURE [Part::Extrusion] Extrude083  label="Extrude083 - foro_passaggio_cavi_led_batteria"
  Base = -> Sketch143
  Dir = (0,-1,2e-16)
  DirMode = 2
  FaceMakerClass = Part::FaceMakerBullseye
  FaceMakerMode = 3
  LengthFwd = 6
  LengthRev = 0
  Solid = true
  Symmetric = true
FEATURE [Part::Cut] Cut048
  Base = -> Cut047
  Refine = true
  Tool = -> Extrude083
FEATURE [Sketcher::SketchObject] Sketch144  label="foro_areazione_alimentatore"
  ArcFitTolerance = 1e-06
  AttachmentSupport = -> [XZ_Plane]
  ExternalGeometry = -> [Sketch036]
  FullyConstrained = true
  MakeInternals = false
  MapMode = 5
  Placement = pos=(0,0,0) rot=(1,0,0;1.5708rad)
  sketch-geometry (4):
    g0: LineSegment StartX=-211.843 StartY=-60.3701 StartZ=0 EndX=-207.775 EndY=-60.3701 EndZ=0
    g1: LineSegment StartX=-207.775 StartY=-60.3701 StartZ=0 EndX=-207.775 EndY=-70.3701 EndZ=0
    g2: LineSegment StartX=-211.843 StartY=-60.3701 StartZ=0 EndX=-211.843 EndY=-70.3701 EndZ=0
    g3: LineSegment StartX=-207.775 StartY=-70.3701 StartZ=0 EndX=-211.843 EndY=-70.3701 EndZ=0
  constraints (11):
    c: Horizontal(g0)
    c: Distance(g1) = 10
    c: Coincident(g1,g0)
    c: Tangent(g1,g-3)
    c: PointOnObject(g0,g-4)
    c: Coincident(g2,g0)
    c: PointOnObject(g2,g-4)
    c: Coincident(g3,g1)
    c: Horizontal(g3)
    c: Coincident(g3,g2)
    c: DistanceY(g0,g-3) = 19
FEATURE [Part::Extrusion] Extrude084  label="Extrude084 - foro_areazione_alimentatore"
  Base = -> Sketch144
  Dir = (0,-1,2e-16)
  DirMode = 2
  FaceMakerClass = Part::FaceMakerBullseye
  FaceMakerMode = 3
  LengthFwd = 10
  LengthRev = 0
  Solid = true
  Symmetric = true
FEATURE [Part::Cut] Cut049
  Base = -> Cut048
  Refine = true
  Tool = -> Extrude084
FEATURE [Sketcher::SketchObject] Sketch145  label="foro_per_condesatore"
  ArcFitTolerance = 1e-06
  AttachmentSupport = -> [XZ_Plane]
  ExternalGeometry = -> [Sketch,Sketch139]
  FullyConstrained = true
  MakeInternals = false
  MapMode = 5
  Placement = pos=(0,0,0) rot=(1,0,0;1.5708rad)
  sketch-geometry (1):
    g0: Circle CenterX=-182.345 CenterY=7.02342 CenterZ=0 NormalX=0 NormalY=0 NormalZ=1 AngleXU=0 Radius=5.2
  constraints (3):
    c: Diameter(g0) = 10.4
    c: Tangent(g0,g-3)
    c: Tangent(g0,g-4)
FEATURE [Part::Extrusion] Extrude085  label="Extrude085 - foro_per_condesatore"
  Base = -> Sketch145
  Dir = (0,-1,2e-16)
  DirMode = 2
  FaceMakerClass = Part::FaceMakerBullseye
  FaceMakerMode = 3
  LengthFwd = 25.2
  LengthRev = 0
  Solid = true
  Symmetric = true
FEATURE [Part::Cut] Cut050
  Base = -> Cut049
  Refine = true
  Tool = -> Extrude085
FEATURE [Sketcher::SketchObject] Sketch146  label="scavo_pulsante_6x6_per_led_batteria"
  ArcFitTolerance = 1e-06
  AttachmentSupport = -> [XZ_Plane]
  ExternalGeometry = -> [Sketch016]
  FullyConstrained = true
  MakeInternals = false
  MapMode = 5
  Placement = pos=(0,0,0) rot=(1,0,0;1.5708rad)
  sketch-geometry (5):
    g0: LineSegment StartX=-216.643 StartY=-65.8316 StartZ=0 EndX=-216.643 EndY=-72.8316 EndZ=0
    g1: LineSegment StartX=-216.643 StartY=-72.8316 StartZ=0 EndX=-210.243 EndY=-72.8316 EndZ=0
    g2: LineSegment StartX=-210.243 StartY=-72.8316 StartZ=0 EndX=-210.243 EndY=-65.8316 EndZ=0
    g3: LineSegment StartX=-210.243 StartY=-65.8316 StartZ=0 EndX=-216.643 EndY=-65.8316 EndZ=0
    g4: GeomPoint [constr] X=-213.443 Y=-69.3316 Z=0
  constraints (13):
    c: Coincident(g0,g1)
    c: Coincident(g1,g2)
    c: Coincident(g2,g3)
    c: Coincident(g3,g0)
    c: Vertical(g0)
    c: Vertical(g2)
    c: Horizontal(g1)
    c: Horizontal(g3)
    c: Distance(g0,g2) = 6.4
    c: Distance(g1,g3) = 7
    c: Tangent(g1,g-3)
    c: Symmetric(g0,g2,g4)
    c: Vertical(g-3,g4)
FEATURE [Part::Extrusion] Extrude086  label="Extrude086 - scavo_pulsante_6x6_per_led_batteria"
  Base = -> Sketch146
  Dir = (0,-1,2e-16)
  DirMode = 2
  FaceMakerClass = Part::FaceMakerBullseye
  FaceMakerMode = 3
  LengthFwd = 4
  LengthRev = 0
  Placement = pos=(0,12.6,0) rot=(0,0,1;0rad)
  Solid = true
  Symmetric = false
FEATURE [Sketcher::SketchObject] Sketch147  label="scavo_led_stato_batteria"
  ArcFitTolerance = 1e-06
  AttachmentSupport = -> [XZ_Plane]
  ExternalGeometry = -> [Sketch016]
  FullyConstrained = true
  MakeInternals = false
  MapMode = 5
  Placement = pos=(0,0,0) rot=(1,0,0;1.5708rad)
  sketch-geometry (5):
    g0: LineSegment StartX=-215.843 StartY=-56.2316 StartZ=0 EndX=-215.843 EndY=-65.4316 EndZ=0
    g1: LineSegment StartX=-215.843 StartY=-65.4316 StartZ=0 EndX=-211.043 EndY=-65.4316 EndZ=0
    g2: LineSegment StartX=-211.043 StartY=-65.4316 StartZ=0 EndX=-211.043 EndY=-56.2316 EndZ=0
    g3: LineSegment StartX=-211.043 StartY=-56.2316 StartZ=0 EndX=-215.843 EndY=-56.2316 EndZ=0
    g4: GeomPoint [constr] X=-213.443 Y=-60.8316 Z=0
  constraints (13):
    c: Coincident(g0,g1)
    c: Coincident(g1,g2)
    c: Coincident(g2,g3)
    c: Coincident(g3,g0)
    c: Distance(g0,g2) = 4.8
    c: Distance(g1,g3) = 9.2
    c: Equal(g0,g2)
    c: Equal(g1,g3)
    c: Perpendicular(g3,g0)
    c: DistanceY(g-3,g0) = 11.4
    c: Vertical(g2)
    c: Symmetric(g0,g2,g4)
    c: Vertical(g4,g-3)
FEATURE [Part::Extrusion] Extrude087  label="Extrude087 - scavo_led_stato_batteria"
  Base = -> Sketch147
  Dir = (0,-1,2e-16)
  DirMode = 2
  FaceMakerClass = Part::FaceMakerBullseye
  FaceMakerMode = 3
  LengthFwd = 2.2
  LengthRev = 0
  Placement = pos=(0,12.6,0) rot=(0,0,1;0rad)
  Solid = true
  Symmetric = false
FEATURE [Sketcher::SketchObject] Sketch148
  ArcFitTolerance = 1e-06
  AttachmentSupport = -> [Pad016]
  ExternalGeometry = -> [Pad016]
  FullyConstrained = true
  MakeInternals = false
  MapMode = 5
  Placement = pos=(0,0,-80.4316) rot=(1,0,0;3.14159rad)
  sketch-geometry (8):
    g0: LineSegment StartX=-176.685 StartY=3.6 StartZ=0 EndX=-186.685 EndY=3.6 EndZ=0
    g1: LineSegment StartX=-176.685 StartY=3.6 StartZ=0 EndX=-176.685 EndY=-9e-16 EndZ=0
    g2: LineSegment [constr] StartX=-186.685 StartY=3.6 StartZ=0 EndX=-186.685 EndY=-9e-16 EndZ=0
    g3: ArcOfEllipse CenterX=-186.685 CenterY=-9e-16 CenterZ=0 NormalX=0 NormalY=0 NormalZ=1 MajorRadius=10 MinorRadius=3.6 AngleXU=0 StartAngle=0 EndAngle=1.5708
    g4: LineSegment [constr] StartX=-176.685 StartY=-1e-15 StartZ=0 EndX=-196.685 EndY=-1e-15 EndZ=0
    g5: LineSegment [constr] StartX=-186.685 StartY=3.6 StartZ=0 EndX=-186.685 EndY=-3.6 EndZ=0
    g6: GeomPoint [constr] X=-177.356 Y=-1e-15 Z=0
    g7: GeomPoint [constr] X=-196.015 Y=-1e-15 Z=0
  constraints (13):
    c: Distance(g0) = 10
    c: Coincident(g0,g-5)
    c: PointOnObject(g0,g-3)
    c: Coincident(g1,g0)
    c: Coincident(g1,g-5)
    c: Coincident(g2,g0)
    c: Vertical(g2)
    c: PointOnObject(g2,g-4)
    c: InternalAlignment(g4-g7 -> g3) x4
    c: Coincident(g3,g2)
    c: Coincident(g3,g0)
    c: Coincident(g3,g1)
    c: Horizontal(g4)
FEATURE [PartDesign::SubtractivePipe] SubtractivePipe004
  AuxilleryCurvelinear = true
  AuxillerySpineTangent = false
  BaseFeature = -> Pad016
  Binormal = (0,0,0)
  Mode = 0
  Profile = -> Sketch148
  Refine = true
  Spine = -> Pad016 [Edge253]
  SpineTangent = false
  Suppressed = false
  Transformation = 0
  Transition = 0
FEATURE [Sketcher::SketchObject] Sketch149
  ArcFitTolerance = 1e-06
  AttachmentSupport = -> [Pad016]
  ExternalGeometry = -> [Pad016]
  FullyConstrained = true
  MakeInternals = false
  MapMode = 5
  Placement = pos=(0,0,-80.4316) rot=(1,0,0;3.14159rad)
  sketch-geometry (8):
    g0: LineSegment StartX=-215.932 StartY=3.6 StartZ=0 EndX=-205.932 EndY=3.6 EndZ=0
    g1: LineSegment StartX=-215.932 StartY=3.6 StartZ=0 EndX=-215.932 EndY=-4e-16 EndZ=0
    g2: LineSegment [constr] StartX=-205.932 StartY=3.6 StartZ=0 EndX=-205.932 EndY=-9e-16 EndZ=0
    g3: ArcOfEllipse CenterX=-205.932 CenterY=-1e-15 CenterZ=0 NormalX=0 NormalY=0 NormalZ=1 MajorRadius=10 MinorRadius=3.6 AngleXU=-3.14159 StartAngle=4.71239 EndAngle=6.28319
    g4: LineSegment [constr] StartX=-215.932 StartY=-1e-15 StartZ=0 EndX=-195.932 EndY=-1e-15 EndZ=0
    g5: LineSegment [constr] StartX=-205.932 StartY=-3.6 StartZ=0 EndX=-205.932 EndY=3.6 EndZ=0
    g6: GeomPoint [constr] X=-215.262 Y=-2.1e-15 Z=0
    g7: GeomPoint [constr] X=-196.602 Y=-9e-16 Z=0
  constraints (13):
    c: Distance(g0) = 10
    c: Coincident(g0,g-5)
    c: PointOnObject(g0,g-5)
    c: Coincident(g1,g0)
    c: Coincident(g1,g-4)
    c: Coincident(g2,g0)
    c: Vertical(g2)
    c: PointOnObject(g2,g-3)
    c: InternalAlignment(g4-g7 -> g3) x4
    c: Coincident(g3,g2)
    c: Coincident(g3,g0)
    c: Coincident(g3,g1)
    c: Horizontal(g4)
FEATURE [PartDesign::SubtractivePipe] SubtractivePipe005
  AuxilleryCurvelinear = true
  AuxillerySpineTangent = false
  BaseFeature = -> SubtractivePipe004
  Binormal = (0,0,0)
  Mode = 0
  Profile = -> Sketch149
  Refine = true
  Spine = -> Pad016 [Edge251,Edge256,Edge255]
  SpineTangent = false
  Suppressed = false
  Transformation = 0
  Transition = 0
FEATURE [PartDesign::SubtractiveLoft] SubtractiveLoft002
  BaseFeature = -> SubtractivePipe005
  Closed = false
  Profile = -> Sketch129
  Refine = true
  Ruled = false
  Sections = -> [Sketch130]
  Suppressed = false
FEATURE [PartDesign::SubtractiveLoft] SubtractiveLoft003
  BaseFeature = -> SubtractiveLoft002
  Closed = false
  Profile = -> Clone2D001
  Refine = true
  Ruled = false
  Sections = -> [Sketch131]
  Suppressed = false
FEATURE [PartDesign::Chamfer] Chamfer010
  Angle = 45
  Base = -> SubtractiveLoft003 [Edge203,Edge204,Edge202,Edge201,Edge195]
  BaseFeature = -> SubtractiveLoft003
  ChamferType = 0
  FlipDirection = false
  Refine = true
  Size = 1.5
  Size2 = 1
  SupportTransform = false
  Suppressed = false
  UseAllEdges = false
FEATURE [PartDesign::Chamfer] Chamfer011
  Angle = 45
  Base = -> Chamfer010 [Edge15]
  BaseFeature = -> Chamfer010
  ChamferType = 0
  FlipDirection = false
  Refine = true
  Size = 1.6
  Size2 = 1
  SupportTransform = false
  Suppressed = false
  UseAllEdges = false
FEATURE [PartDesign::Chamfer] Chamfer012
  Angle = 45
  Base = -> Chamfer011 [Edge10]
  BaseFeature = -> Chamfer011
  ChamferType = 0
  FlipDirection = false
  Refine = true
  Size = 3.5
  Size2 = 1
  SupportTransform = false
  Suppressed = false
  UseAllEdges = false
FEATURE [PartDesign::Chamfer] Chamfer013
  Angle = 45
  Base = -> Chamfer012 [Edge94]
  BaseFeature = -> Chamfer012
  ChamferType = 0
  FlipDirection = false
  Refine = true
  Size = 1.9
  Size2 = 1
  SupportTransform = false
  Suppressed = false
  UseAllEdges = false
FEATURE [PartDesign::Fillet] Fillet007
  Base = -> Chamfer013 [Edge83]
  BaseFeature = -> Chamfer013
  Radius = 1.1
  Refine = true
  SupportTransform = false
  Suppressed = false
  UseAllEdges = false
FEATURE [PartDesign::Fillet] Fillet008
  Base = -> Fillet007 [Edge75]
  BaseFeature = -> Fillet007
  Radius = 1.9
  Refine = true
  SupportTransform = false
  Suppressed = false
  UseAllEdges = false
FEATURE [PartDesign::Pocket] Pocket011
  BaseFeature = -> Fillet008
  Direction = (0,1,-2e-16)
  Length = 0.8
  Length2 = 5
  Profile = -> Sketch132
  ReferenceAxis = -> Sketch132 [N_Axis]
  Refine = true
  Suppressed = false
  Type = 0
FEATURE [PartDesign::Pocket] Pocket012
  BaseFeature = -> Pocket011
  Direction = (0,1,0)
  Length = 1
  Length2 = 5
  Profile = -> ShapeString
  ReferenceAxis = -> ShapeString [N_Axis]
  Refine = true
  Suppressed = false
  Type = 0
FEATURE [Sketcher::SketchObject] Sketch150
  ArcFitTolerance = 1e-06
  AttachmentSupport = -> [Pad008]
  ExternalGeometry = -> [Pad008]
  FullyConstrained = true
  MakeInternals = false
  MapMode = 5
  Placement = pos=(0,3.6,0) rot=(0,0.707107,0.707107;3.14159rad)
  sketch-geometry (7):
    g0: LineSegment [constr] StartX=210.343 StartY=-66.0316 StartZ=0 EndX=210.343 EndY=-72.8316 EndZ=0
    g1: LineSegment [constr] StartX=210.343 StartY=-72.8316 StartZ=0 EndX=216.543 EndY=-72.8316 EndZ=0
    g2: LineSegment [constr] StartX=216.543 StartY=-72.8316 StartZ=0 EndX=216.543 EndY=-66.0316 EndZ=0
    g3: LineSegment [constr] StartX=216.543 StartY=-66.0316 StartZ=0 EndX=210.343 EndY=-66.0316 EndZ=0
    g4: LineSegment [constr] StartX=210.343 StartY=-72.8316 StartZ=0 EndX=216.543 EndY=-66.0316 EndZ=0
    g5: LineSegment [constr] StartX=210.343 StartY=-66.0316 StartZ=0 EndX=213.443 EndY=-69.4316 EndZ=0
    g6: Circle CenterX=213.443 CenterY=-69.4316 CenterZ=0 NormalX=0 NormalY=0 NormalZ=1 AngleXU=0 Radius=2
  constraints (18):
    c: Coincident(g0,g1)
    c: Coincident(g1,g2)
    c: Coincident(g2,g3)
    c: Coincident(g3,g0)
    c: Vertical(g0)
    c: Vertical(g2)
    c: Horizontal(g1)
    c: Horizontal(g3)
    c: Distance(g0,g2) = 6.2
    c: Distance(g1,g3) = 6.8
    c: DistanceY(g-3,g1) = 4
    c: Coincident(g4,g0)
    c: Coincident(g4,g2)
    c: Coincident(g5,g0)
    c: Symmetric(g0,g2,g5)
    c: Diameter(g6) = 4
    c: Coincident(g6,g5)
    c: Vertical(g5,g-3)
FEATURE [Sketcher::SketchObject] Sketch151
  ArcFitTolerance = 1e-06
  AttachmentSupport = -> [Pad008]
  ExternalGeometry = -> [Pad008]
  FullyConstrained = true
  MakeInternals = false
  MapMode = 5
  Placement = pos=(0,3.6,0) rot=(0,0.707107,0.707107;3.14159rad)
  sketch-geometry (10):
    g0: LineSegment [constr] StartX=211.143 StartY=-56.2316 StartZ=0 EndX=211.143 EndY=-65.4316 EndZ=0
    g1: LineSegment [constr] StartX=211.143 StartY=-65.4316 StartZ=0 EndX=215.743 EndY=-65.4316 EndZ=0
    g2: LineSegment [constr] StartX=215.743 StartY=-65.4316 StartZ=0 EndX=215.743 EndY=-56.2316 EndZ=0
    g3: LineSegment [constr] StartX=215.743 StartY=-56.2316 StartZ=0 EndX=211.143 EndY=-56.2316 EndZ=0
    g4: LineSegment StartX=212.243 StartY=-63.8316 StartZ=0 EndX=214.643 EndY=-63.8316 EndZ=0
    g5: LineSegment StartX=214.643 StartY=-63.8316 StartZ=0 EndX=214.643 EndY=-57.0316 EndZ=0
    g6: LineSegment StartX=214.643 StartY=-57.0316 StartZ=0 EndX=212.243 EndY=-57.0316 EndZ=0
    g7: LineSegment StartX=212.243 StartY=-57.0316 StartZ=0 EndX=212.243 EndY=-63.8316 EndZ=0
    g8: GeomPoint [constr] X=213.443 Y=-60.4316 Z=0
    g9: GeomPoint [constr] X=213.443 Y=-60.8316 Z=0
  constraints (26):
    c: Coincident(g0,g1)
    c: Coincident(g1,g2)
    c: Coincident(g2,g3)
    c: Coincident(g3,g0)
    c: Vertical(g0)
    c: Vertical(g2)
    c: Horizontal(g1)
    c: Horizontal(g3)
    c: Distance(g0,g2) = 4.6
    c: Distance(g1,g3) = 9.2
    c: DistanceY(g-3,g1) = 11.4
    c: Coincident(g4,g5)
    c: Coincident(g5,g6)
    c: Coincident(g6,g7)
    c: Coincident(g7,g4)
    c: Horizontal(g4)
    c: Horizontal(g6)
    c: Vertical(g5)
    c: Vertical(g7)
    c: Symmetric(g6,g4,g8)
    c: Distance(g5,g7) = 2.4
    c: Distance(g4,g6) = 6.8
    c: Symmetric(g2,g0,g9)
    c: Vertical(g8,g9)
    c: DistanceY(g1,g4) = 1.6
    c: Vertical(g9,g-3)
FEATURE [PartDesign::Pocket] Pocket019
  BaseFeature = -> Pocket013
  Direction = (0,-1,2e-16)
  Length = 3.6
  Length2 = 5
  Profile = -> Sketch151
  ReferenceAxis = -> Sketch151 [N_Axis]
  Refine = true
  Suppressed = false
  Type = 0
FEATURE [PartDesign::Pocket] Pocket018
  BaseFeature = -> Pocket019
  Direction = (0,-1,2e-16)
  Length = 3.6
  Length2 = 5
  Profile = -> Sketch150
  ReferenceAxis = -> Sketch150 [N_Axis]
  Refine = true
  Suppressed = false
  Type = 0
FEATURE [PartDesign::Point] DatumPoint
  AttacherType = Attacher::AttachEnginePoint
  AttachmentSupport = -> [Sketch150]
  MapMode = 36
  Placement = pos=(-213.443,3.6,-69.4316) rot=(0,1,0;3.14159rad)
FEATURE [PartDesign::Plane] DatumPlane002
  AttachmentSupport = -> [DatumPoint]
  Length = 260.281
  MapMode = 1
  Placement = pos=(-213.443,3.6,-69.4316) rot=(0,0,1;0rad)
  ResizeMode = 0
  Width = 71.8377
FEATURE [Sketcher::SketchObject] Sketch152
  ArcFitTolerance = 1e-06
  AttachmentSupport = -> [DatumPlane002]
  ExternalGeometry = -> [Sketch150]
  FullyConstrained = true
  MakeInternals = false
  MapMode = 5
  Placement = pos=(-213.443,3.6,-69.4316) rot=(0,0,1;0rad)
  sketch-geometry (7):
    g0: LineSegment StartX=0 StartY=0 StartZ=0 EndX=-4 EndY=5.1e-15 EndZ=0
    g1: ArcOfEllipse CenterX=0 CenterY=0 CenterZ=0 NormalX=0 NormalY=0 NormalZ=1 MajorRadius=4 MinorRadius=3.6 AngleXU=3.14159 StartAngle=2e-16 EndAngle=1.5708
    g2: LineSegment [constr] StartX=-4 StartY=9e-16 StartZ=0 EndX=4 EndY=-9e-16 EndZ=0
    g3: LineSegment [constr] StartX=0 StartY=-3.6 StartZ=0 EndX=0 EndY=3.6 EndZ=0
    g4: GeomPoint [constr] X=-1.74356 Y=2.5e-15 Z=0
    g5: GeomPoint [constr] X=1.74356 Y=-2e-15 Z=0
    g6: LineSegment StartX=0 StartY=0 StartZ=0 EndX=-5.5e-15 EndY=-3.6 EndZ=0
  constraints (11):
    c: PointOnObject(g1,g-2)
    c: Distance(g0) = 4
    c: PointOnObject(g0,g-1)
    c: InternalAlignment(g2-g5 -> g1) x4
    c: Coincident(g1,g0)
    c: Vertical(g3)
    c: Coincident(g1,g-1)
    c: Distance(g6) = 3.6
    c: Coincident(g6,g1)
    c: Coincident(g1,g6)
    c: Coincident(g0,g1)
FEATURE [PartDesign::Groove] Groove
  Angle = 360
  Angle2 = 60
  Axis = (0,1,0)
  Base = (-213.443,3.6,-69.4316)
  BaseFeature = -> Pocket018
  Profile = -> Sketch152
  ReferenceAxis = -> Sketch152 [V_Axis]
  Refine = true
  Reversed = true
  Suppressed = false
  Type = 0
FEATURE [PartDesign::Body] Body006  label="lato SX"
  AllowCompound = false
  Group = -> [Binder,Pad019,Chamfer015,Pocket002,Sketch133,Sketch091,Pad005,Sketch092,Pocket001,Sketch093,Sketch094,Pad006,Sketch095,Pad007,Sketch096,Pad008,Sketch097,Pad009,Chamfer005,Pocket004,Sketch098,Pad010,Chamfer006,Pocket003,SubtractivePipe,SubtractivePipe001,Sketch099,Sketch106,Sketch107,Sketch108,Clone2D,Sketch109,SubtractiveLoft,SubtractiveLoft001,Sketch110,Sketch111,Sketch112,Chamfer016,Chamfer017,+15 more]
  Origin = -> Origin006
  Tip = -> Groove
FEATURE [Sketcher::SketchObject] Sketch153  label="ripieno_per_sostegno_led_batteria"
  ArcFitTolerance = 1e-06
  AttachmentSupport = -> [XZ_Plane]
  ExternalGeometry = -> [Sketch036]
  FullyConstrained = true
  MakeInternals = false
  MapMode = 5
  Placement = pos=(0,0,0) rot=(1,0,0;1.5708rad)
  sketch-geometry (4):
    g0: LineSegment StartX=-217.343 StartY=-54.5944 StartZ=0 EndX=-217.343 EndY=-63.1944 EndZ=0
    g1: LineSegment StartX=-217.343 StartY=-63.1944 StartZ=0 EndX=-211.843 EndY=-63.1944 EndZ=0
    g2: LineSegment StartX=-211.843 StartY=-63.1944 StartZ=0 EndX=-211.843 EndY=-54.5944 EndZ=0
    g3: LineSegment StartX=-211.843 StartY=-54.5944 StartZ=0 EndX=-217.343 EndY=-54.5944 EndZ=0
  constraints (11):
    c: Coincident(g0,g1)
    c: Coincident(g1,g2)
    c: Coincident(g2,g3)
    c: Coincident(g3,g0)
    c: Vertical(g0)
    c: Horizontal(g1)
    c: Horizontal(g3)
    c: Tangent(g2,g-3)
    c: DistanceY(g2,g-3) = 4.5
    c: DistanceX(g3,g3) = 5.5
    c: DistanceY(g0,g0) = 8.6
FEATURE [Part::Extrusion] Extrude088  label="Extrude088 - ripieno_per_sostegno_led_batteria"
  Base = -> Sketch153
  Dir = (0,-1,2e-16)
  DirMode = 2
  FaceMakerClass = Part::FaceMakerBullseye
  FaceMakerMode = 3
  LengthFwd = 4
  LengthRev = 0
  Placement = pos=(0,12.6,0) rot=(0,0,1;0rad)
  Solid = true
  Symmetric = false
FEATURE [Part::MultiFuse] Fusion004
  Refine = true
  Shapes = -> [Cut050,Extrude088]
FEATURE [Part::Cut] Cut051
  Base = -> Fusion004
  Refine = true
  Tool = -> Extrude087
FEATURE [Part::Cut] Cut052
  Base = -> Cut051
  Refine = true
  Tool = -> Extrude086
FEATURE [Sketcher::SketchObject] Sketch154
  ArcFitTolerance = 1e-06
  AttachmentSupport = -> [Pad016]
  ExternalGeometry = -> [Binder001]
  FullyConstrained = true
  MakeInternals = false
  MapMode = 5
  Placement = pos=(0,-3.6,0) rot=(1,0,0;1.5708rad)
  sketch-geometry (25):
    g0: LineSegment StartX=-214.643 StartY=-72.4316 StartZ=0 EndX=-212.243 EndY=-72.4316 EndZ=0
    g1: LineSegment StartX=-212.243 StartY=-72.4316 StartZ=0 EndX=-212.243 EndY=-71.2316 EndZ=0
    g2: LineSegment StartX=-212.243 StartY=-71.2316 StartZ=0 EndX=-214.643 EndY=-71.2316 EndZ=0
    g3: LineSegment StartX=-214.643 StartY=-71.2316 StartZ=0 EndX=-214.643 EndY=-72.4316 EndZ=0
    g4: GeomPoint [constr] X=-213.443 Y=-71.8316 Z=0
    g5: LineSegment StartX=-214.643 StartY=-69.6316 StartZ=0 EndX=-212.243 EndY=-69.6316 EndZ=0
    g6: LineSegment StartX=-212.243 StartY=-69.6316 StartZ=0 EndX=-212.243 EndY=-68.4316 EndZ=0
    g7: LineSegment StartX=-212.243 StartY=-68.4316 StartZ=0 EndX=-214.643 EndY=-68.4316 EndZ=0
    g8: LineSegment StartX=-214.643 StartY=-68.4316 StartZ=0 EndX=-214.643 EndY=-69.6316 EndZ=0
    g9: GeomPoint [constr] X=-213.443 Y=-69.0316 Z=0
    g10: LineSegment StartX=-214.643 StartY=-66.8316 StartZ=0 EndX=-212.243 EndY=-66.8316 EndZ=0
    g11: LineSegment StartX=-212.243 StartY=-66.8316 StartZ=0 EndX=-212.243 EndY=-65.6316 EndZ=0
    g12: LineSegment StartX=-212.243 StartY=-65.6316 StartZ=0 EndX=-214.643 EndY=-65.6316 EndZ=0
    g13: LineSegment StartX=-214.643 StartY=-65.6316 StartZ=0 EndX=-214.643 EndY=-66.8316 EndZ=0
    g14: GeomPoint [constr] X=-213.443 Y=-66.2316 Z=0
    g15: LineSegment StartX=-214.643 StartY=-64.0316 StartZ=0 EndX=-212.243 EndY=-64.0316 EndZ=0
    g16: LineSegment StartX=-212.243 StartY=-64.0316 StartZ=0 EndX=-212.243 EndY=-62.8316 EndZ=0
    g17: LineSegment StartX=-212.243 StartY=-62.8316 StartZ=0 EndX=-214.643 EndY=-62.8316 EndZ=0
    g18: LineSegment StartX=-214.643 StartY=-62.8316 StartZ=0 EndX=-214.643 EndY=-64.0316 EndZ=0
    g19: GeomPoint [constr] X=-213.443 Y=-63.4316 Z=0
    g20: LineSegment StartX=-214.643 StartY=-61.2316 StartZ=0 EndX=-212.243 EndY=-61.2316 EndZ=0
    g21: LineSegment StartX=-212.243 StartY=-61.2316 StartZ=0 EndX=-212.243 EndY=-60.0316 EndZ=0
    g22: LineSegment StartX=-212.243 StartY=-60.0316 StartZ=0 EndX=-214.643 EndY=-60.0316 EndZ=0
    g23: LineSegment StartX=-214.643 StartY=-60.0316 StartZ=0 EndX=-214.643 EndY=-61.2316 EndZ=0
    g24: GeomPoint [constr] X=-213.443 Y=-60.6316 Z=0
  constraints (65):
    c: Coincident(g0,g1)
    c: Coincident(g1,g2)
    c: Coincident(g2,g3)
    c: Coincident(g3,g0)
    c: Horizontal(g0)
    c: Horizontal(g2)
    c: Vertical(g1)
    c: Vertical(g3)
    c: Symmetric(g2,g0,g4)
    c: Distance(g1,g3) = 2.4
    c: Distance(g0,g2) = 1.2
    c: Coincident(g5,g6)
    c: Coincident(g6,g7)
    c: Coincident(g7,g8)
    c: Coincident(g8,g5)
    c: Horizontal(g5)
    c: Horizontal(g7)
    c: Vertical(g6)
    c: Vertical(g8)
    c: Symmetric(g7,g5,g9)
    c: Distance(g6,g8) = 2.4
    c: Distance(g5,g7) = 1.2
    c: Coincident(g10,g11)
    c: Coincident(g11,g12)
    c: Coincident(g12,g13)
    c: Coincident(g13,g10)
    c: Horizontal(g10)
    c: Horizontal(g12)
    c: Vertical(g11)
    c: Vertical(g13)
    c: Symmetric(g12,g10,g14)
    c: Distance(g11,g13) = 2.4
    c: Distance(g10,g12) = 1.2
    c: Coincident(g15,g16)
    c: Coincident(g16,g17)
    c: Coincident(g17,g18)
    c: Coincident(g18,g15)
    c: Horizontal(g15)
    c: Horizontal(g17)
    c: Vertical(g16)
    c: Vertical(g18)
    c: Symmetric(g17,g15,g19)
    c: Distance(g16,g18) = 2.4
    c: Distance(g15,g17) = 1.2
    c: Vertical(g4,g-3)
    c: Vertical(g9,g-3)
    c: Vertical(g14,g-3)
    c: Vertical(g19,g-3)
    c: DistanceY(g-3,g4) = 5
    c: DistanceY(g4,g9) = 2.8
    c: DistanceY(g9,g14) = 2.8
    c: DistanceY(g14,g19) = 2.8
    c: Coincident(g20,g21)
    c: Coincident(g21,g22)
    c: Coincident(g22,g23)
    c: Coincident(g23,g20)
    c: Horizontal(g20)
    c: Horizontal(g22)
    c: Vertical(g21)
    c: Vertical(g23)
    c: Symmetric(g22,g20,g24)
    c: Distance(g21,g23) = 2.4
    c: Distance(g20,g22) = 1.2
    c: DistanceY(g19,g24) = 2.8
    c: Vertical(g-3,g24)
FEATURE [PartDesign::Pocket] Pocket020
  BaseFeature = -> Pocket012
  Direction = (0,1,-2e-16)
  Length = 3.6
  Length2 = 5
  Profile = -> Sketch154
  ReferenceAxis = -> Sketch154 [N_Axis]
  Refine = true
  Suppressed = false
  Type = 0
FEATURE [PartDesign::Body] Body007  label="lato DX"
  AllowCompound = false
  Group = -> [Binder001,Sketch114,Pad011,Chamfer014,Sketch115,Pocket006,Sketch116,Pad012,Sketch117,Pocket007,Sketch118,Pad013,Sketch119,Pocket008,Pad017,Chamfer009,Pocket009,Sketch123,Sketch120,Pad014,Pad018,Chamfer008,Pocket010,Sketch121,Pad015,Sketch122,Pad016,SubtractivePipe004,SubtractivePipe005,Sketch149,Sketch148,Sketch124,Sketch125,Sketch126,Sketch129,Sketch130,Clone2D001,Sketch131,SubtractiveLoft002,+13 more]
  Origin = -> Origin007
  Tip = -> Pocket020
FEATURE [Sketcher::SketchObject] Sketch155  label="fermo per protezione batteria"
  ArcFitTolerance = 1e-06
  AttachmentSupport = -> [XZ_Plane]
  ExternalGeometry = -> [Sketch016,Sketch]
  FullyConstrained = true
  MakeInternals = false
  MapMode = 5
  Placement = pos=(0,0,0) rot=(1,0,0;1.5708rad)
  sketch-geometry (8):
    g0: LineSegment StartX=-183.305 StartY=-72.0316 StartZ=0 EndX=-183.305 EndY=-76.8316 EndZ=0
    g1: LineSegment StartX=-179.305 StartY=-68.8316 StartZ=0 EndX=-179.305 EndY=-72.8316 EndZ=0
    g2: LineSegment StartX=-183.305 StartY=-76.8316 StartZ=0 EndX=-179.305 EndY=-72.8316 EndZ=0
    g3: LineSegment StartX=-179.305 StartY=-68.8316 StartZ=0 EndX=-183.305 EndY=-68.8316 EndZ=0
    g4: LineSegment StartX=-183.305 StartY=-72.0316 StartZ=0 EndX=-181.305 EndY=-72.0316 EndZ=0
    g5: LineSegment StartX=-181.305 StartY=-72.0316 StartZ=0 EndX=-181.305 EndY=-70.4316 EndZ=0
    g6: LineSegment StartX=-181.305 StartY=-70.4316 StartZ=0 EndX=-183.305 EndY=-70.4316 EndZ=0
    g7: LineSegment StartX=-183.305 StartY=-70.4316 StartZ=0 EndX=-183.305 EndY=-68.8316 EndZ=0
  constraints (24):
    c: Vertical(g0)
    c: Horizontal(g0,g-3)
    c: Tangent(g0,g-3)
    c: Vertical(g1)
    c: Vertical(g1,g-3)
    c: PointOnObject(g1,g-3)
    c: Coincident(g2,g0)
    c: Coincident(g2,g1)
    c: Coincident(g3,g1)
    c: Horizontal(g3)
    c: Distance(g4) = 2
    c: Coincident(g4,g0)
    c: Horizontal(g4)
    c: Vertical(g3,g0)
    c: Distance(g5) = 1.6
    c: Coincident(g5,g4)
    c: Vertical(g5)
    c: Coincident(g6,g5)
    c: Horizontal(g6)
    c: Coincident(g7,g6)
    c: Coincident(g7,g3)
    c: Vertical(g7)
    c: DistanceY(g7,g7) = 1.6
    c: DistanceY(g1,g4) = 0.8
FEATURE [Part::Extrusion] Extrude089  label="Extrude089 - fermo per protezione batteria"
  Base = -> Sketch155
  Dir = (0,-1,2e-16)
  DirMode = 2
  FaceMakerClass = Part::FaceMakerBullseye
  FaceMakerMode = 3
  LengthFwd = 12
  LengthRev = 0
  Solid = true
  Symmetric = true
FEATURE [Sketcher::SketchObject] Sketch156  label="buco per protezione batteria"
  ArcFitTolerance = 1e-06
  AttachmentSupport = -> [XZ_Plane]
  ExternalGeometry = -> [Sketch,Sketch016]
  FullyConstrained = true
  MakeInternals = false
  MapMode = 5
  Placement = pos=(0,0,0) rot=(1,0,0;1.5708rad)
  sketch-geometry (5):
    g0: LineSegment [constr] StartX=-183.305 StartY=-76.8316 StartZ=0 EndX=-183.305 EndY=-78.4316 EndZ=0
    g1: LineSegment StartX=-200.305 StartY=-78.4316 StartZ=0 EndX=-200.305 EndY=-80.4316 EndZ=0
    g2: LineSegment StartX=-200.305 StartY=-80.4316 StartZ=0 EndX=-198.505 EndY=-80.4316 EndZ=0
    g3: LineSegment StartX=-198.505 StartY=-80.4316 StartZ=0 EndX=-198.505 EndY=-78.4316 EndZ=0
    g4: LineSegment StartX=-198.505 StartY=-78.4316 StartZ=0 EndX=-200.305 EndY=-78.4316 EndZ=0
  constraints (15):
    c: Vertical(g0)
    c: Tangent(g0,g-4)
    c: PointOnObject(g0,g-3)
    c: Horizontal(g0,g-4)
    c: Coincident(g1,g2)
    c: Coincident(g2,g3)
    c: Coincident(g3,g4)
    c: Coincident(g4,g1)
    c: Vertical(g1)
    c: Vertical(g3)
    c: Horizontal(g2)
    c: Distance(g1,g3) = 1.8
    c: Distance(g2,g4) = 2
    c: Tangent(g4,g-3)
    c: Distance(g3,g0) = 15.2
FEATURE [PartDesign::Body] Body  label="Struttura pistola"
  AllowCompound = false
  Group = -> [Sketch,Sketch002,Sketch004,DatumPlane,Sketch005,DatumPlane001,CopyCut,Sketch008,Sketch009,Sketch010,Sketch011,Sketch012,Sketch013,Sketch014,Sketch015,Sketch016,Sketch017,Sketch018,Sketch019,Sketch020,Sketch022,Sketch023,Sketch024,Sketch025,Sketch026,Sketch027,Sketch029,Sketch030,Sketch031,Sketch032,Sketch033,Sketch034,Sketch035,Sketch036,Sketch037,Sketch038,Sketch039,Sketch040,Sketch041,Sketch042,+30 more]
  Origin = -> Origin
FEATURE [Part::Extrusion] Extrude090  label="Extrude090 - buco per protezione batteria"
  Base = -> Sketch156
  Dir = (0,-1,2e-16)
  DirMode = 2
  FaceMakerClass = Part::FaceMakerBullseye
  FaceMakerMode = 3
  LengthFwd = 4.8
  LengthRev = 0
  Solid = true
  Symmetric = true
note: 2 file-system paths scrubbed to <path> (originals preserved in the JSON sidecar)
